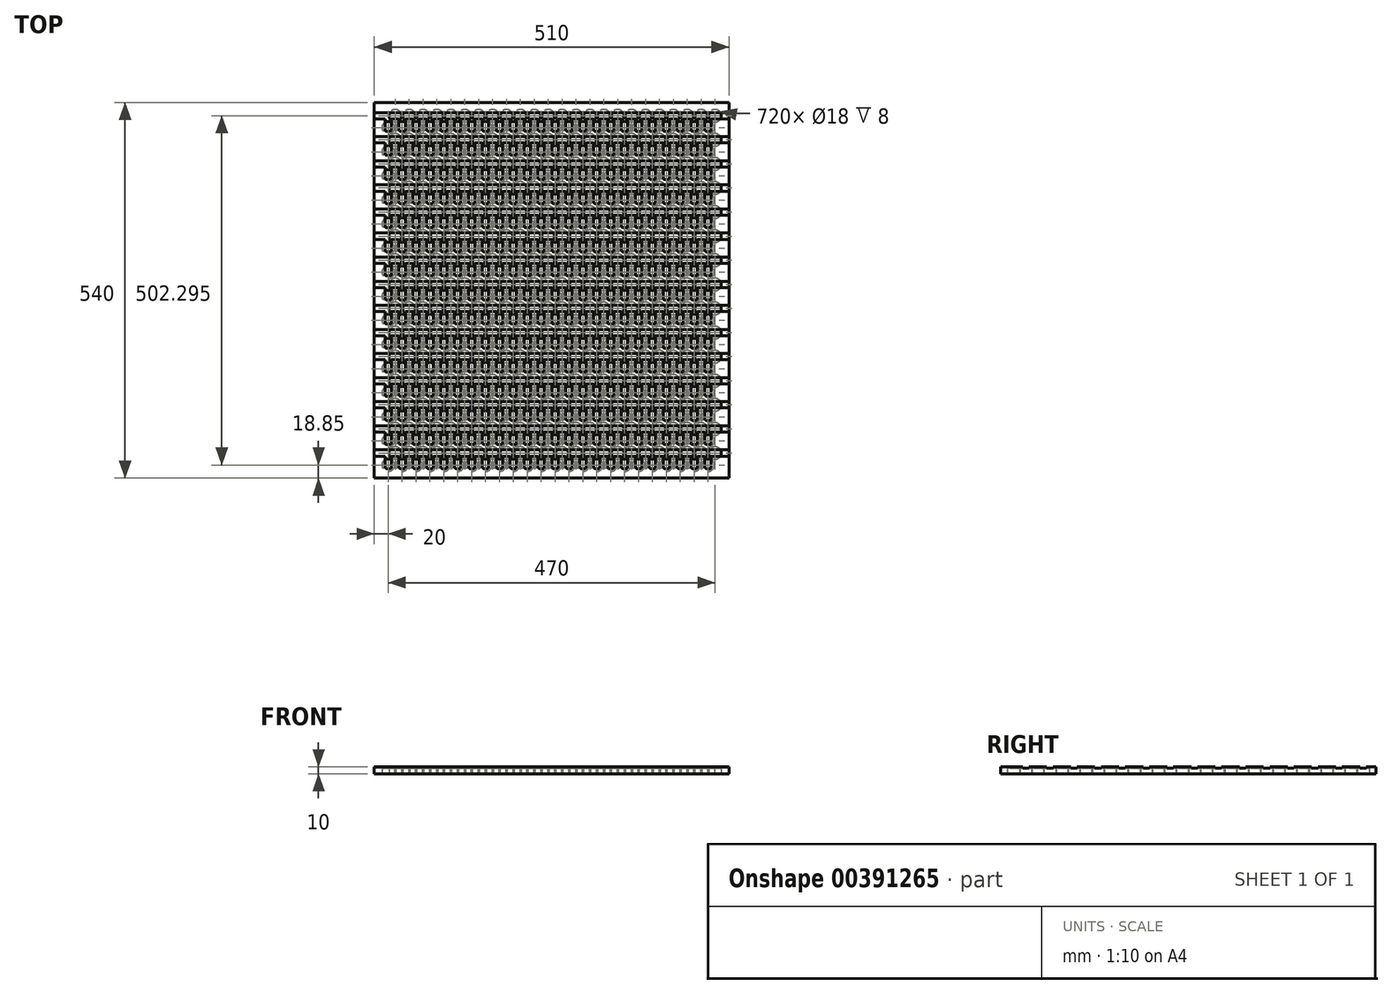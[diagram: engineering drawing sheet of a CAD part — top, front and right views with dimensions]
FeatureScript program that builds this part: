
annotation { "Feature Type Name" : "Feature", "Feature Type Description" : "" }
export const myFeature = defineFeature(function(context is Context, id is Id, definition is map)
    precondition{}
    {
        {
            var Q0;
            Q0=qCreatedBy(makeId("Top.planeOp"),FACE);
            var sketch = newSketch(context, id + "F0", { "sketchPlane" : qUnion([Q0])});
            skCircle(sketch, "E0", {"center": v(0, 0) * mm, "radius": 9 * mm});
            skCircle(sketch, "E1.1.0.0", {"center": v(20, 0) * mm, "radius": 9 * mm});
            skCircle(sketch, "E1.2.0.0", {"center": v(40, 0) * mm, "radius": 9 * mm});
            skCircle(sketch, "E1.3.0.0", {"center": v(60, 0) * mm, "radius": 9 * mm});
            skCircle(sketch, "E1.4.0.0", {"center": v(80, 0) * mm, "radius": 9 * mm});
            skCircle(sketch, "E1.5.0.0", {"center": v(100, 0) * mm, "radius": 9 * mm});
            skCircle(sketch, "E1.6.0.0", {"center": v(120, 0) * mm, "radius": 9 * mm});
            skCircle(sketch, "E1.7.0.0", {"center": v(140, 0) * mm, "radius": 9 * mm});
            skCircle(sketch, "E1.8.0.0", {"center": v(160, 0) * mm, "radius": 9 * mm});
            skCircle(sketch, "E1.9.0.0", {"center": v(180, 0) * mm, "radius": 9 * mm});
            skCircle(sketch, "E1.10.0.0", {"center": v(200, 0) * mm, "radius": 9 * mm});
            skCircle(sketch, "E1.11.0.0", {"center": v(220, 0) * mm, "radius": 9 * mm});
            skCircle(sketch, "E1.12.0.0", {"center": v(240, 0) * mm, "radius": 9 * mm});
            skCircle(sketch, "E1.13.0.0", {"center": v(260, 0) * mm, "radius": 9 * mm});
            skCircle(sketch, "E1.14.0.0", {"center": v(280, 0) * mm, "radius": 9 * mm});
            skCircle(sketch, "E1.15.0.0", {"center": v(300, 0) * mm, "radius": 9 * mm});
            skCircle(sketch, "E1.16.0.0", {"center": v(320, 0) * mm, "radius": 9 * mm});
            skCircle(sketch, "E1.17.0.0", {"center": v(340, 0) * mm, "radius": 9 * mm});
            skCircle(sketch, "E1.18.0.0", {"center": v(360, 0) * mm, "radius": 9 * mm});
            skCircle(sketch, "E1.19.0.0", {"center": v(380, 0) * mm, "radius": 9 * mm});
            skCircle(sketch, "E1.20.0.0", {"center": v(400, 0) * mm, "radius": 9 * mm});
            skCircle(sketch, "E1.21.0.0", {"center": v(420, 0) * mm, "radius": 9 * mm});
            skCircle(sketch, "E1.22.0.0", {"center": v(440, 0) * mm, "radius": 9 * mm});
            skCircle(sketch, "E1.23.0.0", {"center": v(460, 0) * mm, "radius": 9 * mm});
            skLineSegment(sketch, "E1.direction1", {"start": v(0, 0) * mm, "end": v(20, 0) * mm, "construction": true});
            skCircle(sketch, "E2", {"center": v(10, 17.32) * mm, "radius": 9 * mm});
            skCircle(sketch, "E3.1.0.0", {"center": v(30, 17.32) * mm, "radius": 9 * mm});
            skCircle(sketch, "E3.2.0.0", {"center": v(50, 17.32) * mm, "radius": 9 * mm});
            skCircle(sketch, "E3.3.0.0", {"center": v(70, 17.32) * mm, "radius": 9 * mm});
            skCircle(sketch, "E3.4.0.0", {"center": v(90, 17.32) * mm, "radius": 9 * mm});
            skCircle(sketch, "E3.5.0.0", {"center": v(110, 17.32) * mm, "radius": 9 * mm});
            skCircle(sketch, "E3.6.0.0", {"center": v(130, 17.32) * mm, "radius": 9 * mm});
            skCircle(sketch, "E3.7.0.0", {"center": v(150, 17.32) * mm, "radius": 9 * mm});
            skCircle(sketch, "E3.8.0.0", {"center": v(170, 17.32) * mm, "radius": 9 * mm});
            skCircle(sketch, "E3.9.0.0", {"center": v(190, 17.32) * mm, "radius": 9 * mm});
            skCircle(sketch, "E3.10.0.0", {"center": v(210, 17.32) * mm, "radius": 9 * mm});
            skCircle(sketch, "E3.11.0.0", {"center": v(230, 17.32) * mm, "radius": 9 * mm});
            skCircle(sketch, "E3.12.0.0", {"center": v(250, 17.32) * mm, "radius": 9 * mm});
            skCircle(sketch, "E3.13.0.0", {"center": v(270, 17.32) * mm, "radius": 9 * mm});
            skCircle(sketch, "E3.14.0.0", {"center": v(290, 17.32) * mm, "radius": 9 * mm});
            skCircle(sketch, "E3.15.0.0", {"center": v(310, 17.32) * mm, "radius": 9 * mm});
            skCircle(sketch, "E3.16.0.0", {"center": v(330, 17.32) * mm, "radius": 9 * mm});
            skCircle(sketch, "E3.17.0.0", {"center": v(350, 17.32) * mm, "radius": 9 * mm});
            skCircle(sketch, "E3.18.0.0", {"center": v(370, 17.32) * mm, "radius": 9 * mm});
            skCircle(sketch, "E3.19.0.0", {"center": v(390, 17.32) * mm, "radius": 9 * mm});
            skCircle(sketch, "E3.20.0.0", {"center": v(410, 17.32) * mm, "radius": 9 * mm});
            skCircle(sketch, "E3.21.0.0", {"center": v(430, 17.32) * mm, "radius": 9 * mm});
            skCircle(sketch, "E3.22.0.0", {"center": v(450, 17.32) * mm, "radius": 9 * mm});
            skCircle(sketch, "E3.23.0.0", {"center": v(470, 17.32) * mm, "radius": 9 * mm});
            skLineSegment(sketch, "E3.direction1", {"start": v(10, 17.32) * mm, "end": v(30, 17.32) * mm, "construction": true});
            skCircle(sketch, "E4.0.1.0", {"center": v(280, 34.64) * mm, "radius": 9 * mm});
            skCircle(sketch, "E4.0.1.1", {"center": v(260, 34.64) * mm, "radius": 9 * mm});
            skCircle(sketch, "E4.0.1.2", {"center": v(130, 51.96) * mm, "radius": 9 * mm});
            skCircle(sketch, "E4.0.1.3", {"center": v(60, 34.64) * mm, "radius": 9 * mm});
            skCircle(sketch, "E4.0.1.4", {"center": v(80, 34.64) * mm, "radius": 9 * mm});
            skCircle(sketch, "E4.0.1.5", {"center": v(100, 34.64) * mm, "radius": 9 * mm});
            skCircle(sketch, "E4.0.1.6", {"center": v(350, 51.96) * mm, "radius": 9 * mm});
            skCircle(sketch, "E4.0.1.7", {"center": v(0, 34.64) * mm, "radius": 9 * mm});
            skCircle(sketch, "E4.0.1.8", {"center": v(120, 34.64) * mm, "radius": 9 * mm});
            skCircle(sketch, "E4.0.1.9", {"center": v(30, 51.96) * mm, "radius": 9 * mm});
            skCircle(sketch, "E4.0.1.10", {"center": v(380, 34.64) * mm, "radius": 9 * mm});
            skCircle(sketch, "E4.0.1.11", {"center": v(140, 34.64) * mm, "radius": 9 * mm});
            skCircle(sketch, "E4.0.1.12", {"center": v(450, 51.96) * mm, "radius": 9 * mm});
            skCircle(sketch, "E4.0.1.13", {"center": v(160, 34.64) * mm, "radius": 9 * mm});
            skCircle(sketch, "E4.0.1.14", {"center": v(300, 34.64) * mm, "radius": 9 * mm});
            skCircle(sketch, "E4.0.1.15", {"center": v(40, 34.64) * mm, "radius": 9 * mm});
            skCircle(sketch, "E4.0.1.16", {"center": v(210, 51.96) * mm, "radius": 9 * mm});
            skCircle(sketch, "E4.0.1.17", {"center": v(330, 51.96) * mm, "radius": 9 * mm});
            skCircle(sketch, "E4.0.1.18", {"center": v(270, 51.96) * mm, "radius": 9 * mm});
            skCircle(sketch, "E4.0.1.19", {"center": v(440, 34.64) * mm, "radius": 9 * mm});
            skCircle(sketch, "E4.0.1.20", {"center": v(110, 51.96) * mm, "radius": 9 * mm});
            skCircle(sketch, "E4.0.1.21", {"center": v(250, 51.96) * mm, "radius": 9 * mm});
            skCircle(sketch, "E4.0.1.22", {"center": v(180, 34.64) * mm, "radius": 9 * mm});
            skCircle(sketch, "E4.0.1.23", {"center": v(430, 51.96) * mm, "radius": 9 * mm});
            skCircle(sketch, "E4.0.1.24", {"center": v(200, 34.64) * mm, "radius": 9 * mm});
            skCircle(sketch, "E4.0.1.25", {"center": v(420, 34.64) * mm, "radius": 9 * mm});
            skCircle(sketch, "E4.0.1.26", {"center": v(70, 51.96) * mm, "radius": 9 * mm});
            skCircle(sketch, "E4.0.1.27", {"center": v(390, 51.96) * mm, "radius": 9 * mm});
            skCircle(sketch, "E4.0.1.28", {"center": v(220, 34.64) * mm, "radius": 9 * mm});
            skCircle(sketch, "E4.0.1.29", {"center": v(190, 51.96) * mm, "radius": 9 * mm});
            skCircle(sketch, "E4.0.1.30", {"center": v(90, 51.96) * mm, "radius": 9 * mm});
            skCircle(sketch, "E4.0.1.31", {"center": v(230, 51.96) * mm, "radius": 9 * mm});
            skCircle(sketch, "E4.0.1.32", {"center": v(150, 51.96) * mm, "radius": 9 * mm});
            skCircle(sketch, "E4.0.1.33", {"center": v(470, 51.96) * mm, "radius": 9 * mm});
            skCircle(sketch, "E4.0.1.34", {"center": v(410, 51.96) * mm, "radius": 9 * mm});
            skCircle(sketch, "E4.0.1.35", {"center": v(50, 51.96) * mm, "radius": 9 * mm});
            skCircle(sketch, "E4.0.1.36", {"center": v(400, 34.64) * mm, "radius": 9 * mm});
            skCircle(sketch, "E4.0.1.37", {"center": v(240, 34.64) * mm, "radius": 9 * mm});
            skCircle(sketch, "E4.0.1.38", {"center": v(320, 34.64) * mm, "radius": 9 * mm});
            skCircle(sketch, "E4.0.1.39", {"center": v(370, 51.96) * mm, "radius": 9 * mm});
            skCircle(sketch, "E4.0.1.40", {"center": v(10, 51.96) * mm, "radius": 9 * mm});
            skCircle(sketch, "E4.0.1.41", {"center": v(290, 51.96) * mm, "radius": 9 * mm});
            skCircle(sketch, "E4.0.1.42", {"center": v(360, 34.64) * mm, "radius": 9 * mm});
            skCircle(sketch, "E4.0.1.43", {"center": v(460, 34.64) * mm, "radius": 9 * mm});
            skCircle(sketch, "E4.0.1.44", {"center": v(310, 51.96) * mm, "radius": 9 * mm});
            skCircle(sketch, "E4.0.1.45", {"center": v(340, 34.64) * mm, "radius": 9 * mm});
            skCircle(sketch, "E4.0.1.46", {"center": v(170, 51.96) * mm, "radius": 9 * mm});
            skCircle(sketch, "E4.0.1.47", {"center": v(20, 34.64) * mm, "radius": 9 * mm});
            skLineSegment(sketch, "E4.0.1.48", {"start": v(0, 34.64) * mm, "end": v(20, 34.64) * mm, "construction": true});
            skLineSegment(sketch, "E4.0.1.49", {"start": v(10, 51.96) * mm, "end": v(30, 51.96) * mm, "construction": true});
            skCircle(sketch, "E4.0.2.0", {"center": v(280, 69.28) * mm, "radius": 9 * mm});
            skCircle(sketch, "E4.0.2.1", {"center": v(260, 69.28) * mm, "radius": 9 * mm});
            skCircle(sketch, "E4.0.2.2", {"center": v(130, 86.6) * mm, "radius": 9 * mm});
            skCircle(sketch, "E4.0.2.3", {"center": v(60, 69.28) * mm, "radius": 9 * mm});
            skCircle(sketch, "E4.0.2.4", {"center": v(80, 69.28) * mm, "radius": 9 * mm});
            skCircle(sketch, "E4.0.2.5", {"center": v(100, 69.28) * mm, "radius": 9 * mm});
            skCircle(sketch, "E4.0.2.6", {"center": v(350, 86.6) * mm, "radius": 9 * mm});
            skCircle(sketch, "E4.0.2.7", {"center": v(0, 69.28) * mm, "radius": 9 * mm});
            skCircle(sketch, "E4.0.2.8", {"center": v(120, 69.28) * mm, "radius": 9 * mm});
            skCircle(sketch, "E4.0.2.9", {"center": v(30, 86.6) * mm, "radius": 9 * mm});
            skCircle(sketch, "E4.0.2.10", {"center": v(380, 69.28) * mm, "radius": 9 * mm});
            skCircle(sketch, "E4.0.2.11", {"center": v(140, 69.28) * mm, "radius": 9 * mm});
            skCircle(sketch, "E4.0.2.12", {"center": v(450, 86.6) * mm, "radius": 9 * mm});
            skCircle(sketch, "E4.0.2.13", {"center": v(160, 69.28) * mm, "radius": 9 * mm});
            skCircle(sketch, "E4.0.2.14", {"center": v(300, 69.28) * mm, "radius": 9 * mm});
            skCircle(sketch, "E4.0.2.15", {"center": v(40, 69.28) * mm, "radius": 9 * mm});
            skCircle(sketch, "E4.0.2.16", {"center": v(210, 86.6) * mm, "radius": 9 * mm});
            skCircle(sketch, "E4.0.2.17", {"center": v(330, 86.6) * mm, "radius": 9 * mm});
            skCircle(sketch, "E4.0.2.18", {"center": v(270, 86.6) * mm, "radius": 9 * mm});
            skCircle(sketch, "E4.0.2.19", {"center": v(440, 69.28) * mm, "radius": 9 * mm});
            skCircle(sketch, "E4.0.2.20", {"center": v(110, 86.6) * mm, "radius": 9 * mm});
            skCircle(sketch, "E4.0.2.21", {"center": v(250, 86.6) * mm, "radius": 9 * mm});
            skCircle(sketch, "E4.0.2.22", {"center": v(180, 69.28) * mm, "radius": 9 * mm});
            skCircle(sketch, "E4.0.2.23", {"center": v(430, 86.6) * mm, "radius": 9 * mm});
            skCircle(sketch, "E4.0.2.24", {"center": v(200, 69.28) * mm, "radius": 9 * mm});
            skCircle(sketch, "E4.0.2.25", {"center": v(420, 69.28) * mm, "radius": 9 * mm});
            skCircle(sketch, "E4.0.2.26", {"center": v(70, 86.6) * mm, "radius": 9 * mm});
            skCircle(sketch, "E4.0.2.27", {"center": v(390, 86.6) * mm, "radius": 9 * mm});
            skCircle(sketch, "E4.0.2.28", {"center": v(220, 69.28) * mm, "radius": 9 * mm});
            skCircle(sketch, "E4.0.2.29", {"center": v(190, 86.6) * mm, "radius": 9 * mm});
            skCircle(sketch, "E4.0.2.30", {"center": v(90, 86.6) * mm, "radius": 9 * mm});
            skCircle(sketch, "E4.0.2.31", {"center": v(230, 86.6) * mm, "radius": 9 * mm});
            skCircle(sketch, "E4.0.2.32", {"center": v(150, 86.6) * mm, "radius": 9 * mm});
            skCircle(sketch, "E4.0.2.33", {"center": v(470, 86.6) * mm, "radius": 9 * mm});
            skCircle(sketch, "E4.0.2.34", {"center": v(410, 86.6) * mm, "radius": 9 * mm});
            skCircle(sketch, "E4.0.2.35", {"center": v(50, 86.6) * mm, "radius": 9 * mm});
            skCircle(sketch, "E4.0.2.36", {"center": v(400, 69.28) * mm, "radius": 9 * mm});
            skCircle(sketch, "E4.0.2.37", {"center": v(240, 69.28) * mm, "radius": 9 * mm});
            skCircle(sketch, "E4.0.2.38", {"center": v(320, 69.28) * mm, "radius": 9 * mm});
            skCircle(sketch, "E4.0.2.39", {"center": v(370, 86.6) * mm, "radius": 9 * mm});
            skCircle(sketch, "E4.0.2.40", {"center": v(10, 86.6) * mm, "radius": 9 * mm});
            skCircle(sketch, "E4.0.2.41", {"center": v(290, 86.6) * mm, "radius": 9 * mm});
            skCircle(sketch, "E4.0.2.42", {"center": v(360, 69.28) * mm, "radius": 9 * mm});
            skCircle(sketch, "E4.0.2.43", {"center": v(460, 69.28) * mm, "radius": 9 * mm});
            skCircle(sketch, "E4.0.2.44", {"center": v(310, 86.6) * mm, "radius": 9 * mm});
            skCircle(sketch, "E4.0.2.45", {"center": v(340, 69.28) * mm, "radius": 9 * mm});
            skCircle(sketch, "E4.0.2.46", {"center": v(170, 86.6) * mm, "radius": 9 * mm});
            skCircle(sketch, "E4.0.2.47", {"center": v(20, 69.28) * mm, "radius": 9 * mm});
            skLineSegment(sketch, "E4.0.2.48", {"start": v(0, 69.28) * mm, "end": v(20, 69.28) * mm, "construction": true});
            skLineSegment(sketch, "E4.0.2.49", {"start": v(10, 86.6) * mm, "end": v(30, 86.6) * mm, "construction": true});
            skCircle(sketch, "E4.0.3.0", {"center": v(280, 103.92) * mm, "radius": 9 * mm});
            skCircle(sketch, "E4.0.3.1", {"center": v(260, 103.92) * mm, "radius": 9 * mm});
            skCircle(sketch, "E4.0.3.2", {"center": v(130, 121.24) * mm, "radius": 9 * mm});
            skCircle(sketch, "E4.0.3.3", {"center": v(60, 103.92) * mm, "radius": 9 * mm});
            skCircle(sketch, "E4.0.3.4", {"center": v(80, 103.92) * mm, "radius": 9 * mm});
            skCircle(sketch, "E4.0.3.5", {"center": v(100, 103.92) * mm, "radius": 9 * mm});
            skCircle(sketch, "E4.0.3.6", {"center": v(350, 121.24) * mm, "radius": 9 * mm});
            skCircle(sketch, "E4.0.3.7", {"center": v(0, 103.92) * mm, "radius": 9 * mm});
            skCircle(sketch, "E4.0.3.8", {"center": v(120, 103.92) * mm, "radius": 9 * mm});
            skCircle(sketch, "E4.0.3.9", {"center": v(30, 121.24) * mm, "radius": 9 * mm});
            skCircle(sketch, "E4.0.3.10", {"center": v(380, 103.92) * mm, "radius": 9 * mm});
            skCircle(sketch, "E4.0.3.11", {"center": v(140, 103.92) * mm, "radius": 9 * mm});
            skCircle(sketch, "E4.0.3.12", {"center": v(450, 121.24) * mm, "radius": 9 * mm});
            skCircle(sketch, "E4.0.3.13", {"center": v(160, 103.92) * mm, "radius": 9 * mm});
            skCircle(sketch, "E4.0.3.14", {"center": v(300, 103.92) * mm, "radius": 9 * mm});
            skCircle(sketch, "E4.0.3.15", {"center": v(40, 103.92) * mm, "radius": 9 * mm});
            skCircle(sketch, "E4.0.3.16", {"center": v(210, 121.24) * mm, "radius": 9 * mm});
            skCircle(sketch, "E4.0.3.17", {"center": v(330, 121.24) * mm, "radius": 9 * mm});
            skCircle(sketch, "E4.0.3.18", {"center": v(270, 121.24) * mm, "radius": 9 * mm});
            skCircle(sketch, "E4.0.3.19", {"center": v(440, 103.92) * mm, "radius": 9 * mm});
            skCircle(sketch, "E4.0.3.20", {"center": v(110, 121.24) * mm, "radius": 9 * mm});
            skCircle(sketch, "E4.0.3.21", {"center": v(250, 121.24) * mm, "radius": 9 * mm});
            skCircle(sketch, "E4.0.3.22", {"center": v(180, 103.92) * mm, "radius": 9 * mm});
            skCircle(sketch, "E4.0.3.23", {"center": v(430, 121.24) * mm, "radius": 9 * mm});
            skCircle(sketch, "E4.0.3.24", {"center": v(200, 103.92) * mm, "radius": 9 * mm});
            skCircle(sketch, "E4.0.3.25", {"center": v(420, 103.92) * mm, "radius": 9 * mm});
            skCircle(sketch, "E4.0.3.26", {"center": v(70, 121.24) * mm, "radius": 9 * mm});
            skCircle(sketch, "E4.0.3.27", {"center": v(390, 121.24) * mm, "radius": 9 * mm});
            skCircle(sketch, "E4.0.3.28", {"center": v(220, 103.92) * mm, "radius": 9 * mm});
            skCircle(sketch, "E4.0.3.29", {"center": v(190, 121.24) * mm, "radius": 9 * mm});
            skCircle(sketch, "E4.0.3.30", {"center": v(90, 121.24) * mm, "radius": 9 * mm});
            skCircle(sketch, "E4.0.3.31", {"center": v(230, 121.24) * mm, "radius": 9 * mm});
            skCircle(sketch, "E4.0.3.32", {"center": v(150, 121.24) * mm, "radius": 9 * mm});
            skCircle(sketch, "E4.0.3.33", {"center": v(470, 121.24) * mm, "radius": 9 * mm});
            skCircle(sketch, "E4.0.3.34", {"center": v(410, 121.24) * mm, "radius": 9 * mm});
            skCircle(sketch, "E4.0.3.35", {"center": v(50, 121.24) * mm, "radius": 9 * mm});
            skCircle(sketch, "E4.0.3.36", {"center": v(400, 103.92) * mm, "radius": 9 * mm});
            skCircle(sketch, "E4.0.3.37", {"center": v(240, 103.92) * mm, "radius": 9 * mm});
            skCircle(sketch, "E4.0.3.38", {"center": v(320, 103.92) * mm, "radius": 9 * mm});
            skCircle(sketch, "E4.0.3.39", {"center": v(370, 121.24) * mm, "radius": 9 * mm});
            skCircle(sketch, "E4.0.3.40", {"center": v(10, 121.24) * mm, "radius": 9 * mm});
            skCircle(sketch, "E4.0.3.41", {"center": v(290, 121.24) * mm, "radius": 9 * mm});
            skCircle(sketch, "E4.0.3.42", {"center": v(360, 103.92) * mm, "radius": 9 * mm});
            skCircle(sketch, "E4.0.3.43", {"center": v(460, 103.92) * mm, "radius": 9 * mm});
            skCircle(sketch, "E4.0.3.44", {"center": v(310, 121.24) * mm, "radius": 9 * mm});
            skCircle(sketch, "E4.0.3.45", {"center": v(340, 103.92) * mm, "radius": 9 * mm});
            skCircle(sketch, "E4.0.3.46", {"center": v(170, 121.24) * mm, "radius": 9 * mm});
            skCircle(sketch, "E4.0.3.47", {"center": v(20, 103.92) * mm, "radius": 9 * mm});
            skLineSegment(sketch, "E4.0.3.48", {"start": v(0, 103.92) * mm, "end": v(20, 103.92) * mm, "construction": true});
            skLineSegment(sketch, "E4.0.3.49", {"start": v(10, 121.24) * mm, "end": v(30, 121.24) * mm, "construction": true});
            skCircle(sketch, "E4.0.4.0", {"center": v(280, 138.56) * mm, "radius": 9 * mm});
            skCircle(sketch, "E4.0.4.1", {"center": v(260, 138.56) * mm, "radius": 9 * mm});
            skCircle(sketch, "E4.0.4.2", {"center": v(130, 155.88) * mm, "radius": 9 * mm});
            skCircle(sketch, "E4.0.4.3", {"center": v(60, 138.56) * mm, "radius": 9 * mm});
            skCircle(sketch, "E4.0.4.4", {"center": v(80, 138.56) * mm, "radius": 9 * mm});
            skCircle(sketch, "E4.0.4.5", {"center": v(100, 138.56) * mm, "radius": 9 * mm});
            skCircle(sketch, "E4.0.4.6", {"center": v(350, 155.88) * mm, "radius": 9 * mm});
            skCircle(sketch, "E4.0.4.7", {"center": v(0, 138.56) * mm, "radius": 9 * mm});
            skCircle(sketch, "E4.0.4.8", {"center": v(120, 138.56) * mm, "radius": 9 * mm});
            skCircle(sketch, "E4.0.4.9", {"center": v(30, 155.88) * mm, "radius": 9 * mm});
            skCircle(sketch, "E4.0.4.10", {"center": v(380, 138.56) * mm, "radius": 9 * mm});
            skCircle(sketch, "E4.0.4.11", {"center": v(140, 138.56) * mm, "radius": 9 * mm});
            skCircle(sketch, "E4.0.4.12", {"center": v(450, 155.88) * mm, "radius": 9 * mm});
            skCircle(sketch, "E4.0.4.13", {"center": v(160, 138.56) * mm, "radius": 9 * mm});
            skCircle(sketch, "E4.0.4.14", {"center": v(300, 138.56) * mm, "radius": 9 * mm});
            skCircle(sketch, "E4.0.4.15", {"center": v(40, 138.56) * mm, "radius": 9 * mm});
            skCircle(sketch, "E4.0.4.16", {"center": v(210, 155.88) * mm, "radius": 9 * mm});
            skCircle(sketch, "E4.0.4.17", {"center": v(330, 155.88) * mm, "radius": 9 * mm});
            skCircle(sketch, "E4.0.4.18", {"center": v(270, 155.88) * mm, "radius": 9 * mm});
            skCircle(sketch, "E4.0.4.19", {"center": v(440, 138.56) * mm, "radius": 9 * mm});
            skCircle(sketch, "E4.0.4.20", {"center": v(110, 155.88) * mm, "radius": 9 * mm});
            skCircle(sketch, "E4.0.4.21", {"center": v(250, 155.88) * mm, "radius": 9 * mm});
            skCircle(sketch, "E4.0.4.22", {"center": v(180, 138.56) * mm, "radius": 9 * mm});
            skCircle(sketch, "E4.0.4.23", {"center": v(430, 155.88) * mm, "radius": 9 * mm});
            skCircle(sketch, "E4.0.4.24", {"center": v(200, 138.56) * mm, "radius": 9 * mm});
            skCircle(sketch, "E4.0.4.25", {"center": v(420, 138.56) * mm, "radius": 9 * mm});
            skCircle(sketch, "E4.0.4.26", {"center": v(70, 155.88) * mm, "radius": 9 * mm});
            skCircle(sketch, "E4.0.4.27", {"center": v(390, 155.88) * mm, "radius": 9 * mm});
            skCircle(sketch, "E4.0.4.28", {"center": v(220, 138.56) * mm, "radius": 9 * mm});
            skCircle(sketch, "E4.0.4.29", {"center": v(190, 155.88) * mm, "radius": 9 * mm});
            skCircle(sketch, "E4.0.4.30", {"center": v(90, 155.88) * mm, "radius": 9 * mm});
            skCircle(sketch, "E4.0.4.31", {"center": v(230, 155.88) * mm, "radius": 9 * mm});
            skCircle(sketch, "E4.0.4.32", {"center": v(150, 155.88) * mm, "radius": 9 * mm});
            skCircle(sketch, "E4.0.4.33", {"center": v(470, 155.88) * mm, "radius": 9 * mm});
            skCircle(sketch, "E4.0.4.34", {"center": v(410, 155.88) * mm, "radius": 9 * mm});
            skCircle(sketch, "E4.0.4.35", {"center": v(50, 155.88) * mm, "radius": 9 * mm});
            skCircle(sketch, "E4.0.4.36", {"center": v(400, 138.56) * mm, "radius": 9 * mm});
            skCircle(sketch, "E4.0.4.37", {"center": v(240, 138.56) * mm, "radius": 9 * mm});
            skCircle(sketch, "E4.0.4.38", {"center": v(320, 138.56) * mm, "radius": 9 * mm});
            skCircle(sketch, "E4.0.4.39", {"center": v(370, 155.88) * mm, "radius": 9 * mm});
            skCircle(sketch, "E4.0.4.40", {"center": v(10, 155.88) * mm, "radius": 9 * mm});
            skCircle(sketch, "E4.0.4.41", {"center": v(290, 155.88) * mm, "radius": 9 * mm});
            skCircle(sketch, "E4.0.4.42", {"center": v(360, 138.56) * mm, "radius": 9 * mm});
            skCircle(sketch, "E4.0.4.43", {"center": v(460, 138.56) * mm, "radius": 9 * mm});
            skCircle(sketch, "E4.0.4.44", {"center": v(310, 155.88) * mm, "radius": 9 * mm});
            skCircle(sketch, "E4.0.4.45", {"center": v(340, 138.56) * mm, "radius": 9 * mm});
            skCircle(sketch, "E4.0.4.46", {"center": v(170, 155.88) * mm, "radius": 9 * mm});
            skCircle(sketch, "E4.0.4.47", {"center": v(20, 138.56) * mm, "radius": 9 * mm});
            skLineSegment(sketch, "E4.0.4.48", {"start": v(0, 138.56) * mm, "end": v(20, 138.56) * mm, "construction": true});
            skLineSegment(sketch, "E4.0.4.49", {"start": v(10, 155.88) * mm, "end": v(30, 155.88) * mm, "construction": true});
            skCircle(sketch, "E4.0.5.0", {"center": v(280, 173.2) * mm, "radius": 9 * mm});
            skCircle(sketch, "E4.0.5.1", {"center": v(260, 173.2) * mm, "radius": 9 * mm});
            skCircle(sketch, "E4.0.5.2", {"center": v(130, 190.53) * mm, "radius": 9 * mm});
            skCircle(sketch, "E4.0.5.3", {"center": v(60, 173.2) * mm, "radius": 9 * mm});
            skCircle(sketch, "E4.0.5.4", {"center": v(80, 173.2) * mm, "radius": 9 * mm});
            skCircle(sketch, "E4.0.5.5", {"center": v(100, 173.2) * mm, "radius": 9 * mm});
            skCircle(sketch, "E4.0.5.6", {"center": v(350, 190.53) * mm, "radius": 9 * mm});
            skCircle(sketch, "E4.0.5.7", {"center": v(0, 173.2) * mm, "radius": 9 * mm});
            skCircle(sketch, "E4.0.5.8", {"center": v(120, 173.2) * mm, "radius": 9 * mm});
            skCircle(sketch, "E4.0.5.9", {"center": v(30, 190.53) * mm, "radius": 9 * mm});
            skCircle(sketch, "E4.0.5.10", {"center": v(380, 173.2) * mm, "radius": 9 * mm});
            skCircle(sketch, "E4.0.5.11", {"center": v(140, 173.2) * mm, "radius": 9 * mm});
            skCircle(sketch, "E4.0.5.12", {"center": v(450, 190.53) * mm, "radius": 9 * mm});
            skCircle(sketch, "E4.0.5.13", {"center": v(160, 173.2) * mm, "radius": 9 * mm});
            skCircle(sketch, "E4.0.5.14", {"center": v(300, 173.2) * mm, "radius": 9 * mm});
            skCircle(sketch, "E4.0.5.15", {"center": v(40, 173.2) * mm, "radius": 9 * mm});
            skCircle(sketch, "E4.0.5.16", {"center": v(210, 190.53) * mm, "radius": 9 * mm});
            skCircle(sketch, "E4.0.5.17", {"center": v(330, 190.53) * mm, "radius": 9 * mm});
            skCircle(sketch, "E4.0.5.18", {"center": v(270, 190.53) * mm, "radius": 9 * mm});
            skCircle(sketch, "E4.0.5.19", {"center": v(440, 173.2) * mm, "radius": 9 * mm});
            skCircle(sketch, "E4.0.5.20", {"center": v(110, 190.53) * mm, "radius": 9 * mm});
            skCircle(sketch, "E4.0.5.21", {"center": v(250, 190.53) * mm, "radius": 9 * mm});
            skCircle(sketch, "E4.0.5.22", {"center": v(180, 173.2) * mm, "radius": 9 * mm});
            skCircle(sketch, "E4.0.5.23", {"center": v(430, 190.53) * mm, "radius": 9 * mm});
            skCircle(sketch, "E4.0.5.24", {"center": v(200, 173.2) * mm, "radius": 9 * mm});
            skCircle(sketch, "E4.0.5.25", {"center": v(420, 173.2) * mm, "radius": 9 * mm});
            skCircle(sketch, "E4.0.5.26", {"center": v(70, 190.53) * mm, "radius": 9 * mm});
            skCircle(sketch, "E4.0.5.27", {"center": v(390, 190.53) * mm, "radius": 9 * mm});
            skCircle(sketch, "E4.0.5.28", {"center": v(220, 173.2) * mm, "radius": 9 * mm});
            skCircle(sketch, "E4.0.5.29", {"center": v(190, 190.53) * mm, "radius": 9 * mm});
            skCircle(sketch, "E4.0.5.30", {"center": v(90, 190.53) * mm, "radius": 9 * mm});
            skCircle(sketch, "E4.0.5.31", {"center": v(230, 190.53) * mm, "radius": 9 * mm});
            skCircle(sketch, "E4.0.5.32", {"center": v(150, 190.53) * mm, "radius": 9 * mm});
            skCircle(sketch, "E4.0.5.33", {"center": v(470, 190.53) * mm, "radius": 9 * mm});
            skCircle(sketch, "E4.0.5.34", {"center": v(410, 190.53) * mm, "radius": 9 * mm});
            skCircle(sketch, "E4.0.5.35", {"center": v(50, 190.53) * mm, "radius": 9 * mm});
            skCircle(sketch, "E4.0.5.36", {"center": v(400, 173.2) * mm, "radius": 9 * mm});
            skCircle(sketch, "E4.0.5.37", {"center": v(240, 173.2) * mm, "radius": 9 * mm});
            skCircle(sketch, "E4.0.5.38", {"center": v(320, 173.2) * mm, "radius": 9 * mm});
            skCircle(sketch, "E4.0.5.39", {"center": v(370, 190.53) * mm, "radius": 9 * mm});
            skCircle(sketch, "E4.0.5.40", {"center": v(10, 190.53) * mm, "radius": 9 * mm});
            skCircle(sketch, "E4.0.5.41", {"center": v(290, 190.53) * mm, "radius": 9 * mm});
            skCircle(sketch, "E4.0.5.42", {"center": v(360, 173.2) * mm, "radius": 9 * mm});
            skCircle(sketch, "E4.0.5.43", {"center": v(460, 173.2) * mm, "radius": 9 * mm});
            skCircle(sketch, "E4.0.5.44", {"center": v(310, 190.53) * mm, "radius": 9 * mm});
            skCircle(sketch, "E4.0.5.45", {"center": v(340, 173.2) * mm, "radius": 9 * mm});
            skCircle(sketch, "E4.0.5.46", {"center": v(170, 190.53) * mm, "radius": 9 * mm});
            skCircle(sketch, "E4.0.5.47", {"center": v(20, 173.2) * mm, "radius": 9 * mm});
            skLineSegment(sketch, "E4.0.5.48", {"start": v(0, 173.2) * mm, "end": v(20, 173.2) * mm, "construction": true});
            skLineSegment(sketch, "E4.0.5.49", {"start": v(10, 190.53) * mm, "end": v(30, 190.53) * mm, "construction": true});
            skCircle(sketch, "E4.0.6.0", {"center": v(280, 207.85) * mm, "radius": 9 * mm});
            skCircle(sketch, "E4.0.6.1", {"center": v(260, 207.85) * mm, "radius": 9 * mm});
            skCircle(sketch, "E4.0.6.2", {"center": v(130, 225.17) * mm, "radius": 9 * mm});
            skCircle(sketch, "E4.0.6.3", {"center": v(60, 207.85) * mm, "radius": 9 * mm});
            skCircle(sketch, "E4.0.6.4", {"center": v(80, 207.85) * mm, "radius": 9 * mm});
            skCircle(sketch, "E4.0.6.5", {"center": v(100, 207.85) * mm, "radius": 9 * mm});
            skCircle(sketch, "E4.0.6.6", {"center": v(350, 225.17) * mm, "radius": 9 * mm});
            skCircle(sketch, "E4.0.6.7", {"center": v(0, 207.85) * mm, "radius": 9 * mm});
            skCircle(sketch, "E4.0.6.8", {"center": v(120, 207.85) * mm, "radius": 9 * mm});
            skCircle(sketch, "E4.0.6.9", {"center": v(30, 225.17) * mm, "radius": 9 * mm});
            skCircle(sketch, "E4.0.6.10", {"center": v(380, 207.85) * mm, "radius": 9 * mm});
            skCircle(sketch, "E4.0.6.11", {"center": v(140, 207.85) * mm, "radius": 9 * mm});
            skCircle(sketch, "E4.0.6.12", {"center": v(450, 225.17) * mm, "radius": 9 * mm});
            skCircle(sketch, "E4.0.6.13", {"center": v(160, 207.85) * mm, "radius": 9 * mm});
            skCircle(sketch, "E4.0.6.14", {"center": v(300, 207.85) * mm, "radius": 9 * mm});
            skCircle(sketch, "E4.0.6.15", {"center": v(40, 207.85) * mm, "radius": 9 * mm});
            skCircle(sketch, "E4.0.6.16", {"center": v(210, 225.17) * mm, "radius": 9 * mm});
            skCircle(sketch, "E4.0.6.17", {"center": v(330, 225.17) * mm, "radius": 9 * mm});
            skCircle(sketch, "E4.0.6.18", {"center": v(270, 225.17) * mm, "radius": 9 * mm});
            skCircle(sketch, "E4.0.6.19", {"center": v(440, 207.85) * mm, "radius": 9 * mm});
            skCircle(sketch, "E4.0.6.20", {"center": v(110, 225.17) * mm, "radius": 9 * mm});
            skCircle(sketch, "E4.0.6.21", {"center": v(250, 225.17) * mm, "radius": 9 * mm});
            skCircle(sketch, "E4.0.6.22", {"center": v(180, 207.85) * mm, "radius": 9 * mm});
            skCircle(sketch, "E4.0.6.23", {"center": v(430, 225.17) * mm, "radius": 9 * mm});
            skCircle(sketch, "E4.0.6.24", {"center": v(200, 207.85) * mm, "radius": 9 * mm});
            skCircle(sketch, "E4.0.6.25", {"center": v(420, 207.85) * mm, "radius": 9 * mm});
            skCircle(sketch, "E4.0.6.26", {"center": v(70, 225.17) * mm, "radius": 9 * mm});
            skCircle(sketch, "E4.0.6.27", {"center": v(390, 225.17) * mm, "radius": 9 * mm});
            skCircle(sketch, "E4.0.6.28", {"center": v(220, 207.85) * mm, "radius": 9 * mm});
            skCircle(sketch, "E4.0.6.29", {"center": v(190, 225.17) * mm, "radius": 9 * mm});
            skCircle(sketch, "E4.0.6.30", {"center": v(90, 225.17) * mm, "radius": 9 * mm});
            skCircle(sketch, "E4.0.6.31", {"center": v(230, 225.17) * mm, "radius": 9 * mm});
            skCircle(sketch, "E4.0.6.32", {"center": v(150, 225.17) * mm, "radius": 9 * mm});
            skCircle(sketch, "E4.0.6.33", {"center": v(470, 225.17) * mm, "radius": 9 * mm});
            skCircle(sketch, "E4.0.6.34", {"center": v(410, 225.17) * mm, "radius": 9 * mm});
            skCircle(sketch, "E4.0.6.35", {"center": v(50, 225.17) * mm, "radius": 9 * mm});
            skCircle(sketch, "E4.0.6.36", {"center": v(400, 207.85) * mm, "radius": 9 * mm});
            skCircle(sketch, "E4.0.6.37", {"center": v(240, 207.85) * mm, "radius": 9 * mm});
            skCircle(sketch, "E4.0.6.38", {"center": v(320, 207.85) * mm, "radius": 9 * mm});
            skCircle(sketch, "E4.0.6.39", {"center": v(370, 225.17) * mm, "radius": 9 * mm});
            skCircle(sketch, "E4.0.6.40", {"center": v(10, 225.17) * mm, "radius": 9 * mm});
            skCircle(sketch, "E4.0.6.41", {"center": v(290, 225.17) * mm, "radius": 9 * mm});
            skCircle(sketch, "E4.0.6.42", {"center": v(360, 207.85) * mm, "radius": 9 * mm});
            skCircle(sketch, "E4.0.6.43", {"center": v(460, 207.85) * mm, "radius": 9 * mm});
            skCircle(sketch, "E4.0.6.44", {"center": v(310, 225.17) * mm, "radius": 9 * mm});
            skCircle(sketch, "E4.0.6.45", {"center": v(340, 207.85) * mm, "radius": 9 * mm});
            skCircle(sketch, "E4.0.6.46", {"center": v(170, 225.17) * mm, "radius": 9 * mm});
            skCircle(sketch, "E4.0.6.47", {"center": v(20, 207.85) * mm, "radius": 9 * mm});
            skLineSegment(sketch, "E4.0.6.48", {"start": v(0, 207.85) * mm, "end": v(20, 207.85) * mm, "construction": true});
            skLineSegment(sketch, "E4.0.6.49", {"start": v(10, 225.17) * mm, "end": v(30, 225.17) * mm, "construction": true});
            skCircle(sketch, "E4.0.7.0", {"center": v(280, 242.49) * mm, "radius": 9 * mm});
            skCircle(sketch, "E4.0.7.1", {"center": v(260, 242.49) * mm, "radius": 9 * mm});
            skCircle(sketch, "E4.0.7.2", {"center": v(130, 259.8) * mm, "radius": 9 * mm});
            skCircle(sketch, "E4.0.7.3", {"center": v(60, 242.49) * mm, "radius": 9 * mm});
            skCircle(sketch, "E4.0.7.4", {"center": v(80, 242.49) * mm, "radius": 9 * mm});
            skCircle(sketch, "E4.0.7.5", {"center": v(100, 242.49) * mm, "radius": 9 * mm});
            skCircle(sketch, "E4.0.7.6", {"center": v(350, 259.8) * mm, "radius": 9 * mm});
            skCircle(sketch, "E4.0.7.7", {"center": v(0, 242.49) * mm, "radius": 9 * mm});
            skCircle(sketch, "E4.0.7.8", {"center": v(120, 242.49) * mm, "radius": 9 * mm});
            skCircle(sketch, "E4.0.7.9", {"center": v(30, 259.8) * mm, "radius": 9 * mm});
            skCircle(sketch, "E4.0.7.10", {"center": v(380, 242.49) * mm, "radius": 9 * mm});
            skCircle(sketch, "E4.0.7.11", {"center": v(140, 242.49) * mm, "radius": 9 * mm});
            skCircle(sketch, "E4.0.7.12", {"center": v(450, 259.8) * mm, "radius": 9 * mm});
            skCircle(sketch, "E4.0.7.13", {"center": v(160, 242.49) * mm, "radius": 9 * mm});
            skCircle(sketch, "E4.0.7.14", {"center": v(300, 242.49) * mm, "radius": 9 * mm});
            skCircle(sketch, "E4.0.7.15", {"center": v(40, 242.49) * mm, "radius": 9 * mm});
            skCircle(sketch, "E4.0.7.16", {"center": v(210, 259.8) * mm, "radius": 9 * mm});
            skCircle(sketch, "E4.0.7.17", {"center": v(330, 259.8) * mm, "radius": 9 * mm});
            skCircle(sketch, "E4.0.7.18", {"center": v(270, 259.8) * mm, "radius": 9 * mm});
            skCircle(sketch, "E4.0.7.19", {"center": v(440, 242.49) * mm, "radius": 9 * mm});
            skCircle(sketch, "E4.0.7.20", {"center": v(110, 259.8) * mm, "radius": 9 * mm});
            skCircle(sketch, "E4.0.7.21", {"center": v(250, 259.8) * mm, "radius": 9 * mm});
            skCircle(sketch, "E4.0.7.22", {"center": v(180, 242.49) * mm, "radius": 9 * mm});
            skCircle(sketch, "E4.0.7.23", {"center": v(430, 259.8) * mm, "radius": 9 * mm});
            skCircle(sketch, "E4.0.7.24", {"center": v(200, 242.49) * mm, "radius": 9 * mm});
            skCircle(sketch, "E4.0.7.25", {"center": v(420, 242.49) * mm, "radius": 9 * mm});
            skCircle(sketch, "E4.0.7.26", {"center": v(70, 259.8) * mm, "radius": 9 * mm});
            skCircle(sketch, "E4.0.7.27", {"center": v(390, 259.8) * mm, "radius": 9 * mm});
            skCircle(sketch, "E4.0.7.28", {"center": v(220, 242.49) * mm, "radius": 9 * mm});
            skCircle(sketch, "E4.0.7.29", {"center": v(190, 259.8) * mm, "radius": 9 * mm});
            skCircle(sketch, "E4.0.7.30", {"center": v(90, 259.8) * mm, "radius": 9 * mm});
            skCircle(sketch, "E4.0.7.31", {"center": v(230, 259.8) * mm, "radius": 9 * mm});
            skCircle(sketch, "E4.0.7.32", {"center": v(150, 259.8) * mm, "radius": 9 * mm});
            skCircle(sketch, "E4.0.7.33", {"center": v(470, 259.8) * mm, "radius": 9 * mm});
            skCircle(sketch, "E4.0.7.34", {"center": v(410, 259.8) * mm, "radius": 9 * mm});
            skCircle(sketch, "E4.0.7.35", {"center": v(50, 259.8) * mm, "radius": 9 * mm});
            skCircle(sketch, "E4.0.7.36", {"center": v(400, 242.49) * mm, "radius": 9 * mm});
            skCircle(sketch, "E4.0.7.37", {"center": v(240, 242.49) * mm, "radius": 9 * mm});
            skCircle(sketch, "E4.0.7.38", {"center": v(320, 242.49) * mm, "radius": 9 * mm});
            skCircle(sketch, "E4.0.7.39", {"center": v(370, 259.8) * mm, "radius": 9 * mm});
            skCircle(sketch, "E4.0.7.40", {"center": v(10, 259.8) * mm, "radius": 9 * mm});
            skCircle(sketch, "E4.0.7.41", {"center": v(290, 259.8) * mm, "radius": 9 * mm});
            skCircle(sketch, "E4.0.7.42", {"center": v(360, 242.49) * mm, "radius": 9 * mm});
            skCircle(sketch, "E4.0.7.43", {"center": v(460, 242.49) * mm, "radius": 9 * mm});
            skCircle(sketch, "E4.0.7.44", {"center": v(310, 259.8) * mm, "radius": 9 * mm});
            skCircle(sketch, "E4.0.7.45", {"center": v(340, 242.49) * mm, "radius": 9 * mm});
            skCircle(sketch, "E4.0.7.46", {"center": v(170, 259.8) * mm, "radius": 9 * mm});
            skCircle(sketch, "E4.0.7.47", {"center": v(20, 242.49) * mm, "radius": 9 * mm});
            skLineSegment(sketch, "E4.0.7.48", {"start": v(0, 242.49) * mm, "end": v(20, 242.49) * mm, "construction": true});
            skLineSegment(sketch, "E4.0.7.49", {"start": v(10, 259.8) * mm, "end": v(30, 259.8) * mm, "construction": true});
            skCircle(sketch, "E4.0.8.0", {"center": v(280, 277.13) * mm, "radius": 9 * mm});
            skCircle(sketch, "E4.0.8.1", {"center": v(260, 277.13) * mm, "radius": 9 * mm});
            skCircle(sketch, "E4.0.8.2", {"center": v(130, 294.45) * mm, "radius": 9 * mm});
            skCircle(sketch, "E4.0.8.3", {"center": v(60, 277.13) * mm, "radius": 9 * mm});
            skCircle(sketch, "E4.0.8.4", {"center": v(80, 277.13) * mm, "radius": 9 * mm});
            skCircle(sketch, "E4.0.8.5", {"center": v(100, 277.13) * mm, "radius": 9 * mm});
            skCircle(sketch, "E4.0.8.6", {"center": v(350, 294.45) * mm, "radius": 9 * mm});
            skCircle(sketch, "E4.0.8.7", {"center": v(0, 277.13) * mm, "radius": 9 * mm});
            skCircle(sketch, "E4.0.8.8", {"center": v(120, 277.13) * mm, "radius": 9 * mm});
            skCircle(sketch, "E4.0.8.9", {"center": v(30, 294.45) * mm, "radius": 9 * mm});
            skCircle(sketch, "E4.0.8.10", {"center": v(380, 277.13) * mm, "radius": 9 * mm});
            skCircle(sketch, "E4.0.8.11", {"center": v(140, 277.13) * mm, "radius": 9 * mm});
            skCircle(sketch, "E4.0.8.12", {"center": v(450, 294.45) * mm, "radius": 9 * mm});
            skCircle(sketch, "E4.0.8.13", {"center": v(160, 277.13) * mm, "radius": 9 * mm});
            skCircle(sketch, "E4.0.8.14", {"center": v(300, 277.13) * mm, "radius": 9 * mm});
            skCircle(sketch, "E4.0.8.15", {"center": v(40, 277.13) * mm, "radius": 9 * mm});
            skCircle(sketch, "E4.0.8.16", {"center": v(210, 294.45) * mm, "radius": 9 * mm});
            skCircle(sketch, "E4.0.8.17", {"center": v(330, 294.45) * mm, "radius": 9 * mm});
            skCircle(sketch, "E4.0.8.18", {"center": v(270, 294.45) * mm, "radius": 9 * mm});
            skCircle(sketch, "E4.0.8.19", {"center": v(440, 277.13) * mm, "radius": 9 * mm});
            skCircle(sketch, "E4.0.8.20", {"center": v(110, 294.45) * mm, "radius": 9 * mm});
            skCircle(sketch, "E4.0.8.21", {"center": v(250, 294.45) * mm, "radius": 9 * mm});
            skCircle(sketch, "E4.0.8.22", {"center": v(180, 277.13) * mm, "radius": 9 * mm});
            skCircle(sketch, "E4.0.8.23", {"center": v(430, 294.45) * mm, "radius": 9 * mm});
            skCircle(sketch, "E4.0.8.24", {"center": v(200, 277.13) * mm, "radius": 9 * mm});
            skCircle(sketch, "E4.0.8.25", {"center": v(420, 277.13) * mm, "radius": 9 * mm});
            skCircle(sketch, "E4.0.8.26", {"center": v(70, 294.45) * mm, "radius": 9 * mm});
            skCircle(sketch, "E4.0.8.27", {"center": v(390, 294.45) * mm, "radius": 9 * mm});
            skCircle(sketch, "E4.0.8.28", {"center": v(220, 277.13) * mm, "radius": 9 * mm});
            skCircle(sketch, "E4.0.8.29", {"center": v(190, 294.45) * mm, "radius": 9 * mm});
            skCircle(sketch, "E4.0.8.30", {"center": v(90, 294.45) * mm, "radius": 9 * mm});
            skCircle(sketch, "E4.0.8.31", {"center": v(230, 294.45) * mm, "radius": 9 * mm});
            skCircle(sketch, "E4.0.8.32", {"center": v(150, 294.45) * mm, "radius": 9 * mm});
            skCircle(sketch, "E4.0.8.33", {"center": v(470, 294.45) * mm, "radius": 9 * mm});
            skCircle(sketch, "E4.0.8.34", {"center": v(410, 294.45) * mm, "radius": 9 * mm});
            skCircle(sketch, "E4.0.8.35", {"center": v(50, 294.45) * mm, "radius": 9 * mm});
            skCircle(sketch, "E4.0.8.36", {"center": v(400, 277.13) * mm, "radius": 9 * mm});
            skCircle(sketch, "E4.0.8.37", {"center": v(240, 277.13) * mm, "radius": 9 * mm});
            skCircle(sketch, "E4.0.8.38", {"center": v(320, 277.13) * mm, "radius": 9 * mm});
            skCircle(sketch, "E4.0.8.39", {"center": v(370, 294.45) * mm, "radius": 9 * mm});
            skCircle(sketch, "E4.0.8.40", {"center": v(10, 294.45) * mm, "radius": 9 * mm});
            skCircle(sketch, "E4.0.8.41", {"center": v(290, 294.45) * mm, "radius": 9 * mm});
            skCircle(sketch, "E4.0.8.42", {"center": v(360, 277.13) * mm, "radius": 9 * mm});
            skCircle(sketch, "E4.0.8.43", {"center": v(460, 277.13) * mm, "radius": 9 * mm});
            skCircle(sketch, "E4.0.8.44", {"center": v(310, 294.45) * mm, "radius": 9 * mm});
            skCircle(sketch, "E4.0.8.45", {"center": v(340, 277.13) * mm, "radius": 9 * mm});
            skCircle(sketch, "E4.0.8.46", {"center": v(170, 294.45) * mm, "radius": 9 * mm});
            skCircle(sketch, "E4.0.8.47", {"center": v(20, 277.13) * mm, "radius": 9 * mm});
            skLineSegment(sketch, "E4.0.8.48", {"start": v(0, 277.13) * mm, "end": v(20, 277.13) * mm, "construction": true});
            skLineSegment(sketch, "E4.0.8.49", {"start": v(10, 294.45) * mm, "end": v(30, 294.45) * mm, "construction": true});
            skCircle(sketch, "E4.0.9.0", {"center": v(280, 311.77) * mm, "radius": 9 * mm});
            skCircle(sketch, "E4.0.9.1", {"center": v(260, 311.77) * mm, "radius": 9 * mm});
            skCircle(sketch, "E4.0.9.2", {"center": v(130, 329.09) * mm, "radius": 9 * mm});
            skCircle(sketch, "E4.0.9.3", {"center": v(60, 311.77) * mm, "radius": 9 * mm});
            skCircle(sketch, "E4.0.9.4", {"center": v(80, 311.77) * mm, "radius": 9 * mm});
            skCircle(sketch, "E4.0.9.5", {"center": v(100, 311.77) * mm, "radius": 9 * mm});
            skCircle(sketch, "E4.0.9.6", {"center": v(350, 329.09) * mm, "radius": 9 * mm});
            skCircle(sketch, "E4.0.9.7", {"center": v(0, 311.77) * mm, "radius": 9 * mm});
            skCircle(sketch, "E4.0.9.8", {"center": v(120, 311.77) * mm, "radius": 9 * mm});
            skCircle(sketch, "E4.0.9.9", {"center": v(30, 329.09) * mm, "radius": 9 * mm});
            skCircle(sketch, "E4.0.9.10", {"center": v(380, 311.77) * mm, "radius": 9 * mm});
            skCircle(sketch, "E4.0.9.11", {"center": v(140, 311.77) * mm, "radius": 9 * mm});
            skCircle(sketch, "E4.0.9.12", {"center": v(450, 329.09) * mm, "radius": 9 * mm});
            skCircle(sketch, "E4.0.9.13", {"center": v(160, 311.77) * mm, "radius": 9 * mm});
            skCircle(sketch, "E4.0.9.14", {"center": v(300, 311.77) * mm, "radius": 9 * mm});
            skCircle(sketch, "E4.0.9.15", {"center": v(40, 311.77) * mm, "radius": 9 * mm});
            skCircle(sketch, "E4.0.9.16", {"center": v(210, 329.09) * mm, "radius": 9 * mm});
            skCircle(sketch, "E4.0.9.17", {"center": v(330, 329.09) * mm, "radius": 9 * mm});
            skCircle(sketch, "E4.0.9.18", {"center": v(270, 329.09) * mm, "radius": 9 * mm});
            skCircle(sketch, "E4.0.9.19", {"center": v(440, 311.77) * mm, "radius": 9 * mm});
            skCircle(sketch, "E4.0.9.20", {"center": v(110, 329.09) * mm, "radius": 9 * mm});
            skCircle(sketch, "E4.0.9.21", {"center": v(250, 329.09) * mm, "radius": 9 * mm});
            skCircle(sketch, "E4.0.9.22", {"center": v(180, 311.77) * mm, "radius": 9 * mm});
            skCircle(sketch, "E4.0.9.23", {"center": v(430, 329.09) * mm, "radius": 9 * mm});
            skCircle(sketch, "E4.0.9.24", {"center": v(200, 311.77) * mm, "radius": 9 * mm});
            skCircle(sketch, "E4.0.9.25", {"center": v(420, 311.77) * mm, "radius": 9 * mm});
            skCircle(sketch, "E4.0.9.26", {"center": v(70, 329.09) * mm, "radius": 9 * mm});
            skCircle(sketch, "E4.0.9.27", {"center": v(390, 329.09) * mm, "radius": 9 * mm});
            skCircle(sketch, "E4.0.9.28", {"center": v(220, 311.77) * mm, "radius": 9 * mm});
            skCircle(sketch, "E4.0.9.29", {"center": v(190, 329.09) * mm, "radius": 9 * mm});
            skCircle(sketch, "E4.0.9.30", {"center": v(90, 329.09) * mm, "radius": 9 * mm});
            skCircle(sketch, "E4.0.9.31", {"center": v(230, 329.09) * mm, "radius": 9 * mm});
            skCircle(sketch, "E4.0.9.32", {"center": v(150, 329.09) * mm, "radius": 9 * mm});
            skCircle(sketch, "E4.0.9.33", {"center": v(470, 329.09) * mm, "radius": 9 * mm});
            skCircle(sketch, "E4.0.9.34", {"center": v(410, 329.09) * mm, "radius": 9 * mm});
            skCircle(sketch, "E4.0.9.35", {"center": v(50, 329.09) * mm, "radius": 9 * mm});
            skCircle(sketch, "E4.0.9.36", {"center": v(400, 311.77) * mm, "radius": 9 * mm});
            skCircle(sketch, "E4.0.9.37", {"center": v(240, 311.77) * mm, "radius": 9 * mm});
            skCircle(sketch, "E4.0.9.38", {"center": v(320, 311.77) * mm, "radius": 9 * mm});
            skCircle(sketch, "E4.0.9.39", {"center": v(370, 329.09) * mm, "radius": 9 * mm});
            skCircle(sketch, "E4.0.9.40", {"center": v(10, 329.09) * mm, "radius": 9 * mm});
            skCircle(sketch, "E4.0.9.41", {"center": v(290, 329.09) * mm, "radius": 9 * mm});
            skCircle(sketch, "E4.0.9.42", {"center": v(360, 311.77) * mm, "radius": 9 * mm});
            skCircle(sketch, "E4.0.9.43", {"center": v(460, 311.77) * mm, "radius": 9 * mm});
            skCircle(sketch, "E4.0.9.44", {"center": v(310, 329.09) * mm, "radius": 9 * mm});
            skCircle(sketch, "E4.0.9.45", {"center": v(340, 311.77) * mm, "radius": 9 * mm});
            skCircle(sketch, "E4.0.9.46", {"center": v(170, 329.09) * mm, "radius": 9 * mm});
            skCircle(sketch, "E4.0.9.47", {"center": v(20, 311.77) * mm, "radius": 9 * mm});
            skLineSegment(sketch, "E4.0.9.48", {"start": v(0, 311.77) * mm, "end": v(20, 311.77) * mm, "construction": true});
            skLineSegment(sketch, "E4.0.9.49", {"start": v(10, 329.09) * mm, "end": v(30, 329.09) * mm, "construction": true});
            skCircle(sketch, "E4.0.10.0", {"center": v(280, 346.41) * mm, "radius": 9 * mm});
            skCircle(sketch, "E4.0.10.1", {"center": v(260, 346.41) * mm, "radius": 9 * mm});
            skCircle(sketch, "E4.0.10.2", {"center": v(130, 363.73) * mm, "radius": 9 * mm});
            skCircle(sketch, "E4.0.10.3", {"center": v(60, 346.41) * mm, "radius": 9 * mm});
            skCircle(sketch, "E4.0.10.4", {"center": v(80, 346.41) * mm, "radius": 9 * mm});
            skCircle(sketch, "E4.0.10.5", {"center": v(100, 346.41) * mm, "radius": 9 * mm});
            skCircle(sketch, "E4.0.10.6", {"center": v(350, 363.73) * mm, "radius": 9 * mm});
            skCircle(sketch, "E4.0.10.7", {"center": v(0, 346.41) * mm, "radius": 9 * mm});
            skCircle(sketch, "E4.0.10.8", {"center": v(120, 346.41) * mm, "radius": 9 * mm});
            skCircle(sketch, "E4.0.10.9", {"center": v(30, 363.73) * mm, "radius": 9 * mm});
            skCircle(sketch, "E4.0.10.10", {"center": v(380, 346.41) * mm, "radius": 9 * mm});
            skCircle(sketch, "E4.0.10.11", {"center": v(140, 346.41) * mm, "radius": 9 * mm});
            skCircle(sketch, "E4.0.10.12", {"center": v(450, 363.73) * mm, "radius": 9 * mm});
            skCircle(sketch, "E4.0.10.13", {"center": v(160, 346.41) * mm, "radius": 9 * mm});
            skCircle(sketch, "E4.0.10.14", {"center": v(300, 346.41) * mm, "radius": 9 * mm});
            skCircle(sketch, "E4.0.10.15", {"center": v(40, 346.41) * mm, "radius": 9 * mm});
            skCircle(sketch, "E4.0.10.16", {"center": v(210, 363.73) * mm, "radius": 9 * mm});
            skCircle(sketch, "E4.0.10.17", {"center": v(330, 363.73) * mm, "radius": 9 * mm});
            skCircle(sketch, "E4.0.10.18", {"center": v(270, 363.73) * mm, "radius": 9 * mm});
            skCircle(sketch, "E4.0.10.19", {"center": v(440, 346.41) * mm, "radius": 9 * mm});
            skCircle(sketch, "E4.0.10.20", {"center": v(110, 363.73) * mm, "radius": 9 * mm});
            skCircle(sketch, "E4.0.10.21", {"center": v(250, 363.73) * mm, "radius": 9 * mm});
            skCircle(sketch, "E4.0.10.22", {"center": v(180, 346.41) * mm, "radius": 9 * mm});
            skCircle(sketch, "E4.0.10.23", {"center": v(430, 363.73) * mm, "radius": 9 * mm});
            skCircle(sketch, "E4.0.10.24", {"center": v(200, 346.41) * mm, "radius": 9 * mm});
            skCircle(sketch, "E4.0.10.25", {"center": v(420, 346.41) * mm, "radius": 9 * mm});
            skCircle(sketch, "E4.0.10.26", {"center": v(70, 363.73) * mm, "radius": 9 * mm});
            skCircle(sketch, "E4.0.10.27", {"center": v(390, 363.73) * mm, "radius": 9 * mm});
            skCircle(sketch, "E4.0.10.28", {"center": v(220, 346.41) * mm, "radius": 9 * mm});
            skCircle(sketch, "E4.0.10.29", {"center": v(190, 363.73) * mm, "radius": 9 * mm});
            skCircle(sketch, "E4.0.10.30", {"center": v(90, 363.73) * mm, "radius": 9 * mm});
            skCircle(sketch, "E4.0.10.31", {"center": v(230, 363.73) * mm, "radius": 9 * mm});
            skCircle(sketch, "E4.0.10.32", {"center": v(150, 363.73) * mm, "radius": 9 * mm});
            skCircle(sketch, "E4.0.10.33", {"center": v(470, 363.73) * mm, "radius": 9 * mm});
            skCircle(sketch, "E4.0.10.34", {"center": v(410, 363.73) * mm, "radius": 9 * mm});
            skCircle(sketch, "E4.0.10.35", {"center": v(50, 363.73) * mm, "radius": 9 * mm});
            skCircle(sketch, "E4.0.10.36", {"center": v(400, 346.41) * mm, "radius": 9 * mm});
            skCircle(sketch, "E4.0.10.37", {"center": v(240, 346.41) * mm, "radius": 9 * mm});
            skCircle(sketch, "E4.0.10.38", {"center": v(320, 346.41) * mm, "radius": 9 * mm});
            skCircle(sketch, "E4.0.10.39", {"center": v(370, 363.73) * mm, "radius": 9 * mm});
            skCircle(sketch, "E4.0.10.40", {"center": v(10, 363.73) * mm, "radius": 9 * mm});
            skCircle(sketch, "E4.0.10.41", {"center": v(290, 363.73) * mm, "radius": 9 * mm});
            skCircle(sketch, "E4.0.10.42", {"center": v(360, 346.41) * mm, "radius": 9 * mm});
            skCircle(sketch, "E4.0.10.43", {"center": v(460, 346.41) * mm, "radius": 9 * mm});
            skCircle(sketch, "E4.0.10.44", {"center": v(310, 363.73) * mm, "radius": 9 * mm});
            skCircle(sketch, "E4.0.10.45", {"center": v(340, 346.41) * mm, "radius": 9 * mm});
            skCircle(sketch, "E4.0.10.46", {"center": v(170, 363.73) * mm, "radius": 9 * mm});
            skCircle(sketch, "E4.0.10.47", {"center": v(20, 346.41) * mm, "radius": 9 * mm});
            skLineSegment(sketch, "E4.0.10.48", {"start": v(0, 346.41) * mm, "end": v(20, 346.41) * mm, "construction": true});
            skLineSegment(sketch, "E4.0.10.49", {"start": v(10, 363.73) * mm, "end": v(30, 363.73) * mm, "construction": true});
            skCircle(sketch, "E4.0.11.0", {"center": v(280, 381.05) * mm, "radius": 9 * mm});
            skCircle(sketch, "E4.0.11.1", {"center": v(260, 381.05) * mm, "radius": 9 * mm});
            skCircle(sketch, "E4.0.11.2", {"center": v(130, 398.37) * mm, "radius": 9 * mm});
            skCircle(sketch, "E4.0.11.3", {"center": v(60, 381.05) * mm, "radius": 9 * mm});
            skCircle(sketch, "E4.0.11.4", {"center": v(80, 381.05) * mm, "radius": 9 * mm});
            skCircle(sketch, "E4.0.11.5", {"center": v(100, 381.05) * mm, "radius": 9 * mm});
            skCircle(sketch, "E4.0.11.6", {"center": v(350, 398.37) * mm, "radius": 9 * mm});
            skCircle(sketch, "E4.0.11.7", {"center": v(0, 381.05) * mm, "radius": 9 * mm});
            skCircle(sketch, "E4.0.11.8", {"center": v(120, 381.05) * mm, "radius": 9 * mm});
            skCircle(sketch, "E4.0.11.9", {"center": v(30, 398.37) * mm, "radius": 9 * mm});
            skCircle(sketch, "E4.0.11.10", {"center": v(380, 381.05) * mm, "radius": 9 * mm});
            skCircle(sketch, "E4.0.11.11", {"center": v(140, 381.05) * mm, "radius": 9 * mm});
            skCircle(sketch, "E4.0.11.12", {"center": v(450, 398.37) * mm, "radius": 9 * mm});
            skCircle(sketch, "E4.0.11.13", {"center": v(160, 381.05) * mm, "radius": 9 * mm});
            skCircle(sketch, "E4.0.11.14", {"center": v(300, 381.05) * mm, "radius": 9 * mm});
            skCircle(sketch, "E4.0.11.15", {"center": v(40, 381.05) * mm, "radius": 9 * mm});
            skCircle(sketch, "E4.0.11.16", {"center": v(210, 398.37) * mm, "radius": 9 * mm});
            skCircle(sketch, "E4.0.11.17", {"center": v(330, 398.37) * mm, "radius": 9 * mm});
            skCircle(sketch, "E4.0.11.18", {"center": v(270, 398.37) * mm, "radius": 9 * mm});
            skCircle(sketch, "E4.0.11.19", {"center": v(440, 381.05) * mm, "radius": 9 * mm});
            skCircle(sketch, "E4.0.11.20", {"center": v(110, 398.37) * mm, "radius": 9 * mm});
            skCircle(sketch, "E4.0.11.21", {"center": v(250, 398.37) * mm, "radius": 9 * mm});
            skCircle(sketch, "E4.0.11.22", {"center": v(180, 381.05) * mm, "radius": 9 * mm});
            skCircle(sketch, "E4.0.11.23", {"center": v(430, 398.37) * mm, "radius": 9 * mm});
            skCircle(sketch, "E4.0.11.24", {"center": v(200, 381.05) * mm, "radius": 9 * mm});
            skCircle(sketch, "E4.0.11.25", {"center": v(420, 381.05) * mm, "radius": 9 * mm});
            skCircle(sketch, "E4.0.11.26", {"center": v(70, 398.37) * mm, "radius": 9 * mm});
            skCircle(sketch, "E4.0.11.27", {"center": v(390, 398.37) * mm, "radius": 9 * mm});
            skCircle(sketch, "E4.0.11.28", {"center": v(220, 381.05) * mm, "radius": 9 * mm});
            skCircle(sketch, "E4.0.11.29", {"center": v(190, 398.37) * mm, "radius": 9 * mm});
            skCircle(sketch, "E4.0.11.30", {"center": v(90, 398.37) * mm, "radius": 9 * mm});
            skCircle(sketch, "E4.0.11.31", {"center": v(230, 398.37) * mm, "radius": 9 * mm});
            skCircle(sketch, "E4.0.11.32", {"center": v(150, 398.37) * mm, "radius": 9 * mm});
            skCircle(sketch, "E4.0.11.33", {"center": v(470, 398.37) * mm, "radius": 9 * mm});
            skCircle(sketch, "E4.0.11.34", {"center": v(410, 398.37) * mm, "radius": 9 * mm});
            skCircle(sketch, "E4.0.11.35", {"center": v(50, 398.37) * mm, "radius": 9 * mm});
            skCircle(sketch, "E4.0.11.36", {"center": v(400, 381.05) * mm, "radius": 9 * mm});
            skCircle(sketch, "E4.0.11.37", {"center": v(240, 381.05) * mm, "radius": 9 * mm});
            skCircle(sketch, "E4.0.11.38", {"center": v(320, 381.05) * mm, "radius": 9 * mm});
            skCircle(sketch, "E4.0.11.39", {"center": v(370, 398.37) * mm, "radius": 9 * mm});
            skCircle(sketch, "E4.0.11.40", {"center": v(10, 398.37) * mm, "radius": 9 * mm});
            skCircle(sketch, "E4.0.11.41", {"center": v(290, 398.37) * mm, "radius": 9 * mm});
            skCircle(sketch, "E4.0.11.42", {"center": v(360, 381.05) * mm, "radius": 9 * mm});
            skCircle(sketch, "E4.0.11.43", {"center": v(460, 381.05) * mm, "radius": 9 * mm});
            skCircle(sketch, "E4.0.11.44", {"center": v(310, 398.37) * mm, "radius": 9 * mm});
            skCircle(sketch, "E4.0.11.45", {"center": v(340, 381.05) * mm, "radius": 9 * mm});
            skCircle(sketch, "E4.0.11.46", {"center": v(170, 398.37) * mm, "radius": 9 * mm});
            skCircle(sketch, "E4.0.11.47", {"center": v(20, 381.05) * mm, "radius": 9 * mm});
            skLineSegment(sketch, "E4.0.11.48", {"start": v(0, 381.05) * mm, "end": v(20, 381.05) * mm, "construction": true});
            skLineSegment(sketch, "E4.0.11.49", {"start": v(10, 398.37) * mm, "end": v(30, 398.37) * mm, "construction": true});
            skCircle(sketch, "E4.0.12.0", {"center": v(280, 415.7) * mm, "radius": 9 * mm});
            skCircle(sketch, "E4.0.12.1", {"center": v(260, 415.7) * mm, "radius": 9 * mm});
            skCircle(sketch, "E4.0.12.2", {"center": v(130, 433.01) * mm, "radius": 9 * mm});
            skCircle(sketch, "E4.0.12.3", {"center": v(60, 415.7) * mm, "radius": 9 * mm});
            skCircle(sketch, "E4.0.12.4", {"center": v(80, 415.7) * mm, "radius": 9 * mm});
            skCircle(sketch, "E4.0.12.5", {"center": v(100, 415.7) * mm, "radius": 9 * mm});
            skCircle(sketch, "E4.0.12.6", {"center": v(350, 433.01) * mm, "radius": 9 * mm});
            skCircle(sketch, "E4.0.12.7", {"center": v(0, 415.7) * mm, "radius": 9 * mm});
            skCircle(sketch, "E4.0.12.8", {"center": v(120, 415.7) * mm, "radius": 9 * mm});
            skCircle(sketch, "E4.0.12.9", {"center": v(30, 433.01) * mm, "radius": 9 * mm});
            skCircle(sketch, "E4.0.12.10", {"center": v(380, 415.7) * mm, "radius": 9 * mm});
            skCircle(sketch, "E4.0.12.11", {"center": v(140, 415.7) * mm, "radius": 9 * mm});
            skCircle(sketch, "E4.0.12.12", {"center": v(450, 433.01) * mm, "radius": 9 * mm});
            skCircle(sketch, "E4.0.12.13", {"center": v(160, 415.7) * mm, "radius": 9 * mm});
            skCircle(sketch, "E4.0.12.14", {"center": v(300, 415.7) * mm, "radius": 9 * mm});
            skCircle(sketch, "E4.0.12.15", {"center": v(40, 415.7) * mm, "radius": 9 * mm});
            skCircle(sketch, "E4.0.12.16", {"center": v(210, 433.01) * mm, "radius": 9 * mm});
            skCircle(sketch, "E4.0.12.17", {"center": v(330, 433.01) * mm, "radius": 9 * mm});
            skCircle(sketch, "E4.0.12.18", {"center": v(270, 433.01) * mm, "radius": 9 * mm});
            skCircle(sketch, "E4.0.12.19", {"center": v(440, 415.7) * mm, "radius": 9 * mm});
            skCircle(sketch, "E4.0.12.20", {"center": v(110, 433.01) * mm, "radius": 9 * mm});
            skCircle(sketch, "E4.0.12.21", {"center": v(250, 433.01) * mm, "radius": 9 * mm});
            skCircle(sketch, "E4.0.12.22", {"center": v(180, 415.7) * mm, "radius": 9 * mm});
            skCircle(sketch, "E4.0.12.23", {"center": v(430, 433.01) * mm, "radius": 9 * mm});
            skCircle(sketch, "E4.0.12.24", {"center": v(200, 415.7) * mm, "radius": 9 * mm});
            skCircle(sketch, "E4.0.12.25", {"center": v(420, 415.7) * mm, "radius": 9 * mm});
            skCircle(sketch, "E4.0.12.26", {"center": v(70, 433.01) * mm, "radius": 9 * mm});
            skCircle(sketch, "E4.0.12.27", {"center": v(390, 433.01) * mm, "radius": 9 * mm});
            skCircle(sketch, "E4.0.12.28", {"center": v(220, 415.7) * mm, "radius": 9 * mm});
            skCircle(sketch, "E4.0.12.29", {"center": v(190, 433.01) * mm, "radius": 9 * mm});
            skCircle(sketch, "E4.0.12.30", {"center": v(90, 433.01) * mm, "radius": 9 * mm});
            skCircle(sketch, "E4.0.12.31", {"center": v(230, 433.01) * mm, "radius": 9 * mm});
            skCircle(sketch, "E4.0.12.32", {"center": v(150, 433.01) * mm, "radius": 9 * mm});
            skCircle(sketch, "E4.0.12.33", {"center": v(470, 433.01) * mm, "radius": 9 * mm});
            skCircle(sketch, "E4.0.12.34", {"center": v(410, 433.01) * mm, "radius": 9 * mm});
            skCircle(sketch, "E4.0.12.35", {"center": v(50, 433.01) * mm, "radius": 9 * mm});
            skCircle(sketch, "E4.0.12.36", {"center": v(400, 415.7) * mm, "radius": 9 * mm});
            skCircle(sketch, "E4.0.12.37", {"center": v(240, 415.7) * mm, "radius": 9 * mm});
            skCircle(sketch, "E4.0.12.38", {"center": v(320, 415.7) * mm, "radius": 9 * mm});
            skCircle(sketch, "E4.0.12.39", {"center": v(370, 433.01) * mm, "radius": 9 * mm});
            skCircle(sketch, "E4.0.12.40", {"center": v(10, 433.01) * mm, "radius": 9 * mm});
            skCircle(sketch, "E4.0.12.41", {"center": v(290, 433.01) * mm, "radius": 9 * mm});
            skCircle(sketch, "E4.0.12.42", {"center": v(360, 415.7) * mm, "radius": 9 * mm});
            skCircle(sketch, "E4.0.12.43", {"center": v(460, 415.7) * mm, "radius": 9 * mm});
            skCircle(sketch, "E4.0.12.44", {"center": v(310, 433.01) * mm, "radius": 9 * mm});
            skCircle(sketch, "E4.0.12.45", {"center": v(340, 415.7) * mm, "radius": 9 * mm});
            skCircle(sketch, "E4.0.12.46", {"center": v(170, 433.01) * mm, "radius": 9 * mm});
            skCircle(sketch, "E4.0.12.47", {"center": v(20, 415.7) * mm, "radius": 9 * mm});
            skLineSegment(sketch, "E4.0.12.48", {"start": v(0, 415.7) * mm, "end": v(20, 415.7) * mm, "construction": true});
            skLineSegment(sketch, "E4.0.12.49", {"start": v(10, 433.01) * mm, "end": v(30, 433.01) * mm, "construction": true});
            skCircle(sketch, "E4.0.13.0", {"center": v(280, 450.33) * mm, "radius": 9 * mm});
            skCircle(sketch, "E4.0.13.1", {"center": v(260, 450.33) * mm, "radius": 9 * mm});
            skCircle(sketch, "E4.0.13.2", {"center": v(130, 467.65) * mm, "radius": 9 * mm});
            skCircle(sketch, "E4.0.13.3", {"center": v(60, 450.33) * mm, "radius": 9 * mm});
            skCircle(sketch, "E4.0.13.4", {"center": v(80, 450.33) * mm, "radius": 9 * mm});
            skCircle(sketch, "E4.0.13.5", {"center": v(100, 450.33) * mm, "radius": 9 * mm});
            skCircle(sketch, "E4.0.13.6", {"center": v(350, 467.65) * mm, "radius": 9 * mm});
            skCircle(sketch, "E4.0.13.7", {"center": v(0, 450.33) * mm, "radius": 9 * mm});
            skCircle(sketch, "E4.0.13.8", {"center": v(120, 450.33) * mm, "radius": 9 * mm});
            skCircle(sketch, "E4.0.13.9", {"center": v(30, 467.65) * mm, "radius": 9 * mm});
            skCircle(sketch, "E4.0.13.10", {"center": v(380, 450.33) * mm, "radius": 9 * mm});
            skCircle(sketch, "E4.0.13.11", {"center": v(140, 450.33) * mm, "radius": 9 * mm});
            skCircle(sketch, "E4.0.13.12", {"center": v(450, 467.65) * mm, "radius": 9 * mm});
            skCircle(sketch, "E4.0.13.13", {"center": v(160, 450.33) * mm, "radius": 9 * mm});
            skCircle(sketch, "E4.0.13.14", {"center": v(300, 450.33) * mm, "radius": 9 * mm});
            skCircle(sketch, "E4.0.13.15", {"center": v(40, 450.33) * mm, "radius": 9 * mm});
            skCircle(sketch, "E4.0.13.16", {"center": v(210, 467.65) * mm, "radius": 9 * mm});
            skCircle(sketch, "E4.0.13.17", {"center": v(330, 467.65) * mm, "radius": 9 * mm});
            skCircle(sketch, "E4.0.13.18", {"center": v(270, 467.65) * mm, "radius": 9 * mm});
            skCircle(sketch, "E4.0.13.19", {"center": v(440, 450.33) * mm, "radius": 9 * mm});
            skCircle(sketch, "E4.0.13.20", {"center": v(110, 467.65) * mm, "radius": 9 * mm});
            skCircle(sketch, "E4.0.13.21", {"center": v(250, 467.65) * mm, "radius": 9 * mm});
            skCircle(sketch, "E4.0.13.22", {"center": v(180, 450.33) * mm, "radius": 9 * mm});
            skCircle(sketch, "E4.0.13.23", {"center": v(430, 467.65) * mm, "radius": 9 * mm});
            skCircle(sketch, "E4.0.13.24", {"center": v(200, 450.33) * mm, "radius": 9 * mm});
            skCircle(sketch, "E4.0.13.25", {"center": v(420, 450.33) * mm, "radius": 9 * mm});
            skCircle(sketch, "E4.0.13.26", {"center": v(70, 467.65) * mm, "radius": 9 * mm});
            skCircle(sketch, "E4.0.13.27", {"center": v(390, 467.65) * mm, "radius": 9 * mm});
            skCircle(sketch, "E4.0.13.28", {"center": v(220, 450.33) * mm, "radius": 9 * mm});
            skCircle(sketch, "E4.0.13.29", {"center": v(190, 467.65) * mm, "radius": 9 * mm});
            skCircle(sketch, "E4.0.13.30", {"center": v(90, 467.65) * mm, "radius": 9 * mm});
            skCircle(sketch, "E4.0.13.31", {"center": v(230, 467.65) * mm, "radius": 9 * mm});
            skCircle(sketch, "E4.0.13.32", {"center": v(150, 467.65) * mm, "radius": 9 * mm});
            skCircle(sketch, "E4.0.13.33", {"center": v(470, 467.65) * mm, "radius": 9 * mm});
            skCircle(sketch, "E4.0.13.34", {"center": v(410, 467.65) * mm, "radius": 9 * mm});
            skCircle(sketch, "E4.0.13.35", {"center": v(50, 467.65) * mm, "radius": 9 * mm});
            skCircle(sketch, "E4.0.13.36", {"center": v(400, 450.33) * mm, "radius": 9 * mm});
            skCircle(sketch, "E4.0.13.37", {"center": v(240, 450.33) * mm, "radius": 9 * mm});
            skCircle(sketch, "E4.0.13.38", {"center": v(320, 450.33) * mm, "radius": 9 * mm});
            skCircle(sketch, "E4.0.13.39", {"center": v(370, 467.65) * mm, "radius": 9 * mm});
            skCircle(sketch, "E4.0.13.40", {"center": v(10, 467.65) * mm, "radius": 9 * mm});
            skCircle(sketch, "E4.0.13.41", {"center": v(290, 467.65) * mm, "radius": 9 * mm});
            skCircle(sketch, "E4.0.13.42", {"center": v(360, 450.33) * mm, "radius": 9 * mm});
            skCircle(sketch, "E4.0.13.43", {"center": v(460, 450.33) * mm, "radius": 9 * mm});
            skCircle(sketch, "E4.0.13.44", {"center": v(310, 467.65) * mm, "radius": 9 * mm});
            skCircle(sketch, "E4.0.13.45", {"center": v(340, 450.33) * mm, "radius": 9 * mm});
            skCircle(sketch, "E4.0.13.46", {"center": v(170, 467.65) * mm, "radius": 9 * mm});
            skCircle(sketch, "E4.0.13.47", {"center": v(20, 450.33) * mm, "radius": 9 * mm});
            skLineSegment(sketch, "E4.0.13.48", {"start": v(0, 450.33) * mm, "end": v(20, 450.33) * mm, "construction": true});
            skLineSegment(sketch, "E4.0.13.49", {"start": v(10, 467.65) * mm, "end": v(30, 467.65) * mm, "construction": true});
            skCircle(sketch, "E4.0.14.0", {"center": v(280, 484.97) * mm, "radius": 9 * mm});
            skCircle(sketch, "E4.0.14.1", {"center": v(260, 484.97) * mm, "radius": 9 * mm});
            skCircle(sketch, "E4.0.14.2", {"center": v(130, 502.3) * mm, "radius": 9 * mm});
            skCircle(sketch, "E4.0.14.3", {"center": v(60, 484.97) * mm, "radius": 9 * mm});
            skCircle(sketch, "E4.0.14.4", {"center": v(80, 484.97) * mm, "radius": 9 * mm});
            skCircle(sketch, "E4.0.14.5", {"center": v(100, 484.97) * mm, "radius": 9 * mm});
            skCircle(sketch, "E4.0.14.6", {"center": v(350, 502.3) * mm, "radius": 9 * mm});
            skCircle(sketch, "E4.0.14.7", {"center": v(0, 484.97) * mm, "radius": 9 * mm});
            skCircle(sketch, "E4.0.14.8", {"center": v(120, 484.97) * mm, "radius": 9 * mm});
            skCircle(sketch, "E4.0.14.9", {"center": v(30, 502.3) * mm, "radius": 9 * mm});
            skCircle(sketch, "E4.0.14.10", {"center": v(380, 484.97) * mm, "radius": 9 * mm});
            skCircle(sketch, "E4.0.14.11", {"center": v(140, 484.97) * mm, "radius": 9 * mm});
            skCircle(sketch, "E4.0.14.12", {"center": v(450, 502.3) * mm, "radius": 9 * mm});
            skCircle(sketch, "E4.0.14.13", {"center": v(160, 484.97) * mm, "radius": 9 * mm});
            skCircle(sketch, "E4.0.14.14", {"center": v(300, 484.97) * mm, "radius": 9 * mm});
            skCircle(sketch, "E4.0.14.15", {"center": v(40, 484.97) * mm, "radius": 9 * mm});
            skCircle(sketch, "E4.0.14.16", {"center": v(210, 502.3) * mm, "radius": 9 * mm});
            skCircle(sketch, "E4.0.14.17", {"center": v(330, 502.3) * mm, "radius": 9 * mm});
            skCircle(sketch, "E4.0.14.18", {"center": v(270, 502.3) * mm, "radius": 9 * mm});
            skCircle(sketch, "E4.0.14.19", {"center": v(440, 484.97) * mm, "radius": 9 * mm});
            skCircle(sketch, "E4.0.14.20", {"center": v(110, 502.3) * mm, "radius": 9 * mm});
            skCircle(sketch, "E4.0.14.21", {"center": v(250, 502.3) * mm, "radius": 9 * mm});
            skCircle(sketch, "E4.0.14.22", {"center": v(180, 484.97) * mm, "radius": 9 * mm});
            skCircle(sketch, "E4.0.14.23", {"center": v(430, 502.3) * mm, "radius": 9 * mm});
            skCircle(sketch, "E4.0.14.24", {"center": v(200, 484.97) * mm, "radius": 9 * mm});
            skCircle(sketch, "E4.0.14.25", {"center": v(420, 484.97) * mm, "radius": 9 * mm});
            skCircle(sketch, "E4.0.14.26", {"center": v(70, 502.3) * mm, "radius": 9 * mm});
            skCircle(sketch, "E4.0.14.27", {"center": v(390, 502.3) * mm, "radius": 9 * mm});
            skCircle(sketch, "E4.0.14.28", {"center": v(220, 484.97) * mm, "radius": 9 * mm});
            skCircle(sketch, "E4.0.14.29", {"center": v(190, 502.3) * mm, "radius": 9 * mm});
            skCircle(sketch, "E4.0.14.30", {"center": v(90, 502.3) * mm, "radius": 9 * mm});
            skCircle(sketch, "E4.0.14.31", {"center": v(230, 502.3) * mm, "radius": 9 * mm});
            skCircle(sketch, "E4.0.14.32", {"center": v(150, 502.3) * mm, "radius": 9 * mm});
            skCircle(sketch, "E4.0.14.33", {"center": v(470, 502.3) * mm, "radius": 9 * mm});
            skCircle(sketch, "E4.0.14.34", {"center": v(410, 502.3) * mm, "radius": 9 * mm});
            skCircle(sketch, "E4.0.14.35", {"center": v(50, 502.3) * mm, "radius": 9 * mm});
            skCircle(sketch, "E4.0.14.36", {"center": v(400, 484.97) * mm, "radius": 9 * mm});
            skCircle(sketch, "E4.0.14.37", {"center": v(240, 484.97) * mm, "radius": 9 * mm});
            skCircle(sketch, "E4.0.14.38", {"center": v(320, 484.97) * mm, "radius": 9 * mm});
            skCircle(sketch, "E4.0.14.39", {"center": v(370, 502.3) * mm, "radius": 9 * mm});
            skCircle(sketch, "E4.0.14.40", {"center": v(10, 502.3) * mm, "radius": 9 * mm});
            skCircle(sketch, "E4.0.14.41", {"center": v(290, 502.3) * mm, "radius": 9 * mm});
            skCircle(sketch, "E4.0.14.42", {"center": v(360, 484.97) * mm, "radius": 9 * mm});
            skCircle(sketch, "E4.0.14.43", {"center": v(460, 484.97) * mm, "radius": 9 * mm});
            skCircle(sketch, "E4.0.14.44", {"center": v(310, 502.3) * mm, "radius": 9 * mm});
            skCircle(sketch, "E4.0.14.45", {"center": v(340, 484.97) * mm, "radius": 9 * mm});
            skCircle(sketch, "E4.0.14.46", {"center": v(170, 502.3) * mm, "radius": 9 * mm});
            skCircle(sketch, "E4.0.14.47", {"center": v(20, 484.97) * mm, "radius": 9 * mm});
            skLineSegment(sketch, "E4.0.14.48", {"start": v(0, 484.97) * mm, "end": v(20, 484.97) * mm, "construction": true});
            skLineSegment(sketch, "E4.0.14.49", {"start": v(10, 502.3) * mm, "end": v(30, 502.3) * mm, "construction": true});
            skLineSegment(sketch, "E4.direction1", {"start": v(0, 0) * mm, "end": v(25, 0) * mm, "construction": true});
            skLineSegment(sketch, "E4.direction2", {"start": v(0, 0) * mm, "end": v(0, 34.64) * mm, "construction": true});
            skLineSegment(sketch, "E5.bottom", {"start": v(470, 502.3) * mm, "end": v(0, 502.3) * mm, "construction": true});
            skLineSegment(sketch, "E5.top", {"start": v(470, 0) * mm, "end": v(0, 0) * mm, "construction": true});
            skLineSegment(sketch, "E5.left", {"start": v(470, 502.3) * mm, "end": v(470, 0) * mm, "construction": true});
            skLineSegment(sketch, "E5.right", {"start": v(0, 502.3) * mm, "end": v(0, 0) * mm, "construction": true});
            skLineSegment(sketch, "E6", {"start": v(0, 0) * mm, "end": v(470, 502.3) * mm, "construction": true});
            skLineSegment(sketch, "E7", {"start": v(0, 502.3) * mm, "end": v(470, 0) * mm, "construction": true});
            skPoint(sketch, "E8", {"position": v(235, 251.15) * mm});
            skSolve(sketch);
        }
        {
            var Q0;
            Q0=qCreatedBy(makeId("Top.planeOp"),FACE);
            var sketch = newSketch(context, id + "F1", { "sketchPlane" : qUnion([Q0])});
            skLineSegment(sketch, "E9.bottom", {"start": v(-20, 521.15) * mm, "end": v(490, 521.15) * mm});
            skLineSegment(sketch, "E9.top", {"start": v(-20, -18.85) * mm, "end": v(490, -18.85) * mm});
            skLineSegment(sketch, "E9.left", {"start": v(-20, 521.15) * mm, "end": v(-20, -18.85) * mm});
            skLineSegment(sketch, "E9.right", {"start": v(490, 521.15) * mm, "end": v(490, -18.85) * mm});
            skLineSegment(sketch, "E10", {"start": v(-20, 521.15) * mm, "end": v(490, -18.85) * mm, "construction": true});
            skLineSegment(sketch, "E11", {"start": v(490, 521.15) * mm, "end": v(-20, -18.85) * mm, "construction": true});
            skPoint(sketch, "E12", {"position": v(235, 251.15) * mm});
            skSolve(sketch);
        }
        {
            var Q0;
            Q0=qSketchRegion(id+"F1",true);
            extrude(context, id + "F2", {"entities" : qUnion([Q0]), "depth" : 10 * mm});
        }
        {
            var Q0;
            Q0=qSketchRegion(id+"F0",true);
            extrude(context, id + "F3", {"entities" : qUnion([Q0]), "operationType" : NewBodyOperationType.REMOVE, "depth" : 8 * mm});
        }
        {
            var Q0;
            Q0=makeQuery(id+"F2.opExtrude","CAP_FACE",FACE,{"disambiguationData":[OSD([sQuery(id+"F1.wireOp",EDGE,"E9.bottom"),sQuery(id+"F1.wireOp",EDGE,"E9.top"),sQuery(id+"F1.wireOp",EDGE,"E9.left"),sQuery(id+"F1.wireOp",EDGE,"E9.right")])],"isStart":false});
            var sketch = newSketch(context, id + "F4", { "sketchPlane" : qUnion([Q0])});
            skLineSegment(sketch, "E13.bottom", {"start": v(490, 506.8) * mm, "end": v(-20, 506.8) * mm});
            skLineSegment(sketch, "E13.top", {"start": v(490, 497.8) * mm, "end": v(-20, 497.8) * mm});
            skLineSegment(sketch, "E13.left", {"start": v(490, 506.8) * mm, "end": v(490, 497.8) * mm});
            skLineSegment(sketch, "E13.right", {"start": v(-20, 506.8) * mm, "end": v(-20, 497.8) * mm});
            skLineSegment(sketch, "E14.0.1.0", {"start": v(490, 472.15) * mm, "end": v(-20, 472.15) * mm});
            skLineSegment(sketch, "E14.0.1.1", {"start": v(490, 463.15) * mm, "end": v(-20, 463.15) * mm});
            skLineSegment(sketch, "E14.0.1.2", {"start": v(490, 472.15) * mm, "end": v(490, 463.15) * mm});
            skLineSegment(sketch, "E14.0.1.3", {"start": v(-20, 472.15) * mm, "end": v(-20, 463.15) * mm});
            skLineSegment(sketch, "E14.0.2.0", {"start": v(490, 437.51) * mm, "end": v(-20, 437.51) * mm});
            skLineSegment(sketch, "E14.0.2.1", {"start": v(490, 428.51) * mm, "end": v(-20, 428.51) * mm});
            skLineSegment(sketch, "E14.0.2.2", {"start": v(490, 437.51) * mm, "end": v(490, 428.51) * mm});
            skLineSegment(sketch, "E14.0.2.3", {"start": v(-20, 437.51) * mm, "end": v(-20, 428.51) * mm});
            skLineSegment(sketch, "E14.0.3.0", {"start": v(490, 402.87) * mm, "end": v(-20, 402.87) * mm});
            skLineSegment(sketch, "E14.0.3.1", {"start": v(490, 393.87) * mm, "end": v(-20, 393.87) * mm});
            skLineSegment(sketch, "E14.0.3.2", {"start": v(490, 402.87) * mm, "end": v(490, 393.87) * mm});
            skLineSegment(sketch, "E14.0.3.3", {"start": v(-20, 402.87) * mm, "end": v(-20, 393.87) * mm});
            skLineSegment(sketch, "E14.0.4.0", {"start": v(490, 368.23) * mm, "end": v(-20, 368.23) * mm});
            skLineSegment(sketch, "E14.0.4.1", {"start": v(490, 359.23) * mm, "end": v(-20, 359.23) * mm});
            skLineSegment(sketch, "E14.0.4.2", {"start": v(490, 368.23) * mm, "end": v(490, 359.23) * mm});
            skLineSegment(sketch, "E14.0.4.3", {"start": v(-20, 368.23) * mm, "end": v(-20, 359.23) * mm});
            skLineSegment(sketch, "E14.0.5.0", {"start": v(490, 333.59) * mm, "end": v(-20, 333.59) * mm});
            skLineSegment(sketch, "E14.0.5.1", {"start": v(490, 324.59) * mm, "end": v(-20, 324.59) * mm});
            skLineSegment(sketch, "E14.0.5.2", {"start": v(490, 333.59) * mm, "end": v(490, 324.59) * mm});
            skLineSegment(sketch, "E14.0.5.3", {"start": v(-20, 333.59) * mm, "end": v(-20, 324.59) * mm});
            skLineSegment(sketch, "E14.0.6.0", {"start": v(490, 298.95) * mm, "end": v(-20, 298.95) * mm});
            skLineSegment(sketch, "E14.0.6.1", {"start": v(490, 289.95) * mm, "end": v(-20, 289.95) * mm});
            skLineSegment(sketch, "E14.0.6.2", {"start": v(490, 298.95) * mm, "end": v(490, 289.95) * mm});
            skLineSegment(sketch, "E14.0.6.3", {"start": v(-20, 298.95) * mm, "end": v(-20, 289.95) * mm});
            skLineSegment(sketch, "E14.0.7.0", {"start": v(490, 264.3) * mm, "end": v(-20, 264.3) * mm});
            skLineSegment(sketch, "E14.0.7.1", {"start": v(490, 255.3) * mm, "end": v(-20, 255.3) * mm});
            skLineSegment(sketch, "E14.0.7.2", {"start": v(490, 264.3) * mm, "end": v(490, 255.3) * mm});
            skLineSegment(sketch, "E14.0.7.3", {"start": v(-20, 264.3) * mm, "end": v(-20, 255.3) * mm});
            skLineSegment(sketch, "E14.0.8.0", {"start": v(490, 229.67) * mm, "end": v(-20, 229.67) * mm});
            skLineSegment(sketch, "E14.0.8.1", {"start": v(490, 220.67) * mm, "end": v(-20, 220.67) * mm});
            skLineSegment(sketch, "E14.0.8.2", {"start": v(490, 229.67) * mm, "end": v(490, 220.67) * mm});
            skLineSegment(sketch, "E14.0.8.3", {"start": v(-20, 229.67) * mm, "end": v(-20, 220.67) * mm});
            skLineSegment(sketch, "E14.0.9.0", {"start": v(490, 195.03) * mm, "end": v(-20, 195.03) * mm});
            skLineSegment(sketch, "E14.0.9.1", {"start": v(490, 186.03) * mm, "end": v(-20, 186.03) * mm});
            skLineSegment(sketch, "E14.0.9.2", {"start": v(490, 195.03) * mm, "end": v(490, 186.03) * mm});
            skLineSegment(sketch, "E14.0.9.3", {"start": v(-20, 195.03) * mm, "end": v(-20, 186.03) * mm});
            skLineSegment(sketch, "E14.0.10.0", {"start": v(490, 160.38) * mm, "end": v(-20, 160.38) * mm});
            skLineSegment(sketch, "E14.0.10.1", {"start": v(490, 151.38) * mm, "end": v(-20, 151.38) * mm});
            skLineSegment(sketch, "E14.0.10.2", {"start": v(490, 160.38) * mm, "end": v(490, 151.38) * mm});
            skLineSegment(sketch, "E14.0.10.3", {"start": v(-20, 160.38) * mm, "end": v(-20, 151.38) * mm});
            skLineSegment(sketch, "E14.0.11.0", {"start": v(490, 125.74) * mm, "end": v(-20, 125.74) * mm});
            skLineSegment(sketch, "E14.0.11.1", {"start": v(490, 116.74) * mm, "end": v(-20, 116.74) * mm});
            skLineSegment(sketch, "E14.0.11.2", {"start": v(490, 125.74) * mm, "end": v(490, 116.74) * mm});
            skLineSegment(sketch, "E14.0.11.3", {"start": v(-20, 125.74) * mm, "end": v(-20, 116.74) * mm});
            skLineSegment(sketch, "E14.0.12.0", {"start": v(490, 91.1) * mm, "end": v(-20, 91.1) * mm});
            skLineSegment(sketch, "E14.0.12.1", {"start": v(490, 82.1) * mm, "end": v(-20, 82.1) * mm});
            skLineSegment(sketch, "E14.0.12.2", {"start": v(490, 91.1) * mm, "end": v(490, 82.1) * mm});
            skLineSegment(sketch, "E14.0.12.3", {"start": v(-20, 91.1) * mm, "end": v(-20, 82.1) * mm});
            skLineSegment(sketch, "E14.0.13.0", {"start": v(490, 56.46) * mm, "end": v(-20, 56.46) * mm});
            skLineSegment(sketch, "E14.0.13.1", {"start": v(490, 47.46) * mm, "end": v(-20, 47.46) * mm});
            skLineSegment(sketch, "E14.0.13.2", {"start": v(490, 56.46) * mm, "end": v(490, 47.46) * mm});
            skLineSegment(sketch, "E14.0.13.3", {"start": v(-20, 56.46) * mm, "end": v(-20, 47.46) * mm});
            skLineSegment(sketch, "E14.0.14.0", {"start": v(490, 21.82) * mm, "end": v(-20, 21.82) * mm});
            skLineSegment(sketch, "E14.0.14.1", {"start": v(490, 12.82) * mm, "end": v(-20, 12.82) * mm});
            skLineSegment(sketch, "E14.0.14.2", {"start": v(490, 21.82) * mm, "end": v(490, 12.82) * mm});
            skLineSegment(sketch, "E14.0.14.3", {"start": v(-20, 21.82) * mm, "end": v(-20, 12.82) * mm});
            skLineSegment(sketch, "E14.direction1", {"start": v(-20, 497.8) * mm, "end": v(5, 497.8) * mm, "construction": true});
            skLineSegment(sketch, "E14.direction2", {"start": v(-20, 497.8) * mm, "end": v(-20, 463.15) * mm, "construction": true});
            skSolve(sketch);
        }
        {
            var Q0;
            Q0=qSketchRegion(id+"F4",true);
            extrude(context, id + "F5", {"entities" : qUnion([Q0]), "operationType" : NewBodyOperationType.REMOVE, "oppositeDirection" : true, "depth" : 2 * mm});
        }
        {
            var Q0;
            {var subQ0=sQuery(id+"F1.wireOp",EDGE,"E9.left");var subQ1=sQuery(id+"F1.wireOp",EDGE,"E9.right");Q0=makeQuery(id+"F5.boolean.opBoolean","SPLIT",FACE,{"disambiguationData":[TD([makeQuery(id+"F5.opExtrude","SWEPT_FACE",FACE,{"disambiguationData":[OSD([sQuery(id+"F4.wireOp",EDGE,"E13.top")])]})])],"derivedFrom":makeQuery(id+"F2.opExtrude","CAP_FACE",FACE,{"disambiguationData":[OSD([sQuery(id+"F1.wireOp",EDGE,"E9.bottom"),sQuery(id+"F1.wireOp",EDGE,"E9.top"),subQ0,subQ1])],"isStart":false})});}
            var sketch = newSketch(context, id + "F6", { "sketchPlane" : qUnion([Q0])});
            skLineSegment(sketch, "E15.bottom", {"start": v(-2.5, 479.97) * mm, "end": v(2.5, 479.97) * mm});
            skLineSegment(sketch, "E15.top", {"start": v(-4.5, 497.8) * mm, "end": v(4.5, 497.8) * mm});
            skLineSegment(sketch, "E15.left", {"start": v(-4.5, 481.97) * mm, "end": v(-4.5, 497.8) * mm});
            skLineSegment(sketch, "E15.right", {"start": v(4.5, 481.97) * mm, "end": v(4.5, 497.8) * mm});
            skPoint(sketch, "E16.visualSharp", {"position": v(-4.5, 479.97) * mm});
            skArc(sketch, "E16.filletArc", {"start": v(-4.5, 481.97) * mm, "mid": v(-3.91, 480.56) * mm, "end": v(-2.5, 479.97) * mm});
            skPoint(sketch, "E17.visualSharp", {"position": v(4.5, 479.97) * mm});
            skArc(sketch, "E17.filletArc", {"start": v(2.5, 479.97) * mm, "mid": v(3.91, 480.56) * mm, "end": v(4.5, 481.97) * mm});
            skLineSegment(sketch, "E18.0.1.0", {"start": v(-4.5, 447.33) * mm, "end": v(-4.5, 463.15) * mm});
            skLineSegment(sketch, "E18.0.1.1", {"start": v(4.5, 447.33) * mm, "end": v(4.5, 463.15) * mm});
            skPoint(sketch, "E18.0.1.2", {"position": v(4.5, 445.33) * mm});
            skPoint(sketch, "E18.0.1.3", {"position": v(-4.5, 445.33) * mm});
            skLineSegment(sketch, "E18.0.1.4", {"start": v(-4.5, 463.15) * mm, "end": v(4.5, 463.15) * mm});
            skArc(sketch, "E18.0.1.5", {"start": v(-4.5, 447.33) * mm, "mid": v(-3.91, 445.92) * mm, "end": v(-2.5, 445.33) * mm});
            skLineSegment(sketch, "E18.0.1.6", {"start": v(-2.5, 445.33) * mm, "end": v(2.5, 445.33) * mm});
            skArc(sketch, "E18.0.1.7", {"start": v(2.5, 445.33) * mm, "mid": v(3.91, 445.92) * mm, "end": v(4.5, 447.33) * mm});
            skLineSegment(sketch, "E18.0.2.0", {"start": v(-4.5, 412.7) * mm, "end": v(-4.5, 428.51) * mm});
            skLineSegment(sketch, "E18.0.2.1", {"start": v(4.5, 412.7) * mm, "end": v(4.5, 428.51) * mm});
            skPoint(sketch, "E18.0.2.2", {"position": v(4.5, 410.7) * mm});
            skPoint(sketch, "E18.0.2.3", {"position": v(-4.5, 410.7) * mm});
            skLineSegment(sketch, "E18.0.2.4", {"start": v(-4.5, 428.51) * mm, "end": v(4.5, 428.51) * mm});
            skArc(sketch, "E18.0.2.5", {"start": v(-4.5, 412.7) * mm, "mid": v(-3.91, 411.28) * mm, "end": v(-2.5, 410.7) * mm});
            skLineSegment(sketch, "E18.0.2.6", {"start": v(-2.5, 410.7) * mm, "end": v(2.5, 410.7) * mm});
            skArc(sketch, "E18.0.2.7", {"start": v(2.5, 410.7) * mm, "mid": v(3.91, 411.28) * mm, "end": v(4.5, 412.7) * mm});
            skLineSegment(sketch, "E18.0.3.0", {"start": v(-4.5, 378.05) * mm, "end": v(-4.5, 393.87) * mm});
            skLineSegment(sketch, "E18.0.3.1", {"start": v(4.5, 378.05) * mm, "end": v(4.5, 393.87) * mm});
            skPoint(sketch, "E18.0.3.2", {"position": v(4.5, 376.05) * mm});
            skPoint(sketch, "E18.0.3.3", {"position": v(-4.5, 376.05) * mm});
            skLineSegment(sketch, "E18.0.3.4", {"start": v(-4.5, 393.87) * mm, "end": v(4.5, 393.87) * mm});
            skArc(sketch, "E18.0.3.5", {"start": v(-4.5, 378.05) * mm, "mid": v(-3.91, 376.64) * mm, "end": v(-2.5, 376.05) * mm});
            skLineSegment(sketch, "E18.0.3.6", {"start": v(-2.5, 376.05) * mm, "end": v(2.5, 376.05) * mm});
            skArc(sketch, "E18.0.3.7", {"start": v(2.5, 376.05) * mm, "mid": v(3.91, 376.64) * mm, "end": v(4.5, 378.05) * mm});
            skLineSegment(sketch, "E18.0.4.0", {"start": v(-4.5, 343.41) * mm, "end": v(-4.5, 359.23) * mm});
            skLineSegment(sketch, "E18.0.4.1", {"start": v(4.5, 343.41) * mm, "end": v(4.5, 359.23) * mm});
            skPoint(sketch, "E18.0.4.2", {"position": v(4.5, 341.41) * mm});
            skPoint(sketch, "E18.0.4.3", {"position": v(-4.5, 341.41) * mm});
            skLineSegment(sketch, "E18.0.4.4", {"start": v(-4.5, 359.23) * mm, "end": v(4.5, 359.23) * mm});
            skArc(sketch, "E18.0.4.5", {"start": v(-4.5, 343.41) * mm, "mid": v(-3.91, 342) * mm, "end": v(-2.5, 341.41) * mm});
            skLineSegment(sketch, "E18.0.4.6", {"start": v(-2.5, 341.41) * mm, "end": v(2.5, 341.41) * mm});
            skArc(sketch, "E18.0.4.7", {"start": v(2.5, 341.41) * mm, "mid": v(3.91, 342) * mm, "end": v(4.5, 343.41) * mm});
            skLineSegment(sketch, "E18.0.5.0", {"start": v(-4.5, 308.77) * mm, "end": v(-4.5, 324.59) * mm});
            skLineSegment(sketch, "E18.0.5.1", {"start": v(4.5, 308.77) * mm, "end": v(4.5, 324.59) * mm});
            skPoint(sketch, "E18.0.5.2", {"position": v(4.5, 306.77) * mm});
            skPoint(sketch, "E18.0.5.3", {"position": v(-4.5, 306.77) * mm});
            skLineSegment(sketch, "E18.0.5.4", {"start": v(-4.5, 324.59) * mm, "end": v(4.5, 324.59) * mm});
            skArc(sketch, "E18.0.5.5", {"start": v(-4.5, 308.77) * mm, "mid": v(-3.91, 307.35) * mm, "end": v(-2.5, 306.77) * mm});
            skLineSegment(sketch, "E18.0.5.6", {"start": v(-2.5, 306.77) * mm, "end": v(2.5, 306.77) * mm});
            skArc(sketch, "E18.0.5.7", {"start": v(2.5, 306.77) * mm, "mid": v(3.91, 307.35) * mm, "end": v(4.5, 308.77) * mm});
            skLineSegment(sketch, "E18.0.6.0", {"start": v(-4.5, 274.13) * mm, "end": v(-4.5, 289.95) * mm});
            skLineSegment(sketch, "E18.0.6.1", {"start": v(4.5, 274.13) * mm, "end": v(4.5, 289.95) * mm});
            skPoint(sketch, "E18.0.6.2", {"position": v(4.5, 272.13) * mm});
            skPoint(sketch, "E18.0.6.3", {"position": v(-4.5, 272.13) * mm});
            skLineSegment(sketch, "E18.0.6.4", {"start": v(-4.5, 289.95) * mm, "end": v(4.5, 289.95) * mm});
            skArc(sketch, "E18.0.6.5", {"start": v(-4.5, 274.13) * mm, "mid": v(-3.91, 272.71) * mm, "end": v(-2.5, 272.13) * mm});
            skLineSegment(sketch, "E18.0.6.6", {"start": v(-2.5, 272.13) * mm, "end": v(2.5, 272.13) * mm});
            skArc(sketch, "E18.0.6.7", {"start": v(2.5, 272.13) * mm, "mid": v(3.91, 272.71) * mm, "end": v(4.5, 274.13) * mm});
            skLineSegment(sketch, "E18.0.7.0", {"start": v(-4.5, 239.49) * mm, "end": v(-4.5, 255.3) * mm});
            skLineSegment(sketch, "E18.0.7.1", {"start": v(4.5, 239.49) * mm, "end": v(4.5, 255.3) * mm});
            skPoint(sketch, "E18.0.7.2", {"position": v(4.5, 237.49) * mm});
            skPoint(sketch, "E18.0.7.3", {"position": v(-4.5, 237.49) * mm});
            skLineSegment(sketch, "E18.0.7.4", {"start": v(-4.5, 255.3) * mm, "end": v(4.5, 255.3) * mm});
            skArc(sketch, "E18.0.7.5", {"start": v(-4.5, 239.49) * mm, "mid": v(-3.91, 238.07) * mm, "end": v(-2.5, 237.49) * mm});
            skLineSegment(sketch, "E18.0.7.6", {"start": v(-2.5, 237.49) * mm, "end": v(2.5, 237.49) * mm});
            skArc(sketch, "E18.0.7.7", {"start": v(2.5, 237.49) * mm, "mid": v(3.91, 238.07) * mm, "end": v(4.5, 239.49) * mm});
            skLineSegment(sketch, "E18.0.8.0", {"start": v(-4.5, 204.85) * mm, "end": v(-4.5, 220.67) * mm});
            skLineSegment(sketch, "E18.0.8.1", {"start": v(4.5, 204.85) * mm, "end": v(4.5, 220.67) * mm});
            skPoint(sketch, "E18.0.8.2", {"position": v(4.5, 202.85) * mm});
            skPoint(sketch, "E18.0.8.3", {"position": v(-4.5, 202.85) * mm});
            skLineSegment(sketch, "E18.0.8.4", {"start": v(-4.5, 220.67) * mm, "end": v(4.5, 220.67) * mm});
            skArc(sketch, "E18.0.8.5", {"start": v(-4.5, 204.85) * mm, "mid": v(-3.91, 203.43) * mm, "end": v(-2.5, 202.85) * mm});
            skLineSegment(sketch, "E18.0.8.6", {"start": v(-2.5, 202.85) * mm, "end": v(2.5, 202.85) * mm});
            skArc(sketch, "E18.0.8.7", {"start": v(2.5, 202.85) * mm, "mid": v(3.91, 203.43) * mm, "end": v(4.5, 204.85) * mm});
            skLineSegment(sketch, "E18.0.9.0", {"start": v(-4.5, 170.2) * mm, "end": v(-4.5, 186.03) * mm});
            skLineSegment(sketch, "E18.0.9.1", {"start": v(4.5, 170.2) * mm, "end": v(4.5, 186.03) * mm});
            skPoint(sketch, "E18.0.9.2", {"position": v(4.5, 168.2) * mm});
            skPoint(sketch, "E18.0.9.3", {"position": v(-4.5, 168.2) * mm});
            skLineSegment(sketch, "E18.0.9.4", {"start": v(-4.5, 186.03) * mm, "end": v(4.5, 186.03) * mm});
            skArc(sketch, "E18.0.9.5", {"start": v(-4.5, 170.2) * mm, "mid": v(-3.91, 168.8) * mm, "end": v(-2.5, 168.2) * mm});
            skLineSegment(sketch, "E18.0.9.6", {"start": v(-2.5, 168.2) * mm, "end": v(2.5, 168.2) * mm});
            skArc(sketch, "E18.0.9.7", {"start": v(2.5, 168.2) * mm, "mid": v(3.91, 168.8) * mm, "end": v(4.5, 170.2) * mm});
            skLineSegment(sketch, "E18.0.10.0", {"start": v(-4.5, 135.56) * mm, "end": v(-4.5, 151.38) * mm});
            skLineSegment(sketch, "E18.0.10.1", {"start": v(4.5, 135.56) * mm, "end": v(4.5, 151.38) * mm});
            skPoint(sketch, "E18.0.10.2", {"position": v(4.5, 133.56) * mm});
            skPoint(sketch, "E18.0.10.3", {"position": v(-4.5, 133.56) * mm});
            skLineSegment(sketch, "E18.0.10.4", {"start": v(-4.5, 151.38) * mm, "end": v(4.5, 151.38) * mm});
            skArc(sketch, "E18.0.10.5", {"start": v(-4.5, 135.56) * mm, "mid": v(-3.91, 134.15) * mm, "end": v(-2.5, 133.56) * mm});
            skLineSegment(sketch, "E18.0.10.6", {"start": v(-2.5, 133.56) * mm, "end": v(2.5, 133.56) * mm});
            skArc(sketch, "E18.0.10.7", {"start": v(2.5, 133.56) * mm, "mid": v(3.91, 134.15) * mm, "end": v(4.5, 135.56) * mm});
            skLineSegment(sketch, "E18.0.11.0", {"start": v(-4.5, 100.92) * mm, "end": v(-4.5, 116.74) * mm});
            skLineSegment(sketch, "E18.0.11.1", {"start": v(4.5, 100.92) * mm, "end": v(4.5, 116.74) * mm});
            skPoint(sketch, "E18.0.11.2", {"position": v(4.5, 98.92) * mm});
            skPoint(sketch, "E18.0.11.3", {"position": v(-4.5, 98.92) * mm});
            skLineSegment(sketch, "E18.0.11.4", {"start": v(-4.5, 116.74) * mm, "end": v(4.5, 116.74) * mm});
            skArc(sketch, "E18.0.11.5", {"start": v(-4.5, 100.92) * mm, "mid": v(-3.91, 99.5) * mm, "end": v(-2.5, 98.92) * mm});
            skLineSegment(sketch, "E18.0.11.6", {"start": v(-2.5, 98.92) * mm, "end": v(2.5, 98.92) * mm});
            skArc(sketch, "E18.0.11.7", {"start": v(2.5, 98.92) * mm, "mid": v(3.91, 99.5) * mm, "end": v(4.5, 100.92) * mm});
            skLineSegment(sketch, "E18.0.12.0", {"start": v(-4.5, 66.28) * mm, "end": v(-4.5, 82.1) * mm});
            skLineSegment(sketch, "E18.0.12.1", {"start": v(4.5, 66.28) * mm, "end": v(4.5, 82.1) * mm});
            skPoint(sketch, "E18.0.12.2", {"position": v(4.5, 64.28) * mm});
            skPoint(sketch, "E18.0.12.3", {"position": v(-4.5, 64.28) * mm});
            skLineSegment(sketch, "E18.0.12.4", {"start": v(-4.5, 82.1) * mm, "end": v(4.5, 82.1) * mm});
            skArc(sketch, "E18.0.12.5", {"start": v(-4.5, 66.28) * mm, "mid": v(-3.91, 64.87) * mm, "end": v(-2.5, 64.28) * mm});
            skLineSegment(sketch, "E18.0.12.6", {"start": v(-2.5, 64.28) * mm, "end": v(2.5, 64.28) * mm});
            skArc(sketch, "E18.0.12.7", {"start": v(2.5, 64.28) * mm, "mid": v(3.91, 64.87) * mm, "end": v(4.5, 66.28) * mm});
            skLineSegment(sketch, "E18.0.13.0", {"start": v(-4.5, 31.64) * mm, "end": v(-4.5, 47.46) * mm});
            skLineSegment(sketch, "E18.0.13.1", {"start": v(4.5, 31.64) * mm, "end": v(4.5, 47.46) * mm});
            skPoint(sketch, "E18.0.13.2", {"position": v(4.5, 29.64) * mm});
            skPoint(sketch, "E18.0.13.3", {"position": v(-4.5, 29.64) * mm});
            skLineSegment(sketch, "E18.0.13.4", {"start": v(-4.5, 47.46) * mm, "end": v(4.5, 47.46) * mm});
            skArc(sketch, "E18.0.13.5", {"start": v(-4.5, 31.64) * mm, "mid": v(-3.91, 30.23) * mm, "end": v(-2.5, 29.64) * mm});
            skLineSegment(sketch, "E18.0.13.6", {"start": v(-2.5, 29.64) * mm, "end": v(2.5, 29.64) * mm});
            skArc(sketch, "E18.0.13.7", {"start": v(2.5, 29.64) * mm, "mid": v(3.91, 30.23) * mm, "end": v(4.5, 31.64) * mm});
            skLineSegment(sketch, "E18.0.14.0", {"start": v(-4.5, -3) * mm, "end": v(-4.5, 12.82) * mm});
            skLineSegment(sketch, "E18.0.14.1", {"start": v(4.5, -3) * mm, "end": v(4.5, 12.82) * mm});
            skPoint(sketch, "E18.0.14.2", {"position": v(4.5, -5) * mm});
            skPoint(sketch, "E18.0.14.3", {"position": v(-4.5, -5) * mm});
            skLineSegment(sketch, "E18.0.14.4", {"start": v(-4.5, 12.82) * mm, "end": v(4.5, 12.82) * mm});
            skArc(sketch, "E18.0.14.5", {"start": v(-4.5, -3) * mm, "mid": v(-3.91, -4.41) * mm, "end": v(-2.5, -5) * mm});
            skLineSegment(sketch, "E18.0.14.6", {"start": v(-2.5, -5) * mm, "end": v(2.5, -5) * mm});
            skArc(sketch, "E18.0.14.7", {"start": v(2.5, -5) * mm, "mid": v(3.91, -4.41) * mm, "end": v(4.5, -3) * mm});
            skLineSegment(sketch, "E18.1.0.0", {"start": v(15.5, 481.97) * mm, "end": v(15.5, 497.8) * mm});
            skLineSegment(sketch, "E18.1.0.1", {"start": v(24.5, 481.97) * mm, "end": v(24.5, 497.8) * mm});
            skPoint(sketch, "E18.1.0.2", {"position": v(24.5, 479.97) * mm});
            skPoint(sketch, "E18.1.0.3", {"position": v(15.5, 479.97) * mm});
            skLineSegment(sketch, "E18.1.0.4", {"start": v(15.5, 497.8) * mm, "end": v(24.5, 497.8) * mm});
            skArc(sketch, "E18.1.0.5", {"start": v(15.5, 481.97) * mm, "mid": v(16.09, 480.56) * mm, "end": v(17.5, 479.97) * mm});
            skLineSegment(sketch, "E18.1.0.6", {"start": v(17.5, 479.97) * mm, "end": v(22.5, 479.97) * mm});
            skArc(sketch, "E18.1.0.7", {"start": v(22.5, 479.97) * mm, "mid": v(23.91, 480.56) * mm, "end": v(24.5, 481.97) * mm});
            skLineSegment(sketch, "E18.1.1.0", {"start": v(15.5, 447.33) * mm, "end": v(15.5, 463.15) * mm});
            skLineSegment(sketch, "E18.1.1.1", {"start": v(24.5, 447.33) * mm, "end": v(24.5, 463.15) * mm});
            skPoint(sketch, "E18.1.1.2", {"position": v(24.5, 445.33) * mm});
            skPoint(sketch, "E18.1.1.3", {"position": v(15.5, 445.33) * mm});
            skLineSegment(sketch, "E18.1.1.4", {"start": v(15.5, 463.15) * mm, "end": v(24.5, 463.15) * mm});
            skArc(sketch, "E18.1.1.5", {"start": v(15.5, 447.33) * mm, "mid": v(16.09, 445.92) * mm, "end": v(17.5, 445.33) * mm});
            skLineSegment(sketch, "E18.1.1.6", {"start": v(17.5, 445.33) * mm, "end": v(22.5, 445.33) * mm});
            skArc(sketch, "E18.1.1.7", {"start": v(22.5, 445.33) * mm, "mid": v(23.91, 445.92) * mm, "end": v(24.5, 447.33) * mm});
            skLineSegment(sketch, "E18.1.2.0", {"start": v(15.5, 412.7) * mm, "end": v(15.5, 428.51) * mm});
            skLineSegment(sketch, "E18.1.2.1", {"start": v(24.5, 412.7) * mm, "end": v(24.5, 428.51) * mm});
            skPoint(sketch, "E18.1.2.2", {"position": v(24.5, 410.7) * mm});
            skPoint(sketch, "E18.1.2.3", {"position": v(15.5, 410.7) * mm});
            skLineSegment(sketch, "E18.1.2.4", {"start": v(15.5, 428.51) * mm, "end": v(24.5, 428.51) * mm});
            skArc(sketch, "E18.1.2.5", {"start": v(15.5, 412.7) * mm, "mid": v(16.09, 411.28) * mm, "end": v(17.5, 410.7) * mm});
            skLineSegment(sketch, "E18.1.2.6", {"start": v(17.5, 410.7) * mm, "end": v(22.5, 410.7) * mm});
            skArc(sketch, "E18.1.2.7", {"start": v(22.5, 410.7) * mm, "mid": v(23.91, 411.28) * mm, "end": v(24.5, 412.7) * mm});
            skLineSegment(sketch, "E18.1.3.0", {"start": v(15.5, 378.05) * mm, "end": v(15.5, 393.87) * mm});
            skLineSegment(sketch, "E18.1.3.1", {"start": v(24.5, 378.05) * mm, "end": v(24.5, 393.87) * mm});
            skPoint(sketch, "E18.1.3.2", {"position": v(24.5, 376.05) * mm});
            skPoint(sketch, "E18.1.3.3", {"position": v(15.5, 376.05) * mm});
            skLineSegment(sketch, "E18.1.3.4", {"start": v(15.5, 393.87) * mm, "end": v(24.5, 393.87) * mm});
            skArc(sketch, "E18.1.3.5", {"start": v(15.5, 378.05) * mm, "mid": v(16.09, 376.64) * mm, "end": v(17.5, 376.05) * mm});
            skLineSegment(sketch, "E18.1.3.6", {"start": v(17.5, 376.05) * mm, "end": v(22.5, 376.05) * mm});
            skArc(sketch, "E18.1.3.7", {"start": v(22.5, 376.05) * mm, "mid": v(23.91, 376.64) * mm, "end": v(24.5, 378.05) * mm});
            skLineSegment(sketch, "E18.1.4.0", {"start": v(15.5, 343.41) * mm, "end": v(15.5, 359.23) * mm});
            skLineSegment(sketch, "E18.1.4.1", {"start": v(24.5, 343.41) * mm, "end": v(24.5, 359.23) * mm});
            skPoint(sketch, "E18.1.4.2", {"position": v(24.5, 341.41) * mm});
            skPoint(sketch, "E18.1.4.3", {"position": v(15.5, 341.41) * mm});
            skLineSegment(sketch, "E18.1.4.4", {"start": v(15.5, 359.23) * mm, "end": v(24.5, 359.23) * mm});
            skArc(sketch, "E18.1.4.5", {"start": v(15.5, 343.41) * mm, "mid": v(16.09, 342) * mm, "end": v(17.5, 341.41) * mm});
            skLineSegment(sketch, "E18.1.4.6", {"start": v(17.5, 341.41) * mm, "end": v(22.5, 341.41) * mm});
            skArc(sketch, "E18.1.4.7", {"start": v(22.5, 341.41) * mm, "mid": v(23.91, 342) * mm, "end": v(24.5, 343.41) * mm});
            skLineSegment(sketch, "E18.1.5.0", {"start": v(15.5, 308.77) * mm, "end": v(15.5, 324.59) * mm});
            skLineSegment(sketch, "E18.1.5.1", {"start": v(24.5, 308.77) * mm, "end": v(24.5, 324.59) * mm});
            skPoint(sketch, "E18.1.5.2", {"position": v(24.5, 306.77) * mm});
            skPoint(sketch, "E18.1.5.3", {"position": v(15.5, 306.77) * mm});
            skLineSegment(sketch, "E18.1.5.4", {"start": v(15.5, 324.59) * mm, "end": v(24.5, 324.59) * mm});
            skArc(sketch, "E18.1.5.5", {"start": v(15.5, 308.77) * mm, "mid": v(16.09, 307.35) * mm, "end": v(17.5, 306.77) * mm});
            skLineSegment(sketch, "E18.1.5.6", {"start": v(17.5, 306.77) * mm, "end": v(22.5, 306.77) * mm});
            skArc(sketch, "E18.1.5.7", {"start": v(22.5, 306.77) * mm, "mid": v(23.91, 307.35) * mm, "end": v(24.5, 308.77) * mm});
            skLineSegment(sketch, "E18.1.6.0", {"start": v(15.5, 274.13) * mm, "end": v(15.5, 289.95) * mm});
            skLineSegment(sketch, "E18.1.6.1", {"start": v(24.5, 274.13) * mm, "end": v(24.5, 289.95) * mm});
            skPoint(sketch, "E18.1.6.2", {"position": v(24.5, 272.13) * mm});
            skPoint(sketch, "E18.1.6.3", {"position": v(15.5, 272.13) * mm});
            skLineSegment(sketch, "E18.1.6.4", {"start": v(15.5, 289.95) * mm, "end": v(24.5, 289.95) * mm});
            skArc(sketch, "E18.1.6.5", {"start": v(15.5, 274.13) * mm, "mid": v(16.09, 272.71) * mm, "end": v(17.5, 272.13) * mm});
            skLineSegment(sketch, "E18.1.6.6", {"start": v(17.5, 272.13) * mm, "end": v(22.5, 272.13) * mm});
            skArc(sketch, "E18.1.6.7", {"start": v(22.5, 272.13) * mm, "mid": v(23.91, 272.71) * mm, "end": v(24.5, 274.13) * mm});
            skLineSegment(sketch, "E18.1.7.0", {"start": v(15.5, 239.49) * mm, "end": v(15.5, 255.3) * mm});
            skLineSegment(sketch, "E18.1.7.1", {"start": v(24.5, 239.49) * mm, "end": v(24.5, 255.3) * mm});
            skPoint(sketch, "E18.1.7.2", {"position": v(24.5, 237.49) * mm});
            skPoint(sketch, "E18.1.7.3", {"position": v(15.5, 237.49) * mm});
            skLineSegment(sketch, "E18.1.7.4", {"start": v(15.5, 255.3) * mm, "end": v(24.5, 255.3) * mm});
            skArc(sketch, "E18.1.7.5", {"start": v(15.5, 239.49) * mm, "mid": v(16.09, 238.07) * mm, "end": v(17.5, 237.49) * mm});
            skLineSegment(sketch, "E18.1.7.6", {"start": v(17.5, 237.49) * mm, "end": v(22.5, 237.49) * mm});
            skArc(sketch, "E18.1.7.7", {"start": v(22.5, 237.49) * mm, "mid": v(23.91, 238.07) * mm, "end": v(24.5, 239.49) * mm});
            skLineSegment(sketch, "E18.1.8.0", {"start": v(15.5, 204.85) * mm, "end": v(15.5, 220.67) * mm});
            skLineSegment(sketch, "E18.1.8.1", {"start": v(24.5, 204.85) * mm, "end": v(24.5, 220.67) * mm});
            skPoint(sketch, "E18.1.8.2", {"position": v(24.5, 202.85) * mm});
            skPoint(sketch, "E18.1.8.3", {"position": v(15.5, 202.85) * mm});
            skLineSegment(sketch, "E18.1.8.4", {"start": v(15.5, 220.67) * mm, "end": v(24.5, 220.67) * mm});
            skArc(sketch, "E18.1.8.5", {"start": v(15.5, 204.85) * mm, "mid": v(16.09, 203.43) * mm, "end": v(17.5, 202.85) * mm});
            skLineSegment(sketch, "E18.1.8.6", {"start": v(17.5, 202.85) * mm, "end": v(22.5, 202.85) * mm});
            skArc(sketch, "E18.1.8.7", {"start": v(22.5, 202.85) * mm, "mid": v(23.91, 203.43) * mm, "end": v(24.5, 204.85) * mm});
            skLineSegment(sketch, "E18.1.9.0", {"start": v(15.5, 170.2) * mm, "end": v(15.5, 186.03) * mm});
            skLineSegment(sketch, "E18.1.9.1", {"start": v(24.5, 170.2) * mm, "end": v(24.5, 186.03) * mm});
            skPoint(sketch, "E18.1.9.2", {"position": v(24.5, 168.2) * mm});
            skPoint(sketch, "E18.1.9.3", {"position": v(15.5, 168.2) * mm});
            skLineSegment(sketch, "E18.1.9.4", {"start": v(15.5, 186.03) * mm, "end": v(24.5, 186.03) * mm});
            skArc(sketch, "E18.1.9.5", {"start": v(15.5, 170.2) * mm, "mid": v(16.09, 168.8) * mm, "end": v(17.5, 168.2) * mm});
            skLineSegment(sketch, "E18.1.9.6", {"start": v(17.5, 168.2) * mm, "end": v(22.5, 168.2) * mm});
            skArc(sketch, "E18.1.9.7", {"start": v(22.5, 168.2) * mm, "mid": v(23.91, 168.8) * mm, "end": v(24.5, 170.2) * mm});
            skLineSegment(sketch, "E18.1.10.0", {"start": v(15.5, 135.56) * mm, "end": v(15.5, 151.38) * mm});
            skLineSegment(sketch, "E18.1.10.1", {"start": v(24.5, 135.56) * mm, "end": v(24.5, 151.38) * mm});
            skPoint(sketch, "E18.1.10.2", {"position": v(24.5, 133.56) * mm});
            skPoint(sketch, "E18.1.10.3", {"position": v(15.5, 133.56) * mm});
            skLineSegment(sketch, "E18.1.10.4", {"start": v(15.5, 151.38) * mm, "end": v(24.5, 151.38) * mm});
            skArc(sketch, "E18.1.10.5", {"start": v(15.5, 135.56) * mm, "mid": v(16.09, 134.15) * mm, "end": v(17.5, 133.56) * mm});
            skLineSegment(sketch, "E18.1.10.6", {"start": v(17.5, 133.56) * mm, "end": v(22.5, 133.56) * mm});
            skArc(sketch, "E18.1.10.7", {"start": v(22.5, 133.56) * mm, "mid": v(23.91, 134.15) * mm, "end": v(24.5, 135.56) * mm});
            skLineSegment(sketch, "E18.1.11.0", {"start": v(15.5, 100.92) * mm, "end": v(15.5, 116.74) * mm});
            skLineSegment(sketch, "E18.1.11.1", {"start": v(24.5, 100.92) * mm, "end": v(24.5, 116.74) * mm});
            skPoint(sketch, "E18.1.11.2", {"position": v(24.5, 98.92) * mm});
            skPoint(sketch, "E18.1.11.3", {"position": v(15.5, 98.92) * mm});
            skLineSegment(sketch, "E18.1.11.4", {"start": v(15.5, 116.74) * mm, "end": v(24.5, 116.74) * mm});
            skArc(sketch, "E18.1.11.5", {"start": v(15.5, 100.92) * mm, "mid": v(16.09, 99.5) * mm, "end": v(17.5, 98.92) * mm});
            skLineSegment(sketch, "E18.1.11.6", {"start": v(17.5, 98.92) * mm, "end": v(22.5, 98.92) * mm});
            skArc(sketch, "E18.1.11.7", {"start": v(22.5, 98.92) * mm, "mid": v(23.91, 99.5) * mm, "end": v(24.5, 100.92) * mm});
            skLineSegment(sketch, "E18.1.12.0", {"start": v(15.5, 66.28) * mm, "end": v(15.5, 82.1) * mm});
            skLineSegment(sketch, "E18.1.12.1", {"start": v(24.5, 66.28) * mm, "end": v(24.5, 82.1) * mm});
            skPoint(sketch, "E18.1.12.2", {"position": v(24.5, 64.28) * mm});
            skPoint(sketch, "E18.1.12.3", {"position": v(15.5, 64.28) * mm});
            skLineSegment(sketch, "E18.1.12.4", {"start": v(15.5, 82.1) * mm, "end": v(24.5, 82.1) * mm});
            skArc(sketch, "E18.1.12.5", {"start": v(15.5, 66.28) * mm, "mid": v(16.09, 64.87) * mm, "end": v(17.5, 64.28) * mm});
            skLineSegment(sketch, "E18.1.12.6", {"start": v(17.5, 64.28) * mm, "end": v(22.5, 64.28) * mm});
            skArc(sketch, "E18.1.12.7", {"start": v(22.5, 64.28) * mm, "mid": v(23.91, 64.87) * mm, "end": v(24.5, 66.28) * mm});
            skLineSegment(sketch, "E18.1.13.0", {"start": v(15.5, 31.64) * mm, "end": v(15.5, 47.46) * mm});
            skLineSegment(sketch, "E18.1.13.1", {"start": v(24.5, 31.64) * mm, "end": v(24.5, 47.46) * mm});
            skPoint(sketch, "E18.1.13.2", {"position": v(24.5, 29.64) * mm});
            skPoint(sketch, "E18.1.13.3", {"position": v(15.5, 29.64) * mm});
            skLineSegment(sketch, "E18.1.13.4", {"start": v(15.5, 47.46) * mm, "end": v(24.5, 47.46) * mm});
            skArc(sketch, "E18.1.13.5", {"start": v(15.5, 31.64) * mm, "mid": v(16.09, 30.23) * mm, "end": v(17.5, 29.64) * mm});
            skLineSegment(sketch, "E18.1.13.6", {"start": v(17.5, 29.64) * mm, "end": v(22.5, 29.64) * mm});
            skArc(sketch, "E18.1.13.7", {"start": v(22.5, 29.64) * mm, "mid": v(23.91, 30.23) * mm, "end": v(24.5, 31.64) * mm});
            skLineSegment(sketch, "E18.1.14.0", {"start": v(15.5, -3) * mm, "end": v(15.5, 12.82) * mm});
            skLineSegment(sketch, "E18.1.14.1", {"start": v(24.5, -3) * mm, "end": v(24.5, 12.82) * mm});
            skPoint(sketch, "E18.1.14.2", {"position": v(24.5, -5) * mm});
            skPoint(sketch, "E18.1.14.3", {"position": v(15.5, -5) * mm});
            skLineSegment(sketch, "E18.1.14.4", {"start": v(15.5, 12.82) * mm, "end": v(24.5, 12.82) * mm});
            skArc(sketch, "E18.1.14.5", {"start": v(15.5, -3) * mm, "mid": v(16.09, -4.41) * mm, "end": v(17.5, -5) * mm});
            skLineSegment(sketch, "E18.1.14.6", {"start": v(17.5, -5) * mm, "end": v(22.5, -5) * mm});
            skArc(sketch, "E18.1.14.7", {"start": v(22.5, -5) * mm, "mid": v(23.91, -4.41) * mm, "end": v(24.5, -3) * mm});
            skLineSegment(sketch, "E18.2.0.0", {"start": v(35.5, 481.97) * mm, "end": v(35.5, 497.8) * mm});
            skLineSegment(sketch, "E18.2.0.1", {"start": v(44.5, 481.97) * mm, "end": v(44.5, 497.8) * mm});
            skPoint(sketch, "E18.2.0.2", {"position": v(44.5, 479.97) * mm});
            skPoint(sketch, "E18.2.0.3", {"position": v(35.5, 479.97) * mm});
            skLineSegment(sketch, "E18.2.0.4", {"start": v(35.5, 497.8) * mm, "end": v(44.5, 497.8) * mm});
            skArc(sketch, "E18.2.0.5", {"start": v(35.5, 481.97) * mm, "mid": v(36.09, 480.56) * mm, "end": v(37.5, 479.97) * mm});
            skLineSegment(sketch, "E18.2.0.6", {"start": v(37.5, 479.97) * mm, "end": v(42.5, 479.97) * mm});
            skArc(sketch, "E18.2.0.7", {"start": v(42.5, 479.97) * mm, "mid": v(43.91, 480.56) * mm, "end": v(44.5, 481.97) * mm});
            skLineSegment(sketch, "E18.2.1.0", {"start": v(35.5, 447.33) * mm, "end": v(35.5, 463.15) * mm});
            skLineSegment(sketch, "E18.2.1.1", {"start": v(44.5, 447.33) * mm, "end": v(44.5, 463.15) * mm});
            skPoint(sketch, "E18.2.1.2", {"position": v(44.5, 445.33) * mm});
            skPoint(sketch, "E18.2.1.3", {"position": v(35.5, 445.33) * mm});
            skLineSegment(sketch, "E18.2.1.4", {"start": v(35.5, 463.15) * mm, "end": v(44.5, 463.15) * mm});
            skArc(sketch, "E18.2.1.5", {"start": v(35.5, 447.33) * mm, "mid": v(36.09, 445.92) * mm, "end": v(37.5, 445.33) * mm});
            skLineSegment(sketch, "E18.2.1.6", {"start": v(37.5, 445.33) * mm, "end": v(42.5, 445.33) * mm});
            skArc(sketch, "E18.2.1.7", {"start": v(42.5, 445.33) * mm, "mid": v(43.91, 445.92) * mm, "end": v(44.5, 447.33) * mm});
            skLineSegment(sketch, "E18.2.2.0", {"start": v(35.5, 412.7) * mm, "end": v(35.5, 428.51) * mm});
            skLineSegment(sketch, "E18.2.2.1", {"start": v(44.5, 412.7) * mm, "end": v(44.5, 428.51) * mm});
            skPoint(sketch, "E18.2.2.2", {"position": v(44.5, 410.7) * mm});
            skPoint(sketch, "E18.2.2.3", {"position": v(35.5, 410.7) * mm});
            skLineSegment(sketch, "E18.2.2.4", {"start": v(35.5, 428.51) * mm, "end": v(44.5, 428.51) * mm});
            skArc(sketch, "E18.2.2.5", {"start": v(35.5, 412.7) * mm, "mid": v(36.09, 411.28) * mm, "end": v(37.5, 410.7) * mm});
            skLineSegment(sketch, "E18.2.2.6", {"start": v(37.5, 410.7) * mm, "end": v(42.5, 410.7) * mm});
            skArc(sketch, "E18.2.2.7", {"start": v(42.5, 410.7) * mm, "mid": v(43.91, 411.28) * mm, "end": v(44.5, 412.7) * mm});
            skLineSegment(sketch, "E18.2.3.0", {"start": v(35.5, 378.05) * mm, "end": v(35.5, 393.87) * mm});
            skLineSegment(sketch, "E18.2.3.1", {"start": v(44.5, 378.05) * mm, "end": v(44.5, 393.87) * mm});
            skPoint(sketch, "E18.2.3.2", {"position": v(44.5, 376.05) * mm});
            skPoint(sketch, "E18.2.3.3", {"position": v(35.5, 376.05) * mm});
            skLineSegment(sketch, "E18.2.3.4", {"start": v(35.5, 393.87) * mm, "end": v(44.5, 393.87) * mm});
            skArc(sketch, "E18.2.3.5", {"start": v(35.5, 378.05) * mm, "mid": v(36.09, 376.64) * mm, "end": v(37.5, 376.05) * mm});
            skLineSegment(sketch, "E18.2.3.6", {"start": v(37.5, 376.05) * mm, "end": v(42.5, 376.05) * mm});
            skArc(sketch, "E18.2.3.7", {"start": v(42.5, 376.05) * mm, "mid": v(43.91, 376.64) * mm, "end": v(44.5, 378.05) * mm});
            skLineSegment(sketch, "E18.2.4.0", {"start": v(35.5, 343.41) * mm, "end": v(35.5, 359.23) * mm});
            skLineSegment(sketch, "E18.2.4.1", {"start": v(44.5, 343.41) * mm, "end": v(44.5, 359.23) * mm});
            skPoint(sketch, "E18.2.4.2", {"position": v(44.5, 341.41) * mm});
            skPoint(sketch, "E18.2.4.3", {"position": v(35.5, 341.41) * mm});
            skLineSegment(sketch, "E18.2.4.4", {"start": v(35.5, 359.23) * mm, "end": v(44.5, 359.23) * mm});
            skArc(sketch, "E18.2.4.5", {"start": v(35.5, 343.41) * mm, "mid": v(36.09, 342) * mm, "end": v(37.5, 341.41) * mm});
            skLineSegment(sketch, "E18.2.4.6", {"start": v(37.5, 341.41) * mm, "end": v(42.5, 341.41) * mm});
            skArc(sketch, "E18.2.4.7", {"start": v(42.5, 341.41) * mm, "mid": v(43.91, 342) * mm, "end": v(44.5, 343.41) * mm});
            skLineSegment(sketch, "E18.2.5.0", {"start": v(35.5, 308.77) * mm, "end": v(35.5, 324.59) * mm});
            skLineSegment(sketch, "E18.2.5.1", {"start": v(44.5, 308.77) * mm, "end": v(44.5, 324.59) * mm});
            skPoint(sketch, "E18.2.5.2", {"position": v(44.5, 306.77) * mm});
            skPoint(sketch, "E18.2.5.3", {"position": v(35.5, 306.77) * mm});
            skLineSegment(sketch, "E18.2.5.4", {"start": v(35.5, 324.59) * mm, "end": v(44.5, 324.59) * mm});
            skArc(sketch, "E18.2.5.5", {"start": v(35.5, 308.77) * mm, "mid": v(36.09, 307.35) * mm, "end": v(37.5, 306.77) * mm});
            skLineSegment(sketch, "E18.2.5.6", {"start": v(37.5, 306.77) * mm, "end": v(42.5, 306.77) * mm});
            skArc(sketch, "E18.2.5.7", {"start": v(42.5, 306.77) * mm, "mid": v(43.91, 307.35) * mm, "end": v(44.5, 308.77) * mm});
            skLineSegment(sketch, "E18.2.6.0", {"start": v(35.5, 274.13) * mm, "end": v(35.5, 289.95) * mm});
            skLineSegment(sketch, "E18.2.6.1", {"start": v(44.5, 274.13) * mm, "end": v(44.5, 289.95) * mm});
            skPoint(sketch, "E18.2.6.2", {"position": v(44.5, 272.13) * mm});
            skPoint(sketch, "E18.2.6.3", {"position": v(35.5, 272.13) * mm});
            skLineSegment(sketch, "E18.2.6.4", {"start": v(35.5, 289.95) * mm, "end": v(44.5, 289.95) * mm});
            skArc(sketch, "E18.2.6.5", {"start": v(35.5, 274.13) * mm, "mid": v(36.09, 272.71) * mm, "end": v(37.5, 272.13) * mm});
            skLineSegment(sketch, "E18.2.6.6", {"start": v(37.5, 272.13) * mm, "end": v(42.5, 272.13) * mm});
            skArc(sketch, "E18.2.6.7", {"start": v(42.5, 272.13) * mm, "mid": v(43.91, 272.71) * mm, "end": v(44.5, 274.13) * mm});
            skLineSegment(sketch, "E18.2.7.0", {"start": v(35.5, 239.49) * mm, "end": v(35.5, 255.3) * mm});
            skLineSegment(sketch, "E18.2.7.1", {"start": v(44.5, 239.49) * mm, "end": v(44.5, 255.3) * mm});
            skPoint(sketch, "E18.2.7.2", {"position": v(44.5, 237.49) * mm});
            skPoint(sketch, "E18.2.7.3", {"position": v(35.5, 237.49) * mm});
            skLineSegment(sketch, "E18.2.7.4", {"start": v(35.5, 255.3) * mm, "end": v(44.5, 255.3) * mm});
            skArc(sketch, "E18.2.7.5", {"start": v(35.5, 239.49) * mm, "mid": v(36.09, 238.07) * mm, "end": v(37.5, 237.49) * mm});
            skLineSegment(sketch, "E18.2.7.6", {"start": v(37.5, 237.49) * mm, "end": v(42.5, 237.49) * mm});
            skArc(sketch, "E18.2.7.7", {"start": v(42.5, 237.49) * mm, "mid": v(43.91, 238.07) * mm, "end": v(44.5, 239.49) * mm});
            skLineSegment(sketch, "E18.2.8.0", {"start": v(35.5, 204.85) * mm, "end": v(35.5, 220.67) * mm});
            skLineSegment(sketch, "E18.2.8.1", {"start": v(44.5, 204.85) * mm, "end": v(44.5, 220.67) * mm});
            skPoint(sketch, "E18.2.8.2", {"position": v(44.5, 202.85) * mm});
            skPoint(sketch, "E18.2.8.3", {"position": v(35.5, 202.85) * mm});
            skLineSegment(sketch, "E18.2.8.4", {"start": v(35.5, 220.67) * mm, "end": v(44.5, 220.67) * mm});
            skArc(sketch, "E18.2.8.5", {"start": v(35.5, 204.85) * mm, "mid": v(36.09, 203.43) * mm, "end": v(37.5, 202.85) * mm});
            skLineSegment(sketch, "E18.2.8.6", {"start": v(37.5, 202.85) * mm, "end": v(42.5, 202.85) * mm});
            skArc(sketch, "E18.2.8.7", {"start": v(42.5, 202.85) * mm, "mid": v(43.91, 203.43) * mm, "end": v(44.5, 204.85) * mm});
            skLineSegment(sketch, "E18.2.9.0", {"start": v(35.5, 170.2) * mm, "end": v(35.5, 186.03) * mm});
            skLineSegment(sketch, "E18.2.9.1", {"start": v(44.5, 170.2) * mm, "end": v(44.5, 186.03) * mm});
            skPoint(sketch, "E18.2.9.2", {"position": v(44.5, 168.2) * mm});
            skPoint(sketch, "E18.2.9.3", {"position": v(35.5, 168.2) * mm});
            skLineSegment(sketch, "E18.2.9.4", {"start": v(35.5, 186.03) * mm, "end": v(44.5, 186.03) * mm});
            skArc(sketch, "E18.2.9.5", {"start": v(35.5, 170.2) * mm, "mid": v(36.09, 168.8) * mm, "end": v(37.5, 168.2) * mm});
            skLineSegment(sketch, "E18.2.9.6", {"start": v(37.5, 168.2) * mm, "end": v(42.5, 168.2) * mm});
            skArc(sketch, "E18.2.9.7", {"start": v(42.5, 168.2) * mm, "mid": v(43.91, 168.8) * mm, "end": v(44.5, 170.2) * mm});
            skLineSegment(sketch, "E18.2.10.0", {"start": v(35.5, 135.56) * mm, "end": v(35.5, 151.38) * mm});
            skLineSegment(sketch, "E18.2.10.1", {"start": v(44.5, 135.56) * mm, "end": v(44.5, 151.38) * mm});
            skPoint(sketch, "E18.2.10.2", {"position": v(44.5, 133.56) * mm});
            skPoint(sketch, "E18.2.10.3", {"position": v(35.5, 133.56) * mm});
            skLineSegment(sketch, "E18.2.10.4", {"start": v(35.5, 151.38) * mm, "end": v(44.5, 151.38) * mm});
            skArc(sketch, "E18.2.10.5", {"start": v(35.5, 135.56) * mm, "mid": v(36.09, 134.15) * mm, "end": v(37.5, 133.56) * mm});
            skLineSegment(sketch, "E18.2.10.6", {"start": v(37.5, 133.56) * mm, "end": v(42.5, 133.56) * mm});
            skArc(sketch, "E18.2.10.7", {"start": v(42.5, 133.56) * mm, "mid": v(43.91, 134.15) * mm, "end": v(44.5, 135.56) * mm});
            skLineSegment(sketch, "E18.2.11.0", {"start": v(35.5, 100.92) * mm, "end": v(35.5, 116.74) * mm});
            skLineSegment(sketch, "E18.2.11.1", {"start": v(44.5, 100.92) * mm, "end": v(44.5, 116.74) * mm});
            skPoint(sketch, "E18.2.11.2", {"position": v(44.5, 98.92) * mm});
            skPoint(sketch, "E18.2.11.3", {"position": v(35.5, 98.92) * mm});
            skLineSegment(sketch, "E18.2.11.4", {"start": v(35.5, 116.74) * mm, "end": v(44.5, 116.74) * mm});
            skArc(sketch, "E18.2.11.5", {"start": v(35.5, 100.92) * mm, "mid": v(36.09, 99.5) * mm, "end": v(37.5, 98.92) * mm});
            skLineSegment(sketch, "E18.2.11.6", {"start": v(37.5, 98.92) * mm, "end": v(42.5, 98.92) * mm});
            skArc(sketch, "E18.2.11.7", {"start": v(42.5, 98.92) * mm, "mid": v(43.91, 99.5) * mm, "end": v(44.5, 100.92) * mm});
            skLineSegment(sketch, "E18.2.12.0", {"start": v(35.5, 66.28) * mm, "end": v(35.5, 82.1) * mm});
            skLineSegment(sketch, "E18.2.12.1", {"start": v(44.5, 66.28) * mm, "end": v(44.5, 82.1) * mm});
            skPoint(sketch, "E18.2.12.2", {"position": v(44.5, 64.28) * mm});
            skPoint(sketch, "E18.2.12.3", {"position": v(35.5, 64.28) * mm});
            skLineSegment(sketch, "E18.2.12.4", {"start": v(35.5, 82.1) * mm, "end": v(44.5, 82.1) * mm});
            skArc(sketch, "E18.2.12.5", {"start": v(35.5, 66.28) * mm, "mid": v(36.09, 64.87) * mm, "end": v(37.5, 64.28) * mm});
            skLineSegment(sketch, "E18.2.12.6", {"start": v(37.5, 64.28) * mm, "end": v(42.5, 64.28) * mm});
            skArc(sketch, "E18.2.12.7", {"start": v(42.5, 64.28) * mm, "mid": v(43.91, 64.87) * mm, "end": v(44.5, 66.28) * mm});
            skLineSegment(sketch, "E18.2.13.0", {"start": v(35.5, 31.64) * mm, "end": v(35.5, 47.46) * mm});
            skLineSegment(sketch, "E18.2.13.1", {"start": v(44.5, 31.64) * mm, "end": v(44.5, 47.46) * mm});
            skPoint(sketch, "E18.2.13.2", {"position": v(44.5, 29.64) * mm});
            skPoint(sketch, "E18.2.13.3", {"position": v(35.5, 29.64) * mm});
            skLineSegment(sketch, "E18.2.13.4", {"start": v(35.5, 47.46) * mm, "end": v(44.5, 47.46) * mm});
            skArc(sketch, "E18.2.13.5", {"start": v(35.5, 31.64) * mm, "mid": v(36.09, 30.23) * mm, "end": v(37.5, 29.64) * mm});
            skLineSegment(sketch, "E18.2.13.6", {"start": v(37.5, 29.64) * mm, "end": v(42.5, 29.64) * mm});
            skArc(sketch, "E18.2.13.7", {"start": v(42.5, 29.64) * mm, "mid": v(43.91, 30.23) * mm, "end": v(44.5, 31.64) * mm});
            skLineSegment(sketch, "E18.2.14.0", {"start": v(35.5, -3) * mm, "end": v(35.5, 12.82) * mm});
            skLineSegment(sketch, "E18.2.14.1", {"start": v(44.5, -3) * mm, "end": v(44.5, 12.82) * mm});
            skPoint(sketch, "E18.2.14.2", {"position": v(44.5, -5) * mm});
            skPoint(sketch, "E18.2.14.3", {"position": v(35.5, -5) * mm});
            skLineSegment(sketch, "E18.2.14.4", {"start": v(35.5, 12.82) * mm, "end": v(44.5, 12.82) * mm});
            skArc(sketch, "E18.2.14.5", {"start": v(35.5, -3) * mm, "mid": v(36.09, -4.41) * mm, "end": v(37.5, -5) * mm});
            skLineSegment(sketch, "E18.2.14.6", {"start": v(37.5, -5) * mm, "end": v(42.5, -5) * mm});
            skArc(sketch, "E18.2.14.7", {"start": v(42.5, -5) * mm, "mid": v(43.91, -4.41) * mm, "end": v(44.5, -3) * mm});
            skLineSegment(sketch, "E18.3.0.0", {"start": v(55.5, 481.97) * mm, "end": v(55.5, 497.8) * mm});
            skLineSegment(sketch, "E18.3.0.1", {"start": v(64.5, 481.97) * mm, "end": v(64.5, 497.8) * mm});
            skPoint(sketch, "E18.3.0.2", {"position": v(64.5, 479.97) * mm});
            skPoint(sketch, "E18.3.0.3", {"position": v(55.5, 479.97) * mm});
            skLineSegment(sketch, "E18.3.0.4", {"start": v(55.5, 497.8) * mm, "end": v(64.5, 497.8) * mm});
            skArc(sketch, "E18.3.0.5", {"start": v(55.5, 481.97) * mm, "mid": v(56.09, 480.56) * mm, "end": v(57.5, 479.97) * mm});
            skLineSegment(sketch, "E18.3.0.6", {"start": v(57.5, 479.97) * mm, "end": v(62.5, 479.97) * mm});
            skArc(sketch, "E18.3.0.7", {"start": v(62.5, 479.97) * mm, "mid": v(63.91, 480.56) * mm, "end": v(64.5, 481.97) * mm});
            skLineSegment(sketch, "E18.3.1.0", {"start": v(55.5, 447.33) * mm, "end": v(55.5, 463.15) * mm});
            skLineSegment(sketch, "E18.3.1.1", {"start": v(64.5, 447.33) * mm, "end": v(64.5, 463.15) * mm});
            skPoint(sketch, "E18.3.1.2", {"position": v(64.5, 445.33) * mm});
            skPoint(sketch, "E18.3.1.3", {"position": v(55.5, 445.33) * mm});
            skLineSegment(sketch, "E18.3.1.4", {"start": v(55.5, 463.15) * mm, "end": v(64.5, 463.15) * mm});
            skArc(sketch, "E18.3.1.5", {"start": v(55.5, 447.33) * mm, "mid": v(56.09, 445.92) * mm, "end": v(57.5, 445.33) * mm});
            skLineSegment(sketch, "E18.3.1.6", {"start": v(57.5, 445.33) * mm, "end": v(62.5, 445.33) * mm});
            skArc(sketch, "E18.3.1.7", {"start": v(62.5, 445.33) * mm, "mid": v(63.91, 445.92) * mm, "end": v(64.5, 447.33) * mm});
            skLineSegment(sketch, "E18.3.2.0", {"start": v(55.5, 412.7) * mm, "end": v(55.5, 428.51) * mm});
            skLineSegment(sketch, "E18.3.2.1", {"start": v(64.5, 412.7) * mm, "end": v(64.5, 428.51) * mm});
            skPoint(sketch, "E18.3.2.2", {"position": v(64.5, 410.7) * mm});
            skPoint(sketch, "E18.3.2.3", {"position": v(55.5, 410.7) * mm});
            skLineSegment(sketch, "E18.3.2.4", {"start": v(55.5, 428.51) * mm, "end": v(64.5, 428.51) * mm});
            skArc(sketch, "E18.3.2.5", {"start": v(55.5, 412.7) * mm, "mid": v(56.09, 411.28) * mm, "end": v(57.5, 410.7) * mm});
            skLineSegment(sketch, "E18.3.2.6", {"start": v(57.5, 410.7) * mm, "end": v(62.5, 410.7) * mm});
            skArc(sketch, "E18.3.2.7", {"start": v(62.5, 410.7) * mm, "mid": v(63.91, 411.28) * mm, "end": v(64.5, 412.7) * mm});
            skLineSegment(sketch, "E18.3.3.0", {"start": v(55.5, 378.05) * mm, "end": v(55.5, 393.87) * mm});
            skLineSegment(sketch, "E18.3.3.1", {"start": v(64.5, 378.05) * mm, "end": v(64.5, 393.87) * mm});
            skPoint(sketch, "E18.3.3.2", {"position": v(64.5, 376.05) * mm});
            skPoint(sketch, "E18.3.3.3", {"position": v(55.5, 376.05) * mm});
            skLineSegment(sketch, "E18.3.3.4", {"start": v(55.5, 393.87) * mm, "end": v(64.5, 393.87) * mm});
            skArc(sketch, "E18.3.3.5", {"start": v(55.5, 378.05) * mm, "mid": v(56.09, 376.64) * mm, "end": v(57.5, 376.05) * mm});
            skLineSegment(sketch, "E18.3.3.6", {"start": v(57.5, 376.05) * mm, "end": v(62.5, 376.05) * mm});
            skArc(sketch, "E18.3.3.7", {"start": v(62.5, 376.05) * mm, "mid": v(63.91, 376.64) * mm, "end": v(64.5, 378.05) * mm});
            skLineSegment(sketch, "E18.3.4.0", {"start": v(55.5, 343.41) * mm, "end": v(55.5, 359.23) * mm});
            skLineSegment(sketch, "E18.3.4.1", {"start": v(64.5, 343.41) * mm, "end": v(64.5, 359.23) * mm});
            skPoint(sketch, "E18.3.4.2", {"position": v(64.5, 341.41) * mm});
            skPoint(sketch, "E18.3.4.3", {"position": v(55.5, 341.41) * mm});
            skLineSegment(sketch, "E18.3.4.4", {"start": v(55.5, 359.23) * mm, "end": v(64.5, 359.23) * mm});
            skArc(sketch, "E18.3.4.5", {"start": v(55.5, 343.41) * mm, "mid": v(56.09, 342) * mm, "end": v(57.5, 341.41) * mm});
            skLineSegment(sketch, "E18.3.4.6", {"start": v(57.5, 341.41) * mm, "end": v(62.5, 341.41) * mm});
            skArc(sketch, "E18.3.4.7", {"start": v(62.5, 341.41) * mm, "mid": v(63.91, 342) * mm, "end": v(64.5, 343.41) * mm});
            skLineSegment(sketch, "E18.3.5.0", {"start": v(55.5, 308.77) * mm, "end": v(55.5, 324.59) * mm});
            skLineSegment(sketch, "E18.3.5.1", {"start": v(64.5, 308.77) * mm, "end": v(64.5, 324.59) * mm});
            skPoint(sketch, "E18.3.5.2", {"position": v(64.5, 306.77) * mm});
            skPoint(sketch, "E18.3.5.3", {"position": v(55.5, 306.77) * mm});
            skLineSegment(sketch, "E18.3.5.4", {"start": v(55.5, 324.59) * mm, "end": v(64.5, 324.59) * mm});
            skArc(sketch, "E18.3.5.5", {"start": v(55.5, 308.77) * mm, "mid": v(56.09, 307.35) * mm, "end": v(57.5, 306.77) * mm});
            skLineSegment(sketch, "E18.3.5.6", {"start": v(57.5, 306.77) * mm, "end": v(62.5, 306.77) * mm});
            skArc(sketch, "E18.3.5.7", {"start": v(62.5, 306.77) * mm, "mid": v(63.91, 307.35) * mm, "end": v(64.5, 308.77) * mm});
            skLineSegment(sketch, "E18.3.6.0", {"start": v(55.5, 274.13) * mm, "end": v(55.5, 289.95) * mm});
            skLineSegment(sketch, "E18.3.6.1", {"start": v(64.5, 274.13) * mm, "end": v(64.5, 289.95) * mm});
            skPoint(sketch, "E18.3.6.2", {"position": v(64.5, 272.13) * mm});
            skPoint(sketch, "E18.3.6.3", {"position": v(55.5, 272.13) * mm});
            skLineSegment(sketch, "E18.3.6.4", {"start": v(55.5, 289.95) * mm, "end": v(64.5, 289.95) * mm});
            skArc(sketch, "E18.3.6.5", {"start": v(55.5, 274.13) * mm, "mid": v(56.09, 272.71) * mm, "end": v(57.5, 272.13) * mm});
            skLineSegment(sketch, "E18.3.6.6", {"start": v(57.5, 272.13) * mm, "end": v(62.5, 272.13) * mm});
            skArc(sketch, "E18.3.6.7", {"start": v(62.5, 272.13) * mm, "mid": v(63.91, 272.71) * mm, "end": v(64.5, 274.13) * mm});
            skLineSegment(sketch, "E18.3.7.0", {"start": v(55.5, 239.49) * mm, "end": v(55.5, 255.3) * mm});
            skLineSegment(sketch, "E18.3.7.1", {"start": v(64.5, 239.49) * mm, "end": v(64.5, 255.3) * mm});
            skPoint(sketch, "E18.3.7.2", {"position": v(64.5, 237.49) * mm});
            skPoint(sketch, "E18.3.7.3", {"position": v(55.5, 237.49) * mm});
            skLineSegment(sketch, "E18.3.7.4", {"start": v(55.5, 255.3) * mm, "end": v(64.5, 255.3) * mm});
            skArc(sketch, "E18.3.7.5", {"start": v(55.5, 239.49) * mm, "mid": v(56.09, 238.07) * mm, "end": v(57.5, 237.49) * mm});
            skLineSegment(sketch, "E18.3.7.6", {"start": v(57.5, 237.49) * mm, "end": v(62.5, 237.49) * mm});
            skArc(sketch, "E18.3.7.7", {"start": v(62.5, 237.49) * mm, "mid": v(63.91, 238.07) * mm, "end": v(64.5, 239.49) * mm});
            skLineSegment(sketch, "E18.3.8.0", {"start": v(55.5, 204.85) * mm, "end": v(55.5, 220.67) * mm});
            skLineSegment(sketch, "E18.3.8.1", {"start": v(64.5, 204.85) * mm, "end": v(64.5, 220.67) * mm});
            skPoint(sketch, "E18.3.8.2", {"position": v(64.5, 202.85) * mm});
            skPoint(sketch, "E18.3.8.3", {"position": v(55.5, 202.85) * mm});
            skLineSegment(sketch, "E18.3.8.4", {"start": v(55.5, 220.67) * mm, "end": v(64.5, 220.67) * mm});
            skArc(sketch, "E18.3.8.5", {"start": v(55.5, 204.85) * mm, "mid": v(56.09, 203.43) * mm, "end": v(57.5, 202.85) * mm});
            skLineSegment(sketch, "E18.3.8.6", {"start": v(57.5, 202.85) * mm, "end": v(62.5, 202.85) * mm});
            skArc(sketch, "E18.3.8.7", {"start": v(62.5, 202.85) * mm, "mid": v(63.91, 203.43) * mm, "end": v(64.5, 204.85) * mm});
            skLineSegment(sketch, "E18.3.9.0", {"start": v(55.5, 170.2) * mm, "end": v(55.5, 186.03) * mm});
            skLineSegment(sketch, "E18.3.9.1", {"start": v(64.5, 170.2) * mm, "end": v(64.5, 186.03) * mm});
            skPoint(sketch, "E18.3.9.2", {"position": v(64.5, 168.2) * mm});
            skPoint(sketch, "E18.3.9.3", {"position": v(55.5, 168.2) * mm});
            skLineSegment(sketch, "E18.3.9.4", {"start": v(55.5, 186.03) * mm, "end": v(64.5, 186.03) * mm});
            skArc(sketch, "E18.3.9.5", {"start": v(55.5, 170.2) * mm, "mid": v(56.09, 168.8) * mm, "end": v(57.5, 168.2) * mm});
            skLineSegment(sketch, "E18.3.9.6", {"start": v(57.5, 168.2) * mm, "end": v(62.5, 168.2) * mm});
            skArc(sketch, "E18.3.9.7", {"start": v(62.5, 168.2) * mm, "mid": v(63.91, 168.8) * mm, "end": v(64.5, 170.2) * mm});
            skLineSegment(sketch, "E18.3.10.0", {"start": v(55.5, 135.56) * mm, "end": v(55.5, 151.38) * mm});
            skLineSegment(sketch, "E18.3.10.1", {"start": v(64.5, 135.56) * mm, "end": v(64.5, 151.38) * mm});
            skPoint(sketch, "E18.3.10.2", {"position": v(64.5, 133.56) * mm});
            skPoint(sketch, "E18.3.10.3", {"position": v(55.5, 133.56) * mm});
            skLineSegment(sketch, "E18.3.10.4", {"start": v(55.5, 151.38) * mm, "end": v(64.5, 151.38) * mm});
            skArc(sketch, "E18.3.10.5", {"start": v(55.5, 135.56) * mm, "mid": v(56.09, 134.15) * mm, "end": v(57.5, 133.56) * mm});
            skLineSegment(sketch, "E18.3.10.6", {"start": v(57.5, 133.56) * mm, "end": v(62.5, 133.56) * mm});
            skArc(sketch, "E18.3.10.7", {"start": v(62.5, 133.56) * mm, "mid": v(63.91, 134.15) * mm, "end": v(64.5, 135.56) * mm});
            skLineSegment(sketch, "E18.3.11.0", {"start": v(55.5, 100.92) * mm, "end": v(55.5, 116.74) * mm});
            skLineSegment(sketch, "E18.3.11.1", {"start": v(64.5, 100.92) * mm, "end": v(64.5, 116.74) * mm});
            skPoint(sketch, "E18.3.11.2", {"position": v(64.5, 98.92) * mm});
            skPoint(sketch, "E18.3.11.3", {"position": v(55.5, 98.92) * mm});
            skLineSegment(sketch, "E18.3.11.4", {"start": v(55.5, 116.74) * mm, "end": v(64.5, 116.74) * mm});
            skArc(sketch, "E18.3.11.5", {"start": v(55.5, 100.92) * mm, "mid": v(56.09, 99.5) * mm, "end": v(57.5, 98.92) * mm});
            skLineSegment(sketch, "E18.3.11.6", {"start": v(57.5, 98.92) * mm, "end": v(62.5, 98.92) * mm});
            skArc(sketch, "E18.3.11.7", {"start": v(62.5, 98.92) * mm, "mid": v(63.91, 99.5) * mm, "end": v(64.5, 100.92) * mm});
            skLineSegment(sketch, "E18.3.12.0", {"start": v(55.5, 66.28) * mm, "end": v(55.5, 82.1) * mm});
            skLineSegment(sketch, "E18.3.12.1", {"start": v(64.5, 66.28) * mm, "end": v(64.5, 82.1) * mm});
            skPoint(sketch, "E18.3.12.2", {"position": v(64.5, 64.28) * mm});
            skPoint(sketch, "E18.3.12.3", {"position": v(55.5, 64.28) * mm});
            skLineSegment(sketch, "E18.3.12.4", {"start": v(55.5, 82.1) * mm, "end": v(64.5, 82.1) * mm});
            skArc(sketch, "E18.3.12.5", {"start": v(55.5, 66.28) * mm, "mid": v(56.09, 64.87) * mm, "end": v(57.5, 64.28) * mm});
            skLineSegment(sketch, "E18.3.12.6", {"start": v(57.5, 64.28) * mm, "end": v(62.5, 64.28) * mm});
            skArc(sketch, "E18.3.12.7", {"start": v(62.5, 64.28) * mm, "mid": v(63.91, 64.87) * mm, "end": v(64.5, 66.28) * mm});
            skLineSegment(sketch, "E18.3.13.0", {"start": v(55.5, 31.64) * mm, "end": v(55.5, 47.46) * mm});
            skLineSegment(sketch, "E18.3.13.1", {"start": v(64.5, 31.64) * mm, "end": v(64.5, 47.46) * mm});
            skPoint(sketch, "E18.3.13.2", {"position": v(64.5, 29.64) * mm});
            skPoint(sketch, "E18.3.13.3", {"position": v(55.5, 29.64) * mm});
            skLineSegment(sketch, "E18.3.13.4", {"start": v(55.5, 47.46) * mm, "end": v(64.5, 47.46) * mm});
            skArc(sketch, "E18.3.13.5", {"start": v(55.5, 31.64) * mm, "mid": v(56.09, 30.23) * mm, "end": v(57.5, 29.64) * mm});
            skLineSegment(sketch, "E18.3.13.6", {"start": v(57.5, 29.64) * mm, "end": v(62.5, 29.64) * mm});
            skArc(sketch, "E18.3.13.7", {"start": v(62.5, 29.64) * mm, "mid": v(63.91, 30.23) * mm, "end": v(64.5, 31.64) * mm});
            skLineSegment(sketch, "E18.3.14.0", {"start": v(55.5, -3) * mm, "end": v(55.5, 12.82) * mm});
            skLineSegment(sketch, "E18.3.14.1", {"start": v(64.5, -3) * mm, "end": v(64.5, 12.82) * mm});
            skPoint(sketch, "E18.3.14.2", {"position": v(64.5, -5) * mm});
            skPoint(sketch, "E18.3.14.3", {"position": v(55.5, -5) * mm});
            skLineSegment(sketch, "E18.3.14.4", {"start": v(55.5, 12.82) * mm, "end": v(64.5, 12.82) * mm});
            skArc(sketch, "E18.3.14.5", {"start": v(55.5, -3) * mm, "mid": v(56.09, -4.41) * mm, "end": v(57.5, -5) * mm});
            skLineSegment(sketch, "E18.3.14.6", {"start": v(57.5, -5) * mm, "end": v(62.5, -5) * mm});
            skArc(sketch, "E18.3.14.7", {"start": v(62.5, -5) * mm, "mid": v(63.91, -4.41) * mm, "end": v(64.5, -3) * mm});
            skLineSegment(sketch, "E18.4.0.0", {"start": v(75.5, 481.97) * mm, "end": v(75.5, 497.8) * mm});
            skLineSegment(sketch, "E18.4.0.1", {"start": v(84.5, 481.97) * mm, "end": v(84.5, 497.8) * mm});
            skPoint(sketch, "E18.4.0.2", {"position": v(84.5, 479.97) * mm});
            skPoint(sketch, "E18.4.0.3", {"position": v(75.5, 479.97) * mm});
            skLineSegment(sketch, "E18.4.0.4", {"start": v(75.5, 497.8) * mm, "end": v(84.5, 497.8) * mm});
            skArc(sketch, "E18.4.0.5", {"start": v(75.5, 481.97) * mm, "mid": v(76.09, 480.56) * mm, "end": v(77.5, 479.97) * mm});
            skLineSegment(sketch, "E18.4.0.6", {"start": v(77.5, 479.97) * mm, "end": v(82.5, 479.97) * mm});
            skArc(sketch, "E18.4.0.7", {"start": v(82.5, 479.97) * mm, "mid": v(83.91, 480.56) * mm, "end": v(84.5, 481.97) * mm});
            skLineSegment(sketch, "E18.4.1.0", {"start": v(75.5, 447.33) * mm, "end": v(75.5, 463.15) * mm});
            skLineSegment(sketch, "E18.4.1.1", {"start": v(84.5, 447.33) * mm, "end": v(84.5, 463.15) * mm});
            skPoint(sketch, "E18.4.1.2", {"position": v(84.5, 445.33) * mm});
            skPoint(sketch, "E18.4.1.3", {"position": v(75.5, 445.33) * mm});
            skLineSegment(sketch, "E18.4.1.4", {"start": v(75.5, 463.15) * mm, "end": v(84.5, 463.15) * mm});
            skArc(sketch, "E18.4.1.5", {"start": v(75.5, 447.33) * mm, "mid": v(76.09, 445.92) * mm, "end": v(77.5, 445.33) * mm});
            skLineSegment(sketch, "E18.4.1.6", {"start": v(77.5, 445.33) * mm, "end": v(82.5, 445.33) * mm});
            skArc(sketch, "E18.4.1.7", {"start": v(82.5, 445.33) * mm, "mid": v(83.91, 445.92) * mm, "end": v(84.5, 447.33) * mm});
            skLineSegment(sketch, "E18.4.2.0", {"start": v(75.5, 412.7) * mm, "end": v(75.5, 428.51) * mm});
            skLineSegment(sketch, "E18.4.2.1", {"start": v(84.5, 412.7) * mm, "end": v(84.5, 428.51) * mm});
            skPoint(sketch, "E18.4.2.2", {"position": v(84.5, 410.7) * mm});
            skPoint(sketch, "E18.4.2.3", {"position": v(75.5, 410.7) * mm});
            skLineSegment(sketch, "E18.4.2.4", {"start": v(75.5, 428.51) * mm, "end": v(84.5, 428.51) * mm});
            skArc(sketch, "E18.4.2.5", {"start": v(75.5, 412.7) * mm, "mid": v(76.09, 411.28) * mm, "end": v(77.5, 410.7) * mm});
            skLineSegment(sketch, "E18.4.2.6", {"start": v(77.5, 410.7) * mm, "end": v(82.5, 410.7) * mm});
            skArc(sketch, "E18.4.2.7", {"start": v(82.5, 410.7) * mm, "mid": v(83.91, 411.28) * mm, "end": v(84.5, 412.7) * mm});
            skLineSegment(sketch, "E18.4.3.0", {"start": v(75.5, 378.05) * mm, "end": v(75.5, 393.87) * mm});
            skLineSegment(sketch, "E18.4.3.1", {"start": v(84.5, 378.05) * mm, "end": v(84.5, 393.87) * mm});
            skPoint(sketch, "E18.4.3.2", {"position": v(84.5, 376.05) * mm});
            skPoint(sketch, "E18.4.3.3", {"position": v(75.5, 376.05) * mm});
            skLineSegment(sketch, "E18.4.3.4", {"start": v(75.5, 393.87) * mm, "end": v(84.5, 393.87) * mm});
            skArc(sketch, "E18.4.3.5", {"start": v(75.5, 378.05) * mm, "mid": v(76.09, 376.64) * mm, "end": v(77.5, 376.05) * mm});
            skLineSegment(sketch, "E18.4.3.6", {"start": v(77.5, 376.05) * mm, "end": v(82.5, 376.05) * mm});
            skArc(sketch, "E18.4.3.7", {"start": v(82.5, 376.05) * mm, "mid": v(83.91, 376.64) * mm, "end": v(84.5, 378.05) * mm});
            skLineSegment(sketch, "E18.4.4.0", {"start": v(75.5, 343.41) * mm, "end": v(75.5, 359.23) * mm});
            skLineSegment(sketch, "E18.4.4.1", {"start": v(84.5, 343.41) * mm, "end": v(84.5, 359.23) * mm});
            skPoint(sketch, "E18.4.4.2", {"position": v(84.5, 341.41) * mm});
            skPoint(sketch, "E18.4.4.3", {"position": v(75.5, 341.41) * mm});
            skLineSegment(sketch, "E18.4.4.4", {"start": v(75.5, 359.23) * mm, "end": v(84.5, 359.23) * mm});
            skArc(sketch, "E18.4.4.5", {"start": v(75.5, 343.41) * mm, "mid": v(76.09, 342) * mm, "end": v(77.5, 341.41) * mm});
            skLineSegment(sketch, "E18.4.4.6", {"start": v(77.5, 341.41) * mm, "end": v(82.5, 341.41) * mm});
            skArc(sketch, "E18.4.4.7", {"start": v(82.5, 341.41) * mm, "mid": v(83.91, 342) * mm, "end": v(84.5, 343.41) * mm});
            skLineSegment(sketch, "E18.4.5.0", {"start": v(75.5, 308.77) * mm, "end": v(75.5, 324.59) * mm});
            skLineSegment(sketch, "E18.4.5.1", {"start": v(84.5, 308.77) * mm, "end": v(84.5, 324.59) * mm});
            skPoint(sketch, "E18.4.5.2", {"position": v(84.5, 306.77) * mm});
            skPoint(sketch, "E18.4.5.3", {"position": v(75.5, 306.77) * mm});
            skLineSegment(sketch, "E18.4.5.4", {"start": v(75.5, 324.59) * mm, "end": v(84.5, 324.59) * mm});
            skArc(sketch, "E18.4.5.5", {"start": v(75.5, 308.77) * mm, "mid": v(76.09, 307.35) * mm, "end": v(77.5, 306.77) * mm});
            skLineSegment(sketch, "E18.4.5.6", {"start": v(77.5, 306.77) * mm, "end": v(82.5, 306.77) * mm});
            skArc(sketch, "E18.4.5.7", {"start": v(82.5, 306.77) * mm, "mid": v(83.91, 307.35) * mm, "end": v(84.5, 308.77) * mm});
            skLineSegment(sketch, "E18.4.6.0", {"start": v(75.5, 274.13) * mm, "end": v(75.5, 289.95) * mm});
            skLineSegment(sketch, "E18.4.6.1", {"start": v(84.5, 274.13) * mm, "end": v(84.5, 289.95) * mm});
            skPoint(sketch, "E18.4.6.2", {"position": v(84.5, 272.13) * mm});
            skPoint(sketch, "E18.4.6.3", {"position": v(75.5, 272.13) * mm});
            skLineSegment(sketch, "E18.4.6.4", {"start": v(75.5, 289.95) * mm, "end": v(84.5, 289.95) * mm});
            skArc(sketch, "E18.4.6.5", {"start": v(75.5, 274.13) * mm, "mid": v(76.09, 272.71) * mm, "end": v(77.5, 272.13) * mm});
            skLineSegment(sketch, "E18.4.6.6", {"start": v(77.5, 272.13) * mm, "end": v(82.5, 272.13) * mm});
            skArc(sketch, "E18.4.6.7", {"start": v(82.5, 272.13) * mm, "mid": v(83.91, 272.71) * mm, "end": v(84.5, 274.13) * mm});
            skLineSegment(sketch, "E18.4.7.0", {"start": v(75.5, 239.49) * mm, "end": v(75.5, 255.3) * mm});
            skLineSegment(sketch, "E18.4.7.1", {"start": v(84.5, 239.49) * mm, "end": v(84.5, 255.3) * mm});
            skPoint(sketch, "E18.4.7.2", {"position": v(84.5, 237.49) * mm});
            skPoint(sketch, "E18.4.7.3", {"position": v(75.5, 237.49) * mm});
            skLineSegment(sketch, "E18.4.7.4", {"start": v(75.5, 255.3) * mm, "end": v(84.5, 255.3) * mm});
            skArc(sketch, "E18.4.7.5", {"start": v(75.5, 239.49) * mm, "mid": v(76.09, 238.07) * mm, "end": v(77.5, 237.49) * mm});
            skLineSegment(sketch, "E18.4.7.6", {"start": v(77.5, 237.49) * mm, "end": v(82.5, 237.49) * mm});
            skArc(sketch, "E18.4.7.7", {"start": v(82.5, 237.49) * mm, "mid": v(83.91, 238.07) * mm, "end": v(84.5, 239.49) * mm});
            skLineSegment(sketch, "E18.4.8.0", {"start": v(75.5, 204.85) * mm, "end": v(75.5, 220.67) * mm});
            skLineSegment(sketch, "E18.4.8.1", {"start": v(84.5, 204.85) * mm, "end": v(84.5, 220.67) * mm});
            skPoint(sketch, "E18.4.8.2", {"position": v(84.5, 202.85) * mm});
            skPoint(sketch, "E18.4.8.3", {"position": v(75.5, 202.85) * mm});
            skLineSegment(sketch, "E18.4.8.4", {"start": v(75.5, 220.67) * mm, "end": v(84.5, 220.67) * mm});
            skArc(sketch, "E18.4.8.5", {"start": v(75.5, 204.85) * mm, "mid": v(76.09, 203.43) * mm, "end": v(77.5, 202.85) * mm});
            skLineSegment(sketch, "E18.4.8.6", {"start": v(77.5, 202.85) * mm, "end": v(82.5, 202.85) * mm});
            skArc(sketch, "E18.4.8.7", {"start": v(82.5, 202.85) * mm, "mid": v(83.91, 203.43) * mm, "end": v(84.5, 204.85) * mm});
            skLineSegment(sketch, "E18.4.9.0", {"start": v(75.5, 170.2) * mm, "end": v(75.5, 186.03) * mm});
            skLineSegment(sketch, "E18.4.9.1", {"start": v(84.5, 170.2) * mm, "end": v(84.5, 186.03) * mm});
            skPoint(sketch, "E18.4.9.2", {"position": v(84.5, 168.2) * mm});
            skPoint(sketch, "E18.4.9.3", {"position": v(75.5, 168.2) * mm});
            skLineSegment(sketch, "E18.4.9.4", {"start": v(75.5, 186.03) * mm, "end": v(84.5, 186.03) * mm});
            skArc(sketch, "E18.4.9.5", {"start": v(75.5, 170.2) * mm, "mid": v(76.09, 168.8) * mm, "end": v(77.5, 168.2) * mm});
            skLineSegment(sketch, "E18.4.9.6", {"start": v(77.5, 168.2) * mm, "end": v(82.5, 168.2) * mm});
            skArc(sketch, "E18.4.9.7", {"start": v(82.5, 168.2) * mm, "mid": v(83.91, 168.8) * mm, "end": v(84.5, 170.2) * mm});
            skLineSegment(sketch, "E18.4.10.0", {"start": v(75.5, 135.56) * mm, "end": v(75.5, 151.38) * mm});
            skLineSegment(sketch, "E18.4.10.1", {"start": v(84.5, 135.56) * mm, "end": v(84.5, 151.38) * mm});
            skPoint(sketch, "E18.4.10.2", {"position": v(84.5, 133.56) * mm});
            skPoint(sketch, "E18.4.10.3", {"position": v(75.5, 133.56) * mm});
            skLineSegment(sketch, "E18.4.10.4", {"start": v(75.5, 151.38) * mm, "end": v(84.5, 151.38) * mm});
            skArc(sketch, "E18.4.10.5", {"start": v(75.5, 135.56) * mm, "mid": v(76.09, 134.15) * mm, "end": v(77.5, 133.56) * mm});
            skLineSegment(sketch, "E18.4.10.6", {"start": v(77.5, 133.56) * mm, "end": v(82.5, 133.56) * mm});
            skArc(sketch, "E18.4.10.7", {"start": v(82.5, 133.56) * mm, "mid": v(83.91, 134.15) * mm, "end": v(84.5, 135.56) * mm});
            skLineSegment(sketch, "E18.4.11.0", {"start": v(75.5, 100.92) * mm, "end": v(75.5, 116.74) * mm});
            skLineSegment(sketch, "E18.4.11.1", {"start": v(84.5, 100.92) * mm, "end": v(84.5, 116.74) * mm});
            skPoint(sketch, "E18.4.11.2", {"position": v(84.5, 98.92) * mm});
            skPoint(sketch, "E18.4.11.3", {"position": v(75.5, 98.92) * mm});
            skLineSegment(sketch, "E18.4.11.4", {"start": v(75.5, 116.74) * mm, "end": v(84.5, 116.74) * mm});
            skArc(sketch, "E18.4.11.5", {"start": v(75.5, 100.92) * mm, "mid": v(76.09, 99.5) * mm, "end": v(77.5, 98.92) * mm});
            skLineSegment(sketch, "E18.4.11.6", {"start": v(77.5, 98.92) * mm, "end": v(82.5, 98.92) * mm});
            skArc(sketch, "E18.4.11.7", {"start": v(82.5, 98.92) * mm, "mid": v(83.91, 99.5) * mm, "end": v(84.5, 100.92) * mm});
            skLineSegment(sketch, "E18.4.12.0", {"start": v(75.5, 66.28) * mm, "end": v(75.5, 82.1) * mm});
            skLineSegment(sketch, "E18.4.12.1", {"start": v(84.5, 66.28) * mm, "end": v(84.5, 82.1) * mm});
            skPoint(sketch, "E18.4.12.2", {"position": v(84.5, 64.28) * mm});
            skPoint(sketch, "E18.4.12.3", {"position": v(75.5, 64.28) * mm});
            skLineSegment(sketch, "E18.4.12.4", {"start": v(75.5, 82.1) * mm, "end": v(84.5, 82.1) * mm});
            skArc(sketch, "E18.4.12.5", {"start": v(75.5, 66.28) * mm, "mid": v(76.09, 64.87) * mm, "end": v(77.5, 64.28) * mm});
            skLineSegment(sketch, "E18.4.12.6", {"start": v(77.5, 64.28) * mm, "end": v(82.5, 64.28) * mm});
            skArc(sketch, "E18.4.12.7", {"start": v(82.5, 64.28) * mm, "mid": v(83.91, 64.87) * mm, "end": v(84.5, 66.28) * mm});
            skLineSegment(sketch, "E18.4.13.0", {"start": v(75.5, 31.64) * mm, "end": v(75.5, 47.46) * mm});
            skLineSegment(sketch, "E18.4.13.1", {"start": v(84.5, 31.64) * mm, "end": v(84.5, 47.46) * mm});
            skPoint(sketch, "E18.4.13.2", {"position": v(84.5, 29.64) * mm});
            skPoint(sketch, "E18.4.13.3", {"position": v(75.5, 29.64) * mm});
            skLineSegment(sketch, "E18.4.13.4", {"start": v(75.5, 47.46) * mm, "end": v(84.5, 47.46) * mm});
            skArc(sketch, "E18.4.13.5", {"start": v(75.5, 31.64) * mm, "mid": v(76.09, 30.23) * mm, "end": v(77.5, 29.64) * mm});
            skLineSegment(sketch, "E18.4.13.6", {"start": v(77.5, 29.64) * mm, "end": v(82.5, 29.64) * mm});
            skArc(sketch, "E18.4.13.7", {"start": v(82.5, 29.64) * mm, "mid": v(83.91, 30.23) * mm, "end": v(84.5, 31.64) * mm});
            skLineSegment(sketch, "E18.4.14.0", {"start": v(75.5, -3) * mm, "end": v(75.5, 12.82) * mm});
            skLineSegment(sketch, "E18.4.14.1", {"start": v(84.5, -3) * mm, "end": v(84.5, 12.82) * mm});
            skPoint(sketch, "E18.4.14.2", {"position": v(84.5, -5) * mm});
            skPoint(sketch, "E18.4.14.3", {"position": v(75.5, -5) * mm});
            skLineSegment(sketch, "E18.4.14.4", {"start": v(75.5, 12.82) * mm, "end": v(84.5, 12.82) * mm});
            skArc(sketch, "E18.4.14.5", {"start": v(75.5, -3) * mm, "mid": v(76.09, -4.41) * mm, "end": v(77.5, -5) * mm});
            skLineSegment(sketch, "E18.4.14.6", {"start": v(77.5, -5) * mm, "end": v(82.5, -5) * mm});
            skArc(sketch, "E18.4.14.7", {"start": v(82.5, -5) * mm, "mid": v(83.91, -4.41) * mm, "end": v(84.5, -3) * mm});
            skLineSegment(sketch, "E18.5.0.0", {"start": v(95.5, 481.97) * mm, "end": v(95.5, 497.8) * mm});
            skLineSegment(sketch, "E18.5.0.1", {"start": v(104.5, 481.97) * mm, "end": v(104.5, 497.8) * mm});
            skPoint(sketch, "E18.5.0.2", {"position": v(104.5, 479.97) * mm});
            skPoint(sketch, "E18.5.0.3", {"position": v(95.5, 479.97) * mm});
            skLineSegment(sketch, "E18.5.0.4", {"start": v(95.5, 497.8) * mm, "end": v(104.5, 497.8) * mm});
            skArc(sketch, "E18.5.0.5", {"start": v(95.5, 481.97) * mm, "mid": v(96.09, 480.56) * mm, "end": v(97.5, 479.97) * mm});
            skLineSegment(sketch, "E18.5.0.6", {"start": v(97.5, 479.97) * mm, "end": v(102.5, 479.97) * mm});
            skArc(sketch, "E18.5.0.7", {"start": v(102.5, 479.97) * mm, "mid": v(103.91, 480.56) * mm, "end": v(104.5, 481.97) * mm});
            skLineSegment(sketch, "E18.5.1.0", {"start": v(95.5, 447.33) * mm, "end": v(95.5, 463.15) * mm});
            skLineSegment(sketch, "E18.5.1.1", {"start": v(104.5, 447.33) * mm, "end": v(104.5, 463.15) * mm});
            skPoint(sketch, "E18.5.1.2", {"position": v(104.5, 445.33) * mm});
            skPoint(sketch, "E18.5.1.3", {"position": v(95.5, 445.33) * mm});
            skLineSegment(sketch, "E18.5.1.4", {"start": v(95.5, 463.15) * mm, "end": v(104.5, 463.15) * mm});
            skArc(sketch, "E18.5.1.5", {"start": v(95.5, 447.33) * mm, "mid": v(96.09, 445.92) * mm, "end": v(97.5, 445.33) * mm});
            skLineSegment(sketch, "E18.5.1.6", {"start": v(97.5, 445.33) * mm, "end": v(102.5, 445.33) * mm});
            skArc(sketch, "E18.5.1.7", {"start": v(102.5, 445.33) * mm, "mid": v(103.91, 445.92) * mm, "end": v(104.5, 447.33) * mm});
            skLineSegment(sketch, "E18.5.2.0", {"start": v(95.5, 412.7) * mm, "end": v(95.5, 428.51) * mm});
            skLineSegment(sketch, "E18.5.2.1", {"start": v(104.5, 412.7) * mm, "end": v(104.5, 428.51) * mm});
            skPoint(sketch, "E18.5.2.2", {"position": v(104.5, 410.7) * mm});
            skPoint(sketch, "E18.5.2.3", {"position": v(95.5, 410.7) * mm});
            skLineSegment(sketch, "E18.5.2.4", {"start": v(95.5, 428.51) * mm, "end": v(104.5, 428.51) * mm});
            skArc(sketch, "E18.5.2.5", {"start": v(95.5, 412.7) * mm, "mid": v(96.09, 411.28) * mm, "end": v(97.5, 410.7) * mm});
            skLineSegment(sketch, "E18.5.2.6", {"start": v(97.5, 410.7) * mm, "end": v(102.5, 410.7) * mm});
            skArc(sketch, "E18.5.2.7", {"start": v(102.5, 410.7) * mm, "mid": v(103.91, 411.28) * mm, "end": v(104.5, 412.7) * mm});
            skLineSegment(sketch, "E18.5.3.0", {"start": v(95.5, 378.05) * mm, "end": v(95.5, 393.87) * mm});
            skLineSegment(sketch, "E18.5.3.1", {"start": v(104.5, 378.05) * mm, "end": v(104.5, 393.87) * mm});
            skPoint(sketch, "E18.5.3.2", {"position": v(104.5, 376.05) * mm});
            skPoint(sketch, "E18.5.3.3", {"position": v(95.5, 376.05) * mm});
            skLineSegment(sketch, "E18.5.3.4", {"start": v(95.5, 393.87) * mm, "end": v(104.5, 393.87) * mm});
            skArc(sketch, "E18.5.3.5", {"start": v(95.5, 378.05) * mm, "mid": v(96.09, 376.64) * mm, "end": v(97.5, 376.05) * mm});
            skLineSegment(sketch, "E18.5.3.6", {"start": v(97.5, 376.05) * mm, "end": v(102.5, 376.05) * mm});
            skArc(sketch, "E18.5.3.7", {"start": v(102.5, 376.05) * mm, "mid": v(103.91, 376.64) * mm, "end": v(104.5, 378.05) * mm});
            skLineSegment(sketch, "E18.5.4.0", {"start": v(95.5, 343.41) * mm, "end": v(95.5, 359.23) * mm});
            skLineSegment(sketch, "E18.5.4.1", {"start": v(104.5, 343.41) * mm, "end": v(104.5, 359.23) * mm});
            skPoint(sketch, "E18.5.4.2", {"position": v(104.5, 341.41) * mm});
            skPoint(sketch, "E18.5.4.3", {"position": v(95.5, 341.41) * mm});
            skLineSegment(sketch, "E18.5.4.4", {"start": v(95.5, 359.23) * mm, "end": v(104.5, 359.23) * mm});
            skArc(sketch, "E18.5.4.5", {"start": v(95.5, 343.41) * mm, "mid": v(96.09, 342) * mm, "end": v(97.5, 341.41) * mm});
            skLineSegment(sketch, "E18.5.4.6", {"start": v(97.5, 341.41) * mm, "end": v(102.5, 341.41) * mm});
            skArc(sketch, "E18.5.4.7", {"start": v(102.5, 341.41) * mm, "mid": v(103.91, 342) * mm, "end": v(104.5, 343.41) * mm});
            skLineSegment(sketch, "E18.5.5.0", {"start": v(95.5, 308.77) * mm, "end": v(95.5, 324.59) * mm});
            skLineSegment(sketch, "E18.5.5.1", {"start": v(104.5, 308.77) * mm, "end": v(104.5, 324.59) * mm});
            skPoint(sketch, "E18.5.5.2", {"position": v(104.5, 306.77) * mm});
            skPoint(sketch, "E18.5.5.3", {"position": v(95.5, 306.77) * mm});
            skLineSegment(sketch, "E18.5.5.4", {"start": v(95.5, 324.59) * mm, "end": v(104.5, 324.59) * mm});
            skArc(sketch, "E18.5.5.5", {"start": v(95.5, 308.77) * mm, "mid": v(96.09, 307.35) * mm, "end": v(97.5, 306.77) * mm});
            skLineSegment(sketch, "E18.5.5.6", {"start": v(97.5, 306.77) * mm, "end": v(102.5, 306.77) * mm});
            skArc(sketch, "E18.5.5.7", {"start": v(102.5, 306.77) * mm, "mid": v(103.91, 307.35) * mm, "end": v(104.5, 308.77) * mm});
            skLineSegment(sketch, "E18.5.6.0", {"start": v(95.5, 274.13) * mm, "end": v(95.5, 289.95) * mm});
            skLineSegment(sketch, "E18.5.6.1", {"start": v(104.5, 274.13) * mm, "end": v(104.5, 289.95) * mm});
            skPoint(sketch, "E18.5.6.2", {"position": v(104.5, 272.13) * mm});
            skPoint(sketch, "E18.5.6.3", {"position": v(95.5, 272.13) * mm});
            skLineSegment(sketch, "E18.5.6.4", {"start": v(95.5, 289.95) * mm, "end": v(104.5, 289.95) * mm});
            skArc(sketch, "E18.5.6.5", {"start": v(95.5, 274.13) * mm, "mid": v(96.09, 272.71) * mm, "end": v(97.5, 272.13) * mm});
            skLineSegment(sketch, "E18.5.6.6", {"start": v(97.5, 272.13) * mm, "end": v(102.5, 272.13) * mm});
            skArc(sketch, "E18.5.6.7", {"start": v(102.5, 272.13) * mm, "mid": v(103.91, 272.71) * mm, "end": v(104.5, 274.13) * mm});
            skLineSegment(sketch, "E18.5.7.0", {"start": v(95.5, 239.49) * mm, "end": v(95.5, 255.3) * mm});
            skLineSegment(sketch, "E18.5.7.1", {"start": v(104.5, 239.49) * mm, "end": v(104.5, 255.3) * mm});
            skPoint(sketch, "E18.5.7.2", {"position": v(104.5, 237.49) * mm});
            skPoint(sketch, "E18.5.7.3", {"position": v(95.5, 237.49) * mm});
            skLineSegment(sketch, "E18.5.7.4", {"start": v(95.5, 255.3) * mm, "end": v(104.5, 255.3) * mm});
            skArc(sketch, "E18.5.7.5", {"start": v(95.5, 239.49) * mm, "mid": v(96.09, 238.07) * mm, "end": v(97.5, 237.49) * mm});
            skLineSegment(sketch, "E18.5.7.6", {"start": v(97.5, 237.49) * mm, "end": v(102.5, 237.49) * mm});
            skArc(sketch, "E18.5.7.7", {"start": v(102.5, 237.49) * mm, "mid": v(103.91, 238.07) * mm, "end": v(104.5, 239.49) * mm});
            skLineSegment(sketch, "E18.5.8.0", {"start": v(95.5, 204.85) * mm, "end": v(95.5, 220.67) * mm});
            skLineSegment(sketch, "E18.5.8.1", {"start": v(104.5, 204.85) * mm, "end": v(104.5, 220.67) * mm});
            skPoint(sketch, "E18.5.8.2", {"position": v(104.5, 202.85) * mm});
            skPoint(sketch, "E18.5.8.3", {"position": v(95.5, 202.85) * mm});
            skLineSegment(sketch, "E18.5.8.4", {"start": v(95.5, 220.67) * mm, "end": v(104.5, 220.67) * mm});
            skArc(sketch, "E18.5.8.5", {"start": v(95.5, 204.85) * mm, "mid": v(96.09, 203.43) * mm, "end": v(97.5, 202.85) * mm});
            skLineSegment(sketch, "E18.5.8.6", {"start": v(97.5, 202.85) * mm, "end": v(102.5, 202.85) * mm});
            skArc(sketch, "E18.5.8.7", {"start": v(102.5, 202.85) * mm, "mid": v(103.91, 203.43) * mm, "end": v(104.5, 204.85) * mm});
            skLineSegment(sketch, "E18.5.9.0", {"start": v(95.5, 170.2) * mm, "end": v(95.5, 186.03) * mm});
            skLineSegment(sketch, "E18.5.9.1", {"start": v(104.5, 170.2) * mm, "end": v(104.5, 186.03) * mm});
            skPoint(sketch, "E18.5.9.2", {"position": v(104.5, 168.2) * mm});
            skPoint(sketch, "E18.5.9.3", {"position": v(95.5, 168.2) * mm});
            skLineSegment(sketch, "E18.5.9.4", {"start": v(95.5, 186.03) * mm, "end": v(104.5, 186.03) * mm});
            skArc(sketch, "E18.5.9.5", {"start": v(95.5, 170.2) * mm, "mid": v(96.09, 168.8) * mm, "end": v(97.5, 168.2) * mm});
            skLineSegment(sketch, "E18.5.9.6", {"start": v(97.5, 168.2) * mm, "end": v(102.5, 168.2) * mm});
            skArc(sketch, "E18.5.9.7", {"start": v(102.5, 168.2) * mm, "mid": v(103.91, 168.8) * mm, "end": v(104.5, 170.2) * mm});
            skLineSegment(sketch, "E18.5.10.0", {"start": v(95.5, 135.56) * mm, "end": v(95.5, 151.38) * mm});
            skLineSegment(sketch, "E18.5.10.1", {"start": v(104.5, 135.56) * mm, "end": v(104.5, 151.38) * mm});
            skPoint(sketch, "E18.5.10.2", {"position": v(104.5, 133.56) * mm});
            skPoint(sketch, "E18.5.10.3", {"position": v(95.5, 133.56) * mm});
            skLineSegment(sketch, "E18.5.10.4", {"start": v(95.5, 151.38) * mm, "end": v(104.5, 151.38) * mm});
            skArc(sketch, "E18.5.10.5", {"start": v(95.5, 135.56) * mm, "mid": v(96.09, 134.15) * mm, "end": v(97.5, 133.56) * mm});
            skLineSegment(sketch, "E18.5.10.6", {"start": v(97.5, 133.56) * mm, "end": v(102.5, 133.56) * mm});
            skArc(sketch, "E18.5.10.7", {"start": v(102.5, 133.56) * mm, "mid": v(103.91, 134.15) * mm, "end": v(104.5, 135.56) * mm});
            skLineSegment(sketch, "E18.5.11.0", {"start": v(95.5, 100.92) * mm, "end": v(95.5, 116.74) * mm});
            skLineSegment(sketch, "E18.5.11.1", {"start": v(104.5, 100.92) * mm, "end": v(104.5, 116.74) * mm});
            skPoint(sketch, "E18.5.11.2", {"position": v(104.5, 98.92) * mm});
            skPoint(sketch, "E18.5.11.3", {"position": v(95.5, 98.92) * mm});
            skLineSegment(sketch, "E18.5.11.4", {"start": v(95.5, 116.74) * mm, "end": v(104.5, 116.74) * mm});
            skArc(sketch, "E18.5.11.5", {"start": v(95.5, 100.92) * mm, "mid": v(96.09, 99.5) * mm, "end": v(97.5, 98.92) * mm});
            skLineSegment(sketch, "E18.5.11.6", {"start": v(97.5, 98.92) * mm, "end": v(102.5, 98.92) * mm});
            skArc(sketch, "E18.5.11.7", {"start": v(102.5, 98.92) * mm, "mid": v(103.91, 99.5) * mm, "end": v(104.5, 100.92) * mm});
            skLineSegment(sketch, "E18.5.12.0", {"start": v(95.5, 66.28) * mm, "end": v(95.5, 82.1) * mm});
            skLineSegment(sketch, "E18.5.12.1", {"start": v(104.5, 66.28) * mm, "end": v(104.5, 82.1) * mm});
            skPoint(sketch, "E18.5.12.2", {"position": v(104.5, 64.28) * mm});
            skPoint(sketch, "E18.5.12.3", {"position": v(95.5, 64.28) * mm});
            skLineSegment(sketch, "E18.5.12.4", {"start": v(95.5, 82.1) * mm, "end": v(104.5, 82.1) * mm});
            skArc(sketch, "E18.5.12.5", {"start": v(95.5, 66.28) * mm, "mid": v(96.09, 64.87) * mm, "end": v(97.5, 64.28) * mm});
            skLineSegment(sketch, "E18.5.12.6", {"start": v(97.5, 64.28) * mm, "end": v(102.5, 64.28) * mm});
            skArc(sketch, "E18.5.12.7", {"start": v(102.5, 64.28) * mm, "mid": v(103.91, 64.87) * mm, "end": v(104.5, 66.28) * mm});
            skLineSegment(sketch, "E18.5.13.0", {"start": v(95.5, 31.64) * mm, "end": v(95.5, 47.46) * mm});
            skLineSegment(sketch, "E18.5.13.1", {"start": v(104.5, 31.64) * mm, "end": v(104.5, 47.46) * mm});
            skPoint(sketch, "E18.5.13.2", {"position": v(104.5, 29.64) * mm});
            skPoint(sketch, "E18.5.13.3", {"position": v(95.5, 29.64) * mm});
            skLineSegment(sketch, "E18.5.13.4", {"start": v(95.5, 47.46) * mm, "end": v(104.5, 47.46) * mm});
            skArc(sketch, "E18.5.13.5", {"start": v(95.5, 31.64) * mm, "mid": v(96.09, 30.23) * mm, "end": v(97.5, 29.64) * mm});
            skLineSegment(sketch, "E18.5.13.6", {"start": v(97.5, 29.64) * mm, "end": v(102.5, 29.64) * mm});
            skArc(sketch, "E18.5.13.7", {"start": v(102.5, 29.64) * mm, "mid": v(103.91, 30.23) * mm, "end": v(104.5, 31.64) * mm});
            skLineSegment(sketch, "E18.5.14.0", {"start": v(95.5, -3) * mm, "end": v(95.5, 12.82) * mm});
            skLineSegment(sketch, "E18.5.14.1", {"start": v(104.5, -3) * mm, "end": v(104.5, 12.82) * mm});
            skPoint(sketch, "E18.5.14.2", {"position": v(104.5, -5) * mm});
            skPoint(sketch, "E18.5.14.3", {"position": v(95.5, -5) * mm});
            skLineSegment(sketch, "E18.5.14.4", {"start": v(95.5, 12.82) * mm, "end": v(104.5, 12.82) * mm});
            skArc(sketch, "E18.5.14.5", {"start": v(95.5, -3) * mm, "mid": v(96.09, -4.41) * mm, "end": v(97.5, -5) * mm});
            skLineSegment(sketch, "E18.5.14.6", {"start": v(97.5, -5) * mm, "end": v(102.5, -5) * mm});
            skArc(sketch, "E18.5.14.7", {"start": v(102.5, -5) * mm, "mid": v(103.91, -4.41) * mm, "end": v(104.5, -3) * mm});
            skLineSegment(sketch, "E18.6.0.0", {"start": v(115.5, 481.97) * mm, "end": v(115.5, 497.8) * mm});
            skLineSegment(sketch, "E18.6.0.1", {"start": v(124.5, 481.97) * mm, "end": v(124.5, 497.8) * mm});
            skPoint(sketch, "E18.6.0.2", {"position": v(124.5, 479.97) * mm});
            skPoint(sketch, "E18.6.0.3", {"position": v(115.5, 479.97) * mm});
            skLineSegment(sketch, "E18.6.0.4", {"start": v(115.5, 497.8) * mm, "end": v(124.5, 497.8) * mm});
            skArc(sketch, "E18.6.0.5", {"start": v(115.5, 481.97) * mm, "mid": v(116.09, 480.56) * mm, "end": v(117.5, 479.97) * mm});
            skLineSegment(sketch, "E18.6.0.6", {"start": v(117.5, 479.97) * mm, "end": v(122.5, 479.97) * mm});
            skArc(sketch, "E18.6.0.7", {"start": v(122.5, 479.97) * mm, "mid": v(123.91, 480.56) * mm, "end": v(124.5, 481.97) * mm});
            skLineSegment(sketch, "E18.6.1.0", {"start": v(115.5, 447.33) * mm, "end": v(115.5, 463.15) * mm});
            skLineSegment(sketch, "E18.6.1.1", {"start": v(124.5, 447.33) * mm, "end": v(124.5, 463.15) * mm});
            skPoint(sketch, "E18.6.1.2", {"position": v(124.5, 445.33) * mm});
            skPoint(sketch, "E18.6.1.3", {"position": v(115.5, 445.33) * mm});
            skLineSegment(sketch, "E18.6.1.4", {"start": v(115.5, 463.15) * mm, "end": v(124.5, 463.15) * mm});
            skArc(sketch, "E18.6.1.5", {"start": v(115.5, 447.33) * mm, "mid": v(116.09, 445.92) * mm, "end": v(117.5, 445.33) * mm});
            skLineSegment(sketch, "E18.6.1.6", {"start": v(117.5, 445.33) * mm, "end": v(122.5, 445.33) * mm});
            skArc(sketch, "E18.6.1.7", {"start": v(122.5, 445.33) * mm, "mid": v(123.91, 445.92) * mm, "end": v(124.5, 447.33) * mm});
            skLineSegment(sketch, "E18.6.2.0", {"start": v(115.5, 412.7) * mm, "end": v(115.5, 428.51) * mm});
            skLineSegment(sketch, "E18.6.2.1", {"start": v(124.5, 412.7) * mm, "end": v(124.5, 428.51) * mm});
            skPoint(sketch, "E18.6.2.2", {"position": v(124.5, 410.7) * mm});
            skPoint(sketch, "E18.6.2.3", {"position": v(115.5, 410.7) * mm});
            skLineSegment(sketch, "E18.6.2.4", {"start": v(115.5, 428.51) * mm, "end": v(124.5, 428.51) * mm});
            skArc(sketch, "E18.6.2.5", {"start": v(115.5, 412.7) * mm, "mid": v(116.09, 411.28) * mm, "end": v(117.5, 410.7) * mm});
            skLineSegment(sketch, "E18.6.2.6", {"start": v(117.5, 410.7) * mm, "end": v(122.5, 410.7) * mm});
            skArc(sketch, "E18.6.2.7", {"start": v(122.5, 410.7) * mm, "mid": v(123.91, 411.28) * mm, "end": v(124.5, 412.7) * mm});
            skLineSegment(sketch, "E18.6.3.0", {"start": v(115.5, 378.05) * mm, "end": v(115.5, 393.87) * mm});
            skLineSegment(sketch, "E18.6.3.1", {"start": v(124.5, 378.05) * mm, "end": v(124.5, 393.87) * mm});
            skPoint(sketch, "E18.6.3.2", {"position": v(124.5, 376.05) * mm});
            skPoint(sketch, "E18.6.3.3", {"position": v(115.5, 376.05) * mm});
            skLineSegment(sketch, "E18.6.3.4", {"start": v(115.5, 393.87) * mm, "end": v(124.5, 393.87) * mm});
            skArc(sketch, "E18.6.3.5", {"start": v(115.5, 378.05) * mm, "mid": v(116.09, 376.64) * mm, "end": v(117.5, 376.05) * mm});
            skLineSegment(sketch, "E18.6.3.6", {"start": v(117.5, 376.05) * mm, "end": v(122.5, 376.05) * mm});
            skArc(sketch, "E18.6.3.7", {"start": v(122.5, 376.05) * mm, "mid": v(123.91, 376.64) * mm, "end": v(124.5, 378.05) * mm});
            skLineSegment(sketch, "E18.6.4.0", {"start": v(115.5, 343.41) * mm, "end": v(115.5, 359.23) * mm});
            skLineSegment(sketch, "E18.6.4.1", {"start": v(124.5, 343.41) * mm, "end": v(124.5, 359.23) * mm});
            skPoint(sketch, "E18.6.4.2", {"position": v(124.5, 341.41) * mm});
            skPoint(sketch, "E18.6.4.3", {"position": v(115.5, 341.41) * mm});
            skLineSegment(sketch, "E18.6.4.4", {"start": v(115.5, 359.23) * mm, "end": v(124.5, 359.23) * mm});
            skArc(sketch, "E18.6.4.5", {"start": v(115.5, 343.41) * mm, "mid": v(116.09, 342) * mm, "end": v(117.5, 341.41) * mm});
            skLineSegment(sketch, "E18.6.4.6", {"start": v(117.5, 341.41) * mm, "end": v(122.5, 341.41) * mm});
            skArc(sketch, "E18.6.4.7", {"start": v(122.5, 341.41) * mm, "mid": v(123.91, 342) * mm, "end": v(124.5, 343.41) * mm});
            skLineSegment(sketch, "E18.6.5.0", {"start": v(115.5, 308.77) * mm, "end": v(115.5, 324.59) * mm});
            skLineSegment(sketch, "E18.6.5.1", {"start": v(124.5, 308.77) * mm, "end": v(124.5, 324.59) * mm});
            skPoint(sketch, "E18.6.5.2", {"position": v(124.5, 306.77) * mm});
            skPoint(sketch, "E18.6.5.3", {"position": v(115.5, 306.77) * mm});
            skLineSegment(sketch, "E18.6.5.4", {"start": v(115.5, 324.59) * mm, "end": v(124.5, 324.59) * mm});
            skArc(sketch, "E18.6.5.5", {"start": v(115.5, 308.77) * mm, "mid": v(116.09, 307.35) * mm, "end": v(117.5, 306.77) * mm});
            skLineSegment(sketch, "E18.6.5.6", {"start": v(117.5, 306.77) * mm, "end": v(122.5, 306.77) * mm});
            skArc(sketch, "E18.6.5.7", {"start": v(122.5, 306.77) * mm, "mid": v(123.91, 307.35) * mm, "end": v(124.5, 308.77) * mm});
            skLineSegment(sketch, "E18.6.6.0", {"start": v(115.5, 274.13) * mm, "end": v(115.5, 289.95) * mm});
            skLineSegment(sketch, "E18.6.6.1", {"start": v(124.5, 274.13) * mm, "end": v(124.5, 289.95) * mm});
            skPoint(sketch, "E18.6.6.2", {"position": v(124.5, 272.13) * mm});
            skPoint(sketch, "E18.6.6.3", {"position": v(115.5, 272.13) * mm});
            skLineSegment(sketch, "E18.6.6.4", {"start": v(115.5, 289.95) * mm, "end": v(124.5, 289.95) * mm});
            skArc(sketch, "E18.6.6.5", {"start": v(115.5, 274.13) * mm, "mid": v(116.09, 272.71) * mm, "end": v(117.5, 272.13) * mm});
            skLineSegment(sketch, "E18.6.6.6", {"start": v(117.5, 272.13) * mm, "end": v(122.5, 272.13) * mm});
            skArc(sketch, "E18.6.6.7", {"start": v(122.5, 272.13) * mm, "mid": v(123.91, 272.71) * mm, "end": v(124.5, 274.13) * mm});
            skLineSegment(sketch, "E18.6.7.0", {"start": v(115.5, 239.49) * mm, "end": v(115.5, 255.3) * mm});
            skLineSegment(sketch, "E18.6.7.1", {"start": v(124.5, 239.49) * mm, "end": v(124.5, 255.3) * mm});
            skPoint(sketch, "E18.6.7.2", {"position": v(124.5, 237.49) * mm});
            skPoint(sketch, "E18.6.7.3", {"position": v(115.5, 237.49) * mm});
            skLineSegment(sketch, "E18.6.7.4", {"start": v(115.5, 255.3) * mm, "end": v(124.5, 255.3) * mm});
            skArc(sketch, "E18.6.7.5", {"start": v(115.5, 239.49) * mm, "mid": v(116.09, 238.07) * mm, "end": v(117.5, 237.49) * mm});
            skLineSegment(sketch, "E18.6.7.6", {"start": v(117.5, 237.49) * mm, "end": v(122.5, 237.49) * mm});
            skArc(sketch, "E18.6.7.7", {"start": v(122.5, 237.49) * mm, "mid": v(123.91, 238.07) * mm, "end": v(124.5, 239.49) * mm});
            skLineSegment(sketch, "E18.6.8.0", {"start": v(115.5, 204.85) * mm, "end": v(115.5, 220.67) * mm});
            skLineSegment(sketch, "E18.6.8.1", {"start": v(124.5, 204.85) * mm, "end": v(124.5, 220.67) * mm});
            skPoint(sketch, "E18.6.8.2", {"position": v(124.5, 202.85) * mm});
            skPoint(sketch, "E18.6.8.3", {"position": v(115.5, 202.85) * mm});
            skLineSegment(sketch, "E18.6.8.4", {"start": v(115.5, 220.67) * mm, "end": v(124.5, 220.67) * mm});
            skArc(sketch, "E18.6.8.5", {"start": v(115.5, 204.85) * mm, "mid": v(116.09, 203.43) * mm, "end": v(117.5, 202.85) * mm});
            skLineSegment(sketch, "E18.6.8.6", {"start": v(117.5, 202.85) * mm, "end": v(122.5, 202.85) * mm});
            skArc(sketch, "E18.6.8.7", {"start": v(122.5, 202.85) * mm, "mid": v(123.91, 203.43) * mm, "end": v(124.5, 204.85) * mm});
            skLineSegment(sketch, "E18.6.9.0", {"start": v(115.5, 170.2) * mm, "end": v(115.5, 186.03) * mm});
            skLineSegment(sketch, "E18.6.9.1", {"start": v(124.5, 170.2) * mm, "end": v(124.5, 186.03) * mm});
            skPoint(sketch, "E18.6.9.2", {"position": v(124.5, 168.2) * mm});
            skPoint(sketch, "E18.6.9.3", {"position": v(115.5, 168.2) * mm});
            skLineSegment(sketch, "E18.6.9.4", {"start": v(115.5, 186.03) * mm, "end": v(124.5, 186.03) * mm});
            skArc(sketch, "E18.6.9.5", {"start": v(115.5, 170.2) * mm, "mid": v(116.09, 168.8) * mm, "end": v(117.5, 168.2) * mm});
            skLineSegment(sketch, "E18.6.9.6", {"start": v(117.5, 168.2) * mm, "end": v(122.5, 168.2) * mm});
            skArc(sketch, "E18.6.9.7", {"start": v(122.5, 168.2) * mm, "mid": v(123.91, 168.8) * mm, "end": v(124.5, 170.2) * mm});
            skLineSegment(sketch, "E18.6.10.0", {"start": v(115.5, 135.56) * mm, "end": v(115.5, 151.38) * mm});
            skLineSegment(sketch, "E18.6.10.1", {"start": v(124.5, 135.56) * mm, "end": v(124.5, 151.38) * mm});
            skPoint(sketch, "E18.6.10.2", {"position": v(124.5, 133.56) * mm});
            skPoint(sketch, "E18.6.10.3", {"position": v(115.5, 133.56) * mm});
            skLineSegment(sketch, "E18.6.10.4", {"start": v(115.5, 151.38) * mm, "end": v(124.5, 151.38) * mm});
            skArc(sketch, "E18.6.10.5", {"start": v(115.5, 135.56) * mm, "mid": v(116.09, 134.15) * mm, "end": v(117.5, 133.56) * mm});
            skLineSegment(sketch, "E18.6.10.6", {"start": v(117.5, 133.56) * mm, "end": v(122.5, 133.56) * mm});
            skArc(sketch, "E18.6.10.7", {"start": v(122.5, 133.56) * mm, "mid": v(123.91, 134.15) * mm, "end": v(124.5, 135.56) * mm});
            skLineSegment(sketch, "E18.6.11.0", {"start": v(115.5, 100.92) * mm, "end": v(115.5, 116.74) * mm});
            skLineSegment(sketch, "E18.6.11.1", {"start": v(124.5, 100.92) * mm, "end": v(124.5, 116.74) * mm});
            skPoint(sketch, "E18.6.11.2", {"position": v(124.5, 98.92) * mm});
            skPoint(sketch, "E18.6.11.3", {"position": v(115.5, 98.92) * mm});
            skLineSegment(sketch, "E18.6.11.4", {"start": v(115.5, 116.74) * mm, "end": v(124.5, 116.74) * mm});
            skArc(sketch, "E18.6.11.5", {"start": v(115.5, 100.92) * mm, "mid": v(116.09, 99.5) * mm, "end": v(117.5, 98.92) * mm});
            skLineSegment(sketch, "E18.6.11.6", {"start": v(117.5, 98.92) * mm, "end": v(122.5, 98.92) * mm});
            skArc(sketch, "E18.6.11.7", {"start": v(122.5, 98.92) * mm, "mid": v(123.91, 99.5) * mm, "end": v(124.5, 100.92) * mm});
            skLineSegment(sketch, "E18.6.12.0", {"start": v(115.5, 66.28) * mm, "end": v(115.5, 82.1) * mm});
            skLineSegment(sketch, "E18.6.12.1", {"start": v(124.5, 66.28) * mm, "end": v(124.5, 82.1) * mm});
            skPoint(sketch, "E18.6.12.2", {"position": v(124.5, 64.28) * mm});
            skPoint(sketch, "E18.6.12.3", {"position": v(115.5, 64.28) * mm});
            skLineSegment(sketch, "E18.6.12.4", {"start": v(115.5, 82.1) * mm, "end": v(124.5, 82.1) * mm});
            skArc(sketch, "E18.6.12.5", {"start": v(115.5, 66.28) * mm, "mid": v(116.09, 64.87) * mm, "end": v(117.5, 64.28) * mm});
            skLineSegment(sketch, "E18.6.12.6", {"start": v(117.5, 64.28) * mm, "end": v(122.5, 64.28) * mm});
            skArc(sketch, "E18.6.12.7", {"start": v(122.5, 64.28) * mm, "mid": v(123.91, 64.87) * mm, "end": v(124.5, 66.28) * mm});
            skLineSegment(sketch, "E18.6.13.0", {"start": v(115.5, 31.64) * mm, "end": v(115.5, 47.46) * mm});
            skLineSegment(sketch, "E18.6.13.1", {"start": v(124.5, 31.64) * mm, "end": v(124.5, 47.46) * mm});
            skPoint(sketch, "E18.6.13.2", {"position": v(124.5, 29.64) * mm});
            skPoint(sketch, "E18.6.13.3", {"position": v(115.5, 29.64) * mm});
            skLineSegment(sketch, "E18.6.13.4", {"start": v(115.5, 47.46) * mm, "end": v(124.5, 47.46) * mm});
            skArc(sketch, "E18.6.13.5", {"start": v(115.5, 31.64) * mm, "mid": v(116.09, 30.23) * mm, "end": v(117.5, 29.64) * mm});
            skLineSegment(sketch, "E18.6.13.6", {"start": v(117.5, 29.64) * mm, "end": v(122.5, 29.64) * mm});
            skArc(sketch, "E18.6.13.7", {"start": v(122.5, 29.64) * mm, "mid": v(123.91, 30.23) * mm, "end": v(124.5, 31.64) * mm});
            skLineSegment(sketch, "E18.6.14.0", {"start": v(115.5, -3) * mm, "end": v(115.5, 12.82) * mm});
            skLineSegment(sketch, "E18.6.14.1", {"start": v(124.5, -3) * mm, "end": v(124.5, 12.82) * mm});
            skPoint(sketch, "E18.6.14.2", {"position": v(124.5, -5) * mm});
            skPoint(sketch, "E18.6.14.3", {"position": v(115.5, -5) * mm});
            skLineSegment(sketch, "E18.6.14.4", {"start": v(115.5, 12.82) * mm, "end": v(124.5, 12.82) * mm});
            skArc(sketch, "E18.6.14.5", {"start": v(115.5, -3) * mm, "mid": v(116.09, -4.41) * mm, "end": v(117.5, -5) * mm});
            skLineSegment(sketch, "E18.6.14.6", {"start": v(117.5, -5) * mm, "end": v(122.5, -5) * mm});
            skArc(sketch, "E18.6.14.7", {"start": v(122.5, -5) * mm, "mid": v(123.91, -4.41) * mm, "end": v(124.5, -3) * mm});
            skLineSegment(sketch, "E18.7.0.0", {"start": v(135.5, 481.97) * mm, "end": v(135.5, 497.8) * mm});
            skLineSegment(sketch, "E18.7.0.1", {"start": v(144.5, 481.97) * mm, "end": v(144.5, 497.8) * mm});
            skPoint(sketch, "E18.7.0.2", {"position": v(144.5, 479.97) * mm});
            skPoint(sketch, "E18.7.0.3", {"position": v(135.5, 479.97) * mm});
            skLineSegment(sketch, "E18.7.0.4", {"start": v(135.5, 497.8) * mm, "end": v(144.5, 497.8) * mm});
            skArc(sketch, "E18.7.0.5", {"start": v(135.5, 481.97) * mm, "mid": v(136.09, 480.56) * mm, "end": v(137.5, 479.97) * mm});
            skLineSegment(sketch, "E18.7.0.6", {"start": v(137.5, 479.97) * mm, "end": v(142.5, 479.97) * mm});
            skArc(sketch, "E18.7.0.7", {"start": v(142.5, 479.97) * mm, "mid": v(143.91, 480.56) * mm, "end": v(144.5, 481.97) * mm});
            skLineSegment(sketch, "E18.7.1.0", {"start": v(135.5, 447.33) * mm, "end": v(135.5, 463.15) * mm});
            skLineSegment(sketch, "E18.7.1.1", {"start": v(144.5, 447.33) * mm, "end": v(144.5, 463.15) * mm});
            skPoint(sketch, "E18.7.1.2", {"position": v(144.5, 445.33) * mm});
            skPoint(sketch, "E18.7.1.3", {"position": v(135.5, 445.33) * mm});
            skLineSegment(sketch, "E18.7.1.4", {"start": v(135.5, 463.15) * mm, "end": v(144.5, 463.15) * mm});
            skArc(sketch, "E18.7.1.5", {"start": v(135.5, 447.33) * mm, "mid": v(136.09, 445.92) * mm, "end": v(137.5, 445.33) * mm});
            skLineSegment(sketch, "E18.7.1.6", {"start": v(137.5, 445.33) * mm, "end": v(142.5, 445.33) * mm});
            skArc(sketch, "E18.7.1.7", {"start": v(142.5, 445.33) * mm, "mid": v(143.91, 445.92) * mm, "end": v(144.5, 447.33) * mm});
            skLineSegment(sketch, "E18.7.2.0", {"start": v(135.5, 412.7) * mm, "end": v(135.5, 428.51) * mm});
            skLineSegment(sketch, "E18.7.2.1", {"start": v(144.5, 412.7) * mm, "end": v(144.5, 428.51) * mm});
            skPoint(sketch, "E18.7.2.2", {"position": v(144.5, 410.7) * mm});
            skPoint(sketch, "E18.7.2.3", {"position": v(135.5, 410.7) * mm});
            skLineSegment(sketch, "E18.7.2.4", {"start": v(135.5, 428.51) * mm, "end": v(144.5, 428.51) * mm});
            skArc(sketch, "E18.7.2.5", {"start": v(135.5, 412.7) * mm, "mid": v(136.09, 411.28) * mm, "end": v(137.5, 410.7) * mm});
            skLineSegment(sketch, "E18.7.2.6", {"start": v(137.5, 410.7) * mm, "end": v(142.5, 410.7) * mm});
            skArc(sketch, "E18.7.2.7", {"start": v(142.5, 410.7) * mm, "mid": v(143.91, 411.28) * mm, "end": v(144.5, 412.7) * mm});
            skLineSegment(sketch, "E18.7.3.0", {"start": v(135.5, 378.05) * mm, "end": v(135.5, 393.87) * mm});
            skLineSegment(sketch, "E18.7.3.1", {"start": v(144.5, 378.05) * mm, "end": v(144.5, 393.87) * mm});
            skPoint(sketch, "E18.7.3.2", {"position": v(144.5, 376.05) * mm});
            skPoint(sketch, "E18.7.3.3", {"position": v(135.5, 376.05) * mm});
            skLineSegment(sketch, "E18.7.3.4", {"start": v(135.5, 393.87) * mm, "end": v(144.5, 393.87) * mm});
            skArc(sketch, "E18.7.3.5", {"start": v(135.5, 378.05) * mm, "mid": v(136.09, 376.64) * mm, "end": v(137.5, 376.05) * mm});
            skLineSegment(sketch, "E18.7.3.6", {"start": v(137.5, 376.05) * mm, "end": v(142.5, 376.05) * mm});
            skArc(sketch, "E18.7.3.7", {"start": v(142.5, 376.05) * mm, "mid": v(143.91, 376.64) * mm, "end": v(144.5, 378.05) * mm});
            skLineSegment(sketch, "E18.7.4.0", {"start": v(135.5, 343.41) * mm, "end": v(135.5, 359.23) * mm});
            skLineSegment(sketch, "E18.7.4.1", {"start": v(144.5, 343.41) * mm, "end": v(144.5, 359.23) * mm});
            skPoint(sketch, "E18.7.4.2", {"position": v(144.5, 341.41) * mm});
            skPoint(sketch, "E18.7.4.3", {"position": v(135.5, 341.41) * mm});
            skLineSegment(sketch, "E18.7.4.4", {"start": v(135.5, 359.23) * mm, "end": v(144.5, 359.23) * mm});
            skArc(sketch, "E18.7.4.5", {"start": v(135.5, 343.41) * mm, "mid": v(136.09, 342) * mm, "end": v(137.5, 341.41) * mm});
            skLineSegment(sketch, "E18.7.4.6", {"start": v(137.5, 341.41) * mm, "end": v(142.5, 341.41) * mm});
            skArc(sketch, "E18.7.4.7", {"start": v(142.5, 341.41) * mm, "mid": v(143.91, 342) * mm, "end": v(144.5, 343.41) * mm});
            skLineSegment(sketch, "E18.7.5.0", {"start": v(135.5, 308.77) * mm, "end": v(135.5, 324.59) * mm});
            skLineSegment(sketch, "E18.7.5.1", {"start": v(144.5, 308.77) * mm, "end": v(144.5, 324.59) * mm});
            skPoint(sketch, "E18.7.5.2", {"position": v(144.5, 306.77) * mm});
            skPoint(sketch, "E18.7.5.3", {"position": v(135.5, 306.77) * mm});
            skLineSegment(sketch, "E18.7.5.4", {"start": v(135.5, 324.59) * mm, "end": v(144.5, 324.59) * mm});
            skArc(sketch, "E18.7.5.5", {"start": v(135.5, 308.77) * mm, "mid": v(136.09, 307.35) * mm, "end": v(137.5, 306.77) * mm});
            skLineSegment(sketch, "E18.7.5.6", {"start": v(137.5, 306.77) * mm, "end": v(142.5, 306.77) * mm});
            skArc(sketch, "E18.7.5.7", {"start": v(142.5, 306.77) * mm, "mid": v(143.91, 307.35) * mm, "end": v(144.5, 308.77) * mm});
            skLineSegment(sketch, "E18.7.6.0", {"start": v(135.5, 274.13) * mm, "end": v(135.5, 289.95) * mm});
            skLineSegment(sketch, "E18.7.6.1", {"start": v(144.5, 274.13) * mm, "end": v(144.5, 289.95) * mm});
            skPoint(sketch, "E18.7.6.2", {"position": v(144.5, 272.13) * mm});
            skPoint(sketch, "E18.7.6.3", {"position": v(135.5, 272.13) * mm});
            skLineSegment(sketch, "E18.7.6.4", {"start": v(135.5, 289.95) * mm, "end": v(144.5, 289.95) * mm});
            skArc(sketch, "E18.7.6.5", {"start": v(135.5, 274.13) * mm, "mid": v(136.09, 272.71) * mm, "end": v(137.5, 272.13) * mm});
            skLineSegment(sketch, "E18.7.6.6", {"start": v(137.5, 272.13) * mm, "end": v(142.5, 272.13) * mm});
            skArc(sketch, "E18.7.6.7", {"start": v(142.5, 272.13) * mm, "mid": v(143.91, 272.71) * mm, "end": v(144.5, 274.13) * mm});
            skLineSegment(sketch, "E18.7.7.0", {"start": v(135.5, 239.49) * mm, "end": v(135.5, 255.3) * mm});
            skLineSegment(sketch, "E18.7.7.1", {"start": v(144.5, 239.49) * mm, "end": v(144.5, 255.3) * mm});
            skPoint(sketch, "E18.7.7.2", {"position": v(144.5, 237.49) * mm});
            skPoint(sketch, "E18.7.7.3", {"position": v(135.5, 237.49) * mm});
            skLineSegment(sketch, "E18.7.7.4", {"start": v(135.5, 255.3) * mm, "end": v(144.5, 255.3) * mm});
            skArc(sketch, "E18.7.7.5", {"start": v(135.5, 239.49) * mm, "mid": v(136.09, 238.07) * mm, "end": v(137.5, 237.49) * mm});
            skLineSegment(sketch, "E18.7.7.6", {"start": v(137.5, 237.49) * mm, "end": v(142.5, 237.49) * mm});
            skArc(sketch, "E18.7.7.7", {"start": v(142.5, 237.49) * mm, "mid": v(143.91, 238.07) * mm, "end": v(144.5, 239.49) * mm});
            skLineSegment(sketch, "E18.7.8.0", {"start": v(135.5, 204.85) * mm, "end": v(135.5, 220.67) * mm});
            skLineSegment(sketch, "E18.7.8.1", {"start": v(144.5, 204.85) * mm, "end": v(144.5, 220.67) * mm});
            skPoint(sketch, "E18.7.8.2", {"position": v(144.5, 202.85) * mm});
            skPoint(sketch, "E18.7.8.3", {"position": v(135.5, 202.85) * mm});
            skLineSegment(sketch, "E18.7.8.4", {"start": v(135.5, 220.67) * mm, "end": v(144.5, 220.67) * mm});
            skArc(sketch, "E18.7.8.5", {"start": v(135.5, 204.85) * mm, "mid": v(136.09, 203.43) * mm, "end": v(137.5, 202.85) * mm});
            skLineSegment(sketch, "E18.7.8.6", {"start": v(137.5, 202.85) * mm, "end": v(142.5, 202.85) * mm});
            skArc(sketch, "E18.7.8.7", {"start": v(142.5, 202.85) * mm, "mid": v(143.91, 203.43) * mm, "end": v(144.5, 204.85) * mm});
            skLineSegment(sketch, "E18.7.9.0", {"start": v(135.5, 170.2) * mm, "end": v(135.5, 186.03) * mm});
            skLineSegment(sketch, "E18.7.9.1", {"start": v(144.5, 170.2) * mm, "end": v(144.5, 186.03) * mm});
            skPoint(sketch, "E18.7.9.2", {"position": v(144.5, 168.2) * mm});
            skPoint(sketch, "E18.7.9.3", {"position": v(135.5, 168.2) * mm});
            skLineSegment(sketch, "E18.7.9.4", {"start": v(135.5, 186.03) * mm, "end": v(144.5, 186.03) * mm});
            skArc(sketch, "E18.7.9.5", {"start": v(135.5, 170.2) * mm, "mid": v(136.09, 168.8) * mm, "end": v(137.5, 168.2) * mm});
            skLineSegment(sketch, "E18.7.9.6", {"start": v(137.5, 168.2) * mm, "end": v(142.5, 168.2) * mm});
            skArc(sketch, "E18.7.9.7", {"start": v(142.5, 168.2) * mm, "mid": v(143.91, 168.8) * mm, "end": v(144.5, 170.2) * mm});
            skLineSegment(sketch, "E18.7.10.0", {"start": v(135.5, 135.56) * mm, "end": v(135.5, 151.38) * mm});
            skLineSegment(sketch, "E18.7.10.1", {"start": v(144.5, 135.56) * mm, "end": v(144.5, 151.38) * mm});
            skPoint(sketch, "E18.7.10.2", {"position": v(144.5, 133.56) * mm});
            skPoint(sketch, "E18.7.10.3", {"position": v(135.5, 133.56) * mm});
            skLineSegment(sketch, "E18.7.10.4", {"start": v(135.5, 151.38) * mm, "end": v(144.5, 151.38) * mm});
            skArc(sketch, "E18.7.10.5", {"start": v(135.5, 135.56) * mm, "mid": v(136.09, 134.15) * mm, "end": v(137.5, 133.56) * mm});
            skLineSegment(sketch, "E18.7.10.6", {"start": v(137.5, 133.56) * mm, "end": v(142.5, 133.56) * mm});
            skArc(sketch, "E18.7.10.7", {"start": v(142.5, 133.56) * mm, "mid": v(143.91, 134.15) * mm, "end": v(144.5, 135.56) * mm});
            skLineSegment(sketch, "E18.7.11.0", {"start": v(135.5, 100.92) * mm, "end": v(135.5, 116.74) * mm});
            skLineSegment(sketch, "E18.7.11.1", {"start": v(144.5, 100.92) * mm, "end": v(144.5, 116.74) * mm});
            skPoint(sketch, "E18.7.11.2", {"position": v(144.5, 98.92) * mm});
            skPoint(sketch, "E18.7.11.3", {"position": v(135.5, 98.92) * mm});
            skLineSegment(sketch, "E18.7.11.4", {"start": v(135.5, 116.74) * mm, "end": v(144.5, 116.74) * mm});
            skArc(sketch, "E18.7.11.5", {"start": v(135.5, 100.92) * mm, "mid": v(136.09, 99.5) * mm, "end": v(137.5, 98.92) * mm});
            skLineSegment(sketch, "E18.7.11.6", {"start": v(137.5, 98.92) * mm, "end": v(142.5, 98.92) * mm});
            skArc(sketch, "E18.7.11.7", {"start": v(142.5, 98.92) * mm, "mid": v(143.91, 99.5) * mm, "end": v(144.5, 100.92) * mm});
            skLineSegment(sketch, "E18.7.12.0", {"start": v(135.5, 66.28) * mm, "end": v(135.5, 82.1) * mm});
            skLineSegment(sketch, "E18.7.12.1", {"start": v(144.5, 66.28) * mm, "end": v(144.5, 82.1) * mm});
            skPoint(sketch, "E18.7.12.2", {"position": v(144.5, 64.28) * mm});
            skPoint(sketch, "E18.7.12.3", {"position": v(135.5, 64.28) * mm});
            skLineSegment(sketch, "E18.7.12.4", {"start": v(135.5, 82.1) * mm, "end": v(144.5, 82.1) * mm});
            skArc(sketch, "E18.7.12.5", {"start": v(135.5, 66.28) * mm, "mid": v(136.09, 64.87) * mm, "end": v(137.5, 64.28) * mm});
            skLineSegment(sketch, "E18.7.12.6", {"start": v(137.5, 64.28) * mm, "end": v(142.5, 64.28) * mm});
            skArc(sketch, "E18.7.12.7", {"start": v(142.5, 64.28) * mm, "mid": v(143.91, 64.87) * mm, "end": v(144.5, 66.28) * mm});
            skLineSegment(sketch, "E18.7.13.0", {"start": v(135.5, 31.64) * mm, "end": v(135.5, 47.46) * mm});
            skLineSegment(sketch, "E18.7.13.1", {"start": v(144.5, 31.64) * mm, "end": v(144.5, 47.46) * mm});
            skPoint(sketch, "E18.7.13.2", {"position": v(144.5, 29.64) * mm});
            skPoint(sketch, "E18.7.13.3", {"position": v(135.5, 29.64) * mm});
            skLineSegment(sketch, "E18.7.13.4", {"start": v(135.5, 47.46) * mm, "end": v(144.5, 47.46) * mm});
            skArc(sketch, "E18.7.13.5", {"start": v(135.5, 31.64) * mm, "mid": v(136.09, 30.23) * mm, "end": v(137.5, 29.64) * mm});
            skLineSegment(sketch, "E18.7.13.6", {"start": v(137.5, 29.64) * mm, "end": v(142.5, 29.64) * mm});
            skArc(sketch, "E18.7.13.7", {"start": v(142.5, 29.64) * mm, "mid": v(143.91, 30.23) * mm, "end": v(144.5, 31.64) * mm});
            skLineSegment(sketch, "E18.7.14.0", {"start": v(135.5, -3) * mm, "end": v(135.5, 12.82) * mm});
            skLineSegment(sketch, "E18.7.14.1", {"start": v(144.5, -3) * mm, "end": v(144.5, 12.82) * mm});
            skPoint(sketch, "E18.7.14.2", {"position": v(144.5, -5) * mm});
            skPoint(sketch, "E18.7.14.3", {"position": v(135.5, -5) * mm});
            skLineSegment(sketch, "E18.7.14.4", {"start": v(135.5, 12.82) * mm, "end": v(144.5, 12.82) * mm});
            skArc(sketch, "E18.7.14.5", {"start": v(135.5, -3) * mm, "mid": v(136.09, -4.41) * mm, "end": v(137.5, -5) * mm});
            skLineSegment(sketch, "E18.7.14.6", {"start": v(137.5, -5) * mm, "end": v(142.5, -5) * mm});
            skArc(sketch, "E18.7.14.7", {"start": v(142.5, -5) * mm, "mid": v(143.91, -4.41) * mm, "end": v(144.5, -3) * mm});
            skLineSegment(sketch, "E18.8.0.0", {"start": v(155.5, 481.97) * mm, "end": v(155.5, 497.8) * mm});
            skLineSegment(sketch, "E18.8.0.1", {"start": v(164.5, 481.97) * mm, "end": v(164.5, 497.8) * mm});
            skPoint(sketch, "E18.8.0.2", {"position": v(164.5, 479.97) * mm});
            skPoint(sketch, "E18.8.0.3", {"position": v(155.5, 479.97) * mm});
            skLineSegment(sketch, "E18.8.0.4", {"start": v(155.5, 497.8) * mm, "end": v(164.5, 497.8) * mm});
            skArc(sketch, "E18.8.0.5", {"start": v(155.5, 481.97) * mm, "mid": v(156.09, 480.56) * mm, "end": v(157.5, 479.97) * mm});
            skLineSegment(sketch, "E18.8.0.6", {"start": v(157.5, 479.97) * mm, "end": v(162.5, 479.97) * mm});
            skArc(sketch, "E18.8.0.7", {"start": v(162.5, 479.97) * mm, "mid": v(163.91, 480.56) * mm, "end": v(164.5, 481.97) * mm});
            skLineSegment(sketch, "E18.8.1.0", {"start": v(155.5, 447.33) * mm, "end": v(155.5, 463.15) * mm});
            skLineSegment(sketch, "E18.8.1.1", {"start": v(164.5, 447.33) * mm, "end": v(164.5, 463.15) * mm});
            skPoint(sketch, "E18.8.1.2", {"position": v(164.5, 445.33) * mm});
            skPoint(sketch, "E18.8.1.3", {"position": v(155.5, 445.33) * mm});
            skLineSegment(sketch, "E18.8.1.4", {"start": v(155.5, 463.15) * mm, "end": v(164.5, 463.15) * mm});
            skArc(sketch, "E18.8.1.5", {"start": v(155.5, 447.33) * mm, "mid": v(156.09, 445.92) * mm, "end": v(157.5, 445.33) * mm});
            skLineSegment(sketch, "E18.8.1.6", {"start": v(157.5, 445.33) * mm, "end": v(162.5, 445.33) * mm});
            skArc(sketch, "E18.8.1.7", {"start": v(162.5, 445.33) * mm, "mid": v(163.91, 445.92) * mm, "end": v(164.5, 447.33) * mm});
            skLineSegment(sketch, "E18.8.2.0", {"start": v(155.5, 412.7) * mm, "end": v(155.5, 428.51) * mm});
            skLineSegment(sketch, "E18.8.2.1", {"start": v(164.5, 412.7) * mm, "end": v(164.5, 428.51) * mm});
            skPoint(sketch, "E18.8.2.2", {"position": v(164.5, 410.7) * mm});
            skPoint(sketch, "E18.8.2.3", {"position": v(155.5, 410.7) * mm});
            skLineSegment(sketch, "E18.8.2.4", {"start": v(155.5, 428.51) * mm, "end": v(164.5, 428.51) * mm});
            skArc(sketch, "E18.8.2.5", {"start": v(155.5, 412.7) * mm, "mid": v(156.09, 411.28) * mm, "end": v(157.5, 410.7) * mm});
            skLineSegment(sketch, "E18.8.2.6", {"start": v(157.5, 410.7) * mm, "end": v(162.5, 410.7) * mm});
            skArc(sketch, "E18.8.2.7", {"start": v(162.5, 410.7) * mm, "mid": v(163.91, 411.28) * mm, "end": v(164.5, 412.7) * mm});
            skLineSegment(sketch, "E18.8.3.0", {"start": v(155.5, 378.05) * mm, "end": v(155.5, 393.87) * mm});
            skLineSegment(sketch, "E18.8.3.1", {"start": v(164.5, 378.05) * mm, "end": v(164.5, 393.87) * mm});
            skPoint(sketch, "E18.8.3.2", {"position": v(164.5, 376.05) * mm});
            skPoint(sketch, "E18.8.3.3", {"position": v(155.5, 376.05) * mm});
            skLineSegment(sketch, "E18.8.3.4", {"start": v(155.5, 393.87) * mm, "end": v(164.5, 393.87) * mm});
            skArc(sketch, "E18.8.3.5", {"start": v(155.5, 378.05) * mm, "mid": v(156.09, 376.64) * mm, "end": v(157.5, 376.05) * mm});
            skLineSegment(sketch, "E18.8.3.6", {"start": v(157.5, 376.05) * mm, "end": v(162.5, 376.05) * mm});
            skArc(sketch, "E18.8.3.7", {"start": v(162.5, 376.05) * mm, "mid": v(163.91, 376.64) * mm, "end": v(164.5, 378.05) * mm});
            skLineSegment(sketch, "E18.8.4.0", {"start": v(155.5, 343.41) * mm, "end": v(155.5, 359.23) * mm});
            skLineSegment(sketch, "E18.8.4.1", {"start": v(164.5, 343.41) * mm, "end": v(164.5, 359.23) * mm});
            skPoint(sketch, "E18.8.4.2", {"position": v(164.5, 341.41) * mm});
            skPoint(sketch, "E18.8.4.3", {"position": v(155.5, 341.41) * mm});
            skLineSegment(sketch, "E18.8.4.4", {"start": v(155.5, 359.23) * mm, "end": v(164.5, 359.23) * mm});
            skArc(sketch, "E18.8.4.5", {"start": v(155.5, 343.41) * mm, "mid": v(156.09, 342) * mm, "end": v(157.5, 341.41) * mm});
            skLineSegment(sketch, "E18.8.4.6", {"start": v(157.5, 341.41) * mm, "end": v(162.5, 341.41) * mm});
            skArc(sketch, "E18.8.4.7", {"start": v(162.5, 341.41) * mm, "mid": v(163.91, 342) * mm, "end": v(164.5, 343.41) * mm});
            skLineSegment(sketch, "E18.8.5.0", {"start": v(155.5, 308.77) * mm, "end": v(155.5, 324.59) * mm});
            skLineSegment(sketch, "E18.8.5.1", {"start": v(164.5, 308.77) * mm, "end": v(164.5, 324.59) * mm});
            skPoint(sketch, "E18.8.5.2", {"position": v(164.5, 306.77) * mm});
            skPoint(sketch, "E18.8.5.3", {"position": v(155.5, 306.77) * mm});
            skLineSegment(sketch, "E18.8.5.4", {"start": v(155.5, 324.59) * mm, "end": v(164.5, 324.59) * mm});
            skArc(sketch, "E18.8.5.5", {"start": v(155.5, 308.77) * mm, "mid": v(156.09, 307.35) * mm, "end": v(157.5, 306.77) * mm});
            skLineSegment(sketch, "E18.8.5.6", {"start": v(157.5, 306.77) * mm, "end": v(162.5, 306.77) * mm});
            skArc(sketch, "E18.8.5.7", {"start": v(162.5, 306.77) * mm, "mid": v(163.91, 307.35) * mm, "end": v(164.5, 308.77) * mm});
            skLineSegment(sketch, "E18.8.6.0", {"start": v(155.5, 274.13) * mm, "end": v(155.5, 289.95) * mm});
            skLineSegment(sketch, "E18.8.6.1", {"start": v(164.5, 274.13) * mm, "end": v(164.5, 289.95) * mm});
            skPoint(sketch, "E18.8.6.2", {"position": v(164.5, 272.13) * mm});
            skPoint(sketch, "E18.8.6.3", {"position": v(155.5, 272.13) * mm});
            skLineSegment(sketch, "E18.8.6.4", {"start": v(155.5, 289.95) * mm, "end": v(164.5, 289.95) * mm});
            skArc(sketch, "E18.8.6.5", {"start": v(155.5, 274.13) * mm, "mid": v(156.09, 272.71) * mm, "end": v(157.5, 272.13) * mm});
            skLineSegment(sketch, "E18.8.6.6", {"start": v(157.5, 272.13) * mm, "end": v(162.5, 272.13) * mm});
            skArc(sketch, "E18.8.6.7", {"start": v(162.5, 272.13) * mm, "mid": v(163.91, 272.71) * mm, "end": v(164.5, 274.13) * mm});
            skLineSegment(sketch, "E18.8.7.0", {"start": v(155.5, 239.49) * mm, "end": v(155.5, 255.3) * mm});
            skLineSegment(sketch, "E18.8.7.1", {"start": v(164.5, 239.49) * mm, "end": v(164.5, 255.3) * mm});
            skPoint(sketch, "E18.8.7.2", {"position": v(164.5, 237.49) * mm});
            skPoint(sketch, "E18.8.7.3", {"position": v(155.5, 237.49) * mm});
            skLineSegment(sketch, "E18.8.7.4", {"start": v(155.5, 255.3) * mm, "end": v(164.5, 255.3) * mm});
            skArc(sketch, "E18.8.7.5", {"start": v(155.5, 239.49) * mm, "mid": v(156.09, 238.07) * mm, "end": v(157.5, 237.49) * mm});
            skLineSegment(sketch, "E18.8.7.6", {"start": v(157.5, 237.49) * mm, "end": v(162.5, 237.49) * mm});
            skArc(sketch, "E18.8.7.7", {"start": v(162.5, 237.49) * mm, "mid": v(163.91, 238.07) * mm, "end": v(164.5, 239.49) * mm});
            skLineSegment(sketch, "E18.8.8.0", {"start": v(155.5, 204.85) * mm, "end": v(155.5, 220.67) * mm});
            skLineSegment(sketch, "E18.8.8.1", {"start": v(164.5, 204.85) * mm, "end": v(164.5, 220.67) * mm});
            skPoint(sketch, "E18.8.8.2", {"position": v(164.5, 202.85) * mm});
            skPoint(sketch, "E18.8.8.3", {"position": v(155.5, 202.85) * mm});
            skLineSegment(sketch, "E18.8.8.4", {"start": v(155.5, 220.67) * mm, "end": v(164.5, 220.67) * mm});
            skArc(sketch, "E18.8.8.5", {"start": v(155.5, 204.85) * mm, "mid": v(156.09, 203.43) * mm, "end": v(157.5, 202.85) * mm});
            skLineSegment(sketch, "E18.8.8.6", {"start": v(157.5, 202.85) * mm, "end": v(162.5, 202.85) * mm});
            skArc(sketch, "E18.8.8.7", {"start": v(162.5, 202.85) * mm, "mid": v(163.91, 203.43) * mm, "end": v(164.5, 204.85) * mm});
            skLineSegment(sketch, "E18.8.9.0", {"start": v(155.5, 170.2) * mm, "end": v(155.5, 186.03) * mm});
            skLineSegment(sketch, "E18.8.9.1", {"start": v(164.5, 170.2) * mm, "end": v(164.5, 186.03) * mm});
            skPoint(sketch, "E18.8.9.2", {"position": v(164.5, 168.2) * mm});
            skPoint(sketch, "E18.8.9.3", {"position": v(155.5, 168.2) * mm});
            skLineSegment(sketch, "E18.8.9.4", {"start": v(155.5, 186.03) * mm, "end": v(164.5, 186.03) * mm});
            skArc(sketch, "E18.8.9.5", {"start": v(155.5, 170.2) * mm, "mid": v(156.09, 168.8) * mm, "end": v(157.5, 168.2) * mm});
            skLineSegment(sketch, "E18.8.9.6", {"start": v(157.5, 168.2) * mm, "end": v(162.5, 168.2) * mm});
            skArc(sketch, "E18.8.9.7", {"start": v(162.5, 168.2) * mm, "mid": v(163.91, 168.8) * mm, "end": v(164.5, 170.2) * mm});
            skLineSegment(sketch, "E18.8.10.0", {"start": v(155.5, 135.56) * mm, "end": v(155.5, 151.38) * mm});
            skLineSegment(sketch, "E18.8.10.1", {"start": v(164.5, 135.56) * mm, "end": v(164.5, 151.38) * mm});
            skPoint(sketch, "E18.8.10.2", {"position": v(164.5, 133.56) * mm});
            skPoint(sketch, "E18.8.10.3", {"position": v(155.5, 133.56) * mm});
            skLineSegment(sketch, "E18.8.10.4", {"start": v(155.5, 151.38) * mm, "end": v(164.5, 151.38) * mm});
            skArc(sketch, "E18.8.10.5", {"start": v(155.5, 135.56) * mm, "mid": v(156.09, 134.15) * mm, "end": v(157.5, 133.56) * mm});
            skLineSegment(sketch, "E18.8.10.6", {"start": v(157.5, 133.56) * mm, "end": v(162.5, 133.56) * mm});
            skArc(sketch, "E18.8.10.7", {"start": v(162.5, 133.56) * mm, "mid": v(163.91, 134.15) * mm, "end": v(164.5, 135.56) * mm});
            skLineSegment(sketch, "E18.8.11.0", {"start": v(155.5, 100.92) * mm, "end": v(155.5, 116.74) * mm});
            skLineSegment(sketch, "E18.8.11.1", {"start": v(164.5, 100.92) * mm, "end": v(164.5, 116.74) * mm});
            skPoint(sketch, "E18.8.11.2", {"position": v(164.5, 98.92) * mm});
            skPoint(sketch, "E18.8.11.3", {"position": v(155.5, 98.92) * mm});
            skLineSegment(sketch, "E18.8.11.4", {"start": v(155.5, 116.74) * mm, "end": v(164.5, 116.74) * mm});
            skArc(sketch, "E18.8.11.5", {"start": v(155.5, 100.92) * mm, "mid": v(156.09, 99.5) * mm, "end": v(157.5, 98.92) * mm});
            skLineSegment(sketch, "E18.8.11.6", {"start": v(157.5, 98.92) * mm, "end": v(162.5, 98.92) * mm});
            skArc(sketch, "E18.8.11.7", {"start": v(162.5, 98.92) * mm, "mid": v(163.91, 99.5) * mm, "end": v(164.5, 100.92) * mm});
            skLineSegment(sketch, "E18.8.12.0", {"start": v(155.5, 66.28) * mm, "end": v(155.5, 82.1) * mm});
            skLineSegment(sketch, "E18.8.12.1", {"start": v(164.5, 66.28) * mm, "end": v(164.5, 82.1) * mm});
            skPoint(sketch, "E18.8.12.2", {"position": v(164.5, 64.28) * mm});
            skPoint(sketch, "E18.8.12.3", {"position": v(155.5, 64.28) * mm});
            skLineSegment(sketch, "E18.8.12.4", {"start": v(155.5, 82.1) * mm, "end": v(164.5, 82.1) * mm});
            skArc(sketch, "E18.8.12.5", {"start": v(155.5, 66.28) * mm, "mid": v(156.09, 64.87) * mm, "end": v(157.5, 64.28) * mm});
            skLineSegment(sketch, "E18.8.12.6", {"start": v(157.5, 64.28) * mm, "end": v(162.5, 64.28) * mm});
            skArc(sketch, "E18.8.12.7", {"start": v(162.5, 64.28) * mm, "mid": v(163.91, 64.87) * mm, "end": v(164.5, 66.28) * mm});
            skLineSegment(sketch, "E18.8.13.0", {"start": v(155.5, 31.64) * mm, "end": v(155.5, 47.46) * mm});
            skLineSegment(sketch, "E18.8.13.1", {"start": v(164.5, 31.64) * mm, "end": v(164.5, 47.46) * mm});
            skPoint(sketch, "E18.8.13.2", {"position": v(164.5, 29.64) * mm});
            skPoint(sketch, "E18.8.13.3", {"position": v(155.5, 29.64) * mm});
            skLineSegment(sketch, "E18.8.13.4", {"start": v(155.5, 47.46) * mm, "end": v(164.5, 47.46) * mm});
            skArc(sketch, "E18.8.13.5", {"start": v(155.5, 31.64) * mm, "mid": v(156.09, 30.23) * mm, "end": v(157.5, 29.64) * mm});
            skLineSegment(sketch, "E18.8.13.6", {"start": v(157.5, 29.64) * mm, "end": v(162.5, 29.64) * mm});
            skArc(sketch, "E18.8.13.7", {"start": v(162.5, 29.64) * mm, "mid": v(163.91, 30.23) * mm, "end": v(164.5, 31.64) * mm});
            skLineSegment(sketch, "E18.8.14.0", {"start": v(155.5, -3) * mm, "end": v(155.5, 12.82) * mm});
            skLineSegment(sketch, "E18.8.14.1", {"start": v(164.5, -3) * mm, "end": v(164.5, 12.82) * mm});
            skPoint(sketch, "E18.8.14.2", {"position": v(164.5, -5) * mm});
            skPoint(sketch, "E18.8.14.3", {"position": v(155.5, -5) * mm});
            skLineSegment(sketch, "E18.8.14.4", {"start": v(155.5, 12.82) * mm, "end": v(164.5, 12.82) * mm});
            skArc(sketch, "E18.8.14.5", {"start": v(155.5, -3) * mm, "mid": v(156.09, -4.41) * mm, "end": v(157.5, -5) * mm});
            skLineSegment(sketch, "E18.8.14.6", {"start": v(157.5, -5) * mm, "end": v(162.5, -5) * mm});
            skArc(sketch, "E18.8.14.7", {"start": v(162.5, -5) * mm, "mid": v(163.91, -4.41) * mm, "end": v(164.5, -3) * mm});
            skLineSegment(sketch, "E18.9.0.0", {"start": v(175.5, 481.97) * mm, "end": v(175.5, 497.8) * mm});
            skLineSegment(sketch, "E18.9.0.1", {"start": v(184.5, 481.97) * mm, "end": v(184.5, 497.8) * mm});
            skPoint(sketch, "E18.9.0.2", {"position": v(184.5, 479.97) * mm});
            skPoint(sketch, "E18.9.0.3", {"position": v(175.5, 479.97) * mm});
            skLineSegment(sketch, "E18.9.0.4", {"start": v(175.5, 497.8) * mm, "end": v(184.5, 497.8) * mm});
            skArc(sketch, "E18.9.0.5", {"start": v(175.5, 481.97) * mm, "mid": v(176.09, 480.56) * mm, "end": v(177.5, 479.97) * mm});
            skLineSegment(sketch, "E18.9.0.6", {"start": v(177.5, 479.97) * mm, "end": v(182.5, 479.97) * mm});
            skArc(sketch, "E18.9.0.7", {"start": v(182.5, 479.97) * mm, "mid": v(183.91, 480.56) * mm, "end": v(184.5, 481.97) * mm});
            skLineSegment(sketch, "E18.9.1.0", {"start": v(175.5, 447.33) * mm, "end": v(175.5, 463.15) * mm});
            skLineSegment(sketch, "E18.9.1.1", {"start": v(184.5, 447.33) * mm, "end": v(184.5, 463.15) * mm});
            skPoint(sketch, "E18.9.1.2", {"position": v(184.5, 445.33) * mm});
            skPoint(sketch, "E18.9.1.3", {"position": v(175.5, 445.33) * mm});
            skLineSegment(sketch, "E18.9.1.4", {"start": v(175.5, 463.15) * mm, "end": v(184.5, 463.15) * mm});
            skArc(sketch, "E18.9.1.5", {"start": v(175.5, 447.33) * mm, "mid": v(176.09, 445.92) * mm, "end": v(177.5, 445.33) * mm});
            skLineSegment(sketch, "E18.9.1.6", {"start": v(177.5, 445.33) * mm, "end": v(182.5, 445.33) * mm});
            skArc(sketch, "E18.9.1.7", {"start": v(182.5, 445.33) * mm, "mid": v(183.91, 445.92) * mm, "end": v(184.5, 447.33) * mm});
            skLineSegment(sketch, "E18.9.2.0", {"start": v(175.5, 412.7) * mm, "end": v(175.5, 428.51) * mm});
            skLineSegment(sketch, "E18.9.2.1", {"start": v(184.5, 412.7) * mm, "end": v(184.5, 428.51) * mm});
            skPoint(sketch, "E18.9.2.2", {"position": v(184.5, 410.7) * mm});
            skPoint(sketch, "E18.9.2.3", {"position": v(175.5, 410.7) * mm});
            skLineSegment(sketch, "E18.9.2.4", {"start": v(175.5, 428.51) * mm, "end": v(184.5, 428.51) * mm});
            skArc(sketch, "E18.9.2.5", {"start": v(175.5, 412.7) * mm, "mid": v(176.09, 411.28) * mm, "end": v(177.5, 410.7) * mm});
            skLineSegment(sketch, "E18.9.2.6", {"start": v(177.5, 410.7) * mm, "end": v(182.5, 410.7) * mm});
            skArc(sketch, "E18.9.2.7", {"start": v(182.5, 410.7) * mm, "mid": v(183.91, 411.28) * mm, "end": v(184.5, 412.7) * mm});
            skLineSegment(sketch, "E18.9.3.0", {"start": v(175.5, 378.05) * mm, "end": v(175.5, 393.87) * mm});
            skLineSegment(sketch, "E18.9.3.1", {"start": v(184.5, 378.05) * mm, "end": v(184.5, 393.87) * mm});
            skPoint(sketch, "E18.9.3.2", {"position": v(184.5, 376.05) * mm});
            skPoint(sketch, "E18.9.3.3", {"position": v(175.5, 376.05) * mm});
            skLineSegment(sketch, "E18.9.3.4", {"start": v(175.5, 393.87) * mm, "end": v(184.5, 393.87) * mm});
            skArc(sketch, "E18.9.3.5", {"start": v(175.5, 378.05) * mm, "mid": v(176.09, 376.64) * mm, "end": v(177.5, 376.05) * mm});
            skLineSegment(sketch, "E18.9.3.6", {"start": v(177.5, 376.05) * mm, "end": v(182.5, 376.05) * mm});
            skArc(sketch, "E18.9.3.7", {"start": v(182.5, 376.05) * mm, "mid": v(183.91, 376.64) * mm, "end": v(184.5, 378.05) * mm});
            skLineSegment(sketch, "E18.9.4.0", {"start": v(175.5, 343.41) * mm, "end": v(175.5, 359.23) * mm});
            skLineSegment(sketch, "E18.9.4.1", {"start": v(184.5, 343.41) * mm, "end": v(184.5, 359.23) * mm});
            skPoint(sketch, "E18.9.4.2", {"position": v(184.5, 341.41) * mm});
            skPoint(sketch, "E18.9.4.3", {"position": v(175.5, 341.41) * mm});
            skLineSegment(sketch, "E18.9.4.4", {"start": v(175.5, 359.23) * mm, "end": v(184.5, 359.23) * mm});
            skArc(sketch, "E18.9.4.5", {"start": v(175.5, 343.41) * mm, "mid": v(176.09, 342) * mm, "end": v(177.5, 341.41) * mm});
            skLineSegment(sketch, "E18.9.4.6", {"start": v(177.5, 341.41) * mm, "end": v(182.5, 341.41) * mm});
            skArc(sketch, "E18.9.4.7", {"start": v(182.5, 341.41) * mm, "mid": v(183.91, 342) * mm, "end": v(184.5, 343.41) * mm});
            skLineSegment(sketch, "E18.9.5.0", {"start": v(175.5, 308.77) * mm, "end": v(175.5, 324.59) * mm});
            skLineSegment(sketch, "E18.9.5.1", {"start": v(184.5, 308.77) * mm, "end": v(184.5, 324.59) * mm});
            skPoint(sketch, "E18.9.5.2", {"position": v(184.5, 306.77) * mm});
            skPoint(sketch, "E18.9.5.3", {"position": v(175.5, 306.77) * mm});
            skLineSegment(sketch, "E18.9.5.4", {"start": v(175.5, 324.59) * mm, "end": v(184.5, 324.59) * mm});
            skArc(sketch, "E18.9.5.5", {"start": v(175.5, 308.77) * mm, "mid": v(176.09, 307.35) * mm, "end": v(177.5, 306.77) * mm});
            skLineSegment(sketch, "E18.9.5.6", {"start": v(177.5, 306.77) * mm, "end": v(182.5, 306.77) * mm});
            skArc(sketch, "E18.9.5.7", {"start": v(182.5, 306.77) * mm, "mid": v(183.91, 307.35) * mm, "end": v(184.5, 308.77) * mm});
            skLineSegment(sketch, "E18.9.6.0", {"start": v(175.5, 274.13) * mm, "end": v(175.5, 289.95) * mm});
            skLineSegment(sketch, "E18.9.6.1", {"start": v(184.5, 274.13) * mm, "end": v(184.5, 289.95) * mm});
            skPoint(sketch, "E18.9.6.2", {"position": v(184.5, 272.13) * mm});
            skPoint(sketch, "E18.9.6.3", {"position": v(175.5, 272.13) * mm});
            skLineSegment(sketch, "E18.9.6.4", {"start": v(175.5, 289.95) * mm, "end": v(184.5, 289.95) * mm});
            skArc(sketch, "E18.9.6.5", {"start": v(175.5, 274.13) * mm, "mid": v(176.09, 272.71) * mm, "end": v(177.5, 272.13) * mm});
            skLineSegment(sketch, "E18.9.6.6", {"start": v(177.5, 272.13) * mm, "end": v(182.5, 272.13) * mm});
            skArc(sketch, "E18.9.6.7", {"start": v(182.5, 272.13) * mm, "mid": v(183.91, 272.71) * mm, "end": v(184.5, 274.13) * mm});
            skLineSegment(sketch, "E18.9.7.0", {"start": v(175.5, 239.49) * mm, "end": v(175.5, 255.3) * mm});
            skLineSegment(sketch, "E18.9.7.1", {"start": v(184.5, 239.49) * mm, "end": v(184.5, 255.3) * mm});
            skPoint(sketch, "E18.9.7.2", {"position": v(184.5, 237.49) * mm});
            skPoint(sketch, "E18.9.7.3", {"position": v(175.5, 237.49) * mm});
            skLineSegment(sketch, "E18.9.7.4", {"start": v(175.5, 255.3) * mm, "end": v(184.5, 255.3) * mm});
            skArc(sketch, "E18.9.7.5", {"start": v(175.5, 239.49) * mm, "mid": v(176.09, 238.07) * mm, "end": v(177.5, 237.49) * mm});
            skLineSegment(sketch, "E18.9.7.6", {"start": v(177.5, 237.49) * mm, "end": v(182.5, 237.49) * mm});
            skArc(sketch, "E18.9.7.7", {"start": v(182.5, 237.49) * mm, "mid": v(183.91, 238.07) * mm, "end": v(184.5, 239.49) * mm});
            skLineSegment(sketch, "E18.9.8.0", {"start": v(175.5, 204.85) * mm, "end": v(175.5, 220.67) * mm});
            skLineSegment(sketch, "E18.9.8.1", {"start": v(184.5, 204.85) * mm, "end": v(184.5, 220.67) * mm});
            skPoint(sketch, "E18.9.8.2", {"position": v(184.5, 202.85) * mm});
            skPoint(sketch, "E18.9.8.3", {"position": v(175.5, 202.85) * mm});
            skLineSegment(sketch, "E18.9.8.4", {"start": v(175.5, 220.67) * mm, "end": v(184.5, 220.67) * mm});
            skArc(sketch, "E18.9.8.5", {"start": v(175.5, 204.85) * mm, "mid": v(176.09, 203.43) * mm, "end": v(177.5, 202.85) * mm});
            skLineSegment(sketch, "E18.9.8.6", {"start": v(177.5, 202.85) * mm, "end": v(182.5, 202.85) * mm});
            skArc(sketch, "E18.9.8.7", {"start": v(182.5, 202.85) * mm, "mid": v(183.91, 203.43) * mm, "end": v(184.5, 204.85) * mm});
            skLineSegment(sketch, "E18.9.9.0", {"start": v(175.5, 170.2) * mm, "end": v(175.5, 186.03) * mm});
            skLineSegment(sketch, "E18.9.9.1", {"start": v(184.5, 170.2) * mm, "end": v(184.5, 186.03) * mm});
            skPoint(sketch, "E18.9.9.2", {"position": v(184.5, 168.2) * mm});
            skPoint(sketch, "E18.9.9.3", {"position": v(175.5, 168.2) * mm});
            skLineSegment(sketch, "E18.9.9.4", {"start": v(175.5, 186.03) * mm, "end": v(184.5, 186.03) * mm});
            skArc(sketch, "E18.9.9.5", {"start": v(175.5, 170.2) * mm, "mid": v(176.09, 168.8) * mm, "end": v(177.5, 168.2) * mm});
            skLineSegment(sketch, "E18.9.9.6", {"start": v(177.5, 168.2) * mm, "end": v(182.5, 168.2) * mm});
            skArc(sketch, "E18.9.9.7", {"start": v(182.5, 168.2) * mm, "mid": v(183.91, 168.8) * mm, "end": v(184.5, 170.2) * mm});
            skLineSegment(sketch, "E18.9.10.0", {"start": v(175.5, 135.56) * mm, "end": v(175.5, 151.38) * mm});
            skLineSegment(sketch, "E18.9.10.1", {"start": v(184.5, 135.56) * mm, "end": v(184.5, 151.38) * mm});
            skPoint(sketch, "E18.9.10.2", {"position": v(184.5, 133.56) * mm});
            skPoint(sketch, "E18.9.10.3", {"position": v(175.5, 133.56) * mm});
            skLineSegment(sketch, "E18.9.10.4", {"start": v(175.5, 151.38) * mm, "end": v(184.5, 151.38) * mm});
            skArc(sketch, "E18.9.10.5", {"start": v(175.5, 135.56) * mm, "mid": v(176.09, 134.15) * mm, "end": v(177.5, 133.56) * mm});
            skLineSegment(sketch, "E18.9.10.6", {"start": v(177.5, 133.56) * mm, "end": v(182.5, 133.56) * mm});
            skArc(sketch, "E18.9.10.7", {"start": v(182.5, 133.56) * mm, "mid": v(183.91, 134.15) * mm, "end": v(184.5, 135.56) * mm});
            skLineSegment(sketch, "E18.9.11.0", {"start": v(175.5, 100.92) * mm, "end": v(175.5, 116.74) * mm});
            skLineSegment(sketch, "E18.9.11.1", {"start": v(184.5, 100.92) * mm, "end": v(184.5, 116.74) * mm});
            skPoint(sketch, "E18.9.11.2", {"position": v(184.5, 98.92) * mm});
            skPoint(sketch, "E18.9.11.3", {"position": v(175.5, 98.92) * mm});
            skLineSegment(sketch, "E18.9.11.4", {"start": v(175.5, 116.74) * mm, "end": v(184.5, 116.74) * mm});
            skArc(sketch, "E18.9.11.5", {"start": v(175.5, 100.92) * mm, "mid": v(176.09, 99.5) * mm, "end": v(177.5, 98.92) * mm});
            skLineSegment(sketch, "E18.9.11.6", {"start": v(177.5, 98.92) * mm, "end": v(182.5, 98.92) * mm});
            skArc(sketch, "E18.9.11.7", {"start": v(182.5, 98.92) * mm, "mid": v(183.91, 99.5) * mm, "end": v(184.5, 100.92) * mm});
            skLineSegment(sketch, "E18.9.12.0", {"start": v(175.5, 66.28) * mm, "end": v(175.5, 82.1) * mm});
            skLineSegment(sketch, "E18.9.12.1", {"start": v(184.5, 66.28) * mm, "end": v(184.5, 82.1) * mm});
            skPoint(sketch, "E18.9.12.2", {"position": v(184.5, 64.28) * mm});
            skPoint(sketch, "E18.9.12.3", {"position": v(175.5, 64.28) * mm});
            skLineSegment(sketch, "E18.9.12.4", {"start": v(175.5, 82.1) * mm, "end": v(184.5, 82.1) * mm});
            skArc(sketch, "E18.9.12.5", {"start": v(175.5, 66.28) * mm, "mid": v(176.09, 64.87) * mm, "end": v(177.5, 64.28) * mm});
            skLineSegment(sketch, "E18.9.12.6", {"start": v(177.5, 64.28) * mm, "end": v(182.5, 64.28) * mm});
            skArc(sketch, "E18.9.12.7", {"start": v(182.5, 64.28) * mm, "mid": v(183.91, 64.87) * mm, "end": v(184.5, 66.28) * mm});
            skLineSegment(sketch, "E18.9.13.0", {"start": v(175.5, 31.64) * mm, "end": v(175.5, 47.46) * mm});
            skLineSegment(sketch, "E18.9.13.1", {"start": v(184.5, 31.64) * mm, "end": v(184.5, 47.46) * mm});
            skPoint(sketch, "E18.9.13.2", {"position": v(184.5, 29.64) * mm});
            skPoint(sketch, "E18.9.13.3", {"position": v(175.5, 29.64) * mm});
            skLineSegment(sketch, "E18.9.13.4", {"start": v(175.5, 47.46) * mm, "end": v(184.5, 47.46) * mm});
            skArc(sketch, "E18.9.13.5", {"start": v(175.5, 31.64) * mm, "mid": v(176.09, 30.23) * mm, "end": v(177.5, 29.64) * mm});
            skLineSegment(sketch, "E18.9.13.6", {"start": v(177.5, 29.64) * mm, "end": v(182.5, 29.64) * mm});
            skArc(sketch, "E18.9.13.7", {"start": v(182.5, 29.64) * mm, "mid": v(183.91, 30.23) * mm, "end": v(184.5, 31.64) * mm});
            skLineSegment(sketch, "E18.9.14.0", {"start": v(175.5, -3) * mm, "end": v(175.5, 12.82) * mm});
            skLineSegment(sketch, "E18.9.14.1", {"start": v(184.5, -3) * mm, "end": v(184.5, 12.82) * mm});
            skPoint(sketch, "E18.9.14.2", {"position": v(184.5, -5) * mm});
            skPoint(sketch, "E18.9.14.3", {"position": v(175.5, -5) * mm});
            skLineSegment(sketch, "E18.9.14.4", {"start": v(175.5, 12.82) * mm, "end": v(184.5, 12.82) * mm});
            skArc(sketch, "E18.9.14.5", {"start": v(175.5, -3) * mm, "mid": v(176.09, -4.41) * mm, "end": v(177.5, -5) * mm});
            skLineSegment(sketch, "E18.9.14.6", {"start": v(177.5, -5) * mm, "end": v(182.5, -5) * mm});
            skArc(sketch, "E18.9.14.7", {"start": v(182.5, -5) * mm, "mid": v(183.91, -4.41) * mm, "end": v(184.5, -3) * mm});
            skLineSegment(sketch, "E18.10.0.0", {"start": v(195.5, 481.97) * mm, "end": v(195.5, 497.8) * mm});
            skLineSegment(sketch, "E18.10.0.1", {"start": v(204.5, 481.97) * mm, "end": v(204.5, 497.8) * mm});
            skPoint(sketch, "E18.10.0.2", {"position": v(204.5, 479.97) * mm});
            skPoint(sketch, "E18.10.0.3", {"position": v(195.5, 479.97) * mm});
            skLineSegment(sketch, "E18.10.0.4", {"start": v(195.5, 497.8) * mm, "end": v(204.5, 497.8) * mm});
            skArc(sketch, "E18.10.0.5", {"start": v(195.5, 481.97) * mm, "mid": v(196.09, 480.56) * mm, "end": v(197.5, 479.97) * mm});
            skLineSegment(sketch, "E18.10.0.6", {"start": v(197.5, 479.97) * mm, "end": v(202.5, 479.97) * mm});
            skArc(sketch, "E18.10.0.7", {"start": v(202.5, 479.97) * mm, "mid": v(203.91, 480.56) * mm, "end": v(204.5, 481.97) * mm});
            skLineSegment(sketch, "E18.10.1.0", {"start": v(195.5, 447.33) * mm, "end": v(195.5, 463.15) * mm});
            skLineSegment(sketch, "E18.10.1.1", {"start": v(204.5, 447.33) * mm, "end": v(204.5, 463.15) * mm});
            skPoint(sketch, "E18.10.1.2", {"position": v(204.5, 445.33) * mm});
            skPoint(sketch, "E18.10.1.3", {"position": v(195.5, 445.33) * mm});
            skLineSegment(sketch, "E18.10.1.4", {"start": v(195.5, 463.15) * mm, "end": v(204.5, 463.15) * mm});
            skArc(sketch, "E18.10.1.5", {"start": v(195.5, 447.33) * mm, "mid": v(196.09, 445.92) * mm, "end": v(197.5, 445.33) * mm});
            skLineSegment(sketch, "E18.10.1.6", {"start": v(197.5, 445.33) * mm, "end": v(202.5, 445.33) * mm});
            skArc(sketch, "E18.10.1.7", {"start": v(202.5, 445.33) * mm, "mid": v(203.91, 445.92) * mm, "end": v(204.5, 447.33) * mm});
            skLineSegment(sketch, "E18.10.2.0", {"start": v(195.5, 412.7) * mm, "end": v(195.5, 428.51) * mm});
            skLineSegment(sketch, "E18.10.2.1", {"start": v(204.5, 412.7) * mm, "end": v(204.5, 428.51) * mm});
            skPoint(sketch, "E18.10.2.2", {"position": v(204.5, 410.7) * mm});
            skPoint(sketch, "E18.10.2.3", {"position": v(195.5, 410.7) * mm});
            skLineSegment(sketch, "E18.10.2.4", {"start": v(195.5, 428.51) * mm, "end": v(204.5, 428.51) * mm});
            skArc(sketch, "E18.10.2.5", {"start": v(195.5, 412.7) * mm, "mid": v(196.09, 411.28) * mm, "end": v(197.5, 410.7) * mm});
            skLineSegment(sketch, "E18.10.2.6", {"start": v(197.5, 410.7) * mm, "end": v(202.5, 410.7) * mm});
            skArc(sketch, "E18.10.2.7", {"start": v(202.5, 410.7) * mm, "mid": v(203.91, 411.28) * mm, "end": v(204.5, 412.7) * mm});
            skLineSegment(sketch, "E18.10.3.0", {"start": v(195.5, 378.05) * mm, "end": v(195.5, 393.87) * mm});
            skLineSegment(sketch, "E18.10.3.1", {"start": v(204.5, 378.05) * mm, "end": v(204.5, 393.87) * mm});
            skPoint(sketch, "E18.10.3.2", {"position": v(204.5, 376.05) * mm});
            skPoint(sketch, "E18.10.3.3", {"position": v(195.5, 376.05) * mm});
            skLineSegment(sketch, "E18.10.3.4", {"start": v(195.5, 393.87) * mm, "end": v(204.5, 393.87) * mm});
            skArc(sketch, "E18.10.3.5", {"start": v(195.5, 378.05) * mm, "mid": v(196.09, 376.64) * mm, "end": v(197.5, 376.05) * mm});
            skLineSegment(sketch, "E18.10.3.6", {"start": v(197.5, 376.05) * mm, "end": v(202.5, 376.05) * mm});
            skArc(sketch, "E18.10.3.7", {"start": v(202.5, 376.05) * mm, "mid": v(203.91, 376.64) * mm, "end": v(204.5, 378.05) * mm});
            skLineSegment(sketch, "E18.10.4.0", {"start": v(195.5, 343.41) * mm, "end": v(195.5, 359.23) * mm});
            skLineSegment(sketch, "E18.10.4.1", {"start": v(204.5, 343.41) * mm, "end": v(204.5, 359.23) * mm});
            skPoint(sketch, "E18.10.4.2", {"position": v(204.5, 341.41) * mm});
            skPoint(sketch, "E18.10.4.3", {"position": v(195.5, 341.41) * mm});
            skLineSegment(sketch, "E18.10.4.4", {"start": v(195.5, 359.23) * mm, "end": v(204.5, 359.23) * mm});
            skArc(sketch, "E18.10.4.5", {"start": v(195.5, 343.41) * mm, "mid": v(196.09, 342) * mm, "end": v(197.5, 341.41) * mm});
            skLineSegment(sketch, "E18.10.4.6", {"start": v(197.5, 341.41) * mm, "end": v(202.5, 341.41) * mm});
            skArc(sketch, "E18.10.4.7", {"start": v(202.5, 341.41) * mm, "mid": v(203.91, 342) * mm, "end": v(204.5, 343.41) * mm});
            skLineSegment(sketch, "E18.10.5.0", {"start": v(195.5, 308.77) * mm, "end": v(195.5, 324.59) * mm});
            skLineSegment(sketch, "E18.10.5.1", {"start": v(204.5, 308.77) * mm, "end": v(204.5, 324.59) * mm});
            skPoint(sketch, "E18.10.5.2", {"position": v(204.5, 306.77) * mm});
            skPoint(sketch, "E18.10.5.3", {"position": v(195.5, 306.77) * mm});
            skLineSegment(sketch, "E18.10.5.4", {"start": v(195.5, 324.59) * mm, "end": v(204.5, 324.59) * mm});
            skArc(sketch, "E18.10.5.5", {"start": v(195.5, 308.77) * mm, "mid": v(196.09, 307.35) * mm, "end": v(197.5, 306.77) * mm});
            skLineSegment(sketch, "E18.10.5.6", {"start": v(197.5, 306.77) * mm, "end": v(202.5, 306.77) * mm});
            skArc(sketch, "E18.10.5.7", {"start": v(202.5, 306.77) * mm, "mid": v(203.91, 307.35) * mm, "end": v(204.5, 308.77) * mm});
            skLineSegment(sketch, "E18.10.6.0", {"start": v(195.5, 274.13) * mm, "end": v(195.5, 289.95) * mm});
            skLineSegment(sketch, "E18.10.6.1", {"start": v(204.5, 274.13) * mm, "end": v(204.5, 289.95) * mm});
            skPoint(sketch, "E18.10.6.2", {"position": v(204.5, 272.13) * mm});
            skPoint(sketch, "E18.10.6.3", {"position": v(195.5, 272.13) * mm});
            skLineSegment(sketch, "E18.10.6.4", {"start": v(195.5, 289.95) * mm, "end": v(204.5, 289.95) * mm});
            skArc(sketch, "E18.10.6.5", {"start": v(195.5, 274.13) * mm, "mid": v(196.09, 272.71) * mm, "end": v(197.5, 272.13) * mm});
            skLineSegment(sketch, "E18.10.6.6", {"start": v(197.5, 272.13) * mm, "end": v(202.5, 272.13) * mm});
            skArc(sketch, "E18.10.6.7", {"start": v(202.5, 272.13) * mm, "mid": v(203.91, 272.71) * mm, "end": v(204.5, 274.13) * mm});
            skLineSegment(sketch, "E18.10.7.0", {"start": v(195.5, 239.49) * mm, "end": v(195.5, 255.3) * mm});
            skLineSegment(sketch, "E18.10.7.1", {"start": v(204.5, 239.49) * mm, "end": v(204.5, 255.3) * mm});
            skPoint(sketch, "E18.10.7.2", {"position": v(204.5, 237.49) * mm});
            skPoint(sketch, "E18.10.7.3", {"position": v(195.5, 237.49) * mm});
            skLineSegment(sketch, "E18.10.7.4", {"start": v(195.5, 255.3) * mm, "end": v(204.5, 255.3) * mm});
            skArc(sketch, "E18.10.7.5", {"start": v(195.5, 239.49) * mm, "mid": v(196.09, 238.07) * mm, "end": v(197.5, 237.49) * mm});
            skLineSegment(sketch, "E18.10.7.6", {"start": v(197.5, 237.49) * mm, "end": v(202.5, 237.49) * mm});
            skArc(sketch, "E18.10.7.7", {"start": v(202.5, 237.49) * mm, "mid": v(203.91, 238.07) * mm, "end": v(204.5, 239.49) * mm});
            skLineSegment(sketch, "E18.10.8.0", {"start": v(195.5, 204.85) * mm, "end": v(195.5, 220.67) * mm});
            skLineSegment(sketch, "E18.10.8.1", {"start": v(204.5, 204.85) * mm, "end": v(204.5, 220.67) * mm});
            skPoint(sketch, "E18.10.8.2", {"position": v(204.5, 202.85) * mm});
            skPoint(sketch, "E18.10.8.3", {"position": v(195.5, 202.85) * mm});
            skLineSegment(sketch, "E18.10.8.4", {"start": v(195.5, 220.67) * mm, "end": v(204.5, 220.67) * mm});
            skArc(sketch, "E18.10.8.5", {"start": v(195.5, 204.85) * mm, "mid": v(196.09, 203.43) * mm, "end": v(197.5, 202.85) * mm});
            skLineSegment(sketch, "E18.10.8.6", {"start": v(197.5, 202.85) * mm, "end": v(202.5, 202.85) * mm});
            skArc(sketch, "E18.10.8.7", {"start": v(202.5, 202.85) * mm, "mid": v(203.91, 203.43) * mm, "end": v(204.5, 204.85) * mm});
            skLineSegment(sketch, "E18.10.9.0", {"start": v(195.5, 170.2) * mm, "end": v(195.5, 186.03) * mm});
            skLineSegment(sketch, "E18.10.9.1", {"start": v(204.5, 170.2) * mm, "end": v(204.5, 186.03) * mm});
            skPoint(sketch, "E18.10.9.2", {"position": v(204.5, 168.2) * mm});
            skPoint(sketch, "E18.10.9.3", {"position": v(195.5, 168.2) * mm});
            skLineSegment(sketch, "E18.10.9.4", {"start": v(195.5, 186.03) * mm, "end": v(204.5, 186.03) * mm});
            skArc(sketch, "E18.10.9.5", {"start": v(195.5, 170.2) * mm, "mid": v(196.09, 168.8) * mm, "end": v(197.5, 168.2) * mm});
            skLineSegment(sketch, "E18.10.9.6", {"start": v(197.5, 168.2) * mm, "end": v(202.5, 168.2) * mm});
            skArc(sketch, "E18.10.9.7", {"start": v(202.5, 168.2) * mm, "mid": v(203.91, 168.8) * mm, "end": v(204.5, 170.2) * mm});
            skLineSegment(sketch, "E18.10.10.0", {"start": v(195.5, 135.56) * mm, "end": v(195.5, 151.38) * mm});
            skLineSegment(sketch, "E18.10.10.1", {"start": v(204.5, 135.56) * mm, "end": v(204.5, 151.38) * mm});
            skPoint(sketch, "E18.10.10.2", {"position": v(204.5, 133.56) * mm});
            skPoint(sketch, "E18.10.10.3", {"position": v(195.5, 133.56) * mm});
            skLineSegment(sketch, "E18.10.10.4", {"start": v(195.5, 151.38) * mm, "end": v(204.5, 151.38) * mm});
            skArc(sketch, "E18.10.10.5", {"start": v(195.5, 135.56) * mm, "mid": v(196.09, 134.15) * mm, "end": v(197.5, 133.56) * mm});
            skLineSegment(sketch, "E18.10.10.6", {"start": v(197.5, 133.56) * mm, "end": v(202.5, 133.56) * mm});
            skArc(sketch, "E18.10.10.7", {"start": v(202.5, 133.56) * mm, "mid": v(203.91, 134.15) * mm, "end": v(204.5, 135.56) * mm});
            skLineSegment(sketch, "E18.10.11.0", {"start": v(195.5, 100.92) * mm, "end": v(195.5, 116.74) * mm});
            skLineSegment(sketch, "E18.10.11.1", {"start": v(204.5, 100.92) * mm, "end": v(204.5, 116.74) * mm});
            skPoint(sketch, "E18.10.11.2", {"position": v(204.5, 98.92) * mm});
            skPoint(sketch, "E18.10.11.3", {"position": v(195.5, 98.92) * mm});
            skLineSegment(sketch, "E18.10.11.4", {"start": v(195.5, 116.74) * mm, "end": v(204.5, 116.74) * mm});
            skArc(sketch, "E18.10.11.5", {"start": v(195.5, 100.92) * mm, "mid": v(196.09, 99.5) * mm, "end": v(197.5, 98.92) * mm});
            skLineSegment(sketch, "E18.10.11.6", {"start": v(197.5, 98.92) * mm, "end": v(202.5, 98.92) * mm});
            skArc(sketch, "E18.10.11.7", {"start": v(202.5, 98.92) * mm, "mid": v(203.91, 99.5) * mm, "end": v(204.5, 100.92) * mm});
            skLineSegment(sketch, "E18.10.12.0", {"start": v(195.5, 66.28) * mm, "end": v(195.5, 82.1) * mm});
            skLineSegment(sketch, "E18.10.12.1", {"start": v(204.5, 66.28) * mm, "end": v(204.5, 82.1) * mm});
            skPoint(sketch, "E18.10.12.2", {"position": v(204.5, 64.28) * mm});
            skPoint(sketch, "E18.10.12.3", {"position": v(195.5, 64.28) * mm});
            skLineSegment(sketch, "E18.10.12.4", {"start": v(195.5, 82.1) * mm, "end": v(204.5, 82.1) * mm});
            skArc(sketch, "E18.10.12.5", {"start": v(195.5, 66.28) * mm, "mid": v(196.09, 64.87) * mm, "end": v(197.5, 64.28) * mm});
            skLineSegment(sketch, "E18.10.12.6", {"start": v(197.5, 64.28) * mm, "end": v(202.5, 64.28) * mm});
            skArc(sketch, "E18.10.12.7", {"start": v(202.5, 64.28) * mm, "mid": v(203.91, 64.87) * mm, "end": v(204.5, 66.28) * mm});
            skLineSegment(sketch, "E18.10.13.0", {"start": v(195.5, 31.64) * mm, "end": v(195.5, 47.46) * mm});
            skLineSegment(sketch, "E18.10.13.1", {"start": v(204.5, 31.64) * mm, "end": v(204.5, 47.46) * mm});
            skPoint(sketch, "E18.10.13.2", {"position": v(204.5, 29.64) * mm});
            skPoint(sketch, "E18.10.13.3", {"position": v(195.5, 29.64) * mm});
            skLineSegment(sketch, "E18.10.13.4", {"start": v(195.5, 47.46) * mm, "end": v(204.5, 47.46) * mm});
            skArc(sketch, "E18.10.13.5", {"start": v(195.5, 31.64) * mm, "mid": v(196.09, 30.23) * mm, "end": v(197.5, 29.64) * mm});
            skLineSegment(sketch, "E18.10.13.6", {"start": v(197.5, 29.64) * mm, "end": v(202.5, 29.64) * mm});
            skArc(sketch, "E18.10.13.7", {"start": v(202.5, 29.64) * mm, "mid": v(203.91, 30.23) * mm, "end": v(204.5, 31.64) * mm});
            skLineSegment(sketch, "E18.10.14.0", {"start": v(195.5, -3) * mm, "end": v(195.5, 12.82) * mm});
            skLineSegment(sketch, "E18.10.14.1", {"start": v(204.5, -3) * mm, "end": v(204.5, 12.82) * mm});
            skPoint(sketch, "E18.10.14.2", {"position": v(204.5, -5) * mm});
            skPoint(sketch, "E18.10.14.3", {"position": v(195.5, -5) * mm});
            skLineSegment(sketch, "E18.10.14.4", {"start": v(195.5, 12.82) * mm, "end": v(204.5, 12.82) * mm});
            skArc(sketch, "E18.10.14.5", {"start": v(195.5, -3) * mm, "mid": v(196.09, -4.41) * mm, "end": v(197.5, -5) * mm});
            skLineSegment(sketch, "E18.10.14.6", {"start": v(197.5, -5) * mm, "end": v(202.5, -5) * mm});
            skArc(sketch, "E18.10.14.7", {"start": v(202.5, -5) * mm, "mid": v(203.91, -4.41) * mm, "end": v(204.5, -3) * mm});
            skLineSegment(sketch, "E18.11.0.0", {"start": v(215.5, 481.97) * mm, "end": v(215.5, 497.8) * mm});
            skLineSegment(sketch, "E18.11.0.1", {"start": v(224.5, 481.97) * mm, "end": v(224.5, 497.8) * mm});
            skPoint(sketch, "E18.11.0.2", {"position": v(224.5, 479.97) * mm});
            skPoint(sketch, "E18.11.0.3", {"position": v(215.5, 479.97) * mm});
            skLineSegment(sketch, "E18.11.0.4", {"start": v(215.5, 497.8) * mm, "end": v(224.5, 497.8) * mm});
            skArc(sketch, "E18.11.0.5", {"start": v(215.5, 481.97) * mm, "mid": v(216.09, 480.56) * mm, "end": v(217.5, 479.97) * mm});
            skLineSegment(sketch, "E18.11.0.6", {"start": v(217.5, 479.97) * mm, "end": v(222.5, 479.97) * mm});
            skArc(sketch, "E18.11.0.7", {"start": v(222.5, 479.97) * mm, "mid": v(223.91, 480.56) * mm, "end": v(224.5, 481.97) * mm});
            skLineSegment(sketch, "E18.11.1.0", {"start": v(215.5, 447.33) * mm, "end": v(215.5, 463.15) * mm});
            skLineSegment(sketch, "E18.11.1.1", {"start": v(224.5, 447.33) * mm, "end": v(224.5, 463.15) * mm});
            skPoint(sketch, "E18.11.1.2", {"position": v(224.5, 445.33) * mm});
            skPoint(sketch, "E18.11.1.3", {"position": v(215.5, 445.33) * mm});
            skLineSegment(sketch, "E18.11.1.4", {"start": v(215.5, 463.15) * mm, "end": v(224.5, 463.15) * mm});
            skArc(sketch, "E18.11.1.5", {"start": v(215.5, 447.33) * mm, "mid": v(216.09, 445.92) * mm, "end": v(217.5, 445.33) * mm});
            skLineSegment(sketch, "E18.11.1.6", {"start": v(217.5, 445.33) * mm, "end": v(222.5, 445.33) * mm});
            skArc(sketch, "E18.11.1.7", {"start": v(222.5, 445.33) * mm, "mid": v(223.91, 445.92) * mm, "end": v(224.5, 447.33) * mm});
            skLineSegment(sketch, "E18.11.2.0", {"start": v(215.5, 412.7) * mm, "end": v(215.5, 428.51) * mm});
            skLineSegment(sketch, "E18.11.2.1", {"start": v(224.5, 412.7) * mm, "end": v(224.5, 428.51) * mm});
            skPoint(sketch, "E18.11.2.2", {"position": v(224.5, 410.7) * mm});
            skPoint(sketch, "E18.11.2.3", {"position": v(215.5, 410.7) * mm});
            skLineSegment(sketch, "E18.11.2.4", {"start": v(215.5, 428.51) * mm, "end": v(224.5, 428.51) * mm});
            skArc(sketch, "E18.11.2.5", {"start": v(215.5, 412.7) * mm, "mid": v(216.09, 411.28) * mm, "end": v(217.5, 410.7) * mm});
            skLineSegment(sketch, "E18.11.2.6", {"start": v(217.5, 410.7) * mm, "end": v(222.5, 410.7) * mm});
            skArc(sketch, "E18.11.2.7", {"start": v(222.5, 410.7) * mm, "mid": v(223.91, 411.28) * mm, "end": v(224.5, 412.7) * mm});
            skLineSegment(sketch, "E18.11.3.0", {"start": v(215.5, 378.05) * mm, "end": v(215.5, 393.87) * mm});
            skLineSegment(sketch, "E18.11.3.1", {"start": v(224.5, 378.05) * mm, "end": v(224.5, 393.87) * mm});
            skPoint(sketch, "E18.11.3.2", {"position": v(224.5, 376.05) * mm});
            skPoint(sketch, "E18.11.3.3", {"position": v(215.5, 376.05) * mm});
            skLineSegment(sketch, "E18.11.3.4", {"start": v(215.5, 393.87) * mm, "end": v(224.5, 393.87) * mm});
            skArc(sketch, "E18.11.3.5", {"start": v(215.5, 378.05) * mm, "mid": v(216.09, 376.64) * mm, "end": v(217.5, 376.05) * mm});
            skLineSegment(sketch, "E18.11.3.6", {"start": v(217.5, 376.05) * mm, "end": v(222.5, 376.05) * mm});
            skArc(sketch, "E18.11.3.7", {"start": v(222.5, 376.05) * mm, "mid": v(223.91, 376.64) * mm, "end": v(224.5, 378.05) * mm});
            skLineSegment(sketch, "E18.11.4.0", {"start": v(215.5, 343.41) * mm, "end": v(215.5, 359.23) * mm});
            skLineSegment(sketch, "E18.11.4.1", {"start": v(224.5, 343.41) * mm, "end": v(224.5, 359.23) * mm});
            skPoint(sketch, "E18.11.4.2", {"position": v(224.5, 341.41) * mm});
            skPoint(sketch, "E18.11.4.3", {"position": v(215.5, 341.41) * mm});
            skLineSegment(sketch, "E18.11.4.4", {"start": v(215.5, 359.23) * mm, "end": v(224.5, 359.23) * mm});
            skArc(sketch, "E18.11.4.5", {"start": v(215.5, 343.41) * mm, "mid": v(216.09, 342) * mm, "end": v(217.5, 341.41) * mm});
            skLineSegment(sketch, "E18.11.4.6", {"start": v(217.5, 341.41) * mm, "end": v(222.5, 341.41) * mm});
            skArc(sketch, "E18.11.4.7", {"start": v(222.5, 341.41) * mm, "mid": v(223.91, 342) * mm, "end": v(224.5, 343.41) * mm});
            skLineSegment(sketch, "E18.11.5.0", {"start": v(215.5, 308.77) * mm, "end": v(215.5, 324.59) * mm});
            skLineSegment(sketch, "E18.11.5.1", {"start": v(224.5, 308.77) * mm, "end": v(224.5, 324.59) * mm});
            skPoint(sketch, "E18.11.5.2", {"position": v(224.5, 306.77) * mm});
            skPoint(sketch, "E18.11.5.3", {"position": v(215.5, 306.77) * mm});
            skLineSegment(sketch, "E18.11.5.4", {"start": v(215.5, 324.59) * mm, "end": v(224.5, 324.59) * mm});
            skArc(sketch, "E18.11.5.5", {"start": v(215.5, 308.77) * mm, "mid": v(216.09, 307.35) * mm, "end": v(217.5, 306.77) * mm});
            skLineSegment(sketch, "E18.11.5.6", {"start": v(217.5, 306.77) * mm, "end": v(222.5, 306.77) * mm});
            skArc(sketch, "E18.11.5.7", {"start": v(222.5, 306.77) * mm, "mid": v(223.91, 307.35) * mm, "end": v(224.5, 308.77) * mm});
            skLineSegment(sketch, "E18.11.6.0", {"start": v(215.5, 274.13) * mm, "end": v(215.5, 289.95) * mm});
            skLineSegment(sketch, "E18.11.6.1", {"start": v(224.5, 274.13) * mm, "end": v(224.5, 289.95) * mm});
            skPoint(sketch, "E18.11.6.2", {"position": v(224.5, 272.13) * mm});
            skPoint(sketch, "E18.11.6.3", {"position": v(215.5, 272.13) * mm});
            skLineSegment(sketch, "E18.11.6.4", {"start": v(215.5, 289.95) * mm, "end": v(224.5, 289.95) * mm});
            skArc(sketch, "E18.11.6.5", {"start": v(215.5, 274.13) * mm, "mid": v(216.09, 272.71) * mm, "end": v(217.5, 272.13) * mm});
            skLineSegment(sketch, "E18.11.6.6", {"start": v(217.5, 272.13) * mm, "end": v(222.5, 272.13) * mm});
            skArc(sketch, "E18.11.6.7", {"start": v(222.5, 272.13) * mm, "mid": v(223.91, 272.71) * mm, "end": v(224.5, 274.13) * mm});
            skLineSegment(sketch, "E18.11.7.0", {"start": v(215.5, 239.49) * mm, "end": v(215.5, 255.3) * mm});
            skLineSegment(sketch, "E18.11.7.1", {"start": v(224.5, 239.49) * mm, "end": v(224.5, 255.3) * mm});
            skPoint(sketch, "E18.11.7.2", {"position": v(224.5, 237.49) * mm});
            skPoint(sketch, "E18.11.7.3", {"position": v(215.5, 237.49) * mm});
            skLineSegment(sketch, "E18.11.7.4", {"start": v(215.5, 255.3) * mm, "end": v(224.5, 255.3) * mm});
            skArc(sketch, "E18.11.7.5", {"start": v(215.5, 239.49) * mm, "mid": v(216.09, 238.07) * mm, "end": v(217.5, 237.49) * mm});
            skLineSegment(sketch, "E18.11.7.6", {"start": v(217.5, 237.49) * mm, "end": v(222.5, 237.49) * mm});
            skArc(sketch, "E18.11.7.7", {"start": v(222.5, 237.49) * mm, "mid": v(223.91, 238.07) * mm, "end": v(224.5, 239.49) * mm});
            skLineSegment(sketch, "E18.11.8.0", {"start": v(215.5, 204.85) * mm, "end": v(215.5, 220.67) * mm});
            skLineSegment(sketch, "E18.11.8.1", {"start": v(224.5, 204.85) * mm, "end": v(224.5, 220.67) * mm});
            skPoint(sketch, "E18.11.8.2", {"position": v(224.5, 202.85) * mm});
            skPoint(sketch, "E18.11.8.3", {"position": v(215.5, 202.85) * mm});
            skLineSegment(sketch, "E18.11.8.4", {"start": v(215.5, 220.67) * mm, "end": v(224.5, 220.67) * mm});
            skArc(sketch, "E18.11.8.5", {"start": v(215.5, 204.85) * mm, "mid": v(216.09, 203.43) * mm, "end": v(217.5, 202.85) * mm});
            skLineSegment(sketch, "E18.11.8.6", {"start": v(217.5, 202.85) * mm, "end": v(222.5, 202.85) * mm});
            skArc(sketch, "E18.11.8.7", {"start": v(222.5, 202.85) * mm, "mid": v(223.91, 203.43) * mm, "end": v(224.5, 204.85) * mm});
            skLineSegment(sketch, "E18.11.9.0", {"start": v(215.5, 170.2) * mm, "end": v(215.5, 186.03) * mm});
            skLineSegment(sketch, "E18.11.9.1", {"start": v(224.5, 170.2) * mm, "end": v(224.5, 186.03) * mm});
            skPoint(sketch, "E18.11.9.2", {"position": v(224.5, 168.2) * mm});
            skPoint(sketch, "E18.11.9.3", {"position": v(215.5, 168.2) * mm});
            skLineSegment(sketch, "E18.11.9.4", {"start": v(215.5, 186.03) * mm, "end": v(224.5, 186.03) * mm});
            skArc(sketch, "E18.11.9.5", {"start": v(215.5, 170.2) * mm, "mid": v(216.09, 168.8) * mm, "end": v(217.5, 168.2) * mm});
            skLineSegment(sketch, "E18.11.9.6", {"start": v(217.5, 168.2) * mm, "end": v(222.5, 168.2) * mm});
            skArc(sketch, "E18.11.9.7", {"start": v(222.5, 168.2) * mm, "mid": v(223.91, 168.8) * mm, "end": v(224.5, 170.2) * mm});
            skLineSegment(sketch, "E18.11.10.0", {"start": v(215.5, 135.56) * mm, "end": v(215.5, 151.38) * mm});
            skLineSegment(sketch, "E18.11.10.1", {"start": v(224.5, 135.56) * mm, "end": v(224.5, 151.38) * mm});
            skPoint(sketch, "E18.11.10.2", {"position": v(224.5, 133.56) * mm});
            skPoint(sketch, "E18.11.10.3", {"position": v(215.5, 133.56) * mm});
            skLineSegment(sketch, "E18.11.10.4", {"start": v(215.5, 151.38) * mm, "end": v(224.5, 151.38) * mm});
            skArc(sketch, "E18.11.10.5", {"start": v(215.5, 135.56) * mm, "mid": v(216.09, 134.15) * mm, "end": v(217.5, 133.56) * mm});
            skLineSegment(sketch, "E18.11.10.6", {"start": v(217.5, 133.56) * mm, "end": v(222.5, 133.56) * mm});
            skArc(sketch, "E18.11.10.7", {"start": v(222.5, 133.56) * mm, "mid": v(223.91, 134.15) * mm, "end": v(224.5, 135.56) * mm});
            skLineSegment(sketch, "E18.11.11.0", {"start": v(215.5, 100.92) * mm, "end": v(215.5, 116.74) * mm});
            skLineSegment(sketch, "E18.11.11.1", {"start": v(224.5, 100.92) * mm, "end": v(224.5, 116.74) * mm});
            skPoint(sketch, "E18.11.11.2", {"position": v(224.5, 98.92) * mm});
            skPoint(sketch, "E18.11.11.3", {"position": v(215.5, 98.92) * mm});
            skLineSegment(sketch, "E18.11.11.4", {"start": v(215.5, 116.74) * mm, "end": v(224.5, 116.74) * mm});
            skArc(sketch, "E18.11.11.5", {"start": v(215.5, 100.92) * mm, "mid": v(216.09, 99.5) * mm, "end": v(217.5, 98.92) * mm});
            skLineSegment(sketch, "E18.11.11.6", {"start": v(217.5, 98.92) * mm, "end": v(222.5, 98.92) * mm});
            skArc(sketch, "E18.11.11.7", {"start": v(222.5, 98.92) * mm, "mid": v(223.91, 99.5) * mm, "end": v(224.5, 100.92) * mm});
            skLineSegment(sketch, "E18.11.12.0", {"start": v(215.5, 66.28) * mm, "end": v(215.5, 82.1) * mm});
            skLineSegment(sketch, "E18.11.12.1", {"start": v(224.5, 66.28) * mm, "end": v(224.5, 82.1) * mm});
            skPoint(sketch, "E18.11.12.2", {"position": v(224.5, 64.28) * mm});
            skPoint(sketch, "E18.11.12.3", {"position": v(215.5, 64.28) * mm});
            skLineSegment(sketch, "E18.11.12.4", {"start": v(215.5, 82.1) * mm, "end": v(224.5, 82.1) * mm});
            skArc(sketch, "E18.11.12.5", {"start": v(215.5, 66.28) * mm, "mid": v(216.09, 64.87) * mm, "end": v(217.5, 64.28) * mm});
            skLineSegment(sketch, "E18.11.12.6", {"start": v(217.5, 64.28) * mm, "end": v(222.5, 64.28) * mm});
            skArc(sketch, "E18.11.12.7", {"start": v(222.5, 64.28) * mm, "mid": v(223.91, 64.87) * mm, "end": v(224.5, 66.28) * mm});
            skLineSegment(sketch, "E18.11.13.0", {"start": v(215.5, 31.64) * mm, "end": v(215.5, 47.46) * mm});
            skLineSegment(sketch, "E18.11.13.1", {"start": v(224.5, 31.64) * mm, "end": v(224.5, 47.46) * mm});
            skPoint(sketch, "E18.11.13.2", {"position": v(224.5, 29.64) * mm});
            skPoint(sketch, "E18.11.13.3", {"position": v(215.5, 29.64) * mm});
            skLineSegment(sketch, "E18.11.13.4", {"start": v(215.5, 47.46) * mm, "end": v(224.5, 47.46) * mm});
            skArc(sketch, "E18.11.13.5", {"start": v(215.5, 31.64) * mm, "mid": v(216.09, 30.23) * mm, "end": v(217.5, 29.64) * mm});
            skLineSegment(sketch, "E18.11.13.6", {"start": v(217.5, 29.64) * mm, "end": v(222.5, 29.64) * mm});
            skArc(sketch, "E18.11.13.7", {"start": v(222.5, 29.64) * mm, "mid": v(223.91, 30.23) * mm, "end": v(224.5, 31.64) * mm});
            skLineSegment(sketch, "E18.11.14.0", {"start": v(215.5, -3) * mm, "end": v(215.5, 12.82) * mm});
            skLineSegment(sketch, "E18.11.14.1", {"start": v(224.5, -3) * mm, "end": v(224.5, 12.82) * mm});
            skPoint(sketch, "E18.11.14.2", {"position": v(224.5, -5) * mm});
            skPoint(sketch, "E18.11.14.3", {"position": v(215.5, -5) * mm});
            skLineSegment(sketch, "E18.11.14.4", {"start": v(215.5, 12.82) * mm, "end": v(224.5, 12.82) * mm});
            skArc(sketch, "E18.11.14.5", {"start": v(215.5, -3) * mm, "mid": v(216.09, -4.41) * mm, "end": v(217.5, -5) * mm});
            skLineSegment(sketch, "E18.11.14.6", {"start": v(217.5, -5) * mm, "end": v(222.5, -5) * mm});
            skArc(sketch, "E18.11.14.7", {"start": v(222.5, -5) * mm, "mid": v(223.91, -4.41) * mm, "end": v(224.5, -3) * mm});
            skLineSegment(sketch, "E18.12.0.0", {"start": v(235.5, 481.97) * mm, "end": v(235.5, 497.8) * mm});
            skLineSegment(sketch, "E18.12.0.1", {"start": v(244.5, 481.97) * mm, "end": v(244.5, 497.8) * mm});
            skPoint(sketch, "E18.12.0.2", {"position": v(244.5, 479.97) * mm});
            skPoint(sketch, "E18.12.0.3", {"position": v(235.5, 479.97) * mm});
            skLineSegment(sketch, "E18.12.0.4", {"start": v(235.5, 497.8) * mm, "end": v(244.5, 497.8) * mm});
            skArc(sketch, "E18.12.0.5", {"start": v(235.5, 481.97) * mm, "mid": v(236.09, 480.56) * mm, "end": v(237.5, 479.97) * mm});
            skLineSegment(sketch, "E18.12.0.6", {"start": v(237.5, 479.97) * mm, "end": v(242.5, 479.97) * mm});
            skArc(sketch, "E18.12.0.7", {"start": v(242.5, 479.97) * mm, "mid": v(243.91, 480.56) * mm, "end": v(244.5, 481.97) * mm});
            skLineSegment(sketch, "E18.12.1.0", {"start": v(235.5, 447.33) * mm, "end": v(235.5, 463.15) * mm});
            skLineSegment(sketch, "E18.12.1.1", {"start": v(244.5, 447.33) * mm, "end": v(244.5, 463.15) * mm});
            skPoint(sketch, "E18.12.1.2", {"position": v(244.5, 445.33) * mm});
            skPoint(sketch, "E18.12.1.3", {"position": v(235.5, 445.33) * mm});
            skLineSegment(sketch, "E18.12.1.4", {"start": v(235.5, 463.15) * mm, "end": v(244.5, 463.15) * mm});
            skArc(sketch, "E18.12.1.5", {"start": v(235.5, 447.33) * mm, "mid": v(236.09, 445.92) * mm, "end": v(237.5, 445.33) * mm});
            skLineSegment(sketch, "E18.12.1.6", {"start": v(237.5, 445.33) * mm, "end": v(242.5, 445.33) * mm});
            skArc(sketch, "E18.12.1.7", {"start": v(242.5, 445.33) * mm, "mid": v(243.91, 445.92) * mm, "end": v(244.5, 447.33) * mm});
            skLineSegment(sketch, "E18.12.2.0", {"start": v(235.5, 412.7) * mm, "end": v(235.5, 428.51) * mm});
            skLineSegment(sketch, "E18.12.2.1", {"start": v(244.5, 412.7) * mm, "end": v(244.5, 428.51) * mm});
            skPoint(sketch, "E18.12.2.2", {"position": v(244.5, 410.7) * mm});
            skPoint(sketch, "E18.12.2.3", {"position": v(235.5, 410.7) * mm});
            skLineSegment(sketch, "E18.12.2.4", {"start": v(235.5, 428.51) * mm, "end": v(244.5, 428.51) * mm});
            skArc(sketch, "E18.12.2.5", {"start": v(235.5, 412.7) * mm, "mid": v(236.09, 411.28) * mm, "end": v(237.5, 410.7) * mm});
            skLineSegment(sketch, "E18.12.2.6", {"start": v(237.5, 410.7) * mm, "end": v(242.5, 410.7) * mm});
            skArc(sketch, "E18.12.2.7", {"start": v(242.5, 410.7) * mm, "mid": v(243.91, 411.28) * mm, "end": v(244.5, 412.7) * mm});
            skLineSegment(sketch, "E18.12.3.0", {"start": v(235.5, 378.05) * mm, "end": v(235.5, 393.87) * mm});
            skLineSegment(sketch, "E18.12.3.1", {"start": v(244.5, 378.05) * mm, "end": v(244.5, 393.87) * mm});
            skPoint(sketch, "E18.12.3.2", {"position": v(244.5, 376.05) * mm});
            skPoint(sketch, "E18.12.3.3", {"position": v(235.5, 376.05) * mm});
            skLineSegment(sketch, "E18.12.3.4", {"start": v(235.5, 393.87) * mm, "end": v(244.5, 393.87) * mm});
            skArc(sketch, "E18.12.3.5", {"start": v(235.5, 378.05) * mm, "mid": v(236.09, 376.64) * mm, "end": v(237.5, 376.05) * mm});
            skLineSegment(sketch, "E18.12.3.6", {"start": v(237.5, 376.05) * mm, "end": v(242.5, 376.05) * mm});
            skArc(sketch, "E18.12.3.7", {"start": v(242.5, 376.05) * mm, "mid": v(243.91, 376.64) * mm, "end": v(244.5, 378.05) * mm});
            skLineSegment(sketch, "E18.12.4.0", {"start": v(235.5, 343.41) * mm, "end": v(235.5, 359.23) * mm});
            skLineSegment(sketch, "E18.12.4.1", {"start": v(244.5, 343.41) * mm, "end": v(244.5, 359.23) * mm});
            skPoint(sketch, "E18.12.4.2", {"position": v(244.5, 341.41) * mm});
            skPoint(sketch, "E18.12.4.3", {"position": v(235.5, 341.41) * mm});
            skLineSegment(sketch, "E18.12.4.4", {"start": v(235.5, 359.23) * mm, "end": v(244.5, 359.23) * mm});
            skArc(sketch, "E18.12.4.5", {"start": v(235.5, 343.41) * mm, "mid": v(236.09, 342) * mm, "end": v(237.5, 341.41) * mm});
            skLineSegment(sketch, "E18.12.4.6", {"start": v(237.5, 341.41) * mm, "end": v(242.5, 341.41) * mm});
            skArc(sketch, "E18.12.4.7", {"start": v(242.5, 341.41) * mm, "mid": v(243.91, 342) * mm, "end": v(244.5, 343.41) * mm});
            skLineSegment(sketch, "E18.12.5.0", {"start": v(235.5, 308.77) * mm, "end": v(235.5, 324.59) * mm});
            skLineSegment(sketch, "E18.12.5.1", {"start": v(244.5, 308.77) * mm, "end": v(244.5, 324.59) * mm});
            skPoint(sketch, "E18.12.5.2", {"position": v(244.5, 306.77) * mm});
            skPoint(sketch, "E18.12.5.3", {"position": v(235.5, 306.77) * mm});
            skLineSegment(sketch, "E18.12.5.4", {"start": v(235.5, 324.59) * mm, "end": v(244.5, 324.59) * mm});
            skArc(sketch, "E18.12.5.5", {"start": v(235.5, 308.77) * mm, "mid": v(236.09, 307.35) * mm, "end": v(237.5, 306.77) * mm});
            skLineSegment(sketch, "E18.12.5.6", {"start": v(237.5, 306.77) * mm, "end": v(242.5, 306.77) * mm});
            skArc(sketch, "E18.12.5.7", {"start": v(242.5, 306.77) * mm, "mid": v(243.91, 307.35) * mm, "end": v(244.5, 308.77) * mm});
            skLineSegment(sketch, "E18.12.6.0", {"start": v(235.5, 274.13) * mm, "end": v(235.5, 289.95) * mm});
            skLineSegment(sketch, "E18.12.6.1", {"start": v(244.5, 274.13) * mm, "end": v(244.5, 289.95) * mm});
            skPoint(sketch, "E18.12.6.2", {"position": v(244.5, 272.13) * mm});
            skPoint(sketch, "E18.12.6.3", {"position": v(235.5, 272.13) * mm});
            skLineSegment(sketch, "E18.12.6.4", {"start": v(235.5, 289.95) * mm, "end": v(244.5, 289.95) * mm});
            skArc(sketch, "E18.12.6.5", {"start": v(235.5, 274.13) * mm, "mid": v(236.09, 272.71) * mm, "end": v(237.5, 272.13) * mm});
            skLineSegment(sketch, "E18.12.6.6", {"start": v(237.5, 272.13) * mm, "end": v(242.5, 272.13) * mm});
            skArc(sketch, "E18.12.6.7", {"start": v(242.5, 272.13) * mm, "mid": v(243.91, 272.71) * mm, "end": v(244.5, 274.13) * mm});
            skLineSegment(sketch, "E18.12.7.0", {"start": v(235.5, 239.49) * mm, "end": v(235.5, 255.3) * mm});
            skLineSegment(sketch, "E18.12.7.1", {"start": v(244.5, 239.49) * mm, "end": v(244.5, 255.3) * mm});
            skPoint(sketch, "E18.12.7.2", {"position": v(244.5, 237.49) * mm});
            skPoint(sketch, "E18.12.7.3", {"position": v(235.5, 237.49) * mm});
            skLineSegment(sketch, "E18.12.7.4", {"start": v(235.5, 255.3) * mm, "end": v(244.5, 255.3) * mm});
            skArc(sketch, "E18.12.7.5", {"start": v(235.5, 239.49) * mm, "mid": v(236.09, 238.07) * mm, "end": v(237.5, 237.49) * mm});
            skLineSegment(sketch, "E18.12.7.6", {"start": v(237.5, 237.49) * mm, "end": v(242.5, 237.49) * mm});
            skArc(sketch, "E18.12.7.7", {"start": v(242.5, 237.49) * mm, "mid": v(243.91, 238.07) * mm, "end": v(244.5, 239.49) * mm});
            skLineSegment(sketch, "E18.12.8.0", {"start": v(235.5, 204.85) * mm, "end": v(235.5, 220.67) * mm});
            skLineSegment(sketch, "E18.12.8.1", {"start": v(244.5, 204.85) * mm, "end": v(244.5, 220.67) * mm});
            skPoint(sketch, "E18.12.8.2", {"position": v(244.5, 202.85) * mm});
            skPoint(sketch, "E18.12.8.3", {"position": v(235.5, 202.85) * mm});
            skLineSegment(sketch, "E18.12.8.4", {"start": v(235.5, 220.67) * mm, "end": v(244.5, 220.67) * mm});
            skArc(sketch, "E18.12.8.5", {"start": v(235.5, 204.85) * mm, "mid": v(236.09, 203.43) * mm, "end": v(237.5, 202.85) * mm});
            skLineSegment(sketch, "E18.12.8.6", {"start": v(237.5, 202.85) * mm, "end": v(242.5, 202.85) * mm});
            skArc(sketch, "E18.12.8.7", {"start": v(242.5, 202.85) * mm, "mid": v(243.91, 203.43) * mm, "end": v(244.5, 204.85) * mm});
            skLineSegment(sketch, "E18.12.9.0", {"start": v(235.5, 170.2) * mm, "end": v(235.5, 186.03) * mm});
            skLineSegment(sketch, "E18.12.9.1", {"start": v(244.5, 170.2) * mm, "end": v(244.5, 186.03) * mm});
            skPoint(sketch, "E18.12.9.2", {"position": v(244.5, 168.2) * mm});
            skPoint(sketch, "E18.12.9.3", {"position": v(235.5, 168.2) * mm});
            skLineSegment(sketch, "E18.12.9.4", {"start": v(235.5, 186.03) * mm, "end": v(244.5, 186.03) * mm});
            skArc(sketch, "E18.12.9.5", {"start": v(235.5, 170.2) * mm, "mid": v(236.09, 168.8) * mm, "end": v(237.5, 168.2) * mm});
            skLineSegment(sketch, "E18.12.9.6", {"start": v(237.5, 168.2) * mm, "end": v(242.5, 168.2) * mm});
            skArc(sketch, "E18.12.9.7", {"start": v(242.5, 168.2) * mm, "mid": v(243.91, 168.8) * mm, "end": v(244.5, 170.2) * mm});
            skLineSegment(sketch, "E18.12.10.0", {"start": v(235.5, 135.56) * mm, "end": v(235.5, 151.38) * mm});
            skLineSegment(sketch, "E18.12.10.1", {"start": v(244.5, 135.56) * mm, "end": v(244.5, 151.38) * mm});
            skPoint(sketch, "E18.12.10.2", {"position": v(244.5, 133.56) * mm});
            skPoint(sketch, "E18.12.10.3", {"position": v(235.5, 133.56) * mm});
            skLineSegment(sketch, "E18.12.10.4", {"start": v(235.5, 151.38) * mm, "end": v(244.5, 151.38) * mm});
            skArc(sketch, "E18.12.10.5", {"start": v(235.5, 135.56) * mm, "mid": v(236.09, 134.15) * mm, "end": v(237.5, 133.56) * mm});
            skLineSegment(sketch, "E18.12.10.6", {"start": v(237.5, 133.56) * mm, "end": v(242.5, 133.56) * mm});
            skArc(sketch, "E18.12.10.7", {"start": v(242.5, 133.56) * mm, "mid": v(243.91, 134.15) * mm, "end": v(244.5, 135.56) * mm});
            skLineSegment(sketch, "E18.12.11.0", {"start": v(235.5, 100.92) * mm, "end": v(235.5, 116.74) * mm});
            skLineSegment(sketch, "E18.12.11.1", {"start": v(244.5, 100.92) * mm, "end": v(244.5, 116.74) * mm});
            skPoint(sketch, "E18.12.11.2", {"position": v(244.5, 98.92) * mm});
            skPoint(sketch, "E18.12.11.3", {"position": v(235.5, 98.92) * mm});
            skLineSegment(sketch, "E18.12.11.4", {"start": v(235.5, 116.74) * mm, "end": v(244.5, 116.74) * mm});
            skArc(sketch, "E18.12.11.5", {"start": v(235.5, 100.92) * mm, "mid": v(236.09, 99.5) * mm, "end": v(237.5, 98.92) * mm});
            skLineSegment(sketch, "E18.12.11.6", {"start": v(237.5, 98.92) * mm, "end": v(242.5, 98.92) * mm});
            skArc(sketch, "E18.12.11.7", {"start": v(242.5, 98.92) * mm, "mid": v(243.91, 99.5) * mm, "end": v(244.5, 100.92) * mm});
            skLineSegment(sketch, "E18.12.12.0", {"start": v(235.5, 66.28) * mm, "end": v(235.5, 82.1) * mm});
            skLineSegment(sketch, "E18.12.12.1", {"start": v(244.5, 66.28) * mm, "end": v(244.5, 82.1) * mm});
            skPoint(sketch, "E18.12.12.2", {"position": v(244.5, 64.28) * mm});
            skPoint(sketch, "E18.12.12.3", {"position": v(235.5, 64.28) * mm});
            skLineSegment(sketch, "E18.12.12.4", {"start": v(235.5, 82.1) * mm, "end": v(244.5, 82.1) * mm});
            skArc(sketch, "E18.12.12.5", {"start": v(235.5, 66.28) * mm, "mid": v(236.09, 64.87) * mm, "end": v(237.5, 64.28) * mm});
            skLineSegment(sketch, "E18.12.12.6", {"start": v(237.5, 64.28) * mm, "end": v(242.5, 64.28) * mm});
            skArc(sketch, "E18.12.12.7", {"start": v(242.5, 64.28) * mm, "mid": v(243.91, 64.87) * mm, "end": v(244.5, 66.28) * mm});
            skLineSegment(sketch, "E18.12.13.0", {"start": v(235.5, 31.64) * mm, "end": v(235.5, 47.46) * mm});
            skLineSegment(sketch, "E18.12.13.1", {"start": v(244.5, 31.64) * mm, "end": v(244.5, 47.46) * mm});
            skPoint(sketch, "E18.12.13.2", {"position": v(244.5, 29.64) * mm});
            skPoint(sketch, "E18.12.13.3", {"position": v(235.5, 29.64) * mm});
            skLineSegment(sketch, "E18.12.13.4", {"start": v(235.5, 47.46) * mm, "end": v(244.5, 47.46) * mm});
            skArc(sketch, "E18.12.13.5", {"start": v(235.5, 31.64) * mm, "mid": v(236.09, 30.23) * mm, "end": v(237.5, 29.64) * mm});
            skLineSegment(sketch, "E18.12.13.6", {"start": v(237.5, 29.64) * mm, "end": v(242.5, 29.64) * mm});
            skArc(sketch, "E18.12.13.7", {"start": v(242.5, 29.64) * mm, "mid": v(243.91, 30.23) * mm, "end": v(244.5, 31.64) * mm});
            skLineSegment(sketch, "E18.12.14.0", {"start": v(235.5, -3) * mm, "end": v(235.5, 12.82) * mm});
            skLineSegment(sketch, "E18.12.14.1", {"start": v(244.5, -3) * mm, "end": v(244.5, 12.82) * mm});
            skPoint(sketch, "E18.12.14.2", {"position": v(244.5, -5) * mm});
            skPoint(sketch, "E18.12.14.3", {"position": v(235.5, -5) * mm});
            skLineSegment(sketch, "E18.12.14.4", {"start": v(235.5, 12.82) * mm, "end": v(244.5, 12.82) * mm});
            skArc(sketch, "E18.12.14.5", {"start": v(235.5, -3) * mm, "mid": v(236.09, -4.41) * mm, "end": v(237.5, -5) * mm});
            skLineSegment(sketch, "E18.12.14.6", {"start": v(237.5, -5) * mm, "end": v(242.5, -5) * mm});
            skArc(sketch, "E18.12.14.7", {"start": v(242.5, -5) * mm, "mid": v(243.91, -4.41) * mm, "end": v(244.5, -3) * mm});
            skLineSegment(sketch, "E18.13.0.0", {"start": v(255.5, 481.97) * mm, "end": v(255.5, 497.8) * mm});
            skLineSegment(sketch, "E18.13.0.1", {"start": v(264.5, 481.97) * mm, "end": v(264.5, 497.8) * mm});
            skPoint(sketch, "E18.13.0.2", {"position": v(264.5, 479.97) * mm});
            skPoint(sketch, "E18.13.0.3", {"position": v(255.5, 479.97) * mm});
            skLineSegment(sketch, "E18.13.0.4", {"start": v(255.5, 497.8) * mm, "end": v(264.5, 497.8) * mm});
            skArc(sketch, "E18.13.0.5", {"start": v(255.5, 481.97) * mm, "mid": v(256.09, 480.56) * mm, "end": v(257.5, 479.97) * mm});
            skLineSegment(sketch, "E18.13.0.6", {"start": v(257.5, 479.97) * mm, "end": v(262.5, 479.97) * mm});
            skArc(sketch, "E18.13.0.7", {"start": v(262.5, 479.97) * mm, "mid": v(263.91, 480.56) * mm, "end": v(264.5, 481.97) * mm});
            skLineSegment(sketch, "E18.13.1.0", {"start": v(255.5, 447.33) * mm, "end": v(255.5, 463.15) * mm});
            skLineSegment(sketch, "E18.13.1.1", {"start": v(264.5, 447.33) * mm, "end": v(264.5, 463.15) * mm});
            skPoint(sketch, "E18.13.1.2", {"position": v(264.5, 445.33) * mm});
            skPoint(sketch, "E18.13.1.3", {"position": v(255.5, 445.33) * mm});
            skLineSegment(sketch, "E18.13.1.4", {"start": v(255.5, 463.15) * mm, "end": v(264.5, 463.15) * mm});
            skArc(sketch, "E18.13.1.5", {"start": v(255.5, 447.33) * mm, "mid": v(256.09, 445.92) * mm, "end": v(257.5, 445.33) * mm});
            skLineSegment(sketch, "E18.13.1.6", {"start": v(257.5, 445.33) * mm, "end": v(262.5, 445.33) * mm});
            skArc(sketch, "E18.13.1.7", {"start": v(262.5, 445.33) * mm, "mid": v(263.91, 445.92) * mm, "end": v(264.5, 447.33) * mm});
            skLineSegment(sketch, "E18.13.2.0", {"start": v(255.5, 412.7) * mm, "end": v(255.5, 428.51) * mm});
            skLineSegment(sketch, "E18.13.2.1", {"start": v(264.5, 412.7) * mm, "end": v(264.5, 428.51) * mm});
            skPoint(sketch, "E18.13.2.2", {"position": v(264.5, 410.7) * mm});
            skPoint(sketch, "E18.13.2.3", {"position": v(255.5, 410.7) * mm});
            skLineSegment(sketch, "E18.13.2.4", {"start": v(255.5, 428.51) * mm, "end": v(264.5, 428.51) * mm});
            skArc(sketch, "E18.13.2.5", {"start": v(255.5, 412.7) * mm, "mid": v(256.09, 411.28) * mm, "end": v(257.5, 410.7) * mm});
            skLineSegment(sketch, "E18.13.2.6", {"start": v(257.5, 410.7) * mm, "end": v(262.5, 410.7) * mm});
            skArc(sketch, "E18.13.2.7", {"start": v(262.5, 410.7) * mm, "mid": v(263.91, 411.28) * mm, "end": v(264.5, 412.7) * mm});
            skLineSegment(sketch, "E18.13.3.0", {"start": v(255.5, 378.05) * mm, "end": v(255.5, 393.87) * mm});
            skLineSegment(sketch, "E18.13.3.1", {"start": v(264.5, 378.05) * mm, "end": v(264.5, 393.87) * mm});
            skPoint(sketch, "E18.13.3.2", {"position": v(264.5, 376.05) * mm});
            skPoint(sketch, "E18.13.3.3", {"position": v(255.5, 376.05) * mm});
            skLineSegment(sketch, "E18.13.3.4", {"start": v(255.5, 393.87) * mm, "end": v(264.5, 393.87) * mm});
            skArc(sketch, "E18.13.3.5", {"start": v(255.5, 378.05) * mm, "mid": v(256.09, 376.64) * mm, "end": v(257.5, 376.05) * mm});
            skLineSegment(sketch, "E18.13.3.6", {"start": v(257.5, 376.05) * mm, "end": v(262.5, 376.05) * mm});
            skArc(sketch, "E18.13.3.7", {"start": v(262.5, 376.05) * mm, "mid": v(263.91, 376.64) * mm, "end": v(264.5, 378.05) * mm});
            skLineSegment(sketch, "E18.13.4.0", {"start": v(255.5, 343.41) * mm, "end": v(255.5, 359.23) * mm});
            skLineSegment(sketch, "E18.13.4.1", {"start": v(264.5, 343.41) * mm, "end": v(264.5, 359.23) * mm});
            skPoint(sketch, "E18.13.4.2", {"position": v(264.5, 341.41) * mm});
            skPoint(sketch, "E18.13.4.3", {"position": v(255.5, 341.41) * mm});
            skLineSegment(sketch, "E18.13.4.4", {"start": v(255.5, 359.23) * mm, "end": v(264.5, 359.23) * mm});
            skArc(sketch, "E18.13.4.5", {"start": v(255.5, 343.41) * mm, "mid": v(256.09, 342) * mm, "end": v(257.5, 341.41) * mm});
            skLineSegment(sketch, "E18.13.4.6", {"start": v(257.5, 341.41) * mm, "end": v(262.5, 341.41) * mm});
            skArc(sketch, "E18.13.4.7", {"start": v(262.5, 341.41) * mm, "mid": v(263.91, 342) * mm, "end": v(264.5, 343.41) * mm});
            skLineSegment(sketch, "E18.13.5.0", {"start": v(255.5, 308.77) * mm, "end": v(255.5, 324.59) * mm});
            skLineSegment(sketch, "E18.13.5.1", {"start": v(264.5, 308.77) * mm, "end": v(264.5, 324.59) * mm});
            skPoint(sketch, "E18.13.5.2", {"position": v(264.5, 306.77) * mm});
            skPoint(sketch, "E18.13.5.3", {"position": v(255.5, 306.77) * mm});
            skLineSegment(sketch, "E18.13.5.4", {"start": v(255.5, 324.59) * mm, "end": v(264.5, 324.59) * mm});
            skArc(sketch, "E18.13.5.5", {"start": v(255.5, 308.77) * mm, "mid": v(256.09, 307.35) * mm, "end": v(257.5, 306.77) * mm});
            skLineSegment(sketch, "E18.13.5.6", {"start": v(257.5, 306.77) * mm, "end": v(262.5, 306.77) * mm});
            skArc(sketch, "E18.13.5.7", {"start": v(262.5, 306.77) * mm, "mid": v(263.91, 307.35) * mm, "end": v(264.5, 308.77) * mm});
            skLineSegment(sketch, "E18.13.6.0", {"start": v(255.5, 274.13) * mm, "end": v(255.5, 289.95) * mm});
            skLineSegment(sketch, "E18.13.6.1", {"start": v(264.5, 274.13) * mm, "end": v(264.5, 289.95) * mm});
            skPoint(sketch, "E18.13.6.2", {"position": v(264.5, 272.13) * mm});
            skPoint(sketch, "E18.13.6.3", {"position": v(255.5, 272.13) * mm});
            skLineSegment(sketch, "E18.13.6.4", {"start": v(255.5, 289.95) * mm, "end": v(264.5, 289.95) * mm});
            skArc(sketch, "E18.13.6.5", {"start": v(255.5, 274.13) * mm, "mid": v(256.09, 272.71) * mm, "end": v(257.5, 272.13) * mm});
            skLineSegment(sketch, "E18.13.6.6", {"start": v(257.5, 272.13) * mm, "end": v(262.5, 272.13) * mm});
            skArc(sketch, "E18.13.6.7", {"start": v(262.5, 272.13) * mm, "mid": v(263.91, 272.71) * mm, "end": v(264.5, 274.13) * mm});
            skLineSegment(sketch, "E18.13.7.0", {"start": v(255.5, 239.49) * mm, "end": v(255.5, 255.3) * mm});
            skLineSegment(sketch, "E18.13.7.1", {"start": v(264.5, 239.49) * mm, "end": v(264.5, 255.3) * mm});
            skPoint(sketch, "E18.13.7.2", {"position": v(264.5, 237.49) * mm});
            skPoint(sketch, "E18.13.7.3", {"position": v(255.5, 237.49) * mm});
            skLineSegment(sketch, "E18.13.7.4", {"start": v(255.5, 255.3) * mm, "end": v(264.5, 255.3) * mm});
            skArc(sketch, "E18.13.7.5", {"start": v(255.5, 239.49) * mm, "mid": v(256.09, 238.07) * mm, "end": v(257.5, 237.49) * mm});
            skLineSegment(sketch, "E18.13.7.6", {"start": v(257.5, 237.49) * mm, "end": v(262.5, 237.49) * mm});
            skArc(sketch, "E18.13.7.7", {"start": v(262.5, 237.49) * mm, "mid": v(263.91, 238.07) * mm, "end": v(264.5, 239.49) * mm});
            skLineSegment(sketch, "E18.13.8.0", {"start": v(255.5, 204.85) * mm, "end": v(255.5, 220.67) * mm});
            skLineSegment(sketch, "E18.13.8.1", {"start": v(264.5, 204.85) * mm, "end": v(264.5, 220.67) * mm});
            skPoint(sketch, "E18.13.8.2", {"position": v(264.5, 202.85) * mm});
            skPoint(sketch, "E18.13.8.3", {"position": v(255.5, 202.85) * mm});
            skLineSegment(sketch, "E18.13.8.4", {"start": v(255.5, 220.67) * mm, "end": v(264.5, 220.67) * mm});
            skArc(sketch, "E18.13.8.5", {"start": v(255.5, 204.85) * mm, "mid": v(256.09, 203.43) * mm, "end": v(257.5, 202.85) * mm});
            skLineSegment(sketch, "E18.13.8.6", {"start": v(257.5, 202.85) * mm, "end": v(262.5, 202.85) * mm});
            skArc(sketch, "E18.13.8.7", {"start": v(262.5, 202.85) * mm, "mid": v(263.91, 203.43) * mm, "end": v(264.5, 204.85) * mm});
            skLineSegment(sketch, "E18.13.9.0", {"start": v(255.5, 170.2) * mm, "end": v(255.5, 186.03) * mm});
            skLineSegment(sketch, "E18.13.9.1", {"start": v(264.5, 170.2) * mm, "end": v(264.5, 186.03) * mm});
            skPoint(sketch, "E18.13.9.2", {"position": v(264.5, 168.2) * mm});
            skPoint(sketch, "E18.13.9.3", {"position": v(255.5, 168.2) * mm});
            skLineSegment(sketch, "E18.13.9.4", {"start": v(255.5, 186.03) * mm, "end": v(264.5, 186.03) * mm});
            skArc(sketch, "E18.13.9.5", {"start": v(255.5, 170.2) * mm, "mid": v(256.09, 168.8) * mm, "end": v(257.5, 168.2) * mm});
            skLineSegment(sketch, "E18.13.9.6", {"start": v(257.5, 168.2) * mm, "end": v(262.5, 168.2) * mm});
            skArc(sketch, "E18.13.9.7", {"start": v(262.5, 168.2) * mm, "mid": v(263.91, 168.8) * mm, "end": v(264.5, 170.2) * mm});
            skLineSegment(sketch, "E18.13.10.0", {"start": v(255.5, 135.56) * mm, "end": v(255.5, 151.38) * mm});
            skLineSegment(sketch, "E18.13.10.1", {"start": v(264.5, 135.56) * mm, "end": v(264.5, 151.38) * mm});
            skPoint(sketch, "E18.13.10.2", {"position": v(264.5, 133.56) * mm});
            skPoint(sketch, "E18.13.10.3", {"position": v(255.5, 133.56) * mm});
            skLineSegment(sketch, "E18.13.10.4", {"start": v(255.5, 151.38) * mm, "end": v(264.5, 151.38) * mm});
            skArc(sketch, "E18.13.10.5", {"start": v(255.5, 135.56) * mm, "mid": v(256.09, 134.15) * mm, "end": v(257.5, 133.56) * mm});
            skLineSegment(sketch, "E18.13.10.6", {"start": v(257.5, 133.56) * mm, "end": v(262.5, 133.56) * mm});
            skArc(sketch, "E18.13.10.7", {"start": v(262.5, 133.56) * mm, "mid": v(263.91, 134.15) * mm, "end": v(264.5, 135.56) * mm});
            skLineSegment(sketch, "E18.13.11.0", {"start": v(255.5, 100.92) * mm, "end": v(255.5, 116.74) * mm});
            skLineSegment(sketch, "E18.13.11.1", {"start": v(264.5, 100.92) * mm, "end": v(264.5, 116.74) * mm});
            skPoint(sketch, "E18.13.11.2", {"position": v(264.5, 98.92) * mm});
            skPoint(sketch, "E18.13.11.3", {"position": v(255.5, 98.92) * mm});
            skLineSegment(sketch, "E18.13.11.4", {"start": v(255.5, 116.74) * mm, "end": v(264.5, 116.74) * mm});
            skArc(sketch, "E18.13.11.5", {"start": v(255.5, 100.92) * mm, "mid": v(256.09, 99.5) * mm, "end": v(257.5, 98.92) * mm});
            skLineSegment(sketch, "E18.13.11.6", {"start": v(257.5, 98.92) * mm, "end": v(262.5, 98.92) * mm});
            skArc(sketch, "E18.13.11.7", {"start": v(262.5, 98.92) * mm, "mid": v(263.91, 99.5) * mm, "end": v(264.5, 100.92) * mm});
            skLineSegment(sketch, "E18.13.12.0", {"start": v(255.5, 66.28) * mm, "end": v(255.5, 82.1) * mm});
            skLineSegment(sketch, "E18.13.12.1", {"start": v(264.5, 66.28) * mm, "end": v(264.5, 82.1) * mm});
            skPoint(sketch, "E18.13.12.2", {"position": v(264.5, 64.28) * mm});
            skPoint(sketch, "E18.13.12.3", {"position": v(255.5, 64.28) * mm});
            skLineSegment(sketch, "E18.13.12.4", {"start": v(255.5, 82.1) * mm, "end": v(264.5, 82.1) * mm});
            skArc(sketch, "E18.13.12.5", {"start": v(255.5, 66.28) * mm, "mid": v(256.09, 64.87) * mm, "end": v(257.5, 64.28) * mm});
            skLineSegment(sketch, "E18.13.12.6", {"start": v(257.5, 64.28) * mm, "end": v(262.5, 64.28) * mm});
            skArc(sketch, "E18.13.12.7", {"start": v(262.5, 64.28) * mm, "mid": v(263.91, 64.87) * mm, "end": v(264.5, 66.28) * mm});
            skLineSegment(sketch, "E18.13.13.0", {"start": v(255.5, 31.64) * mm, "end": v(255.5, 47.46) * mm});
            skLineSegment(sketch, "E18.13.13.1", {"start": v(264.5, 31.64) * mm, "end": v(264.5, 47.46) * mm});
            skPoint(sketch, "E18.13.13.2", {"position": v(264.5, 29.64) * mm});
            skPoint(sketch, "E18.13.13.3", {"position": v(255.5, 29.64) * mm});
            skLineSegment(sketch, "E18.13.13.4", {"start": v(255.5, 47.46) * mm, "end": v(264.5, 47.46) * mm});
            skArc(sketch, "E18.13.13.5", {"start": v(255.5, 31.64) * mm, "mid": v(256.09, 30.23) * mm, "end": v(257.5, 29.64) * mm});
            skLineSegment(sketch, "E18.13.13.6", {"start": v(257.5, 29.64) * mm, "end": v(262.5, 29.64) * mm});
            skArc(sketch, "E18.13.13.7", {"start": v(262.5, 29.64) * mm, "mid": v(263.91, 30.23) * mm, "end": v(264.5, 31.64) * mm});
            skLineSegment(sketch, "E18.13.14.0", {"start": v(255.5, -3) * mm, "end": v(255.5, 12.82) * mm});
            skLineSegment(sketch, "E18.13.14.1", {"start": v(264.5, -3) * mm, "end": v(264.5, 12.82) * mm});
            skPoint(sketch, "E18.13.14.2", {"position": v(264.5, -5) * mm});
            skPoint(sketch, "E18.13.14.3", {"position": v(255.5, -5) * mm});
            skLineSegment(sketch, "E18.13.14.4", {"start": v(255.5, 12.82) * mm, "end": v(264.5, 12.82) * mm});
            skArc(sketch, "E18.13.14.5", {"start": v(255.5, -3) * mm, "mid": v(256.09, -4.41) * mm, "end": v(257.5, -5) * mm});
            skLineSegment(sketch, "E18.13.14.6", {"start": v(257.5, -5) * mm, "end": v(262.5, -5) * mm});
            skArc(sketch, "E18.13.14.7", {"start": v(262.5, -5) * mm, "mid": v(263.91, -4.41) * mm, "end": v(264.5, -3) * mm});
            skLineSegment(sketch, "E18.14.0.0", {"start": v(275.5, 481.97) * mm, "end": v(275.5, 497.8) * mm});
            skLineSegment(sketch, "E18.14.0.1", {"start": v(284.5, 481.97) * mm, "end": v(284.5, 497.8) * mm});
            skPoint(sketch, "E18.14.0.2", {"position": v(284.5, 479.97) * mm});
            skPoint(sketch, "E18.14.0.3", {"position": v(275.5, 479.97) * mm});
            skLineSegment(sketch, "E18.14.0.4", {"start": v(275.5, 497.8) * mm, "end": v(284.5, 497.8) * mm});
            skArc(sketch, "E18.14.0.5", {"start": v(275.5, 481.97) * mm, "mid": v(276.09, 480.56) * mm, "end": v(277.5, 479.97) * mm});
            skLineSegment(sketch, "E18.14.0.6", {"start": v(277.5, 479.97) * mm, "end": v(282.5, 479.97) * mm});
            skArc(sketch, "E18.14.0.7", {"start": v(282.5, 479.97) * mm, "mid": v(283.91, 480.56) * mm, "end": v(284.5, 481.97) * mm});
            skLineSegment(sketch, "E18.14.1.0", {"start": v(275.5, 447.33) * mm, "end": v(275.5, 463.15) * mm});
            skLineSegment(sketch, "E18.14.1.1", {"start": v(284.5, 447.33) * mm, "end": v(284.5, 463.15) * mm});
            skPoint(sketch, "E18.14.1.2", {"position": v(284.5, 445.33) * mm});
            skPoint(sketch, "E18.14.1.3", {"position": v(275.5, 445.33) * mm});
            skLineSegment(sketch, "E18.14.1.4", {"start": v(275.5, 463.15) * mm, "end": v(284.5, 463.15) * mm});
            skArc(sketch, "E18.14.1.5", {"start": v(275.5, 447.33) * mm, "mid": v(276.09, 445.92) * mm, "end": v(277.5, 445.33) * mm});
            skLineSegment(sketch, "E18.14.1.6", {"start": v(277.5, 445.33) * mm, "end": v(282.5, 445.33) * mm});
            skArc(sketch, "E18.14.1.7", {"start": v(282.5, 445.33) * mm, "mid": v(283.91, 445.92) * mm, "end": v(284.5, 447.33) * mm});
            skLineSegment(sketch, "E18.14.2.0", {"start": v(275.5, 412.7) * mm, "end": v(275.5, 428.51) * mm});
            skLineSegment(sketch, "E18.14.2.1", {"start": v(284.5, 412.7) * mm, "end": v(284.5, 428.51) * mm});
            skPoint(sketch, "E18.14.2.2", {"position": v(284.5, 410.7) * mm});
            skPoint(sketch, "E18.14.2.3", {"position": v(275.5, 410.7) * mm});
            skLineSegment(sketch, "E18.14.2.4", {"start": v(275.5, 428.51) * mm, "end": v(284.5, 428.51) * mm});
            skArc(sketch, "E18.14.2.5", {"start": v(275.5, 412.7) * mm, "mid": v(276.09, 411.28) * mm, "end": v(277.5, 410.7) * mm});
            skLineSegment(sketch, "E18.14.2.6", {"start": v(277.5, 410.7) * mm, "end": v(282.5, 410.7) * mm});
            skArc(sketch, "E18.14.2.7", {"start": v(282.5, 410.7) * mm, "mid": v(283.91, 411.28) * mm, "end": v(284.5, 412.7) * mm});
            skLineSegment(sketch, "E18.14.3.0", {"start": v(275.5, 378.05) * mm, "end": v(275.5, 393.87) * mm});
            skLineSegment(sketch, "E18.14.3.1", {"start": v(284.5, 378.05) * mm, "end": v(284.5, 393.87) * mm});
            skPoint(sketch, "E18.14.3.2", {"position": v(284.5, 376.05) * mm});
            skPoint(sketch, "E18.14.3.3", {"position": v(275.5, 376.05) * mm});
            skLineSegment(sketch, "E18.14.3.4", {"start": v(275.5, 393.87) * mm, "end": v(284.5, 393.87) * mm});
            skArc(sketch, "E18.14.3.5", {"start": v(275.5, 378.05) * mm, "mid": v(276.09, 376.64) * mm, "end": v(277.5, 376.05) * mm});
            skLineSegment(sketch, "E18.14.3.6", {"start": v(277.5, 376.05) * mm, "end": v(282.5, 376.05) * mm});
            skArc(sketch, "E18.14.3.7", {"start": v(282.5, 376.05) * mm, "mid": v(283.91, 376.64) * mm, "end": v(284.5, 378.05) * mm});
            skLineSegment(sketch, "E18.14.4.0", {"start": v(275.5, 343.41) * mm, "end": v(275.5, 359.23) * mm});
            skLineSegment(sketch, "E18.14.4.1", {"start": v(284.5, 343.41) * mm, "end": v(284.5, 359.23) * mm});
            skPoint(sketch, "E18.14.4.2", {"position": v(284.5, 341.41) * mm});
            skPoint(sketch, "E18.14.4.3", {"position": v(275.5, 341.41) * mm});
            skLineSegment(sketch, "E18.14.4.4", {"start": v(275.5, 359.23) * mm, "end": v(284.5, 359.23) * mm});
            skArc(sketch, "E18.14.4.5", {"start": v(275.5, 343.41) * mm, "mid": v(276.09, 342) * mm, "end": v(277.5, 341.41) * mm});
            skLineSegment(sketch, "E18.14.4.6", {"start": v(277.5, 341.41) * mm, "end": v(282.5, 341.41) * mm});
            skArc(sketch, "E18.14.4.7", {"start": v(282.5, 341.41) * mm, "mid": v(283.91, 342) * mm, "end": v(284.5, 343.41) * mm});
            skLineSegment(sketch, "E18.14.5.0", {"start": v(275.5, 308.77) * mm, "end": v(275.5, 324.59) * mm});
            skLineSegment(sketch, "E18.14.5.1", {"start": v(284.5, 308.77) * mm, "end": v(284.5, 324.59) * mm});
            skPoint(sketch, "E18.14.5.2", {"position": v(284.5, 306.77) * mm});
            skPoint(sketch, "E18.14.5.3", {"position": v(275.5, 306.77) * mm});
            skLineSegment(sketch, "E18.14.5.4", {"start": v(275.5, 324.59) * mm, "end": v(284.5, 324.59) * mm});
            skArc(sketch, "E18.14.5.5", {"start": v(275.5, 308.77) * mm, "mid": v(276.09, 307.35) * mm, "end": v(277.5, 306.77) * mm});
            skLineSegment(sketch, "E18.14.5.6", {"start": v(277.5, 306.77) * mm, "end": v(282.5, 306.77) * mm});
            skArc(sketch, "E18.14.5.7", {"start": v(282.5, 306.77) * mm, "mid": v(283.91, 307.35) * mm, "end": v(284.5, 308.77) * mm});
            skLineSegment(sketch, "E18.14.6.0", {"start": v(275.5, 274.13) * mm, "end": v(275.5, 289.95) * mm});
            skLineSegment(sketch, "E18.14.6.1", {"start": v(284.5, 274.13) * mm, "end": v(284.5, 289.95) * mm});
            skPoint(sketch, "E18.14.6.2", {"position": v(284.5, 272.13) * mm});
            skPoint(sketch, "E18.14.6.3", {"position": v(275.5, 272.13) * mm});
            skLineSegment(sketch, "E18.14.6.4", {"start": v(275.5, 289.95) * mm, "end": v(284.5, 289.95) * mm});
            skArc(sketch, "E18.14.6.5", {"start": v(275.5, 274.13) * mm, "mid": v(276.09, 272.71) * mm, "end": v(277.5, 272.13) * mm});
            skLineSegment(sketch, "E18.14.6.6", {"start": v(277.5, 272.13) * mm, "end": v(282.5, 272.13) * mm});
            skArc(sketch, "E18.14.6.7", {"start": v(282.5, 272.13) * mm, "mid": v(283.91, 272.71) * mm, "end": v(284.5, 274.13) * mm});
            skLineSegment(sketch, "E18.14.7.0", {"start": v(275.5, 239.49) * mm, "end": v(275.5, 255.3) * mm});
            skLineSegment(sketch, "E18.14.7.1", {"start": v(284.5, 239.49) * mm, "end": v(284.5, 255.3) * mm});
            skPoint(sketch, "E18.14.7.2", {"position": v(284.5, 237.49) * mm});
            skPoint(sketch, "E18.14.7.3", {"position": v(275.5, 237.49) * mm});
            skLineSegment(sketch, "E18.14.7.4", {"start": v(275.5, 255.3) * mm, "end": v(284.5, 255.3) * mm});
            skArc(sketch, "E18.14.7.5", {"start": v(275.5, 239.49) * mm, "mid": v(276.09, 238.07) * mm, "end": v(277.5, 237.49) * mm});
            skLineSegment(sketch, "E18.14.7.6", {"start": v(277.5, 237.49) * mm, "end": v(282.5, 237.49) * mm});
            skArc(sketch, "E18.14.7.7", {"start": v(282.5, 237.49) * mm, "mid": v(283.91, 238.07) * mm, "end": v(284.5, 239.49) * mm});
            skLineSegment(sketch, "E18.14.8.0", {"start": v(275.5, 204.85) * mm, "end": v(275.5, 220.67) * mm});
            skLineSegment(sketch, "E18.14.8.1", {"start": v(284.5, 204.85) * mm, "end": v(284.5, 220.67) * mm});
            skPoint(sketch, "E18.14.8.2", {"position": v(284.5, 202.85) * mm});
            skPoint(sketch, "E18.14.8.3", {"position": v(275.5, 202.85) * mm});
            skLineSegment(sketch, "E18.14.8.4", {"start": v(275.5, 220.67) * mm, "end": v(284.5, 220.67) * mm});
            skArc(sketch, "E18.14.8.5", {"start": v(275.5, 204.85) * mm, "mid": v(276.09, 203.43) * mm, "end": v(277.5, 202.85) * mm});
            skLineSegment(sketch, "E18.14.8.6", {"start": v(277.5, 202.85) * mm, "end": v(282.5, 202.85) * mm});
            skArc(sketch, "E18.14.8.7", {"start": v(282.5, 202.85) * mm, "mid": v(283.91, 203.43) * mm, "end": v(284.5, 204.85) * mm});
            skLineSegment(sketch, "E18.14.9.0", {"start": v(275.5, 170.2) * mm, "end": v(275.5, 186.03) * mm});
            skLineSegment(sketch, "E18.14.9.1", {"start": v(284.5, 170.2) * mm, "end": v(284.5, 186.03) * mm});
            skPoint(sketch, "E18.14.9.2", {"position": v(284.5, 168.2) * mm});
            skPoint(sketch, "E18.14.9.3", {"position": v(275.5, 168.2) * mm});
            skLineSegment(sketch, "E18.14.9.4", {"start": v(275.5, 186.03) * mm, "end": v(284.5, 186.03) * mm});
            skArc(sketch, "E18.14.9.5", {"start": v(275.5, 170.2) * mm, "mid": v(276.09, 168.8) * mm, "end": v(277.5, 168.2) * mm});
            skLineSegment(sketch, "E18.14.9.6", {"start": v(277.5, 168.2) * mm, "end": v(282.5, 168.2) * mm});
            skArc(sketch, "E18.14.9.7", {"start": v(282.5, 168.2) * mm, "mid": v(283.91, 168.8) * mm, "end": v(284.5, 170.2) * mm});
            skLineSegment(sketch, "E18.14.10.0", {"start": v(275.5, 135.56) * mm, "end": v(275.5, 151.38) * mm});
            skLineSegment(sketch, "E18.14.10.1", {"start": v(284.5, 135.56) * mm, "end": v(284.5, 151.38) * mm});
            skPoint(sketch, "E18.14.10.2", {"position": v(284.5, 133.56) * mm});
            skPoint(sketch, "E18.14.10.3", {"position": v(275.5, 133.56) * mm});
            skLineSegment(sketch, "E18.14.10.4", {"start": v(275.5, 151.38) * mm, "end": v(284.5, 151.38) * mm});
            skArc(sketch, "E18.14.10.5", {"start": v(275.5, 135.56) * mm, "mid": v(276.09, 134.15) * mm, "end": v(277.5, 133.56) * mm});
            skLineSegment(sketch, "E18.14.10.6", {"start": v(277.5, 133.56) * mm, "end": v(282.5, 133.56) * mm});
            skArc(sketch, "E18.14.10.7", {"start": v(282.5, 133.56) * mm, "mid": v(283.91, 134.15) * mm, "end": v(284.5, 135.56) * mm});
            skLineSegment(sketch, "E18.14.11.0", {"start": v(275.5, 100.92) * mm, "end": v(275.5, 116.74) * mm});
            skLineSegment(sketch, "E18.14.11.1", {"start": v(284.5, 100.92) * mm, "end": v(284.5, 116.74) * mm});
            skPoint(sketch, "E18.14.11.2", {"position": v(284.5, 98.92) * mm});
            skPoint(sketch, "E18.14.11.3", {"position": v(275.5, 98.92) * mm});
            skLineSegment(sketch, "E18.14.11.4", {"start": v(275.5, 116.74) * mm, "end": v(284.5, 116.74) * mm});
            skArc(sketch, "E18.14.11.5", {"start": v(275.5, 100.92) * mm, "mid": v(276.09, 99.5) * mm, "end": v(277.5, 98.92) * mm});
            skLineSegment(sketch, "E18.14.11.6", {"start": v(277.5, 98.92) * mm, "end": v(282.5, 98.92) * mm});
            skArc(sketch, "E18.14.11.7", {"start": v(282.5, 98.92) * mm, "mid": v(283.91, 99.5) * mm, "end": v(284.5, 100.92) * mm});
            skLineSegment(sketch, "E18.14.12.0", {"start": v(275.5, 66.28) * mm, "end": v(275.5, 82.1) * mm});
            skLineSegment(sketch, "E18.14.12.1", {"start": v(284.5, 66.28) * mm, "end": v(284.5, 82.1) * mm});
            skPoint(sketch, "E18.14.12.2", {"position": v(284.5, 64.28) * mm});
            skPoint(sketch, "E18.14.12.3", {"position": v(275.5, 64.28) * mm});
            skLineSegment(sketch, "E18.14.12.4", {"start": v(275.5, 82.1) * mm, "end": v(284.5, 82.1) * mm});
            skArc(sketch, "E18.14.12.5", {"start": v(275.5, 66.28) * mm, "mid": v(276.09, 64.87) * mm, "end": v(277.5, 64.28) * mm});
            skLineSegment(sketch, "E18.14.12.6", {"start": v(277.5, 64.28) * mm, "end": v(282.5, 64.28) * mm});
            skArc(sketch, "E18.14.12.7", {"start": v(282.5, 64.28) * mm, "mid": v(283.91, 64.87) * mm, "end": v(284.5, 66.28) * mm});
            skLineSegment(sketch, "E18.14.13.0", {"start": v(275.5, 31.64) * mm, "end": v(275.5, 47.46) * mm});
            skLineSegment(sketch, "E18.14.13.1", {"start": v(284.5, 31.64) * mm, "end": v(284.5, 47.46) * mm});
            skPoint(sketch, "E18.14.13.2", {"position": v(284.5, 29.64) * mm});
            skPoint(sketch, "E18.14.13.3", {"position": v(275.5, 29.64) * mm});
            skLineSegment(sketch, "E18.14.13.4", {"start": v(275.5, 47.46) * mm, "end": v(284.5, 47.46) * mm});
            skArc(sketch, "E18.14.13.5", {"start": v(275.5, 31.64) * mm, "mid": v(276.09, 30.23) * mm, "end": v(277.5, 29.64) * mm});
            skLineSegment(sketch, "E18.14.13.6", {"start": v(277.5, 29.64) * mm, "end": v(282.5, 29.64) * mm});
            skArc(sketch, "E18.14.13.7", {"start": v(282.5, 29.64) * mm, "mid": v(283.91, 30.23) * mm, "end": v(284.5, 31.64) * mm});
            skLineSegment(sketch, "E18.14.14.0", {"start": v(275.5, -3) * mm, "end": v(275.5, 12.82) * mm});
            skLineSegment(sketch, "E18.14.14.1", {"start": v(284.5, -3) * mm, "end": v(284.5, 12.82) * mm});
            skPoint(sketch, "E18.14.14.2", {"position": v(284.5, -5) * mm});
            skPoint(sketch, "E18.14.14.3", {"position": v(275.5, -5) * mm});
            skLineSegment(sketch, "E18.14.14.4", {"start": v(275.5, 12.82) * mm, "end": v(284.5, 12.82) * mm});
            skArc(sketch, "E18.14.14.5", {"start": v(275.5, -3) * mm, "mid": v(276.09, -4.41) * mm, "end": v(277.5, -5) * mm});
            skLineSegment(sketch, "E18.14.14.6", {"start": v(277.5, -5) * mm, "end": v(282.5, -5) * mm});
            skArc(sketch, "E18.14.14.7", {"start": v(282.5, -5) * mm, "mid": v(283.91, -4.41) * mm, "end": v(284.5, -3) * mm});
            skLineSegment(sketch, "E18.15.0.0", {"start": v(295.5, 481.97) * mm, "end": v(295.5, 497.8) * mm});
            skLineSegment(sketch, "E18.15.0.1", {"start": v(304.5, 481.97) * mm, "end": v(304.5, 497.8) * mm});
            skPoint(sketch, "E18.15.0.2", {"position": v(304.5, 479.97) * mm});
            skPoint(sketch, "E18.15.0.3", {"position": v(295.5, 479.97) * mm});
            skLineSegment(sketch, "E18.15.0.4", {"start": v(295.5, 497.8) * mm, "end": v(304.5, 497.8) * mm});
            skArc(sketch, "E18.15.0.5", {"start": v(295.5, 481.97) * mm, "mid": v(296.09, 480.56) * mm, "end": v(297.5, 479.97) * mm});
            skLineSegment(sketch, "E18.15.0.6", {"start": v(297.5, 479.97) * mm, "end": v(302.5, 479.97) * mm});
            skArc(sketch, "E18.15.0.7", {"start": v(302.5, 479.97) * mm, "mid": v(303.91, 480.56) * mm, "end": v(304.5, 481.97) * mm});
            skLineSegment(sketch, "E18.15.1.0", {"start": v(295.5, 447.33) * mm, "end": v(295.5, 463.15) * mm});
            skLineSegment(sketch, "E18.15.1.1", {"start": v(304.5, 447.33) * mm, "end": v(304.5, 463.15) * mm});
            skPoint(sketch, "E18.15.1.2", {"position": v(304.5, 445.33) * mm});
            skPoint(sketch, "E18.15.1.3", {"position": v(295.5, 445.33) * mm});
            skLineSegment(sketch, "E18.15.1.4", {"start": v(295.5, 463.15) * mm, "end": v(304.5, 463.15) * mm});
            skArc(sketch, "E18.15.1.5", {"start": v(295.5, 447.33) * mm, "mid": v(296.09, 445.92) * mm, "end": v(297.5, 445.33) * mm});
            skLineSegment(sketch, "E18.15.1.6", {"start": v(297.5, 445.33) * mm, "end": v(302.5, 445.33) * mm});
            skArc(sketch, "E18.15.1.7", {"start": v(302.5, 445.33) * mm, "mid": v(303.91, 445.92) * mm, "end": v(304.5, 447.33) * mm});
            skLineSegment(sketch, "E18.15.2.0", {"start": v(295.5, 412.7) * mm, "end": v(295.5, 428.51) * mm});
            skLineSegment(sketch, "E18.15.2.1", {"start": v(304.5, 412.7) * mm, "end": v(304.5, 428.51) * mm});
            skPoint(sketch, "E18.15.2.2", {"position": v(304.5, 410.7) * mm});
            skPoint(sketch, "E18.15.2.3", {"position": v(295.5, 410.7) * mm});
            skLineSegment(sketch, "E18.15.2.4", {"start": v(295.5, 428.51) * mm, "end": v(304.5, 428.51) * mm});
            skArc(sketch, "E18.15.2.5", {"start": v(295.5, 412.7) * mm, "mid": v(296.09, 411.28) * mm, "end": v(297.5, 410.7) * mm});
            skLineSegment(sketch, "E18.15.2.6", {"start": v(297.5, 410.7) * mm, "end": v(302.5, 410.7) * mm});
            skArc(sketch, "E18.15.2.7", {"start": v(302.5, 410.7) * mm, "mid": v(303.91, 411.28) * mm, "end": v(304.5, 412.7) * mm});
            skLineSegment(sketch, "E18.15.3.0", {"start": v(295.5, 378.05) * mm, "end": v(295.5, 393.87) * mm});
            skLineSegment(sketch, "E18.15.3.1", {"start": v(304.5, 378.05) * mm, "end": v(304.5, 393.87) * mm});
            skPoint(sketch, "E18.15.3.2", {"position": v(304.5, 376.05) * mm});
            skPoint(sketch, "E18.15.3.3", {"position": v(295.5, 376.05) * mm});
            skLineSegment(sketch, "E18.15.3.4", {"start": v(295.5, 393.87) * mm, "end": v(304.5, 393.87) * mm});
            skArc(sketch, "E18.15.3.5", {"start": v(295.5, 378.05) * mm, "mid": v(296.09, 376.64) * mm, "end": v(297.5, 376.05) * mm});
            skLineSegment(sketch, "E18.15.3.6", {"start": v(297.5, 376.05) * mm, "end": v(302.5, 376.05) * mm});
            skArc(sketch, "E18.15.3.7", {"start": v(302.5, 376.05) * mm, "mid": v(303.91, 376.64) * mm, "end": v(304.5, 378.05) * mm});
            skLineSegment(sketch, "E18.15.4.0", {"start": v(295.5, 343.41) * mm, "end": v(295.5, 359.23) * mm});
            skLineSegment(sketch, "E18.15.4.1", {"start": v(304.5, 343.41) * mm, "end": v(304.5, 359.23) * mm});
            skPoint(sketch, "E18.15.4.2", {"position": v(304.5, 341.41) * mm});
            skPoint(sketch, "E18.15.4.3", {"position": v(295.5, 341.41) * mm});
            skLineSegment(sketch, "E18.15.4.4", {"start": v(295.5, 359.23) * mm, "end": v(304.5, 359.23) * mm});
            skArc(sketch, "E18.15.4.5", {"start": v(295.5, 343.41) * mm, "mid": v(296.09, 342) * mm, "end": v(297.5, 341.41) * mm});
            skLineSegment(sketch, "E18.15.4.6", {"start": v(297.5, 341.41) * mm, "end": v(302.5, 341.41) * mm});
            skArc(sketch, "E18.15.4.7", {"start": v(302.5, 341.41) * mm, "mid": v(303.91, 342) * mm, "end": v(304.5, 343.41) * mm});
            skLineSegment(sketch, "E18.15.5.0", {"start": v(295.5, 308.77) * mm, "end": v(295.5, 324.59) * mm});
            skLineSegment(sketch, "E18.15.5.1", {"start": v(304.5, 308.77) * mm, "end": v(304.5, 324.59) * mm});
            skPoint(sketch, "E18.15.5.2", {"position": v(304.5, 306.77) * mm});
            skPoint(sketch, "E18.15.5.3", {"position": v(295.5, 306.77) * mm});
            skLineSegment(sketch, "E18.15.5.4", {"start": v(295.5, 324.59) * mm, "end": v(304.5, 324.59) * mm});
            skArc(sketch, "E18.15.5.5", {"start": v(295.5, 308.77) * mm, "mid": v(296.09, 307.35) * mm, "end": v(297.5, 306.77) * mm});
            skLineSegment(sketch, "E18.15.5.6", {"start": v(297.5, 306.77) * mm, "end": v(302.5, 306.77) * mm});
            skArc(sketch, "E18.15.5.7", {"start": v(302.5, 306.77) * mm, "mid": v(303.91, 307.35) * mm, "end": v(304.5, 308.77) * mm});
            skLineSegment(sketch, "E18.15.6.0", {"start": v(295.5, 274.13) * mm, "end": v(295.5, 289.95) * mm});
            skLineSegment(sketch, "E18.15.6.1", {"start": v(304.5, 274.13) * mm, "end": v(304.5, 289.95) * mm});
            skPoint(sketch, "E18.15.6.2", {"position": v(304.5, 272.13) * mm});
            skPoint(sketch, "E18.15.6.3", {"position": v(295.5, 272.13) * mm});
            skLineSegment(sketch, "E18.15.6.4", {"start": v(295.5, 289.95) * mm, "end": v(304.5, 289.95) * mm});
            skArc(sketch, "E18.15.6.5", {"start": v(295.5, 274.13) * mm, "mid": v(296.09, 272.71) * mm, "end": v(297.5, 272.13) * mm});
            skLineSegment(sketch, "E18.15.6.6", {"start": v(297.5, 272.13) * mm, "end": v(302.5, 272.13) * mm});
            skArc(sketch, "E18.15.6.7", {"start": v(302.5, 272.13) * mm, "mid": v(303.91, 272.71) * mm, "end": v(304.5, 274.13) * mm});
            skLineSegment(sketch, "E18.15.7.0", {"start": v(295.5, 239.49) * mm, "end": v(295.5, 255.3) * mm});
            skLineSegment(sketch, "E18.15.7.1", {"start": v(304.5, 239.49) * mm, "end": v(304.5, 255.3) * mm});
            skPoint(sketch, "E18.15.7.2", {"position": v(304.5, 237.49) * mm});
            skPoint(sketch, "E18.15.7.3", {"position": v(295.5, 237.49) * mm});
            skLineSegment(sketch, "E18.15.7.4", {"start": v(295.5, 255.3) * mm, "end": v(304.5, 255.3) * mm});
            skArc(sketch, "E18.15.7.5", {"start": v(295.5, 239.49) * mm, "mid": v(296.09, 238.07) * mm, "end": v(297.5, 237.49) * mm});
            skLineSegment(sketch, "E18.15.7.6", {"start": v(297.5, 237.49) * mm, "end": v(302.5, 237.49) * mm});
            skArc(sketch, "E18.15.7.7", {"start": v(302.5, 237.49) * mm, "mid": v(303.91, 238.07) * mm, "end": v(304.5, 239.49) * mm});
            skLineSegment(sketch, "E18.15.8.0", {"start": v(295.5, 204.85) * mm, "end": v(295.5, 220.67) * mm});
            skLineSegment(sketch, "E18.15.8.1", {"start": v(304.5, 204.85) * mm, "end": v(304.5, 220.67) * mm});
            skPoint(sketch, "E18.15.8.2", {"position": v(304.5, 202.85) * mm});
            skPoint(sketch, "E18.15.8.3", {"position": v(295.5, 202.85) * mm});
            skLineSegment(sketch, "E18.15.8.4", {"start": v(295.5, 220.67) * mm, "end": v(304.5, 220.67) * mm});
            skArc(sketch, "E18.15.8.5", {"start": v(295.5, 204.85) * mm, "mid": v(296.09, 203.43) * mm, "end": v(297.5, 202.85) * mm});
            skLineSegment(sketch, "E18.15.8.6", {"start": v(297.5, 202.85) * mm, "end": v(302.5, 202.85) * mm});
            skArc(sketch, "E18.15.8.7", {"start": v(302.5, 202.85) * mm, "mid": v(303.91, 203.43) * mm, "end": v(304.5, 204.85) * mm});
            skLineSegment(sketch, "E18.15.9.0", {"start": v(295.5, 170.2) * mm, "end": v(295.5, 186.03) * mm});
            skLineSegment(sketch, "E18.15.9.1", {"start": v(304.5, 170.2) * mm, "end": v(304.5, 186.03) * mm});
            skPoint(sketch, "E18.15.9.2", {"position": v(304.5, 168.2) * mm});
            skPoint(sketch, "E18.15.9.3", {"position": v(295.5, 168.2) * mm});
            skLineSegment(sketch, "E18.15.9.4", {"start": v(295.5, 186.03) * mm, "end": v(304.5, 186.03) * mm});
            skArc(sketch, "E18.15.9.5", {"start": v(295.5, 170.2) * mm, "mid": v(296.09, 168.8) * mm, "end": v(297.5, 168.2) * mm});
            skLineSegment(sketch, "E18.15.9.6", {"start": v(297.5, 168.2) * mm, "end": v(302.5, 168.2) * mm});
            skArc(sketch, "E18.15.9.7", {"start": v(302.5, 168.2) * mm, "mid": v(303.91, 168.8) * mm, "end": v(304.5, 170.2) * mm});
            skLineSegment(sketch, "E18.15.10.0", {"start": v(295.5, 135.56) * mm, "end": v(295.5, 151.38) * mm});
            skLineSegment(sketch, "E18.15.10.1", {"start": v(304.5, 135.56) * mm, "end": v(304.5, 151.38) * mm});
            skPoint(sketch, "E18.15.10.2", {"position": v(304.5, 133.56) * mm});
            skPoint(sketch, "E18.15.10.3", {"position": v(295.5, 133.56) * mm});
            skLineSegment(sketch, "E18.15.10.4", {"start": v(295.5, 151.38) * mm, "end": v(304.5, 151.38) * mm});
            skArc(sketch, "E18.15.10.5", {"start": v(295.5, 135.56) * mm, "mid": v(296.09, 134.15) * mm, "end": v(297.5, 133.56) * mm});
            skLineSegment(sketch, "E18.15.10.6", {"start": v(297.5, 133.56) * mm, "end": v(302.5, 133.56) * mm});
            skArc(sketch, "E18.15.10.7", {"start": v(302.5, 133.56) * mm, "mid": v(303.91, 134.15) * mm, "end": v(304.5, 135.56) * mm});
            skLineSegment(sketch, "E18.15.11.0", {"start": v(295.5, 100.92) * mm, "end": v(295.5, 116.74) * mm});
            skLineSegment(sketch, "E18.15.11.1", {"start": v(304.5, 100.92) * mm, "end": v(304.5, 116.74) * mm});
            skPoint(sketch, "E18.15.11.2", {"position": v(304.5, 98.92) * mm});
            skPoint(sketch, "E18.15.11.3", {"position": v(295.5, 98.92) * mm});
            skLineSegment(sketch, "E18.15.11.4", {"start": v(295.5, 116.74) * mm, "end": v(304.5, 116.74) * mm});
            skArc(sketch, "E18.15.11.5", {"start": v(295.5, 100.92) * mm, "mid": v(296.09, 99.5) * mm, "end": v(297.5, 98.92) * mm});
            skLineSegment(sketch, "E18.15.11.6", {"start": v(297.5, 98.92) * mm, "end": v(302.5, 98.92) * mm});
            skArc(sketch, "E18.15.11.7", {"start": v(302.5, 98.92) * mm, "mid": v(303.91, 99.5) * mm, "end": v(304.5, 100.92) * mm});
            skLineSegment(sketch, "E18.15.12.0", {"start": v(295.5, 66.28) * mm, "end": v(295.5, 82.1) * mm});
            skLineSegment(sketch, "E18.15.12.1", {"start": v(304.5, 66.28) * mm, "end": v(304.5, 82.1) * mm});
            skPoint(sketch, "E18.15.12.2", {"position": v(304.5, 64.28) * mm});
            skPoint(sketch, "E18.15.12.3", {"position": v(295.5, 64.28) * mm});
            skLineSegment(sketch, "E18.15.12.4", {"start": v(295.5, 82.1) * mm, "end": v(304.5, 82.1) * mm});
            skArc(sketch, "E18.15.12.5", {"start": v(295.5, 66.28) * mm, "mid": v(296.09, 64.87) * mm, "end": v(297.5, 64.28) * mm});
            skLineSegment(sketch, "E18.15.12.6", {"start": v(297.5, 64.28) * mm, "end": v(302.5, 64.28) * mm});
            skArc(sketch, "E18.15.12.7", {"start": v(302.5, 64.28) * mm, "mid": v(303.91, 64.87) * mm, "end": v(304.5, 66.28) * mm});
            skLineSegment(sketch, "E18.15.13.0", {"start": v(295.5, 31.64) * mm, "end": v(295.5, 47.46) * mm});
            skLineSegment(sketch, "E18.15.13.1", {"start": v(304.5, 31.64) * mm, "end": v(304.5, 47.46) * mm});
            skPoint(sketch, "E18.15.13.2", {"position": v(304.5, 29.64) * mm});
            skPoint(sketch, "E18.15.13.3", {"position": v(295.5, 29.64) * mm});
            skLineSegment(sketch, "E18.15.13.4", {"start": v(295.5, 47.46) * mm, "end": v(304.5, 47.46) * mm});
            skArc(sketch, "E18.15.13.5", {"start": v(295.5, 31.64) * mm, "mid": v(296.09, 30.23) * mm, "end": v(297.5, 29.64) * mm});
            skLineSegment(sketch, "E18.15.13.6", {"start": v(297.5, 29.64) * mm, "end": v(302.5, 29.64) * mm});
            skArc(sketch, "E18.15.13.7", {"start": v(302.5, 29.64) * mm, "mid": v(303.91, 30.23) * mm, "end": v(304.5, 31.64) * mm});
            skLineSegment(sketch, "E18.15.14.0", {"start": v(295.5, -3) * mm, "end": v(295.5, 12.82) * mm});
            skLineSegment(sketch, "E18.15.14.1", {"start": v(304.5, -3) * mm, "end": v(304.5, 12.82) * mm});
            skPoint(sketch, "E18.15.14.2", {"position": v(304.5, -5) * mm});
            skPoint(sketch, "E18.15.14.3", {"position": v(295.5, -5) * mm});
            skLineSegment(sketch, "E18.15.14.4", {"start": v(295.5, 12.82) * mm, "end": v(304.5, 12.82) * mm});
            skArc(sketch, "E18.15.14.5", {"start": v(295.5, -3) * mm, "mid": v(296.09, -4.41) * mm, "end": v(297.5, -5) * mm});
            skLineSegment(sketch, "E18.15.14.6", {"start": v(297.5, -5) * mm, "end": v(302.5, -5) * mm});
            skArc(sketch, "E18.15.14.7", {"start": v(302.5, -5) * mm, "mid": v(303.91, -4.41) * mm, "end": v(304.5, -3) * mm});
            skLineSegment(sketch, "E18.16.0.0", {"start": v(315.5, 481.97) * mm, "end": v(315.5, 497.8) * mm});
            skLineSegment(sketch, "E18.16.0.1", {"start": v(324.5, 481.97) * mm, "end": v(324.5, 497.8) * mm});
            skPoint(sketch, "E18.16.0.2", {"position": v(324.5, 479.97) * mm});
            skPoint(sketch, "E18.16.0.3", {"position": v(315.5, 479.97) * mm});
            skLineSegment(sketch, "E18.16.0.4", {"start": v(315.5, 497.8) * mm, "end": v(324.5, 497.8) * mm});
            skArc(sketch, "E18.16.0.5", {"start": v(315.5, 481.97) * mm, "mid": v(316.09, 480.56) * mm, "end": v(317.5, 479.97) * mm});
            skLineSegment(sketch, "E18.16.0.6", {"start": v(317.5, 479.97) * mm, "end": v(322.5, 479.97) * mm});
            skArc(sketch, "E18.16.0.7", {"start": v(322.5, 479.97) * mm, "mid": v(323.91, 480.56) * mm, "end": v(324.5, 481.97) * mm});
            skLineSegment(sketch, "E18.16.1.0", {"start": v(315.5, 447.33) * mm, "end": v(315.5, 463.15) * mm});
            skLineSegment(sketch, "E18.16.1.1", {"start": v(324.5, 447.33) * mm, "end": v(324.5, 463.15) * mm});
            skPoint(sketch, "E18.16.1.2", {"position": v(324.5, 445.33) * mm});
            skPoint(sketch, "E18.16.1.3", {"position": v(315.5, 445.33) * mm});
            skLineSegment(sketch, "E18.16.1.4", {"start": v(315.5, 463.15) * mm, "end": v(324.5, 463.15) * mm});
            skArc(sketch, "E18.16.1.5", {"start": v(315.5, 447.33) * mm, "mid": v(316.09, 445.92) * mm, "end": v(317.5, 445.33) * mm});
            skLineSegment(sketch, "E18.16.1.6", {"start": v(317.5, 445.33) * mm, "end": v(322.5, 445.33) * mm});
            skArc(sketch, "E18.16.1.7", {"start": v(322.5, 445.33) * mm, "mid": v(323.91, 445.92) * mm, "end": v(324.5, 447.33) * mm});
            skLineSegment(sketch, "E18.16.2.0", {"start": v(315.5, 412.7) * mm, "end": v(315.5, 428.51) * mm});
            skLineSegment(sketch, "E18.16.2.1", {"start": v(324.5, 412.7) * mm, "end": v(324.5, 428.51) * mm});
            skPoint(sketch, "E18.16.2.2", {"position": v(324.5, 410.7) * mm});
            skPoint(sketch, "E18.16.2.3", {"position": v(315.5, 410.7) * mm});
            skLineSegment(sketch, "E18.16.2.4", {"start": v(315.5, 428.51) * mm, "end": v(324.5, 428.51) * mm});
            skArc(sketch, "E18.16.2.5", {"start": v(315.5, 412.7) * mm, "mid": v(316.09, 411.28) * mm, "end": v(317.5, 410.7) * mm});
            skLineSegment(sketch, "E18.16.2.6", {"start": v(317.5, 410.7) * mm, "end": v(322.5, 410.7) * mm});
            skArc(sketch, "E18.16.2.7", {"start": v(322.5, 410.7) * mm, "mid": v(323.91, 411.28) * mm, "end": v(324.5, 412.7) * mm});
            skLineSegment(sketch, "E18.16.3.0", {"start": v(315.5, 378.05) * mm, "end": v(315.5, 393.87) * mm});
            skLineSegment(sketch, "E18.16.3.1", {"start": v(324.5, 378.05) * mm, "end": v(324.5, 393.87) * mm});
            skPoint(sketch, "E18.16.3.2", {"position": v(324.5, 376.05) * mm});
            skPoint(sketch, "E18.16.3.3", {"position": v(315.5, 376.05) * mm});
            skLineSegment(sketch, "E18.16.3.4", {"start": v(315.5, 393.87) * mm, "end": v(324.5, 393.87) * mm});
            skArc(sketch, "E18.16.3.5", {"start": v(315.5, 378.05) * mm, "mid": v(316.09, 376.64) * mm, "end": v(317.5, 376.05) * mm});
            skLineSegment(sketch, "E18.16.3.6", {"start": v(317.5, 376.05) * mm, "end": v(322.5, 376.05) * mm});
            skArc(sketch, "E18.16.3.7", {"start": v(322.5, 376.05) * mm, "mid": v(323.91, 376.64) * mm, "end": v(324.5, 378.05) * mm});
            skLineSegment(sketch, "E18.16.4.0", {"start": v(315.5, 343.41) * mm, "end": v(315.5, 359.23) * mm});
            skLineSegment(sketch, "E18.16.4.1", {"start": v(324.5, 343.41) * mm, "end": v(324.5, 359.23) * mm});
            skPoint(sketch, "E18.16.4.2", {"position": v(324.5, 341.41) * mm});
            skPoint(sketch, "E18.16.4.3", {"position": v(315.5, 341.41) * mm});
            skLineSegment(sketch, "E18.16.4.4", {"start": v(315.5, 359.23) * mm, "end": v(324.5, 359.23) * mm});
            skArc(sketch, "E18.16.4.5", {"start": v(315.5, 343.41) * mm, "mid": v(316.09, 342) * mm, "end": v(317.5, 341.41) * mm});
            skLineSegment(sketch, "E18.16.4.6", {"start": v(317.5, 341.41) * mm, "end": v(322.5, 341.41) * mm});
            skArc(sketch, "E18.16.4.7", {"start": v(322.5, 341.41) * mm, "mid": v(323.91, 342) * mm, "end": v(324.5, 343.41) * mm});
            skLineSegment(sketch, "E18.16.5.0", {"start": v(315.5, 308.77) * mm, "end": v(315.5, 324.59) * mm});
            skLineSegment(sketch, "E18.16.5.1", {"start": v(324.5, 308.77) * mm, "end": v(324.5, 324.59) * mm});
            skPoint(sketch, "E18.16.5.2", {"position": v(324.5, 306.77) * mm});
            skPoint(sketch, "E18.16.5.3", {"position": v(315.5, 306.77) * mm});
            skLineSegment(sketch, "E18.16.5.4", {"start": v(315.5, 324.59) * mm, "end": v(324.5, 324.59) * mm});
            skArc(sketch, "E18.16.5.5", {"start": v(315.5, 308.77) * mm, "mid": v(316.09, 307.35) * mm, "end": v(317.5, 306.77) * mm});
            skLineSegment(sketch, "E18.16.5.6", {"start": v(317.5, 306.77) * mm, "end": v(322.5, 306.77) * mm});
            skArc(sketch, "E18.16.5.7", {"start": v(322.5, 306.77) * mm, "mid": v(323.91, 307.35) * mm, "end": v(324.5, 308.77) * mm});
            skLineSegment(sketch, "E18.16.6.0", {"start": v(315.5, 274.13) * mm, "end": v(315.5, 289.95) * mm});
            skLineSegment(sketch, "E18.16.6.1", {"start": v(324.5, 274.13) * mm, "end": v(324.5, 289.95) * mm});
            skPoint(sketch, "E18.16.6.2", {"position": v(324.5, 272.13) * mm});
            skPoint(sketch, "E18.16.6.3", {"position": v(315.5, 272.13) * mm});
            skLineSegment(sketch, "E18.16.6.4", {"start": v(315.5, 289.95) * mm, "end": v(324.5, 289.95) * mm});
            skArc(sketch, "E18.16.6.5", {"start": v(315.5, 274.13) * mm, "mid": v(316.09, 272.71) * mm, "end": v(317.5, 272.13) * mm});
            skLineSegment(sketch, "E18.16.6.6", {"start": v(317.5, 272.13) * mm, "end": v(322.5, 272.13) * mm});
            skArc(sketch, "E18.16.6.7", {"start": v(322.5, 272.13) * mm, "mid": v(323.91, 272.71) * mm, "end": v(324.5, 274.13) * mm});
            skLineSegment(sketch, "E18.16.7.0", {"start": v(315.5, 239.49) * mm, "end": v(315.5, 255.3) * mm});
            skLineSegment(sketch, "E18.16.7.1", {"start": v(324.5, 239.49) * mm, "end": v(324.5, 255.3) * mm});
            skPoint(sketch, "E18.16.7.2", {"position": v(324.5, 237.49) * mm});
            skPoint(sketch, "E18.16.7.3", {"position": v(315.5, 237.49) * mm});
            skLineSegment(sketch, "E18.16.7.4", {"start": v(315.5, 255.3) * mm, "end": v(324.5, 255.3) * mm});
            skArc(sketch, "E18.16.7.5", {"start": v(315.5, 239.49) * mm, "mid": v(316.09, 238.07) * mm, "end": v(317.5, 237.49) * mm});
            skLineSegment(sketch, "E18.16.7.6", {"start": v(317.5, 237.49) * mm, "end": v(322.5, 237.49) * mm});
            skArc(sketch, "E18.16.7.7", {"start": v(322.5, 237.49) * mm, "mid": v(323.91, 238.07) * mm, "end": v(324.5, 239.49) * mm});
            skLineSegment(sketch, "E18.16.8.0", {"start": v(315.5, 204.85) * mm, "end": v(315.5, 220.67) * mm});
            skLineSegment(sketch, "E18.16.8.1", {"start": v(324.5, 204.85) * mm, "end": v(324.5, 220.67) * mm});
            skPoint(sketch, "E18.16.8.2", {"position": v(324.5, 202.85) * mm});
            skPoint(sketch, "E18.16.8.3", {"position": v(315.5, 202.85) * mm});
            skLineSegment(sketch, "E18.16.8.4", {"start": v(315.5, 220.67) * mm, "end": v(324.5, 220.67) * mm});
            skArc(sketch, "E18.16.8.5", {"start": v(315.5, 204.85) * mm, "mid": v(316.09, 203.43) * mm, "end": v(317.5, 202.85) * mm});
            skLineSegment(sketch, "E18.16.8.6", {"start": v(317.5, 202.85) * mm, "end": v(322.5, 202.85) * mm});
            skArc(sketch, "E18.16.8.7", {"start": v(322.5, 202.85) * mm, "mid": v(323.91, 203.43) * mm, "end": v(324.5, 204.85) * mm});
            skLineSegment(sketch, "E18.16.9.0", {"start": v(315.5, 170.2) * mm, "end": v(315.5, 186.03) * mm});
            skLineSegment(sketch, "E18.16.9.1", {"start": v(324.5, 170.2) * mm, "end": v(324.5, 186.03) * mm});
            skPoint(sketch, "E18.16.9.2", {"position": v(324.5, 168.2) * mm});
            skPoint(sketch, "E18.16.9.3", {"position": v(315.5, 168.2) * mm});
            skLineSegment(sketch, "E18.16.9.4", {"start": v(315.5, 186.03) * mm, "end": v(324.5, 186.03) * mm});
            skArc(sketch, "E18.16.9.5", {"start": v(315.5, 170.2) * mm, "mid": v(316.09, 168.8) * mm, "end": v(317.5, 168.2) * mm});
            skLineSegment(sketch, "E18.16.9.6", {"start": v(317.5, 168.2) * mm, "end": v(322.5, 168.2) * mm});
            skArc(sketch, "E18.16.9.7", {"start": v(322.5, 168.2) * mm, "mid": v(323.91, 168.8) * mm, "end": v(324.5, 170.2) * mm});
            skLineSegment(sketch, "E18.16.10.0", {"start": v(315.5, 135.56) * mm, "end": v(315.5, 151.38) * mm});
            skLineSegment(sketch, "E18.16.10.1", {"start": v(324.5, 135.56) * mm, "end": v(324.5, 151.38) * mm});
            skPoint(sketch, "E18.16.10.2", {"position": v(324.5, 133.56) * mm});
            skPoint(sketch, "E18.16.10.3", {"position": v(315.5, 133.56) * mm});
            skLineSegment(sketch, "E18.16.10.4", {"start": v(315.5, 151.38) * mm, "end": v(324.5, 151.38) * mm});
            skArc(sketch, "E18.16.10.5", {"start": v(315.5, 135.56) * mm, "mid": v(316.09, 134.15) * mm, "end": v(317.5, 133.56) * mm});
            skLineSegment(sketch, "E18.16.10.6", {"start": v(317.5, 133.56) * mm, "end": v(322.5, 133.56) * mm});
            skArc(sketch, "E18.16.10.7", {"start": v(322.5, 133.56) * mm, "mid": v(323.91, 134.15) * mm, "end": v(324.5, 135.56) * mm});
            skLineSegment(sketch, "E18.16.11.0", {"start": v(315.5, 100.92) * mm, "end": v(315.5, 116.74) * mm});
            skLineSegment(sketch, "E18.16.11.1", {"start": v(324.5, 100.92) * mm, "end": v(324.5, 116.74) * mm});
            skPoint(sketch, "E18.16.11.2", {"position": v(324.5, 98.92) * mm});
            skPoint(sketch, "E18.16.11.3", {"position": v(315.5, 98.92) * mm});
            skLineSegment(sketch, "E18.16.11.4", {"start": v(315.5, 116.74) * mm, "end": v(324.5, 116.74) * mm});
            skArc(sketch, "E18.16.11.5", {"start": v(315.5, 100.92) * mm, "mid": v(316.09, 99.5) * mm, "end": v(317.5, 98.92) * mm});
            skLineSegment(sketch, "E18.16.11.6", {"start": v(317.5, 98.92) * mm, "end": v(322.5, 98.92) * mm});
            skArc(sketch, "E18.16.11.7", {"start": v(322.5, 98.92) * mm, "mid": v(323.91, 99.5) * mm, "end": v(324.5, 100.92) * mm});
            skLineSegment(sketch, "E18.16.12.0", {"start": v(315.5, 66.28) * mm, "end": v(315.5, 82.1) * mm});
            skLineSegment(sketch, "E18.16.12.1", {"start": v(324.5, 66.28) * mm, "end": v(324.5, 82.1) * mm});
            skPoint(sketch, "E18.16.12.2", {"position": v(324.5, 64.28) * mm});
            skPoint(sketch, "E18.16.12.3", {"position": v(315.5, 64.28) * mm});
            skLineSegment(sketch, "E18.16.12.4", {"start": v(315.5, 82.1) * mm, "end": v(324.5, 82.1) * mm});
            skArc(sketch, "E18.16.12.5", {"start": v(315.5, 66.28) * mm, "mid": v(316.09, 64.87) * mm, "end": v(317.5, 64.28) * mm});
            skLineSegment(sketch, "E18.16.12.6", {"start": v(317.5, 64.28) * mm, "end": v(322.5, 64.28) * mm});
            skArc(sketch, "E18.16.12.7", {"start": v(322.5, 64.28) * mm, "mid": v(323.91, 64.87) * mm, "end": v(324.5, 66.28) * mm});
            skLineSegment(sketch, "E18.16.13.0", {"start": v(315.5, 31.64) * mm, "end": v(315.5, 47.46) * mm});
            skLineSegment(sketch, "E18.16.13.1", {"start": v(324.5, 31.64) * mm, "end": v(324.5, 47.46) * mm});
            skPoint(sketch, "E18.16.13.2", {"position": v(324.5, 29.64) * mm});
            skPoint(sketch, "E18.16.13.3", {"position": v(315.5, 29.64) * mm});
            skLineSegment(sketch, "E18.16.13.4", {"start": v(315.5, 47.46) * mm, "end": v(324.5, 47.46) * mm});
            skArc(sketch, "E18.16.13.5", {"start": v(315.5, 31.64) * mm, "mid": v(316.09, 30.23) * mm, "end": v(317.5, 29.64) * mm});
            skLineSegment(sketch, "E18.16.13.6", {"start": v(317.5, 29.64) * mm, "end": v(322.5, 29.64) * mm});
            skArc(sketch, "E18.16.13.7", {"start": v(322.5, 29.64) * mm, "mid": v(323.91, 30.23) * mm, "end": v(324.5, 31.64) * mm});
            skLineSegment(sketch, "E18.16.14.0", {"start": v(315.5, -3) * mm, "end": v(315.5, 12.82) * mm});
            skLineSegment(sketch, "E18.16.14.1", {"start": v(324.5, -3) * mm, "end": v(324.5, 12.82) * mm});
            skPoint(sketch, "E18.16.14.2", {"position": v(324.5, -5) * mm});
            skPoint(sketch, "E18.16.14.3", {"position": v(315.5, -5) * mm});
            skLineSegment(sketch, "E18.16.14.4", {"start": v(315.5, 12.82) * mm, "end": v(324.5, 12.82) * mm});
            skArc(sketch, "E18.16.14.5", {"start": v(315.5, -3) * mm, "mid": v(316.09, -4.41) * mm, "end": v(317.5, -5) * mm});
            skLineSegment(sketch, "E18.16.14.6", {"start": v(317.5, -5) * mm, "end": v(322.5, -5) * mm});
            skArc(sketch, "E18.16.14.7", {"start": v(322.5, -5) * mm, "mid": v(323.91, -4.41) * mm, "end": v(324.5, -3) * mm});
            skLineSegment(sketch, "E18.17.0.0", {"start": v(335.5, 481.97) * mm, "end": v(335.5, 497.8) * mm});
            skLineSegment(sketch, "E18.17.0.1", {"start": v(344.5, 481.97) * mm, "end": v(344.5, 497.8) * mm});
            skPoint(sketch, "E18.17.0.2", {"position": v(344.5, 479.97) * mm});
            skPoint(sketch, "E18.17.0.3", {"position": v(335.5, 479.97) * mm});
            skLineSegment(sketch, "E18.17.0.4", {"start": v(335.5, 497.8) * mm, "end": v(344.5, 497.8) * mm});
            skArc(sketch, "E18.17.0.5", {"start": v(335.5, 481.97) * mm, "mid": v(336.09, 480.56) * mm, "end": v(337.5, 479.97) * mm});
            skLineSegment(sketch, "E18.17.0.6", {"start": v(337.5, 479.97) * mm, "end": v(342.5, 479.97) * mm});
            skArc(sketch, "E18.17.0.7", {"start": v(342.5, 479.97) * mm, "mid": v(343.91, 480.56) * mm, "end": v(344.5, 481.97) * mm});
            skLineSegment(sketch, "E18.17.1.0", {"start": v(335.5, 447.33) * mm, "end": v(335.5, 463.15) * mm});
            skLineSegment(sketch, "E18.17.1.1", {"start": v(344.5, 447.33) * mm, "end": v(344.5, 463.15) * mm});
            skPoint(sketch, "E18.17.1.2", {"position": v(344.5, 445.33) * mm});
            skPoint(sketch, "E18.17.1.3", {"position": v(335.5, 445.33) * mm});
            skLineSegment(sketch, "E18.17.1.4", {"start": v(335.5, 463.15) * mm, "end": v(344.5, 463.15) * mm});
            skArc(sketch, "E18.17.1.5", {"start": v(335.5, 447.33) * mm, "mid": v(336.09, 445.92) * mm, "end": v(337.5, 445.33) * mm});
            skLineSegment(sketch, "E18.17.1.6", {"start": v(337.5, 445.33) * mm, "end": v(342.5, 445.33) * mm});
            skArc(sketch, "E18.17.1.7", {"start": v(342.5, 445.33) * mm, "mid": v(343.91, 445.92) * mm, "end": v(344.5, 447.33) * mm});
            skLineSegment(sketch, "E18.17.2.0", {"start": v(335.5, 412.7) * mm, "end": v(335.5, 428.51) * mm});
            skLineSegment(sketch, "E18.17.2.1", {"start": v(344.5, 412.7) * mm, "end": v(344.5, 428.51) * mm});
            skPoint(sketch, "E18.17.2.2", {"position": v(344.5, 410.7) * mm});
            skPoint(sketch, "E18.17.2.3", {"position": v(335.5, 410.7) * mm});
            skLineSegment(sketch, "E18.17.2.4", {"start": v(335.5, 428.51) * mm, "end": v(344.5, 428.51) * mm});
            skArc(sketch, "E18.17.2.5", {"start": v(335.5, 412.7) * mm, "mid": v(336.09, 411.28) * mm, "end": v(337.5, 410.7) * mm});
            skLineSegment(sketch, "E18.17.2.6", {"start": v(337.5, 410.7) * mm, "end": v(342.5, 410.7) * mm});
            skArc(sketch, "E18.17.2.7", {"start": v(342.5, 410.7) * mm, "mid": v(343.91, 411.28) * mm, "end": v(344.5, 412.7) * mm});
            skLineSegment(sketch, "E18.17.3.0", {"start": v(335.5, 378.05) * mm, "end": v(335.5, 393.87) * mm});
            skLineSegment(sketch, "E18.17.3.1", {"start": v(344.5, 378.05) * mm, "end": v(344.5, 393.87) * mm});
            skPoint(sketch, "E18.17.3.2", {"position": v(344.5, 376.05) * mm});
            skPoint(sketch, "E18.17.3.3", {"position": v(335.5, 376.05) * mm});
            skLineSegment(sketch, "E18.17.3.4", {"start": v(335.5, 393.87) * mm, "end": v(344.5, 393.87) * mm});
            skArc(sketch, "E18.17.3.5", {"start": v(335.5, 378.05) * mm, "mid": v(336.09, 376.64) * mm, "end": v(337.5, 376.05) * mm});
            skLineSegment(sketch, "E18.17.3.6", {"start": v(337.5, 376.05) * mm, "end": v(342.5, 376.05) * mm});
            skArc(sketch, "E18.17.3.7", {"start": v(342.5, 376.05) * mm, "mid": v(343.91, 376.64) * mm, "end": v(344.5, 378.05) * mm});
            skLineSegment(sketch, "E18.17.4.0", {"start": v(335.5, 343.41) * mm, "end": v(335.5, 359.23) * mm});
            skLineSegment(sketch, "E18.17.4.1", {"start": v(344.5, 343.41) * mm, "end": v(344.5, 359.23) * mm});
            skPoint(sketch, "E18.17.4.2", {"position": v(344.5, 341.41) * mm});
            skPoint(sketch, "E18.17.4.3", {"position": v(335.5, 341.41) * mm});
            skLineSegment(sketch, "E18.17.4.4", {"start": v(335.5, 359.23) * mm, "end": v(344.5, 359.23) * mm});
            skArc(sketch, "E18.17.4.5", {"start": v(335.5, 343.41) * mm, "mid": v(336.09, 342) * mm, "end": v(337.5, 341.41) * mm});
            skLineSegment(sketch, "E18.17.4.6", {"start": v(337.5, 341.41) * mm, "end": v(342.5, 341.41) * mm});
            skArc(sketch, "E18.17.4.7", {"start": v(342.5, 341.41) * mm, "mid": v(343.91, 342) * mm, "end": v(344.5, 343.41) * mm});
            skLineSegment(sketch, "E18.17.5.0", {"start": v(335.5, 308.77) * mm, "end": v(335.5, 324.59) * mm});
            skLineSegment(sketch, "E18.17.5.1", {"start": v(344.5, 308.77) * mm, "end": v(344.5, 324.59) * mm});
            skPoint(sketch, "E18.17.5.2", {"position": v(344.5, 306.77) * mm});
            skPoint(sketch, "E18.17.5.3", {"position": v(335.5, 306.77) * mm});
            skLineSegment(sketch, "E18.17.5.4", {"start": v(335.5, 324.59) * mm, "end": v(344.5, 324.59) * mm});
            skArc(sketch, "E18.17.5.5", {"start": v(335.5, 308.77) * mm, "mid": v(336.09, 307.35) * mm, "end": v(337.5, 306.77) * mm});
            skLineSegment(sketch, "E18.17.5.6", {"start": v(337.5, 306.77) * mm, "end": v(342.5, 306.77) * mm});
            skArc(sketch, "E18.17.5.7", {"start": v(342.5, 306.77) * mm, "mid": v(343.91, 307.35) * mm, "end": v(344.5, 308.77) * mm});
            skLineSegment(sketch, "E18.17.6.0", {"start": v(335.5, 274.13) * mm, "end": v(335.5, 289.95) * mm});
            skLineSegment(sketch, "E18.17.6.1", {"start": v(344.5, 274.13) * mm, "end": v(344.5, 289.95) * mm});
            skPoint(sketch, "E18.17.6.2", {"position": v(344.5, 272.13) * mm});
            skPoint(sketch, "E18.17.6.3", {"position": v(335.5, 272.13) * mm});
            skLineSegment(sketch, "E18.17.6.4", {"start": v(335.5, 289.95) * mm, "end": v(344.5, 289.95) * mm});
            skArc(sketch, "E18.17.6.5", {"start": v(335.5, 274.13) * mm, "mid": v(336.09, 272.71) * mm, "end": v(337.5, 272.13) * mm});
            skLineSegment(sketch, "E18.17.6.6", {"start": v(337.5, 272.13) * mm, "end": v(342.5, 272.13) * mm});
            skArc(sketch, "E18.17.6.7", {"start": v(342.5, 272.13) * mm, "mid": v(343.91, 272.71) * mm, "end": v(344.5, 274.13) * mm});
            skLineSegment(sketch, "E18.17.7.0", {"start": v(335.5, 239.49) * mm, "end": v(335.5, 255.3) * mm});
            skLineSegment(sketch, "E18.17.7.1", {"start": v(344.5, 239.49) * mm, "end": v(344.5, 255.3) * mm});
            skPoint(sketch, "E18.17.7.2", {"position": v(344.5, 237.49) * mm});
            skPoint(sketch, "E18.17.7.3", {"position": v(335.5, 237.49) * mm});
            skLineSegment(sketch, "E18.17.7.4", {"start": v(335.5, 255.3) * mm, "end": v(344.5, 255.3) * mm});
            skArc(sketch, "E18.17.7.5", {"start": v(335.5, 239.49) * mm, "mid": v(336.09, 238.07) * mm, "end": v(337.5, 237.49) * mm});
            skLineSegment(sketch, "E18.17.7.6", {"start": v(337.5, 237.49) * mm, "end": v(342.5, 237.49) * mm});
            skArc(sketch, "E18.17.7.7", {"start": v(342.5, 237.49) * mm, "mid": v(343.91, 238.07) * mm, "end": v(344.5, 239.49) * mm});
            skLineSegment(sketch, "E18.17.8.0", {"start": v(335.5, 204.85) * mm, "end": v(335.5, 220.67) * mm});
            skLineSegment(sketch, "E18.17.8.1", {"start": v(344.5, 204.85) * mm, "end": v(344.5, 220.67) * mm});
            skPoint(sketch, "E18.17.8.2", {"position": v(344.5, 202.85) * mm});
            skPoint(sketch, "E18.17.8.3", {"position": v(335.5, 202.85) * mm});
            skLineSegment(sketch, "E18.17.8.4", {"start": v(335.5, 220.67) * mm, "end": v(344.5, 220.67) * mm});
            skArc(sketch, "E18.17.8.5", {"start": v(335.5, 204.85) * mm, "mid": v(336.09, 203.43) * mm, "end": v(337.5, 202.85) * mm});
            skLineSegment(sketch, "E18.17.8.6", {"start": v(337.5, 202.85) * mm, "end": v(342.5, 202.85) * mm});
            skArc(sketch, "E18.17.8.7", {"start": v(342.5, 202.85) * mm, "mid": v(343.91, 203.43) * mm, "end": v(344.5, 204.85) * mm});
            skLineSegment(sketch, "E18.17.9.0", {"start": v(335.5, 170.2) * mm, "end": v(335.5, 186.03) * mm});
            skLineSegment(sketch, "E18.17.9.1", {"start": v(344.5, 170.2) * mm, "end": v(344.5, 186.03) * mm});
            skPoint(sketch, "E18.17.9.2", {"position": v(344.5, 168.2) * mm});
            skPoint(sketch, "E18.17.9.3", {"position": v(335.5, 168.2) * mm});
            skLineSegment(sketch, "E18.17.9.4", {"start": v(335.5, 186.03) * mm, "end": v(344.5, 186.03) * mm});
            skArc(sketch, "E18.17.9.5", {"start": v(335.5, 170.2) * mm, "mid": v(336.09, 168.8) * mm, "end": v(337.5, 168.2) * mm});
            skLineSegment(sketch, "E18.17.9.6", {"start": v(337.5, 168.2) * mm, "end": v(342.5, 168.2) * mm});
            skArc(sketch, "E18.17.9.7", {"start": v(342.5, 168.2) * mm, "mid": v(343.91, 168.8) * mm, "end": v(344.5, 170.2) * mm});
            skLineSegment(sketch, "E18.17.10.0", {"start": v(335.5, 135.56) * mm, "end": v(335.5, 151.38) * mm});
            skLineSegment(sketch, "E18.17.10.1", {"start": v(344.5, 135.56) * mm, "end": v(344.5, 151.38) * mm});
            skPoint(sketch, "E18.17.10.2", {"position": v(344.5, 133.56) * mm});
            skPoint(sketch, "E18.17.10.3", {"position": v(335.5, 133.56) * mm});
            skLineSegment(sketch, "E18.17.10.4", {"start": v(335.5, 151.38) * mm, "end": v(344.5, 151.38) * mm});
            skArc(sketch, "E18.17.10.5", {"start": v(335.5, 135.56) * mm, "mid": v(336.09, 134.15) * mm, "end": v(337.5, 133.56) * mm});
            skLineSegment(sketch, "E18.17.10.6", {"start": v(337.5, 133.56) * mm, "end": v(342.5, 133.56) * mm});
            skArc(sketch, "E18.17.10.7", {"start": v(342.5, 133.56) * mm, "mid": v(343.91, 134.15) * mm, "end": v(344.5, 135.56) * mm});
            skLineSegment(sketch, "E18.17.11.0", {"start": v(335.5, 100.92) * mm, "end": v(335.5, 116.74) * mm});
            skLineSegment(sketch, "E18.17.11.1", {"start": v(344.5, 100.92) * mm, "end": v(344.5, 116.74) * mm});
            skPoint(sketch, "E18.17.11.2", {"position": v(344.5, 98.92) * mm});
            skPoint(sketch, "E18.17.11.3", {"position": v(335.5, 98.92) * mm});
            skLineSegment(sketch, "E18.17.11.4", {"start": v(335.5, 116.74) * mm, "end": v(344.5, 116.74) * mm});
            skArc(sketch, "E18.17.11.5", {"start": v(335.5, 100.92) * mm, "mid": v(336.09, 99.5) * mm, "end": v(337.5, 98.92) * mm});
            skLineSegment(sketch, "E18.17.11.6", {"start": v(337.5, 98.92) * mm, "end": v(342.5, 98.92) * mm});
            skArc(sketch, "E18.17.11.7", {"start": v(342.5, 98.92) * mm, "mid": v(343.91, 99.5) * mm, "end": v(344.5, 100.92) * mm});
            skLineSegment(sketch, "E18.17.12.0", {"start": v(335.5, 66.28) * mm, "end": v(335.5, 82.1) * mm});
            skLineSegment(sketch, "E18.17.12.1", {"start": v(344.5, 66.28) * mm, "end": v(344.5, 82.1) * mm});
            skPoint(sketch, "E18.17.12.2", {"position": v(344.5, 64.28) * mm});
            skPoint(sketch, "E18.17.12.3", {"position": v(335.5, 64.28) * mm});
            skLineSegment(sketch, "E18.17.12.4", {"start": v(335.5, 82.1) * mm, "end": v(344.5, 82.1) * mm});
            skArc(sketch, "E18.17.12.5", {"start": v(335.5, 66.28) * mm, "mid": v(336.09, 64.87) * mm, "end": v(337.5, 64.28) * mm});
            skLineSegment(sketch, "E18.17.12.6", {"start": v(337.5, 64.28) * mm, "end": v(342.5, 64.28) * mm});
            skArc(sketch, "E18.17.12.7", {"start": v(342.5, 64.28) * mm, "mid": v(343.91, 64.87) * mm, "end": v(344.5, 66.28) * mm});
            skLineSegment(sketch, "E18.17.13.0", {"start": v(335.5, 31.64) * mm, "end": v(335.5, 47.46) * mm});
            skLineSegment(sketch, "E18.17.13.1", {"start": v(344.5, 31.64) * mm, "end": v(344.5, 47.46) * mm});
            skPoint(sketch, "E18.17.13.2", {"position": v(344.5, 29.64) * mm});
            skPoint(sketch, "E18.17.13.3", {"position": v(335.5, 29.64) * mm});
            skLineSegment(sketch, "E18.17.13.4", {"start": v(335.5, 47.46) * mm, "end": v(344.5, 47.46) * mm});
            skArc(sketch, "E18.17.13.5", {"start": v(335.5, 31.64) * mm, "mid": v(336.09, 30.23) * mm, "end": v(337.5, 29.64) * mm});
            skLineSegment(sketch, "E18.17.13.6", {"start": v(337.5, 29.64) * mm, "end": v(342.5, 29.64) * mm});
            skArc(sketch, "E18.17.13.7", {"start": v(342.5, 29.64) * mm, "mid": v(343.91, 30.23) * mm, "end": v(344.5, 31.64) * mm});
            skLineSegment(sketch, "E18.17.14.0", {"start": v(335.5, -3) * mm, "end": v(335.5, 12.82) * mm});
            skLineSegment(sketch, "E18.17.14.1", {"start": v(344.5, -3) * mm, "end": v(344.5, 12.82) * mm});
            skPoint(sketch, "E18.17.14.2", {"position": v(344.5, -5) * mm});
            skPoint(sketch, "E18.17.14.3", {"position": v(335.5, -5) * mm});
            skLineSegment(sketch, "E18.17.14.4", {"start": v(335.5, 12.82) * mm, "end": v(344.5, 12.82) * mm});
            skArc(sketch, "E18.17.14.5", {"start": v(335.5, -3) * mm, "mid": v(336.09, -4.41) * mm, "end": v(337.5, -5) * mm});
            skLineSegment(sketch, "E18.17.14.6", {"start": v(337.5, -5) * mm, "end": v(342.5, -5) * mm});
            skArc(sketch, "E18.17.14.7", {"start": v(342.5, -5) * mm, "mid": v(343.91, -4.41) * mm, "end": v(344.5, -3) * mm});
            skLineSegment(sketch, "E18.18.0.0", {"start": v(355.5, 481.97) * mm, "end": v(355.5, 497.8) * mm});
            skLineSegment(sketch, "E18.18.0.1", {"start": v(364.5, 481.97) * mm, "end": v(364.5, 497.8) * mm});
            skPoint(sketch, "E18.18.0.2", {"position": v(364.5, 479.97) * mm});
            skPoint(sketch, "E18.18.0.3", {"position": v(355.5, 479.97) * mm});
            skLineSegment(sketch, "E18.18.0.4", {"start": v(355.5, 497.8) * mm, "end": v(364.5, 497.8) * mm});
            skArc(sketch, "E18.18.0.5", {"start": v(355.5, 481.97) * mm, "mid": v(356.09, 480.56) * mm, "end": v(357.5, 479.97) * mm});
            skLineSegment(sketch, "E18.18.0.6", {"start": v(357.5, 479.97) * mm, "end": v(362.5, 479.97) * mm});
            skArc(sketch, "E18.18.0.7", {"start": v(362.5, 479.97) * mm, "mid": v(363.91, 480.56) * mm, "end": v(364.5, 481.97) * mm});
            skLineSegment(sketch, "E18.18.1.0", {"start": v(355.5, 447.33) * mm, "end": v(355.5, 463.15) * mm});
            skLineSegment(sketch, "E18.18.1.1", {"start": v(364.5, 447.33) * mm, "end": v(364.5, 463.15) * mm});
            skPoint(sketch, "E18.18.1.2", {"position": v(364.5, 445.33) * mm});
            skPoint(sketch, "E18.18.1.3", {"position": v(355.5, 445.33) * mm});
            skLineSegment(sketch, "E18.18.1.4", {"start": v(355.5, 463.15) * mm, "end": v(364.5, 463.15) * mm});
            skArc(sketch, "E18.18.1.5", {"start": v(355.5, 447.33) * mm, "mid": v(356.09, 445.92) * mm, "end": v(357.5, 445.33) * mm});
            skLineSegment(sketch, "E18.18.1.6", {"start": v(357.5, 445.33) * mm, "end": v(362.5, 445.33) * mm});
            skArc(sketch, "E18.18.1.7", {"start": v(362.5, 445.33) * mm, "mid": v(363.91, 445.92) * mm, "end": v(364.5, 447.33) * mm});
            skLineSegment(sketch, "E18.18.2.0", {"start": v(355.5, 412.7) * mm, "end": v(355.5, 428.51) * mm});
            skLineSegment(sketch, "E18.18.2.1", {"start": v(364.5, 412.7) * mm, "end": v(364.5, 428.51) * mm});
            skPoint(sketch, "E18.18.2.2", {"position": v(364.5, 410.7) * mm});
            skPoint(sketch, "E18.18.2.3", {"position": v(355.5, 410.7) * mm});
            skLineSegment(sketch, "E18.18.2.4", {"start": v(355.5, 428.51) * mm, "end": v(364.5, 428.51) * mm});
            skArc(sketch, "E18.18.2.5", {"start": v(355.5, 412.7) * mm, "mid": v(356.09, 411.28) * mm, "end": v(357.5, 410.7) * mm});
            skLineSegment(sketch, "E18.18.2.6", {"start": v(357.5, 410.7) * mm, "end": v(362.5, 410.7) * mm});
            skArc(sketch, "E18.18.2.7", {"start": v(362.5, 410.7) * mm, "mid": v(363.91, 411.28) * mm, "end": v(364.5, 412.7) * mm});
            skLineSegment(sketch, "E18.18.3.0", {"start": v(355.5, 378.05) * mm, "end": v(355.5, 393.87) * mm});
            skLineSegment(sketch, "E18.18.3.1", {"start": v(364.5, 378.05) * mm, "end": v(364.5, 393.87) * mm});
            skPoint(sketch, "E18.18.3.2", {"position": v(364.5, 376.05) * mm});
            skPoint(sketch, "E18.18.3.3", {"position": v(355.5, 376.05) * mm});
            skLineSegment(sketch, "E18.18.3.4", {"start": v(355.5, 393.87) * mm, "end": v(364.5, 393.87) * mm});
            skArc(sketch, "E18.18.3.5", {"start": v(355.5, 378.05) * mm, "mid": v(356.09, 376.64) * mm, "end": v(357.5, 376.05) * mm});
            skLineSegment(sketch, "E18.18.3.6", {"start": v(357.5, 376.05) * mm, "end": v(362.5, 376.05) * mm});
            skArc(sketch, "E18.18.3.7", {"start": v(362.5, 376.05) * mm, "mid": v(363.91, 376.64) * mm, "end": v(364.5, 378.05) * mm});
            skLineSegment(sketch, "E18.18.4.0", {"start": v(355.5, 343.41) * mm, "end": v(355.5, 359.23) * mm});
            skLineSegment(sketch, "E18.18.4.1", {"start": v(364.5, 343.41) * mm, "end": v(364.5, 359.23) * mm});
            skPoint(sketch, "E18.18.4.2", {"position": v(364.5, 341.41) * mm});
            skPoint(sketch, "E18.18.4.3", {"position": v(355.5, 341.41) * mm});
            skLineSegment(sketch, "E18.18.4.4", {"start": v(355.5, 359.23) * mm, "end": v(364.5, 359.23) * mm});
            skArc(sketch, "E18.18.4.5", {"start": v(355.5, 343.41) * mm, "mid": v(356.09, 342) * mm, "end": v(357.5, 341.41) * mm});
            skLineSegment(sketch, "E18.18.4.6", {"start": v(357.5, 341.41) * mm, "end": v(362.5, 341.41) * mm});
            skArc(sketch, "E18.18.4.7", {"start": v(362.5, 341.41) * mm, "mid": v(363.91, 342) * mm, "end": v(364.5, 343.41) * mm});
            skLineSegment(sketch, "E18.18.5.0", {"start": v(355.5, 308.77) * mm, "end": v(355.5, 324.59) * mm});
            skLineSegment(sketch, "E18.18.5.1", {"start": v(364.5, 308.77) * mm, "end": v(364.5, 324.59) * mm});
            skPoint(sketch, "E18.18.5.2", {"position": v(364.5, 306.77) * mm});
            skPoint(sketch, "E18.18.5.3", {"position": v(355.5, 306.77) * mm});
            skLineSegment(sketch, "E18.18.5.4", {"start": v(355.5, 324.59) * mm, "end": v(364.5, 324.59) * mm});
            skArc(sketch, "E18.18.5.5", {"start": v(355.5, 308.77) * mm, "mid": v(356.09, 307.35) * mm, "end": v(357.5, 306.77) * mm});
            skLineSegment(sketch, "E18.18.5.6", {"start": v(357.5, 306.77) * mm, "end": v(362.5, 306.77) * mm});
            skArc(sketch, "E18.18.5.7", {"start": v(362.5, 306.77) * mm, "mid": v(363.91, 307.35) * mm, "end": v(364.5, 308.77) * mm});
            skLineSegment(sketch, "E18.18.6.0", {"start": v(355.5, 274.13) * mm, "end": v(355.5, 289.95) * mm});
            skLineSegment(sketch, "E18.18.6.1", {"start": v(364.5, 274.13) * mm, "end": v(364.5, 289.95) * mm});
            skPoint(sketch, "E18.18.6.2", {"position": v(364.5, 272.13) * mm});
            skPoint(sketch, "E18.18.6.3", {"position": v(355.5, 272.13) * mm});
            skLineSegment(sketch, "E18.18.6.4", {"start": v(355.5, 289.95) * mm, "end": v(364.5, 289.95) * mm});
            skArc(sketch, "E18.18.6.5", {"start": v(355.5, 274.13) * mm, "mid": v(356.09, 272.71) * mm, "end": v(357.5, 272.13) * mm});
            skLineSegment(sketch, "E18.18.6.6", {"start": v(357.5, 272.13) * mm, "end": v(362.5, 272.13) * mm});
            skArc(sketch, "E18.18.6.7", {"start": v(362.5, 272.13) * mm, "mid": v(363.91, 272.71) * mm, "end": v(364.5, 274.13) * mm});
            skLineSegment(sketch, "E18.18.7.0", {"start": v(355.5, 239.49) * mm, "end": v(355.5, 255.3) * mm});
            skLineSegment(sketch, "E18.18.7.1", {"start": v(364.5, 239.49) * mm, "end": v(364.5, 255.3) * mm});
            skPoint(sketch, "E18.18.7.2", {"position": v(364.5, 237.49) * mm});
            skPoint(sketch, "E18.18.7.3", {"position": v(355.5, 237.49) * mm});
            skLineSegment(sketch, "E18.18.7.4", {"start": v(355.5, 255.3) * mm, "end": v(364.5, 255.3) * mm});
            skArc(sketch, "E18.18.7.5", {"start": v(355.5, 239.49) * mm, "mid": v(356.09, 238.07) * mm, "end": v(357.5, 237.49) * mm});
            skLineSegment(sketch, "E18.18.7.6", {"start": v(357.5, 237.49) * mm, "end": v(362.5, 237.49) * mm});
            skArc(sketch, "E18.18.7.7", {"start": v(362.5, 237.49) * mm, "mid": v(363.91, 238.07) * mm, "end": v(364.5, 239.49) * mm});
            skLineSegment(sketch, "E18.18.8.0", {"start": v(355.5, 204.85) * mm, "end": v(355.5, 220.67) * mm});
            skLineSegment(sketch, "E18.18.8.1", {"start": v(364.5, 204.85) * mm, "end": v(364.5, 220.67) * mm});
            skPoint(sketch, "E18.18.8.2", {"position": v(364.5, 202.85) * mm});
            skPoint(sketch, "E18.18.8.3", {"position": v(355.5, 202.85) * mm});
            skLineSegment(sketch, "E18.18.8.4", {"start": v(355.5, 220.67) * mm, "end": v(364.5, 220.67) * mm});
            skArc(sketch, "E18.18.8.5", {"start": v(355.5, 204.85) * mm, "mid": v(356.09, 203.43) * mm, "end": v(357.5, 202.85) * mm});
            skLineSegment(sketch, "E18.18.8.6", {"start": v(357.5, 202.85) * mm, "end": v(362.5, 202.85) * mm});
            skArc(sketch, "E18.18.8.7", {"start": v(362.5, 202.85) * mm, "mid": v(363.91, 203.43) * mm, "end": v(364.5, 204.85) * mm});
            skLineSegment(sketch, "E18.18.9.0", {"start": v(355.5, 170.2) * mm, "end": v(355.5, 186.03) * mm});
            skLineSegment(sketch, "E18.18.9.1", {"start": v(364.5, 170.2) * mm, "end": v(364.5, 186.03) * mm});
            skPoint(sketch, "E18.18.9.2", {"position": v(364.5, 168.2) * mm});
            skPoint(sketch, "E18.18.9.3", {"position": v(355.5, 168.2) * mm});
            skLineSegment(sketch, "E18.18.9.4", {"start": v(355.5, 186.03) * mm, "end": v(364.5, 186.03) * mm});
            skArc(sketch, "E18.18.9.5", {"start": v(355.5, 170.2) * mm, "mid": v(356.09, 168.8) * mm, "end": v(357.5, 168.2) * mm});
            skLineSegment(sketch, "E18.18.9.6", {"start": v(357.5, 168.2) * mm, "end": v(362.5, 168.2) * mm});
            skArc(sketch, "E18.18.9.7", {"start": v(362.5, 168.2) * mm, "mid": v(363.91, 168.8) * mm, "end": v(364.5, 170.2) * mm});
            skLineSegment(sketch, "E18.18.10.0", {"start": v(355.5, 135.56) * mm, "end": v(355.5, 151.38) * mm});
            skLineSegment(sketch, "E18.18.10.1", {"start": v(364.5, 135.56) * mm, "end": v(364.5, 151.38) * mm});
            skPoint(sketch, "E18.18.10.2", {"position": v(364.5, 133.56) * mm});
            skPoint(sketch, "E18.18.10.3", {"position": v(355.5, 133.56) * mm});
            skLineSegment(sketch, "E18.18.10.4", {"start": v(355.5, 151.38) * mm, "end": v(364.5, 151.38) * mm});
            skArc(sketch, "E18.18.10.5", {"start": v(355.5, 135.56) * mm, "mid": v(356.09, 134.15) * mm, "end": v(357.5, 133.56) * mm});
            skLineSegment(sketch, "E18.18.10.6", {"start": v(357.5, 133.56) * mm, "end": v(362.5, 133.56) * mm});
            skArc(sketch, "E18.18.10.7", {"start": v(362.5, 133.56) * mm, "mid": v(363.91, 134.15) * mm, "end": v(364.5, 135.56) * mm});
            skLineSegment(sketch, "E18.18.11.0", {"start": v(355.5, 100.92) * mm, "end": v(355.5, 116.74) * mm});
            skLineSegment(sketch, "E18.18.11.1", {"start": v(364.5, 100.92) * mm, "end": v(364.5, 116.74) * mm});
            skPoint(sketch, "E18.18.11.2", {"position": v(364.5, 98.92) * mm});
            skPoint(sketch, "E18.18.11.3", {"position": v(355.5, 98.92) * mm});
            skLineSegment(sketch, "E18.18.11.4", {"start": v(355.5, 116.74) * mm, "end": v(364.5, 116.74) * mm});
            skArc(sketch, "E18.18.11.5", {"start": v(355.5, 100.92) * mm, "mid": v(356.09, 99.5) * mm, "end": v(357.5, 98.92) * mm});
            skLineSegment(sketch, "E18.18.11.6", {"start": v(357.5, 98.92) * mm, "end": v(362.5, 98.92) * mm});
            skArc(sketch, "E18.18.11.7", {"start": v(362.5, 98.92) * mm, "mid": v(363.91, 99.5) * mm, "end": v(364.5, 100.92) * mm});
            skLineSegment(sketch, "E18.18.12.0", {"start": v(355.5, 66.28) * mm, "end": v(355.5, 82.1) * mm});
            skLineSegment(sketch, "E18.18.12.1", {"start": v(364.5, 66.28) * mm, "end": v(364.5, 82.1) * mm});
            skPoint(sketch, "E18.18.12.2", {"position": v(364.5, 64.28) * mm});
            skPoint(sketch, "E18.18.12.3", {"position": v(355.5, 64.28) * mm});
            skLineSegment(sketch, "E18.18.12.4", {"start": v(355.5, 82.1) * mm, "end": v(364.5, 82.1) * mm});
            skArc(sketch, "E18.18.12.5", {"start": v(355.5, 66.28) * mm, "mid": v(356.09, 64.87) * mm, "end": v(357.5, 64.28) * mm});
            skLineSegment(sketch, "E18.18.12.6", {"start": v(357.5, 64.28) * mm, "end": v(362.5, 64.28) * mm});
            skArc(sketch, "E18.18.12.7", {"start": v(362.5, 64.28) * mm, "mid": v(363.91, 64.87) * mm, "end": v(364.5, 66.28) * mm});
            skLineSegment(sketch, "E18.18.13.0", {"start": v(355.5, 31.64) * mm, "end": v(355.5, 47.46) * mm});
            skLineSegment(sketch, "E18.18.13.1", {"start": v(364.5, 31.64) * mm, "end": v(364.5, 47.46) * mm});
            skPoint(sketch, "E18.18.13.2", {"position": v(364.5, 29.64) * mm});
            skPoint(sketch, "E18.18.13.3", {"position": v(355.5, 29.64) * mm});
            skLineSegment(sketch, "E18.18.13.4", {"start": v(355.5, 47.46) * mm, "end": v(364.5, 47.46) * mm});
            skArc(sketch, "E18.18.13.5", {"start": v(355.5, 31.64) * mm, "mid": v(356.09, 30.23) * mm, "end": v(357.5, 29.64) * mm});
            skLineSegment(sketch, "E18.18.13.6", {"start": v(357.5, 29.64) * mm, "end": v(362.5, 29.64) * mm});
            skArc(sketch, "E18.18.13.7", {"start": v(362.5, 29.64) * mm, "mid": v(363.91, 30.23) * mm, "end": v(364.5, 31.64) * mm});
            skLineSegment(sketch, "E18.18.14.0", {"start": v(355.5, -3) * mm, "end": v(355.5, 12.82) * mm});
            skLineSegment(sketch, "E18.18.14.1", {"start": v(364.5, -3) * mm, "end": v(364.5, 12.82) * mm});
            skPoint(sketch, "E18.18.14.2", {"position": v(364.5, -5) * mm});
            skPoint(sketch, "E18.18.14.3", {"position": v(355.5, -5) * mm});
            skLineSegment(sketch, "E18.18.14.4", {"start": v(355.5, 12.82) * mm, "end": v(364.5, 12.82) * mm});
            skArc(sketch, "E18.18.14.5", {"start": v(355.5, -3) * mm, "mid": v(356.09, -4.41) * mm, "end": v(357.5, -5) * mm});
            skLineSegment(sketch, "E18.18.14.6", {"start": v(357.5, -5) * mm, "end": v(362.5, -5) * mm});
            skArc(sketch, "E18.18.14.7", {"start": v(362.5, -5) * mm, "mid": v(363.91, -4.41) * mm, "end": v(364.5, -3) * mm});
            skLineSegment(sketch, "E18.19.0.0", {"start": v(375.5, 481.97) * mm, "end": v(375.5, 497.8) * mm});
            skLineSegment(sketch, "E18.19.0.1", {"start": v(384.5, 481.97) * mm, "end": v(384.5, 497.8) * mm});
            skPoint(sketch, "E18.19.0.2", {"position": v(384.5, 479.97) * mm});
            skPoint(sketch, "E18.19.0.3", {"position": v(375.5, 479.97) * mm});
            skLineSegment(sketch, "E18.19.0.4", {"start": v(375.5, 497.8) * mm, "end": v(384.5, 497.8) * mm});
            skArc(sketch, "E18.19.0.5", {"start": v(375.5, 481.97) * mm, "mid": v(376.09, 480.56) * mm, "end": v(377.5, 479.97) * mm});
            skLineSegment(sketch, "E18.19.0.6", {"start": v(377.5, 479.97) * mm, "end": v(382.5, 479.97) * mm});
            skArc(sketch, "E18.19.0.7", {"start": v(382.5, 479.97) * mm, "mid": v(383.91, 480.56) * mm, "end": v(384.5, 481.97) * mm});
            skLineSegment(sketch, "E18.19.1.0", {"start": v(375.5, 447.33) * mm, "end": v(375.5, 463.15) * mm});
            skLineSegment(sketch, "E18.19.1.1", {"start": v(384.5, 447.33) * mm, "end": v(384.5, 463.15) * mm});
            skPoint(sketch, "E18.19.1.2", {"position": v(384.5, 445.33) * mm});
            skPoint(sketch, "E18.19.1.3", {"position": v(375.5, 445.33) * mm});
            skLineSegment(sketch, "E18.19.1.4", {"start": v(375.5, 463.15) * mm, "end": v(384.5, 463.15) * mm});
            skArc(sketch, "E18.19.1.5", {"start": v(375.5, 447.33) * mm, "mid": v(376.09, 445.92) * mm, "end": v(377.5, 445.33) * mm});
            skLineSegment(sketch, "E18.19.1.6", {"start": v(377.5, 445.33) * mm, "end": v(382.5, 445.33) * mm});
            skArc(sketch, "E18.19.1.7", {"start": v(382.5, 445.33) * mm, "mid": v(383.91, 445.92) * mm, "end": v(384.5, 447.33) * mm});
            skLineSegment(sketch, "E18.19.2.0", {"start": v(375.5, 412.7) * mm, "end": v(375.5, 428.51) * mm});
            skLineSegment(sketch, "E18.19.2.1", {"start": v(384.5, 412.7) * mm, "end": v(384.5, 428.51) * mm});
            skPoint(sketch, "E18.19.2.2", {"position": v(384.5, 410.7) * mm});
            skPoint(sketch, "E18.19.2.3", {"position": v(375.5, 410.7) * mm});
            skLineSegment(sketch, "E18.19.2.4", {"start": v(375.5, 428.51) * mm, "end": v(384.5, 428.51) * mm});
            skArc(sketch, "E18.19.2.5", {"start": v(375.5, 412.7) * mm, "mid": v(376.09, 411.28) * mm, "end": v(377.5, 410.7) * mm});
            skLineSegment(sketch, "E18.19.2.6", {"start": v(377.5, 410.7) * mm, "end": v(382.5, 410.7) * mm});
            skArc(sketch, "E18.19.2.7", {"start": v(382.5, 410.7) * mm, "mid": v(383.91, 411.28) * mm, "end": v(384.5, 412.7) * mm});
            skLineSegment(sketch, "E18.19.3.0", {"start": v(375.5, 378.05) * mm, "end": v(375.5, 393.87) * mm});
            skLineSegment(sketch, "E18.19.3.1", {"start": v(384.5, 378.05) * mm, "end": v(384.5, 393.87) * mm});
            skPoint(sketch, "E18.19.3.2", {"position": v(384.5, 376.05) * mm});
            skPoint(sketch, "E18.19.3.3", {"position": v(375.5, 376.05) * mm});
            skLineSegment(sketch, "E18.19.3.4", {"start": v(375.5, 393.87) * mm, "end": v(384.5, 393.87) * mm});
            skArc(sketch, "E18.19.3.5", {"start": v(375.5, 378.05) * mm, "mid": v(376.09, 376.64) * mm, "end": v(377.5, 376.05) * mm});
            skLineSegment(sketch, "E18.19.3.6", {"start": v(377.5, 376.05) * mm, "end": v(382.5, 376.05) * mm});
            skArc(sketch, "E18.19.3.7", {"start": v(382.5, 376.05) * mm, "mid": v(383.91, 376.64) * mm, "end": v(384.5, 378.05) * mm});
            skLineSegment(sketch, "E18.19.4.0", {"start": v(375.5, 343.41) * mm, "end": v(375.5, 359.23) * mm});
            skLineSegment(sketch, "E18.19.4.1", {"start": v(384.5, 343.41) * mm, "end": v(384.5, 359.23) * mm});
            skPoint(sketch, "E18.19.4.2", {"position": v(384.5, 341.41) * mm});
            skPoint(sketch, "E18.19.4.3", {"position": v(375.5, 341.41) * mm});
            skLineSegment(sketch, "E18.19.4.4", {"start": v(375.5, 359.23) * mm, "end": v(384.5, 359.23) * mm});
            skArc(sketch, "E18.19.4.5", {"start": v(375.5, 343.41) * mm, "mid": v(376.09, 342) * mm, "end": v(377.5, 341.41) * mm});
            skLineSegment(sketch, "E18.19.4.6", {"start": v(377.5, 341.41) * mm, "end": v(382.5, 341.41) * mm});
            skArc(sketch, "E18.19.4.7", {"start": v(382.5, 341.41) * mm, "mid": v(383.91, 342) * mm, "end": v(384.5, 343.41) * mm});
            skLineSegment(sketch, "E18.19.5.0", {"start": v(375.5, 308.77) * mm, "end": v(375.5, 324.59) * mm});
            skLineSegment(sketch, "E18.19.5.1", {"start": v(384.5, 308.77) * mm, "end": v(384.5, 324.59) * mm});
            skPoint(sketch, "E18.19.5.2", {"position": v(384.5, 306.77) * mm});
            skPoint(sketch, "E18.19.5.3", {"position": v(375.5, 306.77) * mm});
            skLineSegment(sketch, "E18.19.5.4", {"start": v(375.5, 324.59) * mm, "end": v(384.5, 324.59) * mm});
            skArc(sketch, "E18.19.5.5", {"start": v(375.5, 308.77) * mm, "mid": v(376.09, 307.35) * mm, "end": v(377.5, 306.77) * mm});
            skLineSegment(sketch, "E18.19.5.6", {"start": v(377.5, 306.77) * mm, "end": v(382.5, 306.77) * mm});
            skArc(sketch, "E18.19.5.7", {"start": v(382.5, 306.77) * mm, "mid": v(383.91, 307.35) * mm, "end": v(384.5, 308.77) * mm});
            skLineSegment(sketch, "E18.19.6.0", {"start": v(375.5, 274.13) * mm, "end": v(375.5, 289.95) * mm});
            skLineSegment(sketch, "E18.19.6.1", {"start": v(384.5, 274.13) * mm, "end": v(384.5, 289.95) * mm});
            skPoint(sketch, "E18.19.6.2", {"position": v(384.5, 272.13) * mm});
            skPoint(sketch, "E18.19.6.3", {"position": v(375.5, 272.13) * mm});
            skLineSegment(sketch, "E18.19.6.4", {"start": v(375.5, 289.95) * mm, "end": v(384.5, 289.95) * mm});
            skArc(sketch, "E18.19.6.5", {"start": v(375.5, 274.13) * mm, "mid": v(376.09, 272.71) * mm, "end": v(377.5, 272.13) * mm});
            skLineSegment(sketch, "E18.19.6.6", {"start": v(377.5, 272.13) * mm, "end": v(382.5, 272.13) * mm});
            skArc(sketch, "E18.19.6.7", {"start": v(382.5, 272.13) * mm, "mid": v(383.91, 272.71) * mm, "end": v(384.5, 274.13) * mm});
            skLineSegment(sketch, "E18.19.7.0", {"start": v(375.5, 239.49) * mm, "end": v(375.5, 255.3) * mm});
            skLineSegment(sketch, "E18.19.7.1", {"start": v(384.5, 239.49) * mm, "end": v(384.5, 255.3) * mm});
            skPoint(sketch, "E18.19.7.2", {"position": v(384.5, 237.49) * mm});
            skPoint(sketch, "E18.19.7.3", {"position": v(375.5, 237.49) * mm});
            skLineSegment(sketch, "E18.19.7.4", {"start": v(375.5, 255.3) * mm, "end": v(384.5, 255.3) * mm});
            skArc(sketch, "E18.19.7.5", {"start": v(375.5, 239.49) * mm, "mid": v(376.09, 238.07) * mm, "end": v(377.5, 237.49) * mm});
            skLineSegment(sketch, "E18.19.7.6", {"start": v(377.5, 237.49) * mm, "end": v(382.5, 237.49) * mm});
            skArc(sketch, "E18.19.7.7", {"start": v(382.5, 237.49) * mm, "mid": v(383.91, 238.07) * mm, "end": v(384.5, 239.49) * mm});
            skLineSegment(sketch, "E18.19.8.0", {"start": v(375.5, 204.85) * mm, "end": v(375.5, 220.67) * mm});
            skLineSegment(sketch, "E18.19.8.1", {"start": v(384.5, 204.85) * mm, "end": v(384.5, 220.67) * mm});
            skPoint(sketch, "E18.19.8.2", {"position": v(384.5, 202.85) * mm});
            skPoint(sketch, "E18.19.8.3", {"position": v(375.5, 202.85) * mm});
            skLineSegment(sketch, "E18.19.8.4", {"start": v(375.5, 220.67) * mm, "end": v(384.5, 220.67) * mm});
            skArc(sketch, "E18.19.8.5", {"start": v(375.5, 204.85) * mm, "mid": v(376.09, 203.43) * mm, "end": v(377.5, 202.85) * mm});
            skLineSegment(sketch, "E18.19.8.6", {"start": v(377.5, 202.85) * mm, "end": v(382.5, 202.85) * mm});
            skArc(sketch, "E18.19.8.7", {"start": v(382.5, 202.85) * mm, "mid": v(383.91, 203.43) * mm, "end": v(384.5, 204.85) * mm});
            skLineSegment(sketch, "E18.19.9.0", {"start": v(375.5, 170.2) * mm, "end": v(375.5, 186.03) * mm});
            skLineSegment(sketch, "E18.19.9.1", {"start": v(384.5, 170.2) * mm, "end": v(384.5, 186.03) * mm});
            skPoint(sketch, "E18.19.9.2", {"position": v(384.5, 168.2) * mm});
            skPoint(sketch, "E18.19.9.3", {"position": v(375.5, 168.2) * mm});
            skLineSegment(sketch, "E18.19.9.4", {"start": v(375.5, 186.03) * mm, "end": v(384.5, 186.03) * mm});
            skArc(sketch, "E18.19.9.5", {"start": v(375.5, 170.2) * mm, "mid": v(376.09, 168.8) * mm, "end": v(377.5, 168.2) * mm});
            skLineSegment(sketch, "E18.19.9.6", {"start": v(377.5, 168.2) * mm, "end": v(382.5, 168.2) * mm});
            skArc(sketch, "E18.19.9.7", {"start": v(382.5, 168.2) * mm, "mid": v(383.91, 168.8) * mm, "end": v(384.5, 170.2) * mm});
            skLineSegment(sketch, "E18.19.10.0", {"start": v(375.5, 135.56) * mm, "end": v(375.5, 151.38) * mm});
            skLineSegment(sketch, "E18.19.10.1", {"start": v(384.5, 135.56) * mm, "end": v(384.5, 151.38) * mm});
            skPoint(sketch, "E18.19.10.2", {"position": v(384.5, 133.56) * mm});
            skPoint(sketch, "E18.19.10.3", {"position": v(375.5, 133.56) * mm});
            skLineSegment(sketch, "E18.19.10.4", {"start": v(375.5, 151.38) * mm, "end": v(384.5, 151.38) * mm});
            skArc(sketch, "E18.19.10.5", {"start": v(375.5, 135.56) * mm, "mid": v(376.09, 134.15) * mm, "end": v(377.5, 133.56) * mm});
            skLineSegment(sketch, "E18.19.10.6", {"start": v(377.5, 133.56) * mm, "end": v(382.5, 133.56) * mm});
            skArc(sketch, "E18.19.10.7", {"start": v(382.5, 133.56) * mm, "mid": v(383.91, 134.15) * mm, "end": v(384.5, 135.56) * mm});
            skLineSegment(sketch, "E18.19.11.0", {"start": v(375.5, 100.92) * mm, "end": v(375.5, 116.74) * mm});
            skLineSegment(sketch, "E18.19.11.1", {"start": v(384.5, 100.92) * mm, "end": v(384.5, 116.74) * mm});
            skPoint(sketch, "E18.19.11.2", {"position": v(384.5, 98.92) * mm});
            skPoint(sketch, "E18.19.11.3", {"position": v(375.5, 98.92) * mm});
            skLineSegment(sketch, "E18.19.11.4", {"start": v(375.5, 116.74) * mm, "end": v(384.5, 116.74) * mm});
            skArc(sketch, "E18.19.11.5", {"start": v(375.5, 100.92) * mm, "mid": v(376.09, 99.5) * mm, "end": v(377.5, 98.92) * mm});
            skLineSegment(sketch, "E18.19.11.6", {"start": v(377.5, 98.92) * mm, "end": v(382.5, 98.92) * mm});
            skArc(sketch, "E18.19.11.7", {"start": v(382.5, 98.92) * mm, "mid": v(383.91, 99.5) * mm, "end": v(384.5, 100.92) * mm});
            skLineSegment(sketch, "E18.19.12.0", {"start": v(375.5, 66.28) * mm, "end": v(375.5, 82.1) * mm});
            skLineSegment(sketch, "E18.19.12.1", {"start": v(384.5, 66.28) * mm, "end": v(384.5, 82.1) * mm});
            skPoint(sketch, "E18.19.12.2", {"position": v(384.5, 64.28) * mm});
            skPoint(sketch, "E18.19.12.3", {"position": v(375.5, 64.28) * mm});
            skLineSegment(sketch, "E18.19.12.4", {"start": v(375.5, 82.1) * mm, "end": v(384.5, 82.1) * mm});
            skArc(sketch, "E18.19.12.5", {"start": v(375.5, 66.28) * mm, "mid": v(376.09, 64.87) * mm, "end": v(377.5, 64.28) * mm});
            skLineSegment(sketch, "E18.19.12.6", {"start": v(377.5, 64.28) * mm, "end": v(382.5, 64.28) * mm});
            skArc(sketch, "E18.19.12.7", {"start": v(382.5, 64.28) * mm, "mid": v(383.91, 64.87) * mm, "end": v(384.5, 66.28) * mm});
            skLineSegment(sketch, "E18.19.13.0", {"start": v(375.5, 31.64) * mm, "end": v(375.5, 47.46) * mm});
            skLineSegment(sketch, "E18.19.13.1", {"start": v(384.5, 31.64) * mm, "end": v(384.5, 47.46) * mm});
            skPoint(sketch, "E18.19.13.2", {"position": v(384.5, 29.64) * mm});
            skPoint(sketch, "E18.19.13.3", {"position": v(375.5, 29.64) * mm});
            skLineSegment(sketch, "E18.19.13.4", {"start": v(375.5, 47.46) * mm, "end": v(384.5, 47.46) * mm});
            skArc(sketch, "E18.19.13.5", {"start": v(375.5, 31.64) * mm, "mid": v(376.09, 30.23) * mm, "end": v(377.5, 29.64) * mm});
            skLineSegment(sketch, "E18.19.13.6", {"start": v(377.5, 29.64) * mm, "end": v(382.5, 29.64) * mm});
            skArc(sketch, "E18.19.13.7", {"start": v(382.5, 29.64) * mm, "mid": v(383.91, 30.23) * mm, "end": v(384.5, 31.64) * mm});
            skLineSegment(sketch, "E18.19.14.0", {"start": v(375.5, -3) * mm, "end": v(375.5, 12.82) * mm});
            skLineSegment(sketch, "E18.19.14.1", {"start": v(384.5, -3) * mm, "end": v(384.5, 12.82) * mm});
            skPoint(sketch, "E18.19.14.2", {"position": v(384.5, -5) * mm});
            skPoint(sketch, "E18.19.14.3", {"position": v(375.5, -5) * mm});
            skLineSegment(sketch, "E18.19.14.4", {"start": v(375.5, 12.82) * mm, "end": v(384.5, 12.82) * mm});
            skArc(sketch, "E18.19.14.5", {"start": v(375.5, -3) * mm, "mid": v(376.09, -4.41) * mm, "end": v(377.5, -5) * mm});
            skLineSegment(sketch, "E18.19.14.6", {"start": v(377.5, -5) * mm, "end": v(382.5, -5) * mm});
            skArc(sketch, "E18.19.14.7", {"start": v(382.5, -5) * mm, "mid": v(383.91, -4.41) * mm, "end": v(384.5, -3) * mm});
            skLineSegment(sketch, "E18.20.0.0", {"start": v(395.5, 481.97) * mm, "end": v(395.5, 497.8) * mm});
            skLineSegment(sketch, "E18.20.0.1", {"start": v(404.5, 481.97) * mm, "end": v(404.5, 497.8) * mm});
            skPoint(sketch, "E18.20.0.2", {"position": v(404.5, 479.97) * mm});
            skPoint(sketch, "E18.20.0.3", {"position": v(395.5, 479.97) * mm});
            skLineSegment(sketch, "E18.20.0.4", {"start": v(395.5, 497.8) * mm, "end": v(404.5, 497.8) * mm});
            skArc(sketch, "E18.20.0.5", {"start": v(395.5, 481.97) * mm, "mid": v(396.09, 480.56) * mm, "end": v(397.5, 479.97) * mm});
            skLineSegment(sketch, "E18.20.0.6", {"start": v(397.5, 479.97) * mm, "end": v(402.5, 479.97) * mm});
            skArc(sketch, "E18.20.0.7", {"start": v(402.5, 479.97) * mm, "mid": v(403.91, 480.56) * mm, "end": v(404.5, 481.97) * mm});
            skLineSegment(sketch, "E18.20.1.0", {"start": v(395.5, 447.33) * mm, "end": v(395.5, 463.15) * mm});
            skLineSegment(sketch, "E18.20.1.1", {"start": v(404.5, 447.33) * mm, "end": v(404.5, 463.15) * mm});
            skPoint(sketch, "E18.20.1.2", {"position": v(404.5, 445.33) * mm});
            skPoint(sketch, "E18.20.1.3", {"position": v(395.5, 445.33) * mm});
            skLineSegment(sketch, "E18.20.1.4", {"start": v(395.5, 463.15) * mm, "end": v(404.5, 463.15) * mm});
            skArc(sketch, "E18.20.1.5", {"start": v(395.5, 447.33) * mm, "mid": v(396.09, 445.92) * mm, "end": v(397.5, 445.33) * mm});
            skLineSegment(sketch, "E18.20.1.6", {"start": v(397.5, 445.33) * mm, "end": v(402.5, 445.33) * mm});
            skArc(sketch, "E18.20.1.7", {"start": v(402.5, 445.33) * mm, "mid": v(403.91, 445.92) * mm, "end": v(404.5, 447.33) * mm});
            skLineSegment(sketch, "E18.20.2.0", {"start": v(395.5, 412.7) * mm, "end": v(395.5, 428.51) * mm});
            skLineSegment(sketch, "E18.20.2.1", {"start": v(404.5, 412.7) * mm, "end": v(404.5, 428.51) * mm});
            skPoint(sketch, "E18.20.2.2", {"position": v(404.5, 410.7) * mm});
            skPoint(sketch, "E18.20.2.3", {"position": v(395.5, 410.7) * mm});
            skLineSegment(sketch, "E18.20.2.4", {"start": v(395.5, 428.51) * mm, "end": v(404.5, 428.51) * mm});
            skArc(sketch, "E18.20.2.5", {"start": v(395.5, 412.7) * mm, "mid": v(396.09, 411.28) * mm, "end": v(397.5, 410.7) * mm});
            skLineSegment(sketch, "E18.20.2.6", {"start": v(397.5, 410.7) * mm, "end": v(402.5, 410.7) * mm});
            skArc(sketch, "E18.20.2.7", {"start": v(402.5, 410.7) * mm, "mid": v(403.91, 411.28) * mm, "end": v(404.5, 412.7) * mm});
            skLineSegment(sketch, "E18.20.3.0", {"start": v(395.5, 378.05) * mm, "end": v(395.5, 393.87) * mm});
            skLineSegment(sketch, "E18.20.3.1", {"start": v(404.5, 378.05) * mm, "end": v(404.5, 393.87) * mm});
            skPoint(sketch, "E18.20.3.2", {"position": v(404.5, 376.05) * mm});
            skPoint(sketch, "E18.20.3.3", {"position": v(395.5, 376.05) * mm});
            skLineSegment(sketch, "E18.20.3.4", {"start": v(395.5, 393.87) * mm, "end": v(404.5, 393.87) * mm});
            skArc(sketch, "E18.20.3.5", {"start": v(395.5, 378.05) * mm, "mid": v(396.09, 376.64) * mm, "end": v(397.5, 376.05) * mm});
            skLineSegment(sketch, "E18.20.3.6", {"start": v(397.5, 376.05) * mm, "end": v(402.5, 376.05) * mm});
            skArc(sketch, "E18.20.3.7", {"start": v(402.5, 376.05) * mm, "mid": v(403.91, 376.64) * mm, "end": v(404.5, 378.05) * mm});
            skLineSegment(sketch, "E18.20.4.0", {"start": v(395.5, 343.41) * mm, "end": v(395.5, 359.23) * mm});
            skLineSegment(sketch, "E18.20.4.1", {"start": v(404.5, 343.41) * mm, "end": v(404.5, 359.23) * mm});
            skPoint(sketch, "E18.20.4.2", {"position": v(404.5, 341.41) * mm});
            skPoint(sketch, "E18.20.4.3", {"position": v(395.5, 341.41) * mm});
            skLineSegment(sketch, "E18.20.4.4", {"start": v(395.5, 359.23) * mm, "end": v(404.5, 359.23) * mm});
            skArc(sketch, "E18.20.4.5", {"start": v(395.5, 343.41) * mm, "mid": v(396.09, 342) * mm, "end": v(397.5, 341.41) * mm});
            skLineSegment(sketch, "E18.20.4.6", {"start": v(397.5, 341.41) * mm, "end": v(402.5, 341.41) * mm});
            skArc(sketch, "E18.20.4.7", {"start": v(402.5, 341.41) * mm, "mid": v(403.91, 342) * mm, "end": v(404.5, 343.41) * mm});
            skLineSegment(sketch, "E18.20.5.0", {"start": v(395.5, 308.77) * mm, "end": v(395.5, 324.59) * mm});
            skLineSegment(sketch, "E18.20.5.1", {"start": v(404.5, 308.77) * mm, "end": v(404.5, 324.59) * mm});
            skPoint(sketch, "E18.20.5.2", {"position": v(404.5, 306.77) * mm});
            skPoint(sketch, "E18.20.5.3", {"position": v(395.5, 306.77) * mm});
            skLineSegment(sketch, "E18.20.5.4", {"start": v(395.5, 324.59) * mm, "end": v(404.5, 324.59) * mm});
            skArc(sketch, "E18.20.5.5", {"start": v(395.5, 308.77) * mm, "mid": v(396.09, 307.35) * mm, "end": v(397.5, 306.77) * mm});
            skLineSegment(sketch, "E18.20.5.6", {"start": v(397.5, 306.77) * mm, "end": v(402.5, 306.77) * mm});
            skArc(sketch, "E18.20.5.7", {"start": v(402.5, 306.77) * mm, "mid": v(403.91, 307.35) * mm, "end": v(404.5, 308.77) * mm});
            skLineSegment(sketch, "E18.20.6.0", {"start": v(395.5, 274.13) * mm, "end": v(395.5, 289.95) * mm});
            skLineSegment(sketch, "E18.20.6.1", {"start": v(404.5, 274.13) * mm, "end": v(404.5, 289.95) * mm});
            skPoint(sketch, "E18.20.6.2", {"position": v(404.5, 272.13) * mm});
            skPoint(sketch, "E18.20.6.3", {"position": v(395.5, 272.13) * mm});
            skLineSegment(sketch, "E18.20.6.4", {"start": v(395.5, 289.95) * mm, "end": v(404.5, 289.95) * mm});
            skArc(sketch, "E18.20.6.5", {"start": v(395.5, 274.13) * mm, "mid": v(396.09, 272.71) * mm, "end": v(397.5, 272.13) * mm});
            skLineSegment(sketch, "E18.20.6.6", {"start": v(397.5, 272.13) * mm, "end": v(402.5, 272.13) * mm});
            skArc(sketch, "E18.20.6.7", {"start": v(402.5, 272.13) * mm, "mid": v(403.91, 272.71) * mm, "end": v(404.5, 274.13) * mm});
            skLineSegment(sketch, "E18.20.7.0", {"start": v(395.5, 239.49) * mm, "end": v(395.5, 255.3) * mm});
            skLineSegment(sketch, "E18.20.7.1", {"start": v(404.5, 239.49) * mm, "end": v(404.5, 255.3) * mm});
            skPoint(sketch, "E18.20.7.2", {"position": v(404.5, 237.49) * mm});
            skPoint(sketch, "E18.20.7.3", {"position": v(395.5, 237.49) * mm});
            skLineSegment(sketch, "E18.20.7.4", {"start": v(395.5, 255.3) * mm, "end": v(404.5, 255.3) * mm});
            skArc(sketch, "E18.20.7.5", {"start": v(395.5, 239.49) * mm, "mid": v(396.09, 238.07) * mm, "end": v(397.5, 237.49) * mm});
            skLineSegment(sketch, "E18.20.7.6", {"start": v(397.5, 237.49) * mm, "end": v(402.5, 237.49) * mm});
            skArc(sketch, "E18.20.7.7", {"start": v(402.5, 237.49) * mm, "mid": v(403.91, 238.07) * mm, "end": v(404.5, 239.49) * mm});
            skLineSegment(sketch, "E18.20.8.0", {"start": v(395.5, 204.85) * mm, "end": v(395.5, 220.67) * mm});
            skLineSegment(sketch, "E18.20.8.1", {"start": v(404.5, 204.85) * mm, "end": v(404.5, 220.67) * mm});
            skPoint(sketch, "E18.20.8.2", {"position": v(404.5, 202.85) * mm});
            skPoint(sketch, "E18.20.8.3", {"position": v(395.5, 202.85) * mm});
            skLineSegment(sketch, "E18.20.8.4", {"start": v(395.5, 220.67) * mm, "end": v(404.5, 220.67) * mm});
            skArc(sketch, "E18.20.8.5", {"start": v(395.5, 204.85) * mm, "mid": v(396.09, 203.43) * mm, "end": v(397.5, 202.85) * mm});
            skLineSegment(sketch, "E18.20.8.6", {"start": v(397.5, 202.85) * mm, "end": v(402.5, 202.85) * mm});
            skArc(sketch, "E18.20.8.7", {"start": v(402.5, 202.85) * mm, "mid": v(403.91, 203.43) * mm, "end": v(404.5, 204.85) * mm});
            skLineSegment(sketch, "E18.20.9.0", {"start": v(395.5, 170.2) * mm, "end": v(395.5, 186.03) * mm});
            skLineSegment(sketch, "E18.20.9.1", {"start": v(404.5, 170.2) * mm, "end": v(404.5, 186.03) * mm});
            skPoint(sketch, "E18.20.9.2", {"position": v(404.5, 168.2) * mm});
            skPoint(sketch, "E18.20.9.3", {"position": v(395.5, 168.2) * mm});
            skLineSegment(sketch, "E18.20.9.4", {"start": v(395.5, 186.03) * mm, "end": v(404.5, 186.03) * mm});
            skArc(sketch, "E18.20.9.5", {"start": v(395.5, 170.2) * mm, "mid": v(396.09, 168.8) * mm, "end": v(397.5, 168.2) * mm});
            skLineSegment(sketch, "E18.20.9.6", {"start": v(397.5, 168.2) * mm, "end": v(402.5, 168.2) * mm});
            skArc(sketch, "E18.20.9.7", {"start": v(402.5, 168.2) * mm, "mid": v(403.91, 168.8) * mm, "end": v(404.5, 170.2) * mm});
            skLineSegment(sketch, "E18.20.10.0", {"start": v(395.5, 135.56) * mm, "end": v(395.5, 151.38) * mm});
            skLineSegment(sketch, "E18.20.10.1", {"start": v(404.5, 135.56) * mm, "end": v(404.5, 151.38) * mm});
            skPoint(sketch, "E18.20.10.2", {"position": v(404.5, 133.56) * mm});
            skPoint(sketch, "E18.20.10.3", {"position": v(395.5, 133.56) * mm});
            skLineSegment(sketch, "E18.20.10.4", {"start": v(395.5, 151.38) * mm, "end": v(404.5, 151.38) * mm});
            skArc(sketch, "E18.20.10.5", {"start": v(395.5, 135.56) * mm, "mid": v(396.09, 134.15) * mm, "end": v(397.5, 133.56) * mm});
            skLineSegment(sketch, "E18.20.10.6", {"start": v(397.5, 133.56) * mm, "end": v(402.5, 133.56) * mm});
            skArc(sketch, "E18.20.10.7", {"start": v(402.5, 133.56) * mm, "mid": v(403.91, 134.15) * mm, "end": v(404.5, 135.56) * mm});
            skLineSegment(sketch, "E18.20.11.0", {"start": v(395.5, 100.92) * mm, "end": v(395.5, 116.74) * mm});
            skLineSegment(sketch, "E18.20.11.1", {"start": v(404.5, 100.92) * mm, "end": v(404.5, 116.74) * mm});
            skPoint(sketch, "E18.20.11.2", {"position": v(404.5, 98.92) * mm});
            skPoint(sketch, "E18.20.11.3", {"position": v(395.5, 98.92) * mm});
            skLineSegment(sketch, "E18.20.11.4", {"start": v(395.5, 116.74) * mm, "end": v(404.5, 116.74) * mm});
            skArc(sketch, "E18.20.11.5", {"start": v(395.5, 100.92) * mm, "mid": v(396.09, 99.5) * mm, "end": v(397.5, 98.92) * mm});
            skLineSegment(sketch, "E18.20.11.6", {"start": v(397.5, 98.92) * mm, "end": v(402.5, 98.92) * mm});
            skArc(sketch, "E18.20.11.7", {"start": v(402.5, 98.92) * mm, "mid": v(403.91, 99.5) * mm, "end": v(404.5, 100.92) * mm});
            skLineSegment(sketch, "E18.20.12.0", {"start": v(395.5, 66.28) * mm, "end": v(395.5, 82.1) * mm});
            skLineSegment(sketch, "E18.20.12.1", {"start": v(404.5, 66.28) * mm, "end": v(404.5, 82.1) * mm});
            skPoint(sketch, "E18.20.12.2", {"position": v(404.5, 64.28) * mm});
            skPoint(sketch, "E18.20.12.3", {"position": v(395.5, 64.28) * mm});
            skLineSegment(sketch, "E18.20.12.4", {"start": v(395.5, 82.1) * mm, "end": v(404.5, 82.1) * mm});
            skArc(sketch, "E18.20.12.5", {"start": v(395.5, 66.28) * mm, "mid": v(396.09, 64.87) * mm, "end": v(397.5, 64.28) * mm});
            skLineSegment(sketch, "E18.20.12.6", {"start": v(397.5, 64.28) * mm, "end": v(402.5, 64.28) * mm});
            skArc(sketch, "E18.20.12.7", {"start": v(402.5, 64.28) * mm, "mid": v(403.91, 64.87) * mm, "end": v(404.5, 66.28) * mm});
            skLineSegment(sketch, "E18.20.13.0", {"start": v(395.5, 31.64) * mm, "end": v(395.5, 47.46) * mm});
            skLineSegment(sketch, "E18.20.13.1", {"start": v(404.5, 31.64) * mm, "end": v(404.5, 47.46) * mm});
            skPoint(sketch, "E18.20.13.2", {"position": v(404.5, 29.64) * mm});
            skPoint(sketch, "E18.20.13.3", {"position": v(395.5, 29.64) * mm});
            skLineSegment(sketch, "E18.20.13.4", {"start": v(395.5, 47.46) * mm, "end": v(404.5, 47.46) * mm});
            skArc(sketch, "E18.20.13.5", {"start": v(395.5, 31.64) * mm, "mid": v(396.09, 30.23) * mm, "end": v(397.5, 29.64) * mm});
            skLineSegment(sketch, "E18.20.13.6", {"start": v(397.5, 29.64) * mm, "end": v(402.5, 29.64) * mm});
            skArc(sketch, "E18.20.13.7", {"start": v(402.5, 29.64) * mm, "mid": v(403.91, 30.23) * mm, "end": v(404.5, 31.64) * mm});
            skLineSegment(sketch, "E18.20.14.0", {"start": v(395.5, -3) * mm, "end": v(395.5, 12.82) * mm});
            skLineSegment(sketch, "E18.20.14.1", {"start": v(404.5, -3) * mm, "end": v(404.5, 12.82) * mm});
            skPoint(sketch, "E18.20.14.2", {"position": v(404.5, -5) * mm});
            skPoint(sketch, "E18.20.14.3", {"position": v(395.5, -5) * mm});
            skLineSegment(sketch, "E18.20.14.4", {"start": v(395.5, 12.82) * mm, "end": v(404.5, 12.82) * mm});
            skArc(sketch, "E18.20.14.5", {"start": v(395.5, -3) * mm, "mid": v(396.09, -4.41) * mm, "end": v(397.5, -5) * mm});
            skLineSegment(sketch, "E18.20.14.6", {"start": v(397.5, -5) * mm, "end": v(402.5, -5) * mm});
            skArc(sketch, "E18.20.14.7", {"start": v(402.5, -5) * mm, "mid": v(403.91, -4.41) * mm, "end": v(404.5, -3) * mm});
            skLineSegment(sketch, "E18.21.0.0", {"start": v(415.5, 481.97) * mm, "end": v(415.5, 497.8) * mm});
            skLineSegment(sketch, "E18.21.0.1", {"start": v(424.5, 481.97) * mm, "end": v(424.5, 497.8) * mm});
            skPoint(sketch, "E18.21.0.2", {"position": v(424.5, 479.97) * mm});
            skPoint(sketch, "E18.21.0.3", {"position": v(415.5, 479.97) * mm});
            skLineSegment(sketch, "E18.21.0.4", {"start": v(415.5, 497.8) * mm, "end": v(424.5, 497.8) * mm});
            skArc(sketch, "E18.21.0.5", {"start": v(415.5, 481.97) * mm, "mid": v(416.09, 480.56) * mm, "end": v(417.5, 479.97) * mm});
            skLineSegment(sketch, "E18.21.0.6", {"start": v(417.5, 479.97) * mm, "end": v(422.5, 479.97) * mm});
            skArc(sketch, "E18.21.0.7", {"start": v(422.5, 479.97) * mm, "mid": v(423.91, 480.56) * mm, "end": v(424.5, 481.97) * mm});
            skLineSegment(sketch, "E18.21.1.0", {"start": v(415.5, 447.33) * mm, "end": v(415.5, 463.15) * mm});
            skLineSegment(sketch, "E18.21.1.1", {"start": v(424.5, 447.33) * mm, "end": v(424.5, 463.15) * mm});
            skPoint(sketch, "E18.21.1.2", {"position": v(424.5, 445.33) * mm});
            skPoint(sketch, "E18.21.1.3", {"position": v(415.5, 445.33) * mm});
            skLineSegment(sketch, "E18.21.1.4", {"start": v(415.5, 463.15) * mm, "end": v(424.5, 463.15) * mm});
            skArc(sketch, "E18.21.1.5", {"start": v(415.5, 447.33) * mm, "mid": v(416.09, 445.92) * mm, "end": v(417.5, 445.33) * mm});
            skLineSegment(sketch, "E18.21.1.6", {"start": v(417.5, 445.33) * mm, "end": v(422.5, 445.33) * mm});
            skArc(sketch, "E18.21.1.7", {"start": v(422.5, 445.33) * mm, "mid": v(423.91, 445.92) * mm, "end": v(424.5, 447.33) * mm});
            skLineSegment(sketch, "E18.21.2.0", {"start": v(415.5, 412.7) * mm, "end": v(415.5, 428.51) * mm});
            skLineSegment(sketch, "E18.21.2.1", {"start": v(424.5, 412.7) * mm, "end": v(424.5, 428.51) * mm});
            skPoint(sketch, "E18.21.2.2", {"position": v(424.5, 410.7) * mm});
            skPoint(sketch, "E18.21.2.3", {"position": v(415.5, 410.7) * mm});
            skLineSegment(sketch, "E18.21.2.4", {"start": v(415.5, 428.51) * mm, "end": v(424.5, 428.51) * mm});
            skArc(sketch, "E18.21.2.5", {"start": v(415.5, 412.7) * mm, "mid": v(416.09, 411.28) * mm, "end": v(417.5, 410.7) * mm});
            skLineSegment(sketch, "E18.21.2.6", {"start": v(417.5, 410.7) * mm, "end": v(422.5, 410.7) * mm});
            skArc(sketch, "E18.21.2.7", {"start": v(422.5, 410.7) * mm, "mid": v(423.91, 411.28) * mm, "end": v(424.5, 412.7) * mm});
            skLineSegment(sketch, "E18.21.3.0", {"start": v(415.5, 378.05) * mm, "end": v(415.5, 393.87) * mm});
            skLineSegment(sketch, "E18.21.3.1", {"start": v(424.5, 378.05) * mm, "end": v(424.5, 393.87) * mm});
            skPoint(sketch, "E18.21.3.2", {"position": v(424.5, 376.05) * mm});
            skPoint(sketch, "E18.21.3.3", {"position": v(415.5, 376.05) * mm});
            skLineSegment(sketch, "E18.21.3.4", {"start": v(415.5, 393.87) * mm, "end": v(424.5, 393.87) * mm});
            skArc(sketch, "E18.21.3.5", {"start": v(415.5, 378.05) * mm, "mid": v(416.09, 376.64) * mm, "end": v(417.5, 376.05) * mm});
            skLineSegment(sketch, "E18.21.3.6", {"start": v(417.5, 376.05) * mm, "end": v(422.5, 376.05) * mm});
            skArc(sketch, "E18.21.3.7", {"start": v(422.5, 376.05) * mm, "mid": v(423.91, 376.64) * mm, "end": v(424.5, 378.05) * mm});
            skLineSegment(sketch, "E18.21.4.0", {"start": v(415.5, 343.41) * mm, "end": v(415.5, 359.23) * mm});
            skLineSegment(sketch, "E18.21.4.1", {"start": v(424.5, 343.41) * mm, "end": v(424.5, 359.23) * mm});
            skPoint(sketch, "E18.21.4.2", {"position": v(424.5, 341.41) * mm});
            skPoint(sketch, "E18.21.4.3", {"position": v(415.5, 341.41) * mm});
            skLineSegment(sketch, "E18.21.4.4", {"start": v(415.5, 359.23) * mm, "end": v(424.5, 359.23) * mm});
            skArc(sketch, "E18.21.4.5", {"start": v(415.5, 343.41) * mm, "mid": v(416.09, 342) * mm, "end": v(417.5, 341.41) * mm});
            skLineSegment(sketch, "E18.21.4.6", {"start": v(417.5, 341.41) * mm, "end": v(422.5, 341.41) * mm});
            skArc(sketch, "E18.21.4.7", {"start": v(422.5, 341.41) * mm, "mid": v(423.91, 342) * mm, "end": v(424.5, 343.41) * mm});
            skLineSegment(sketch, "E18.21.5.0", {"start": v(415.5, 308.77) * mm, "end": v(415.5, 324.59) * mm});
            skLineSegment(sketch, "E18.21.5.1", {"start": v(424.5, 308.77) * mm, "end": v(424.5, 324.59) * mm});
            skPoint(sketch, "E18.21.5.2", {"position": v(424.5, 306.77) * mm});
            skPoint(sketch, "E18.21.5.3", {"position": v(415.5, 306.77) * mm});
            skLineSegment(sketch, "E18.21.5.4", {"start": v(415.5, 324.59) * mm, "end": v(424.5, 324.59) * mm});
            skArc(sketch, "E18.21.5.5", {"start": v(415.5, 308.77) * mm, "mid": v(416.09, 307.35) * mm, "end": v(417.5, 306.77) * mm});
            skLineSegment(sketch, "E18.21.5.6", {"start": v(417.5, 306.77) * mm, "end": v(422.5, 306.77) * mm});
            skArc(sketch, "E18.21.5.7", {"start": v(422.5, 306.77) * mm, "mid": v(423.91, 307.35) * mm, "end": v(424.5, 308.77) * mm});
            skLineSegment(sketch, "E18.21.6.0", {"start": v(415.5, 274.13) * mm, "end": v(415.5, 289.95) * mm});
            skLineSegment(sketch, "E18.21.6.1", {"start": v(424.5, 274.13) * mm, "end": v(424.5, 289.95) * mm});
            skPoint(sketch, "E18.21.6.2", {"position": v(424.5, 272.13) * mm});
            skPoint(sketch, "E18.21.6.3", {"position": v(415.5, 272.13) * mm});
            skLineSegment(sketch, "E18.21.6.4", {"start": v(415.5, 289.95) * mm, "end": v(424.5, 289.95) * mm});
            skArc(sketch, "E18.21.6.5", {"start": v(415.5, 274.13) * mm, "mid": v(416.09, 272.71) * mm, "end": v(417.5, 272.13) * mm});
            skLineSegment(sketch, "E18.21.6.6", {"start": v(417.5, 272.13) * mm, "end": v(422.5, 272.13) * mm});
            skArc(sketch, "E18.21.6.7", {"start": v(422.5, 272.13) * mm, "mid": v(423.91, 272.71) * mm, "end": v(424.5, 274.13) * mm});
            skLineSegment(sketch, "E18.21.7.0", {"start": v(415.5, 239.49) * mm, "end": v(415.5, 255.3) * mm});
            skLineSegment(sketch, "E18.21.7.1", {"start": v(424.5, 239.49) * mm, "end": v(424.5, 255.3) * mm});
            skPoint(sketch, "E18.21.7.2", {"position": v(424.5, 237.49) * mm});
            skPoint(sketch, "E18.21.7.3", {"position": v(415.5, 237.49) * mm});
            skLineSegment(sketch, "E18.21.7.4", {"start": v(415.5, 255.3) * mm, "end": v(424.5, 255.3) * mm});
            skArc(sketch, "E18.21.7.5", {"start": v(415.5, 239.49) * mm, "mid": v(416.09, 238.07) * mm, "end": v(417.5, 237.49) * mm});
            skLineSegment(sketch, "E18.21.7.6", {"start": v(417.5, 237.49) * mm, "end": v(422.5, 237.49) * mm});
            skArc(sketch, "E18.21.7.7", {"start": v(422.5, 237.49) * mm, "mid": v(423.91, 238.07) * mm, "end": v(424.5, 239.49) * mm});
            skLineSegment(sketch, "E18.21.8.0", {"start": v(415.5, 204.85) * mm, "end": v(415.5, 220.67) * mm});
            skLineSegment(sketch, "E18.21.8.1", {"start": v(424.5, 204.85) * mm, "end": v(424.5, 220.67) * mm});
            skPoint(sketch, "E18.21.8.2", {"position": v(424.5, 202.85) * mm});
            skPoint(sketch, "E18.21.8.3", {"position": v(415.5, 202.85) * mm});
            skLineSegment(sketch, "E18.21.8.4", {"start": v(415.5, 220.67) * mm, "end": v(424.5, 220.67) * mm});
            skArc(sketch, "E18.21.8.5", {"start": v(415.5, 204.85) * mm, "mid": v(416.09, 203.43) * mm, "end": v(417.5, 202.85) * mm});
            skLineSegment(sketch, "E18.21.8.6", {"start": v(417.5, 202.85) * mm, "end": v(422.5, 202.85) * mm});
            skArc(sketch, "E18.21.8.7", {"start": v(422.5, 202.85) * mm, "mid": v(423.91, 203.43) * mm, "end": v(424.5, 204.85) * mm});
            skLineSegment(sketch, "E18.21.9.0", {"start": v(415.5, 170.2) * mm, "end": v(415.5, 186.03) * mm});
            skLineSegment(sketch, "E18.21.9.1", {"start": v(424.5, 170.2) * mm, "end": v(424.5, 186.03) * mm});
            skPoint(sketch, "E18.21.9.2", {"position": v(424.5, 168.2) * mm});
            skPoint(sketch, "E18.21.9.3", {"position": v(415.5, 168.2) * mm});
            skLineSegment(sketch, "E18.21.9.4", {"start": v(415.5, 186.03) * mm, "end": v(424.5, 186.03) * mm});
            skArc(sketch, "E18.21.9.5", {"start": v(415.5, 170.2) * mm, "mid": v(416.09, 168.8) * mm, "end": v(417.5, 168.2) * mm});
            skLineSegment(sketch, "E18.21.9.6", {"start": v(417.5, 168.2) * mm, "end": v(422.5, 168.2) * mm});
            skArc(sketch, "E18.21.9.7", {"start": v(422.5, 168.2) * mm, "mid": v(423.91, 168.8) * mm, "end": v(424.5, 170.2) * mm});
            skLineSegment(sketch, "E18.21.10.0", {"start": v(415.5, 135.56) * mm, "end": v(415.5, 151.38) * mm});
            skLineSegment(sketch, "E18.21.10.1", {"start": v(424.5, 135.56) * mm, "end": v(424.5, 151.38) * mm});
            skPoint(sketch, "E18.21.10.2", {"position": v(424.5, 133.56) * mm});
            skPoint(sketch, "E18.21.10.3", {"position": v(415.5, 133.56) * mm});
            skLineSegment(sketch, "E18.21.10.4", {"start": v(415.5, 151.38) * mm, "end": v(424.5, 151.38) * mm});
            skArc(sketch, "E18.21.10.5", {"start": v(415.5, 135.56) * mm, "mid": v(416.09, 134.15) * mm, "end": v(417.5, 133.56) * mm});
            skLineSegment(sketch, "E18.21.10.6", {"start": v(417.5, 133.56) * mm, "end": v(422.5, 133.56) * mm});
            skArc(sketch, "E18.21.10.7", {"start": v(422.5, 133.56) * mm, "mid": v(423.91, 134.15) * mm, "end": v(424.5, 135.56) * mm});
            skLineSegment(sketch, "E18.21.11.0", {"start": v(415.5, 100.92) * mm, "end": v(415.5, 116.74) * mm});
            skLineSegment(sketch, "E18.21.11.1", {"start": v(424.5, 100.92) * mm, "end": v(424.5, 116.74) * mm});
            skPoint(sketch, "E18.21.11.2", {"position": v(424.5, 98.92) * mm});
            skPoint(sketch, "E18.21.11.3", {"position": v(415.5, 98.92) * mm});
            skLineSegment(sketch, "E18.21.11.4", {"start": v(415.5, 116.74) * mm, "end": v(424.5, 116.74) * mm});
            skArc(sketch, "E18.21.11.5", {"start": v(415.5, 100.92) * mm, "mid": v(416.09, 99.5) * mm, "end": v(417.5, 98.92) * mm});
            skLineSegment(sketch, "E18.21.11.6", {"start": v(417.5, 98.92) * mm, "end": v(422.5, 98.92) * mm});
            skArc(sketch, "E18.21.11.7", {"start": v(422.5, 98.92) * mm, "mid": v(423.91, 99.5) * mm, "end": v(424.5, 100.92) * mm});
            skLineSegment(sketch, "E18.21.12.0", {"start": v(415.5, 66.28) * mm, "end": v(415.5, 82.1) * mm});
            skLineSegment(sketch, "E18.21.12.1", {"start": v(424.5, 66.28) * mm, "end": v(424.5, 82.1) * mm});
            skPoint(sketch, "E18.21.12.2", {"position": v(424.5, 64.28) * mm});
            skPoint(sketch, "E18.21.12.3", {"position": v(415.5, 64.28) * mm});
            skLineSegment(sketch, "E18.21.12.4", {"start": v(415.5, 82.1) * mm, "end": v(424.5, 82.1) * mm});
            skArc(sketch, "E18.21.12.5", {"start": v(415.5, 66.28) * mm, "mid": v(416.09, 64.87) * mm, "end": v(417.5, 64.28) * mm});
            skLineSegment(sketch, "E18.21.12.6", {"start": v(417.5, 64.28) * mm, "end": v(422.5, 64.28) * mm});
            skArc(sketch, "E18.21.12.7", {"start": v(422.5, 64.28) * mm, "mid": v(423.91, 64.87) * mm, "end": v(424.5, 66.28) * mm});
            skLineSegment(sketch, "E18.21.13.0", {"start": v(415.5, 31.64) * mm, "end": v(415.5, 47.46) * mm});
            skLineSegment(sketch, "E18.21.13.1", {"start": v(424.5, 31.64) * mm, "end": v(424.5, 47.46) * mm});
            skPoint(sketch, "E18.21.13.2", {"position": v(424.5, 29.64) * mm});
            skPoint(sketch, "E18.21.13.3", {"position": v(415.5, 29.64) * mm});
            skLineSegment(sketch, "E18.21.13.4", {"start": v(415.5, 47.46) * mm, "end": v(424.5, 47.46) * mm});
            skArc(sketch, "E18.21.13.5", {"start": v(415.5, 31.64) * mm, "mid": v(416.09, 30.23) * mm, "end": v(417.5, 29.64) * mm});
            skLineSegment(sketch, "E18.21.13.6", {"start": v(417.5, 29.64) * mm, "end": v(422.5, 29.64) * mm});
            skArc(sketch, "E18.21.13.7", {"start": v(422.5, 29.64) * mm, "mid": v(423.91, 30.23) * mm, "end": v(424.5, 31.64) * mm});
            skLineSegment(sketch, "E18.21.14.0", {"start": v(415.5, -3) * mm, "end": v(415.5, 12.82) * mm});
            skLineSegment(sketch, "E18.21.14.1", {"start": v(424.5, -3) * mm, "end": v(424.5, 12.82) * mm});
            skPoint(sketch, "E18.21.14.2", {"position": v(424.5, -5) * mm});
            skPoint(sketch, "E18.21.14.3", {"position": v(415.5, -5) * mm});
            skLineSegment(sketch, "E18.21.14.4", {"start": v(415.5, 12.82) * mm, "end": v(424.5, 12.82) * mm});
            skArc(sketch, "E18.21.14.5", {"start": v(415.5, -3) * mm, "mid": v(416.09, -4.41) * mm, "end": v(417.5, -5) * mm});
            skLineSegment(sketch, "E18.21.14.6", {"start": v(417.5, -5) * mm, "end": v(422.5, -5) * mm});
            skArc(sketch, "E18.21.14.7", {"start": v(422.5, -5) * mm, "mid": v(423.91, -4.41) * mm, "end": v(424.5, -3) * mm});
            skLineSegment(sketch, "E18.22.0.0", {"start": v(435.5, 481.97) * mm, "end": v(435.5, 497.8) * mm});
            skLineSegment(sketch, "E18.22.0.1", {"start": v(444.5, 481.97) * mm, "end": v(444.5, 497.8) * mm});
            skPoint(sketch, "E18.22.0.2", {"position": v(444.5, 479.97) * mm});
            skPoint(sketch, "E18.22.0.3", {"position": v(435.5, 479.97) * mm});
            skLineSegment(sketch, "E18.22.0.4", {"start": v(435.5, 497.8) * mm, "end": v(444.5, 497.8) * mm});
            skArc(sketch, "E18.22.0.5", {"start": v(435.5, 481.97) * mm, "mid": v(436.09, 480.56) * mm, "end": v(437.5, 479.97) * mm});
            skLineSegment(sketch, "E18.22.0.6", {"start": v(437.5, 479.97) * mm, "end": v(442.5, 479.97) * mm});
            skArc(sketch, "E18.22.0.7", {"start": v(442.5, 479.97) * mm, "mid": v(443.91, 480.56) * mm, "end": v(444.5, 481.97) * mm});
            skLineSegment(sketch, "E18.22.1.0", {"start": v(435.5, 447.33) * mm, "end": v(435.5, 463.15) * mm});
            skLineSegment(sketch, "E18.22.1.1", {"start": v(444.5, 447.33) * mm, "end": v(444.5, 463.15) * mm});
            skPoint(sketch, "E18.22.1.2", {"position": v(444.5, 445.33) * mm});
            skPoint(sketch, "E18.22.1.3", {"position": v(435.5, 445.33) * mm});
            skLineSegment(sketch, "E18.22.1.4", {"start": v(435.5, 463.15) * mm, "end": v(444.5, 463.15) * mm});
            skArc(sketch, "E18.22.1.5", {"start": v(435.5, 447.33) * mm, "mid": v(436.09, 445.92) * mm, "end": v(437.5, 445.33) * mm});
            skLineSegment(sketch, "E18.22.1.6", {"start": v(437.5, 445.33) * mm, "end": v(442.5, 445.33) * mm});
            skArc(sketch, "E18.22.1.7", {"start": v(442.5, 445.33) * mm, "mid": v(443.91, 445.92) * mm, "end": v(444.5, 447.33) * mm});
            skLineSegment(sketch, "E18.22.2.0", {"start": v(435.5, 412.7) * mm, "end": v(435.5, 428.51) * mm});
            skLineSegment(sketch, "E18.22.2.1", {"start": v(444.5, 412.7) * mm, "end": v(444.5, 428.51) * mm});
            skPoint(sketch, "E18.22.2.2", {"position": v(444.5, 410.7) * mm});
            skPoint(sketch, "E18.22.2.3", {"position": v(435.5, 410.7) * mm});
            skLineSegment(sketch, "E18.22.2.4", {"start": v(435.5, 428.51) * mm, "end": v(444.5, 428.51) * mm});
            skArc(sketch, "E18.22.2.5", {"start": v(435.5, 412.7) * mm, "mid": v(436.09, 411.28) * mm, "end": v(437.5, 410.7) * mm});
            skLineSegment(sketch, "E18.22.2.6", {"start": v(437.5, 410.7) * mm, "end": v(442.5, 410.7) * mm});
            skArc(sketch, "E18.22.2.7", {"start": v(442.5, 410.7) * mm, "mid": v(443.91, 411.28) * mm, "end": v(444.5, 412.7) * mm});
            skLineSegment(sketch, "E18.22.3.0", {"start": v(435.5, 378.05) * mm, "end": v(435.5, 393.87) * mm});
            skLineSegment(sketch, "E18.22.3.1", {"start": v(444.5, 378.05) * mm, "end": v(444.5, 393.87) * mm});
            skPoint(sketch, "E18.22.3.2", {"position": v(444.5, 376.05) * mm});
            skPoint(sketch, "E18.22.3.3", {"position": v(435.5, 376.05) * mm});
            skLineSegment(sketch, "E18.22.3.4", {"start": v(435.5, 393.87) * mm, "end": v(444.5, 393.87) * mm});
            skArc(sketch, "E18.22.3.5", {"start": v(435.5, 378.05) * mm, "mid": v(436.09, 376.64) * mm, "end": v(437.5, 376.05) * mm});
            skLineSegment(sketch, "E18.22.3.6", {"start": v(437.5, 376.05) * mm, "end": v(442.5, 376.05) * mm});
            skArc(sketch, "E18.22.3.7", {"start": v(442.5, 376.05) * mm, "mid": v(443.91, 376.64) * mm, "end": v(444.5, 378.05) * mm});
            skLineSegment(sketch, "E18.22.4.0", {"start": v(435.5, 343.41) * mm, "end": v(435.5, 359.23) * mm});
            skLineSegment(sketch, "E18.22.4.1", {"start": v(444.5, 343.41) * mm, "end": v(444.5, 359.23) * mm});
            skPoint(sketch, "E18.22.4.2", {"position": v(444.5, 341.41) * mm});
            skPoint(sketch, "E18.22.4.3", {"position": v(435.5, 341.41) * mm});
            skLineSegment(sketch, "E18.22.4.4", {"start": v(435.5, 359.23) * mm, "end": v(444.5, 359.23) * mm});
            skArc(sketch, "E18.22.4.5", {"start": v(435.5, 343.41) * mm, "mid": v(436.09, 342) * mm, "end": v(437.5, 341.41) * mm});
            skLineSegment(sketch, "E18.22.4.6", {"start": v(437.5, 341.41) * mm, "end": v(442.5, 341.41) * mm});
            skArc(sketch, "E18.22.4.7", {"start": v(442.5, 341.41) * mm, "mid": v(443.91, 342) * mm, "end": v(444.5, 343.41) * mm});
            skLineSegment(sketch, "E18.22.5.0", {"start": v(435.5, 308.77) * mm, "end": v(435.5, 324.59) * mm});
            skLineSegment(sketch, "E18.22.5.1", {"start": v(444.5, 308.77) * mm, "end": v(444.5, 324.59) * mm});
            skPoint(sketch, "E18.22.5.2", {"position": v(444.5, 306.77) * mm});
            skPoint(sketch, "E18.22.5.3", {"position": v(435.5, 306.77) * mm});
            skLineSegment(sketch, "E18.22.5.4", {"start": v(435.5, 324.59) * mm, "end": v(444.5, 324.59) * mm});
            skArc(sketch, "E18.22.5.5", {"start": v(435.5, 308.77) * mm, "mid": v(436.09, 307.35) * mm, "end": v(437.5, 306.77) * mm});
            skLineSegment(sketch, "E18.22.5.6", {"start": v(437.5, 306.77) * mm, "end": v(442.5, 306.77) * mm});
            skArc(sketch, "E18.22.5.7", {"start": v(442.5, 306.77) * mm, "mid": v(443.91, 307.35) * mm, "end": v(444.5, 308.77) * mm});
            skLineSegment(sketch, "E18.22.6.0", {"start": v(435.5, 274.13) * mm, "end": v(435.5, 289.95) * mm});
            skLineSegment(sketch, "E18.22.6.1", {"start": v(444.5, 274.13) * mm, "end": v(444.5, 289.95) * mm});
            skPoint(sketch, "E18.22.6.2", {"position": v(444.5, 272.13) * mm});
            skPoint(sketch, "E18.22.6.3", {"position": v(435.5, 272.13) * mm});
            skLineSegment(sketch, "E18.22.6.4", {"start": v(435.5, 289.95) * mm, "end": v(444.5, 289.95) * mm});
            skArc(sketch, "E18.22.6.5", {"start": v(435.5, 274.13) * mm, "mid": v(436.09, 272.71) * mm, "end": v(437.5, 272.13) * mm});
            skLineSegment(sketch, "E18.22.6.6", {"start": v(437.5, 272.13) * mm, "end": v(442.5, 272.13) * mm});
            skArc(sketch, "E18.22.6.7", {"start": v(442.5, 272.13) * mm, "mid": v(443.91, 272.71) * mm, "end": v(444.5, 274.13) * mm});
            skLineSegment(sketch, "E18.22.7.0", {"start": v(435.5, 239.49) * mm, "end": v(435.5, 255.3) * mm});
            skLineSegment(sketch, "E18.22.7.1", {"start": v(444.5, 239.49) * mm, "end": v(444.5, 255.3) * mm});
            skPoint(sketch, "E18.22.7.2", {"position": v(444.5, 237.49) * mm});
            skPoint(sketch, "E18.22.7.3", {"position": v(435.5, 237.49) * mm});
            skLineSegment(sketch, "E18.22.7.4", {"start": v(435.5, 255.3) * mm, "end": v(444.5, 255.3) * mm});
            skArc(sketch, "E18.22.7.5", {"start": v(435.5, 239.49) * mm, "mid": v(436.09, 238.07) * mm, "end": v(437.5, 237.49) * mm});
            skLineSegment(sketch, "E18.22.7.6", {"start": v(437.5, 237.49) * mm, "end": v(442.5, 237.49) * mm});
            skArc(sketch, "E18.22.7.7", {"start": v(442.5, 237.49) * mm, "mid": v(443.91, 238.07) * mm, "end": v(444.5, 239.49) * mm});
            skLineSegment(sketch, "E18.22.8.0", {"start": v(435.5, 204.85) * mm, "end": v(435.5, 220.67) * mm});
            skLineSegment(sketch, "E18.22.8.1", {"start": v(444.5, 204.85) * mm, "end": v(444.5, 220.67) * mm});
            skPoint(sketch, "E18.22.8.2", {"position": v(444.5, 202.85) * mm});
            skPoint(sketch, "E18.22.8.3", {"position": v(435.5, 202.85) * mm});
            skLineSegment(sketch, "E18.22.8.4", {"start": v(435.5, 220.67) * mm, "end": v(444.5, 220.67) * mm});
            skArc(sketch, "E18.22.8.5", {"start": v(435.5, 204.85) * mm, "mid": v(436.09, 203.43) * mm, "end": v(437.5, 202.85) * mm});
            skLineSegment(sketch, "E18.22.8.6", {"start": v(437.5, 202.85) * mm, "end": v(442.5, 202.85) * mm});
            skArc(sketch, "E18.22.8.7", {"start": v(442.5, 202.85) * mm, "mid": v(443.91, 203.43) * mm, "end": v(444.5, 204.85) * mm});
            skLineSegment(sketch, "E18.22.9.0", {"start": v(435.5, 170.2) * mm, "end": v(435.5, 186.03) * mm});
            skLineSegment(sketch, "E18.22.9.1", {"start": v(444.5, 170.2) * mm, "end": v(444.5, 186.03) * mm});
            skPoint(sketch, "E18.22.9.2", {"position": v(444.5, 168.2) * mm});
            skPoint(sketch, "E18.22.9.3", {"position": v(435.5, 168.2) * mm});
            skLineSegment(sketch, "E18.22.9.4", {"start": v(435.5, 186.03) * mm, "end": v(444.5, 186.03) * mm});
            skArc(sketch, "E18.22.9.5", {"start": v(435.5, 170.2) * mm, "mid": v(436.09, 168.8) * mm, "end": v(437.5, 168.2) * mm});
            skLineSegment(sketch, "E18.22.9.6", {"start": v(437.5, 168.2) * mm, "end": v(442.5, 168.2) * mm});
            skArc(sketch, "E18.22.9.7", {"start": v(442.5, 168.2) * mm, "mid": v(443.91, 168.8) * mm, "end": v(444.5, 170.2) * mm});
            skLineSegment(sketch, "E18.22.10.0", {"start": v(435.5, 135.56) * mm, "end": v(435.5, 151.38) * mm});
            skLineSegment(sketch, "E18.22.10.1", {"start": v(444.5, 135.56) * mm, "end": v(444.5, 151.38) * mm});
            skPoint(sketch, "E18.22.10.2", {"position": v(444.5, 133.56) * mm});
            skPoint(sketch, "E18.22.10.3", {"position": v(435.5, 133.56) * mm});
            skLineSegment(sketch, "E18.22.10.4", {"start": v(435.5, 151.38) * mm, "end": v(444.5, 151.38) * mm});
            skArc(sketch, "E18.22.10.5", {"start": v(435.5, 135.56) * mm, "mid": v(436.09, 134.15) * mm, "end": v(437.5, 133.56) * mm});
            skLineSegment(sketch, "E18.22.10.6", {"start": v(437.5, 133.56) * mm, "end": v(442.5, 133.56) * mm});
            skArc(sketch, "E18.22.10.7", {"start": v(442.5, 133.56) * mm, "mid": v(443.91, 134.15) * mm, "end": v(444.5, 135.56) * mm});
            skLineSegment(sketch, "E18.22.11.0", {"start": v(435.5, 100.92) * mm, "end": v(435.5, 116.74) * mm});
            skLineSegment(sketch, "E18.22.11.1", {"start": v(444.5, 100.92) * mm, "end": v(444.5, 116.74) * mm});
            skPoint(sketch, "E18.22.11.2", {"position": v(444.5, 98.92) * mm});
            skPoint(sketch, "E18.22.11.3", {"position": v(435.5, 98.92) * mm});
            skLineSegment(sketch, "E18.22.11.4", {"start": v(435.5, 116.74) * mm, "end": v(444.5, 116.74) * mm});
            skArc(sketch, "E18.22.11.5", {"start": v(435.5, 100.92) * mm, "mid": v(436.09, 99.5) * mm, "end": v(437.5, 98.92) * mm});
            skLineSegment(sketch, "E18.22.11.6", {"start": v(437.5, 98.92) * mm, "end": v(442.5, 98.92) * mm});
            skArc(sketch, "E18.22.11.7", {"start": v(442.5, 98.92) * mm, "mid": v(443.91, 99.5) * mm, "end": v(444.5, 100.92) * mm});
            skLineSegment(sketch, "E18.22.12.0", {"start": v(435.5, 66.28) * mm, "end": v(435.5, 82.1) * mm});
            skLineSegment(sketch, "E18.22.12.1", {"start": v(444.5, 66.28) * mm, "end": v(444.5, 82.1) * mm});
            skPoint(sketch, "E18.22.12.2", {"position": v(444.5, 64.28) * mm});
            skPoint(sketch, "E18.22.12.3", {"position": v(435.5, 64.28) * mm});
            skLineSegment(sketch, "E18.22.12.4", {"start": v(435.5, 82.1) * mm, "end": v(444.5, 82.1) * mm});
            skArc(sketch, "E18.22.12.5", {"start": v(435.5, 66.28) * mm, "mid": v(436.09, 64.87) * mm, "end": v(437.5, 64.28) * mm});
            skLineSegment(sketch, "E18.22.12.6", {"start": v(437.5, 64.28) * mm, "end": v(442.5, 64.28) * mm});
            skArc(sketch, "E18.22.12.7", {"start": v(442.5, 64.28) * mm, "mid": v(443.91, 64.87) * mm, "end": v(444.5, 66.28) * mm});
            skLineSegment(sketch, "E18.22.13.0", {"start": v(435.5, 31.64) * mm, "end": v(435.5, 47.46) * mm});
            skLineSegment(sketch, "E18.22.13.1", {"start": v(444.5, 31.64) * mm, "end": v(444.5, 47.46) * mm});
            skPoint(sketch, "E18.22.13.2", {"position": v(444.5, 29.64) * mm});
            skPoint(sketch, "E18.22.13.3", {"position": v(435.5, 29.64) * mm});
            skLineSegment(sketch, "E18.22.13.4", {"start": v(435.5, 47.46) * mm, "end": v(444.5, 47.46) * mm});
            skArc(sketch, "E18.22.13.5", {"start": v(435.5, 31.64) * mm, "mid": v(436.09, 30.23) * mm, "end": v(437.5, 29.64) * mm});
            skLineSegment(sketch, "E18.22.13.6", {"start": v(437.5, 29.64) * mm, "end": v(442.5, 29.64) * mm});
            skArc(sketch, "E18.22.13.7", {"start": v(442.5, 29.64) * mm, "mid": v(443.91, 30.23) * mm, "end": v(444.5, 31.64) * mm});
            skLineSegment(sketch, "E18.22.14.0", {"start": v(435.5, -3) * mm, "end": v(435.5, 12.82) * mm});
            skLineSegment(sketch, "E18.22.14.1", {"start": v(444.5, -3) * mm, "end": v(444.5, 12.82) * mm});
            skPoint(sketch, "E18.22.14.2", {"position": v(444.5, -5) * mm});
            skPoint(sketch, "E18.22.14.3", {"position": v(435.5, -5) * mm});
            skLineSegment(sketch, "E18.22.14.4", {"start": v(435.5, 12.82) * mm, "end": v(444.5, 12.82) * mm});
            skArc(sketch, "E18.22.14.5", {"start": v(435.5, -3) * mm, "mid": v(436.09, -4.41) * mm, "end": v(437.5, -5) * mm});
            skLineSegment(sketch, "E18.22.14.6", {"start": v(437.5, -5) * mm, "end": v(442.5, -5) * mm});
            skArc(sketch, "E18.22.14.7", {"start": v(442.5, -5) * mm, "mid": v(443.91, -4.41) * mm, "end": v(444.5, -3) * mm});
            skLineSegment(sketch, "E18.23.0.0", {"start": v(455.5, 481.97) * mm, "end": v(455.5, 497.8) * mm});
            skLineSegment(sketch, "E18.23.0.1", {"start": v(464.5, 481.97) * mm, "end": v(464.5, 497.8) * mm});
            skPoint(sketch, "E18.23.0.2", {"position": v(464.5, 479.97) * mm});
            skPoint(sketch, "E18.23.0.3", {"position": v(455.5, 479.97) * mm});
            skLineSegment(sketch, "E18.23.0.4", {"start": v(455.5, 497.8) * mm, "end": v(464.5, 497.8) * mm});
            skArc(sketch, "E18.23.0.5", {"start": v(455.5, 481.97) * mm, "mid": v(456.09, 480.56) * mm, "end": v(457.5, 479.97) * mm});
            skLineSegment(sketch, "E18.23.0.6", {"start": v(457.5, 479.97) * mm, "end": v(462.5, 479.97) * mm});
            skArc(sketch, "E18.23.0.7", {"start": v(462.5, 479.97) * mm, "mid": v(463.91, 480.56) * mm, "end": v(464.5, 481.97) * mm});
            skLineSegment(sketch, "E18.23.1.0", {"start": v(455.5, 447.33) * mm, "end": v(455.5, 463.15) * mm});
            skLineSegment(sketch, "E18.23.1.1", {"start": v(464.5, 447.33) * mm, "end": v(464.5, 463.15) * mm});
            skPoint(sketch, "E18.23.1.2", {"position": v(464.5, 445.33) * mm});
            skPoint(sketch, "E18.23.1.3", {"position": v(455.5, 445.33) * mm});
            skLineSegment(sketch, "E18.23.1.4", {"start": v(455.5, 463.15) * mm, "end": v(464.5, 463.15) * mm});
            skArc(sketch, "E18.23.1.5", {"start": v(455.5, 447.33) * mm, "mid": v(456.09, 445.92) * mm, "end": v(457.5, 445.33) * mm});
            skLineSegment(sketch, "E18.23.1.6", {"start": v(457.5, 445.33) * mm, "end": v(462.5, 445.33) * mm});
            skArc(sketch, "E18.23.1.7", {"start": v(462.5, 445.33) * mm, "mid": v(463.91, 445.92) * mm, "end": v(464.5, 447.33) * mm});
            skLineSegment(sketch, "E18.23.2.0", {"start": v(455.5, 412.7) * mm, "end": v(455.5, 428.51) * mm});
            skLineSegment(sketch, "E18.23.2.1", {"start": v(464.5, 412.7) * mm, "end": v(464.5, 428.51) * mm});
            skPoint(sketch, "E18.23.2.2", {"position": v(464.5, 410.7) * mm});
            skPoint(sketch, "E18.23.2.3", {"position": v(455.5, 410.7) * mm});
            skLineSegment(sketch, "E18.23.2.4", {"start": v(455.5, 428.51) * mm, "end": v(464.5, 428.51) * mm});
            skArc(sketch, "E18.23.2.5", {"start": v(455.5, 412.7) * mm, "mid": v(456.09, 411.28) * mm, "end": v(457.5, 410.7) * mm});
            skLineSegment(sketch, "E18.23.2.6", {"start": v(457.5, 410.7) * mm, "end": v(462.5, 410.7) * mm});
            skArc(sketch, "E18.23.2.7", {"start": v(462.5, 410.7) * mm, "mid": v(463.91, 411.28) * mm, "end": v(464.5, 412.7) * mm});
            skLineSegment(sketch, "E18.23.3.0", {"start": v(455.5, 378.05) * mm, "end": v(455.5, 393.87) * mm});
            skLineSegment(sketch, "E18.23.3.1", {"start": v(464.5, 378.05) * mm, "end": v(464.5, 393.87) * mm});
            skPoint(sketch, "E18.23.3.2", {"position": v(464.5, 376.05) * mm});
            skPoint(sketch, "E18.23.3.3", {"position": v(455.5, 376.05) * mm});
            skLineSegment(sketch, "E18.23.3.4", {"start": v(455.5, 393.87) * mm, "end": v(464.5, 393.87) * mm});
            skArc(sketch, "E18.23.3.5", {"start": v(455.5, 378.05) * mm, "mid": v(456.09, 376.64) * mm, "end": v(457.5, 376.05) * mm});
            skLineSegment(sketch, "E18.23.3.6", {"start": v(457.5, 376.05) * mm, "end": v(462.5, 376.05) * mm});
            skArc(sketch, "E18.23.3.7", {"start": v(462.5, 376.05) * mm, "mid": v(463.91, 376.64) * mm, "end": v(464.5, 378.05) * mm});
            skLineSegment(sketch, "E18.23.4.0", {"start": v(455.5, 343.41) * mm, "end": v(455.5, 359.23) * mm});
            skLineSegment(sketch, "E18.23.4.1", {"start": v(464.5, 343.41) * mm, "end": v(464.5, 359.23) * mm});
            skPoint(sketch, "E18.23.4.2", {"position": v(464.5, 341.41) * mm});
            skPoint(sketch, "E18.23.4.3", {"position": v(455.5, 341.41) * mm});
            skLineSegment(sketch, "E18.23.4.4", {"start": v(455.5, 359.23) * mm, "end": v(464.5, 359.23) * mm});
            skArc(sketch, "E18.23.4.5", {"start": v(455.5, 343.41) * mm, "mid": v(456.09, 342) * mm, "end": v(457.5, 341.41) * mm});
            skLineSegment(sketch, "E18.23.4.6", {"start": v(457.5, 341.41) * mm, "end": v(462.5, 341.41) * mm});
            skArc(sketch, "E18.23.4.7", {"start": v(462.5, 341.41) * mm, "mid": v(463.91, 342) * mm, "end": v(464.5, 343.41) * mm});
            skLineSegment(sketch, "E18.23.5.0", {"start": v(455.5, 308.77) * mm, "end": v(455.5, 324.59) * mm});
            skLineSegment(sketch, "E18.23.5.1", {"start": v(464.5, 308.77) * mm, "end": v(464.5, 324.59) * mm});
            skPoint(sketch, "E18.23.5.2", {"position": v(464.5, 306.77) * mm});
            skPoint(sketch, "E18.23.5.3", {"position": v(455.5, 306.77) * mm});
            skLineSegment(sketch, "E18.23.5.4", {"start": v(455.5, 324.59) * mm, "end": v(464.5, 324.59) * mm});
            skArc(sketch, "E18.23.5.5", {"start": v(455.5, 308.77) * mm, "mid": v(456.09, 307.35) * mm, "end": v(457.5, 306.77) * mm});
            skLineSegment(sketch, "E18.23.5.6", {"start": v(457.5, 306.77) * mm, "end": v(462.5, 306.77) * mm});
            skArc(sketch, "E18.23.5.7", {"start": v(462.5, 306.77) * mm, "mid": v(463.91, 307.35) * mm, "end": v(464.5, 308.77) * mm});
            skLineSegment(sketch, "E18.23.6.0", {"start": v(455.5, 274.13) * mm, "end": v(455.5, 289.95) * mm});
            skLineSegment(sketch, "E18.23.6.1", {"start": v(464.5, 274.13) * mm, "end": v(464.5, 289.95) * mm});
            skPoint(sketch, "E18.23.6.2", {"position": v(464.5, 272.13) * mm});
            skPoint(sketch, "E18.23.6.3", {"position": v(455.5, 272.13) * mm});
            skLineSegment(sketch, "E18.23.6.4", {"start": v(455.5, 289.95) * mm, "end": v(464.5, 289.95) * mm});
            skArc(sketch, "E18.23.6.5", {"start": v(455.5, 274.13) * mm, "mid": v(456.09, 272.71) * mm, "end": v(457.5, 272.13) * mm});
            skLineSegment(sketch, "E18.23.6.6", {"start": v(457.5, 272.13) * mm, "end": v(462.5, 272.13) * mm});
            skArc(sketch, "E18.23.6.7", {"start": v(462.5, 272.13) * mm, "mid": v(463.91, 272.71) * mm, "end": v(464.5, 274.13) * mm});
            skLineSegment(sketch, "E18.23.7.0", {"start": v(455.5, 239.49) * mm, "end": v(455.5, 255.3) * mm});
            skLineSegment(sketch, "E18.23.7.1", {"start": v(464.5, 239.49) * mm, "end": v(464.5, 255.3) * mm});
            skPoint(sketch, "E18.23.7.2", {"position": v(464.5, 237.49) * mm});
            skPoint(sketch, "E18.23.7.3", {"position": v(455.5, 237.49) * mm});
            skLineSegment(sketch, "E18.23.7.4", {"start": v(455.5, 255.3) * mm, "end": v(464.5, 255.3) * mm});
            skArc(sketch, "E18.23.7.5", {"start": v(455.5, 239.49) * mm, "mid": v(456.09, 238.07) * mm, "end": v(457.5, 237.49) * mm});
            skLineSegment(sketch, "E18.23.7.6", {"start": v(457.5, 237.49) * mm, "end": v(462.5, 237.49) * mm});
            skArc(sketch, "E18.23.7.7", {"start": v(462.5, 237.49) * mm, "mid": v(463.91, 238.07) * mm, "end": v(464.5, 239.49) * mm});
            skLineSegment(sketch, "E18.23.8.0", {"start": v(455.5, 204.85) * mm, "end": v(455.5, 220.67) * mm});
            skLineSegment(sketch, "E18.23.8.1", {"start": v(464.5, 204.85) * mm, "end": v(464.5, 220.67) * mm});
            skPoint(sketch, "E18.23.8.2", {"position": v(464.5, 202.85) * mm});
            skPoint(sketch, "E18.23.8.3", {"position": v(455.5, 202.85) * mm});
            skLineSegment(sketch, "E18.23.8.4", {"start": v(455.5, 220.67) * mm, "end": v(464.5, 220.67) * mm});
            skArc(sketch, "E18.23.8.5", {"start": v(455.5, 204.85) * mm, "mid": v(456.09, 203.43) * mm, "end": v(457.5, 202.85) * mm});
            skLineSegment(sketch, "E18.23.8.6", {"start": v(457.5, 202.85) * mm, "end": v(462.5, 202.85) * mm});
            skArc(sketch, "E18.23.8.7", {"start": v(462.5, 202.85) * mm, "mid": v(463.91, 203.43) * mm, "end": v(464.5, 204.85) * mm});
            skLineSegment(sketch, "E18.23.9.0", {"start": v(455.5, 170.2) * mm, "end": v(455.5, 186.03) * mm});
            skLineSegment(sketch, "E18.23.9.1", {"start": v(464.5, 170.2) * mm, "end": v(464.5, 186.03) * mm});
            skPoint(sketch, "E18.23.9.2", {"position": v(464.5, 168.2) * mm});
            skPoint(sketch, "E18.23.9.3", {"position": v(455.5, 168.2) * mm});
            skLineSegment(sketch, "E18.23.9.4", {"start": v(455.5, 186.03) * mm, "end": v(464.5, 186.03) * mm});
            skArc(sketch, "E18.23.9.5", {"start": v(455.5, 170.2) * mm, "mid": v(456.09, 168.8) * mm, "end": v(457.5, 168.2) * mm});
            skLineSegment(sketch, "E18.23.9.6", {"start": v(457.5, 168.2) * mm, "end": v(462.5, 168.2) * mm});
            skArc(sketch, "E18.23.9.7", {"start": v(462.5, 168.2) * mm, "mid": v(463.91, 168.8) * mm, "end": v(464.5, 170.2) * mm});
            skLineSegment(sketch, "E18.23.10.0", {"start": v(455.5, 135.56) * mm, "end": v(455.5, 151.38) * mm});
            skLineSegment(sketch, "E18.23.10.1", {"start": v(464.5, 135.56) * mm, "end": v(464.5, 151.38) * mm});
            skPoint(sketch, "E18.23.10.2", {"position": v(464.5, 133.56) * mm});
            skPoint(sketch, "E18.23.10.3", {"position": v(455.5, 133.56) * mm});
            skLineSegment(sketch, "E18.23.10.4", {"start": v(455.5, 151.38) * mm, "end": v(464.5, 151.38) * mm});
            skArc(sketch, "E18.23.10.5", {"start": v(455.5, 135.56) * mm, "mid": v(456.09, 134.15) * mm, "end": v(457.5, 133.56) * mm});
            skLineSegment(sketch, "E18.23.10.6", {"start": v(457.5, 133.56) * mm, "end": v(462.5, 133.56) * mm});
            skArc(sketch, "E18.23.10.7", {"start": v(462.5, 133.56) * mm, "mid": v(463.91, 134.15) * mm, "end": v(464.5, 135.56) * mm});
            skLineSegment(sketch, "E18.23.11.0", {"start": v(455.5, 100.92) * mm, "end": v(455.5, 116.74) * mm});
            skLineSegment(sketch, "E18.23.11.1", {"start": v(464.5, 100.92) * mm, "end": v(464.5, 116.74) * mm});
            skPoint(sketch, "E18.23.11.2", {"position": v(464.5, 98.92) * mm});
            skPoint(sketch, "E18.23.11.3", {"position": v(455.5, 98.92) * mm});
            skLineSegment(sketch, "E18.23.11.4", {"start": v(455.5, 116.74) * mm, "end": v(464.5, 116.74) * mm});
            skArc(sketch, "E18.23.11.5", {"start": v(455.5, 100.92) * mm, "mid": v(456.09, 99.5) * mm, "end": v(457.5, 98.92) * mm});
            skLineSegment(sketch, "E18.23.11.6", {"start": v(457.5, 98.92) * mm, "end": v(462.5, 98.92) * mm});
            skArc(sketch, "E18.23.11.7", {"start": v(462.5, 98.92) * mm, "mid": v(463.91, 99.5) * mm, "end": v(464.5, 100.92) * mm});
            skLineSegment(sketch, "E18.23.12.0", {"start": v(455.5, 66.28) * mm, "end": v(455.5, 82.1) * mm});
            skLineSegment(sketch, "E18.23.12.1", {"start": v(464.5, 66.28) * mm, "end": v(464.5, 82.1) * mm});
            skPoint(sketch, "E18.23.12.2", {"position": v(464.5, 64.28) * mm});
            skPoint(sketch, "E18.23.12.3", {"position": v(455.5, 64.28) * mm});
            skLineSegment(sketch, "E18.23.12.4", {"start": v(455.5, 82.1) * mm, "end": v(464.5, 82.1) * mm});
            skArc(sketch, "E18.23.12.5", {"start": v(455.5, 66.28) * mm, "mid": v(456.09, 64.87) * mm, "end": v(457.5, 64.28) * mm});
            skLineSegment(sketch, "E18.23.12.6", {"start": v(457.5, 64.28) * mm, "end": v(462.5, 64.28) * mm});
            skArc(sketch, "E18.23.12.7", {"start": v(462.5, 64.28) * mm, "mid": v(463.91, 64.87) * mm, "end": v(464.5, 66.28) * mm});
            skLineSegment(sketch, "E18.23.13.0", {"start": v(455.5, 31.64) * mm, "end": v(455.5, 47.46) * mm});
            skLineSegment(sketch, "E18.23.13.1", {"start": v(464.5, 31.64) * mm, "end": v(464.5, 47.46) * mm});
            skPoint(sketch, "E18.23.13.2", {"position": v(464.5, 29.64) * mm});
            skPoint(sketch, "E18.23.13.3", {"position": v(455.5, 29.64) * mm});
            skLineSegment(sketch, "E18.23.13.4", {"start": v(455.5, 47.46) * mm, "end": v(464.5, 47.46) * mm});
            skArc(sketch, "E18.23.13.5", {"start": v(455.5, 31.64) * mm, "mid": v(456.09, 30.23) * mm, "end": v(457.5, 29.64) * mm});
            skLineSegment(sketch, "E18.23.13.6", {"start": v(457.5, 29.64) * mm, "end": v(462.5, 29.64) * mm});
            skArc(sketch, "E18.23.13.7", {"start": v(462.5, 29.64) * mm, "mid": v(463.91, 30.23) * mm, "end": v(464.5, 31.64) * mm});
            skLineSegment(sketch, "E18.23.14.0", {"start": v(455.5, -3) * mm, "end": v(455.5, 12.82) * mm});
            skLineSegment(sketch, "E18.23.14.1", {"start": v(464.5, -3) * mm, "end": v(464.5, 12.82) * mm});
            skPoint(sketch, "E18.23.14.2", {"position": v(464.5, -5) * mm});
            skPoint(sketch, "E18.23.14.3", {"position": v(455.5, -5) * mm});
            skLineSegment(sketch, "E18.23.14.4", {"start": v(455.5, 12.82) * mm, "end": v(464.5, 12.82) * mm});
            skArc(sketch, "E18.23.14.5", {"start": v(455.5, -3) * mm, "mid": v(456.09, -4.41) * mm, "end": v(457.5, -5) * mm});
            skLineSegment(sketch, "E18.23.14.6", {"start": v(457.5, -5) * mm, "end": v(462.5, -5) * mm});
            skArc(sketch, "E18.23.14.7", {"start": v(462.5, -5) * mm, "mid": v(463.91, -4.41) * mm, "end": v(464.5, -3) * mm});
            skLineSegment(sketch, "E18.direction1", {"start": v(-4.5, 479.97) * mm, "end": v(15.5, 479.97) * mm, "construction": true});
            skLineSegment(sketch, "E18.direction2", {"start": v(-4.5, 479.97) * mm, "end": v(-4.5, 445.33) * mm, "construction": true});
            skSolve(sketch);
        }
        {
            var Q0;
            Q0=qSketchRegion(id+"F6",true);
            extrude(context, id + "F7", {"entities" : qUnion([Q0]), "operationType" : NewBodyOperationType.REMOVE, "oppositeDirection" : true, "depth" : 2 * mm});
        }
    });
